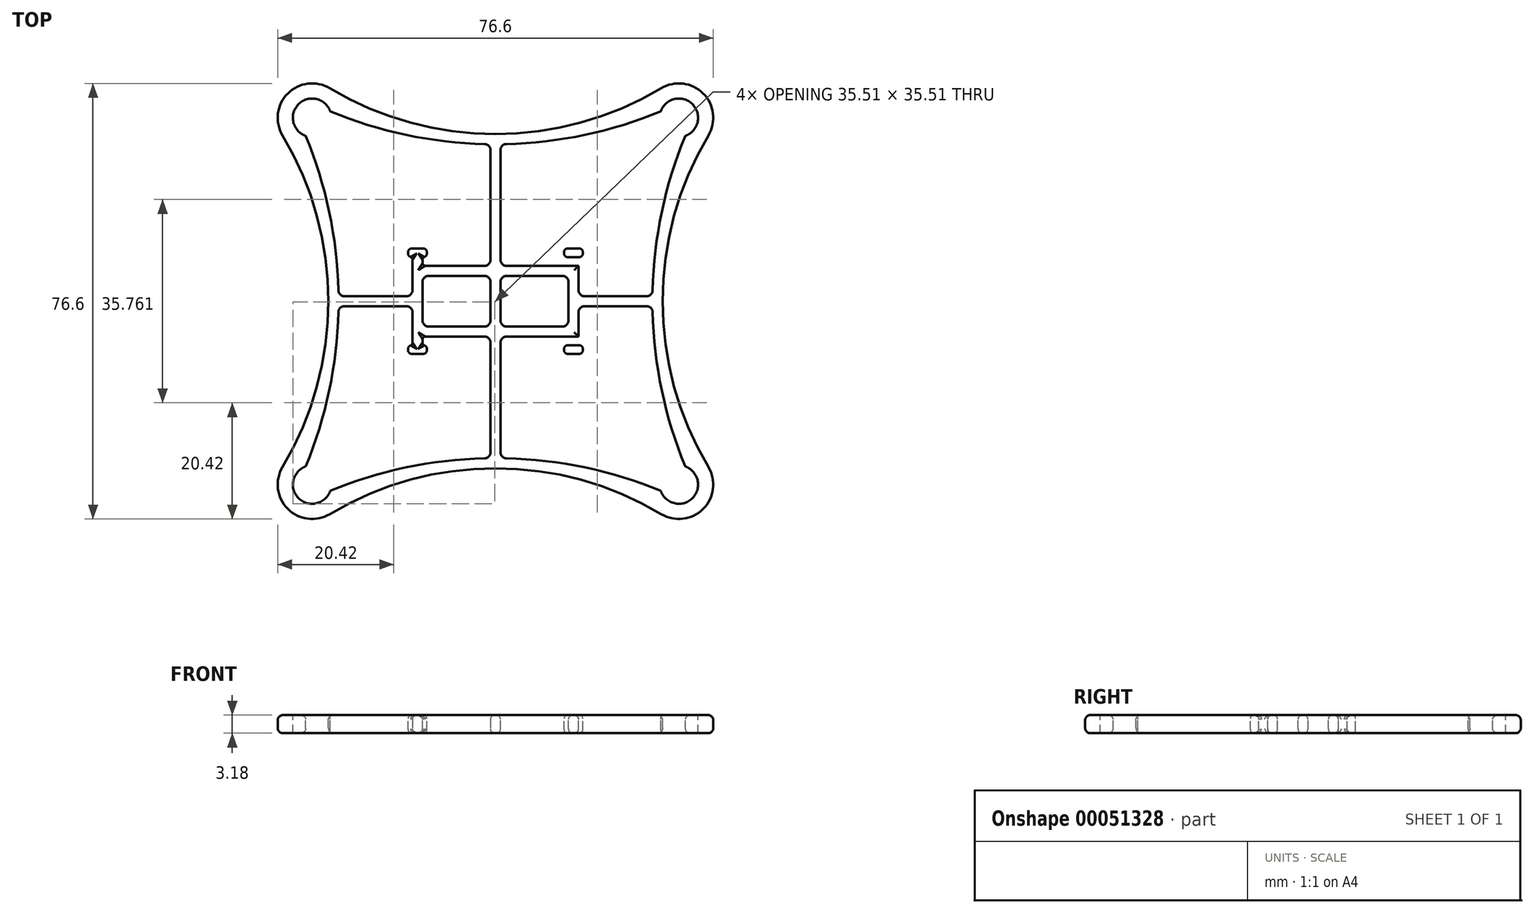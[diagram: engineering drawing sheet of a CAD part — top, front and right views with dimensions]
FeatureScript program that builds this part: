
annotation { "Feature Type Name" : "Feature", "Feature Type Description" : "" }
export const myFeature = defineFeature(function(context is Context, id is Id, definition is map)
    precondition{}
    {
        {
            var Q0;
            Q0=qCreatedBy(makeId("Top.planeOp"),FACE);
            var sketch = newSketch(context, id + "F0", { "sketchPlane" : qUnion([Q0])});
            skCircle(sketch, "E0", {"center": v(-32.26, 32.26) * mm, "radius": 3.38 * mm});
            skCircle(sketch, "E1", {"center": v(32.26, 32.26) * mm, "radius": 3.38 * mm});
            skCircle(sketch, "E2", {"center": v(32.26, -32.26) * mm, "radius": 3.38 * mm});
            skCircle(sketch, "E3", {"center": v(-32.26, -32.26) * mm, "radius": 3.38 * mm});
            skCircle(sketch, "E4", {"center": v(-32.26, 32.26) * mm, "radius": 6.05 * mm});
            skCircle(sketch, "E5", {"center": v(-32.26, -32.26) * mm, "radius": 6.05 * mm});
            skCircle(sketch, "E6", {"center": v(32.26, -32.26) * mm, "radius": 6.05 * mm});
            skCircle(sketch, "E7", {"center": v(32.26, 32.26) * mm, "radius": 6.05 * mm});
            skCircle(sketch, "E8", {"center": v(-103.8, 0) * mm, "radius": 76.2 * mm});
            skCircle(sketch, "E9", {"center": v(-86.16, 0) * mm, "radius": 56.77 * mm});
            skCircle(sketch, "E10", {"center": v(0, 103.8) * mm, "radius": 76.2 * mm});
            skCircle(sketch, "E11", {"center": v(0, 86.16) * mm, "radius": 56.77 * mm});
            skCircle(sketch, "E12", {"center": v(103.8, 0) * mm, "radius": 76.2 * mm});
            skCircle(sketch, "E13", {"center": v(86.16, 0) * mm, "radius": 56.77 * mm});
            skCircle(sketch, "E14", {"center": v(0, -103.8) * mm, "radius": 76.2 * mm});
            skCircle(sketch, "E15", {"center": v(0, -86.16) * mm, "radius": 56.77 * mm});
            skPoint(sketch, "E16.rect.middle", {"position": v(0, 0) * mm});
            skLineSegment(sketch, "E17.rect.bottom", {"start": v(14.6, 6.22) * mm, "end": v(-14.6, 6.22) * mm});
            skLineSegment(sketch, "E17.rect.top", {"start": v(14.6, -6.22) * mm, "end": v(-14.6, -6.22) * mm});
            skLineSegment(sketch, "E17.rect.left", {"start": v(14.6, 6.22) * mm, "end": v(14.6, -6.22) * mm});
            skLineSegment(sketch, "E17.rect.right", {"start": v(-14.6, 6.22) * mm, "end": v(-14.6, -6.22) * mm});
            skLineSegment(sketch, "E18.rect.bottom", {"start": v(12.83, 4.44) * mm, "end": v(-12.83, 4.45) * mm});
            skLineSegment(sketch, "E18.rect.top", {"start": v(12.83, -4.45) * mm, "end": v(-12.83, -4.44) * mm});
            skLineSegment(sketch, "E18.rect.left", {"start": v(12.83, 4.44) * mm, "end": v(12.83, -4.45) * mm});
            skLineSegment(sketch, "E18.rect.right", {"start": v(-12.83, 4.45) * mm, "end": v(-12.83, -4.44) * mm});
            skLineSegment(sketch, "E19.rect.bottom", {"start": v(0.89, 29.4) * mm, "end": v(-0.89, 29.4) * mm});
            skLineSegment(sketch, "E19.rect.top", {"start": v(0.89, -29.4) * mm, "end": v(-0.89, -29.4) * mm});
            skLineSegment(sketch, "E19.rect.left", {"start": v(0.89, 29.4) * mm, "end": v(0.89, -29.4) * mm});
            skLineSegment(sketch, "E19.rect.right", {"start": v(-0.89, 29.4) * mm, "end": v(-0.89, -29.4) * mm});
            skLineSegment(sketch, "E20.rect.bottom", {"start": v(29.4, 0.89) * mm, "end": v(-29.4, 0.89) * mm});
            skLineSegment(sketch, "E20.rect.top", {"start": v(29.4, -0.89) * mm, "end": v(-29.4, -0.89) * mm});
            skLineSegment(sketch, "E20.rect.left", {"start": v(29.4, 0.89) * mm, "end": v(29.4, -0.89) * mm});
            skLineSegment(sketch, "E20.rect.right", {"start": v(-29.4, 0.89) * mm, "end": v(-29.4, -0.89) * mm});
            skLineSegment(sketch, "E21.left", {"start": v(14.6, 6.22) * mm, "end": v(14.6, 6.22) * mm});
            skLineSegment(sketch, "E22.left", {"start": v(14.6, -6.22) * mm, "end": v(14.6, -6.22) * mm});
            skLineSegment(sketch, "E23.bottom", {"start": v(-14.6, 6.22) * mm, "end": v(-12.83, 6.22) * mm});
            skLineSegment(sketch, "E23.top", {"start": v(-14.6, 8.5) * mm, "end": v(-12.83, 8.5) * mm});
            skLineSegment(sketch, "E23.left", {"start": v(-14.6, 6.22) * mm, "end": v(-14.6, 8.5) * mm});
            skLineSegment(sketch, "E23.right", {"start": v(-12.83, 6.22) * mm, "end": v(-12.83, 8.5) * mm});
            skLineSegment(sketch, "E24.bottom", {"start": v(-14.6, -6.22) * mm, "end": v(-12.83, -6.22) * mm});
            skLineSegment(sketch, "E24.top", {"start": v(-14.6, -8.5) * mm, "end": v(-12.83, -8.5) * mm});
            skLineSegment(sketch, "E24.left", {"start": v(-14.6, -6.22) * mm, "end": v(-14.6, -8.5) * mm});
            skLineSegment(sketch, "E24.right", {"start": v(-12.83, -6.22) * mm, "end": v(-12.83, -8.5) * mm});
            skLineSegment(sketch, "E25.bottom", {"start": v(14.6, -6.22) * mm, "end": v(12.83, -6.22) * mm});
            skLineSegment(sketch, "E25.top", {"start": v(14.6, -8.5) * mm, "end": v(12.83, -8.5) * mm});
            skLineSegment(sketch, "E25.left", {"start": v(14.6, -6.22) * mm, "end": v(14.6, -8.5) * mm});
            skLineSegment(sketch, "E25.right", {"start": v(12.83, -6.22) * mm, "end": v(12.83, -8.5) * mm});
            skLineSegment(sketch, "E26.bottom", {"start": v(14.6, 6.22) * mm, "end": v(12.83, 6.22) * mm});
            skLineSegment(sketch, "E26.top", {"start": v(14.6, 8.5) * mm, "end": v(12.83, 8.5) * mm});
            skLineSegment(sketch, "E26.left", {"start": v(14.6, 6.22) * mm, "end": v(14.6, 8.5) * mm});
            skLineSegment(sketch, "E26.right", {"start": v(12.83, 6.22) * mm, "end": v(12.83, 8.5) * mm});
            skLineSegment(sketch, "E27.rect.bottom", {"start": v(-12.06, 9.27) * mm, "end": v(-15.37, 9.27) * mm});
            skLineSegment(sketch, "E27.rect.top", {"start": v(-12.06, 7.75) * mm, "end": v(-15.37, 7.75) * mm});
            skLineSegment(sketch, "E27.rect.left", {"start": v(-12.06, 9.27) * mm, "end": v(-12.06, 7.75) * mm});
            skLineSegment(sketch, "E27.rect.right", {"start": v(-15.37, 9.27) * mm, "end": v(-15.37, 7.75) * mm});
            skPoint(sketch, "E27.rect.middle", {"position": v(-13.72, 8.5) * mm});
            skLineSegment(sketch, "E28.rect.bottom", {"start": v(12.07, 9.27) * mm, "end": v(15.37, 9.27) * mm});
            skLineSegment(sketch, "E28.rect.top", {"start": v(12.07, 7.75) * mm, "end": v(15.37, 7.75) * mm});
            skLineSegment(sketch, "E28.rect.left", {"start": v(12.07, 9.27) * mm, "end": v(12.07, 7.75) * mm});
            skLineSegment(sketch, "E28.rect.right", {"start": v(15.37, 9.27) * mm, "end": v(15.37, 7.75) * mm});
            skPoint(sketch, "E28.rect.middle", {"position": v(13.72, 8.5) * mm});
            skLineSegment(sketch, "E29.rect.bottom", {"start": v(12.07, -7.75) * mm, "end": v(15.37, -7.75) * mm});
            skLineSegment(sketch, "E29.rect.top", {"start": v(12.07, -9.27) * mm, "end": v(15.37, -9.27) * mm});
            skLineSegment(sketch, "E29.rect.left", {"start": v(12.07, -7.75) * mm, "end": v(12.07, -9.27) * mm});
            skLineSegment(sketch, "E29.rect.right", {"start": v(15.37, -7.75) * mm, "end": v(15.37, -9.27) * mm});
            skPoint(sketch, "E29.rect.middle", {"position": v(13.72, -8.5) * mm});
            skLineSegment(sketch, "E30.rect.bottom", {"start": v(-12.06, -9.27) * mm, "end": v(-15.37, -9.27) * mm});
            skLineSegment(sketch, "E30.rect.top", {"start": v(-12.06, -7.75) * mm, "end": v(-15.37, -7.75) * mm});
            skLineSegment(sketch, "E30.rect.left", {"start": v(-12.06, -9.27) * mm, "end": v(-12.06, -7.75) * mm});
            skLineSegment(sketch, "E30.rect.right", {"start": v(-15.37, -9.27) * mm, "end": v(-15.37, -7.75) * mm});
            skPoint(sketch, "E30.rect.middle", {"position": v(-13.72, -8.5) * mm});
            skSolve(sketch);
        }
        {
            var Q0;
            {var subQ3=sQuery(id+"F0.wireOp",EDGE,"E4");var subQ5=sQuery(id+"F0.wireOp",EDGE,"E9");var subQ7=makeQuery(id+"F0.imprint","INTERSECT",VERTEX,{"derivedFrom":[subQ3,subQ5]});Q0=makeQuery(id+"F0.imprint","IMPRINT",FACE,{"disambiguationData":[TD([[makeQuery(id+"F0.imprint","IMPRINT",EDGE,{"disambiguationData":[TD([[subQ7,-1.0]])],"derivedFrom":subQ3}),-1.0]])]});}
            var Q1;
            {var subQ0=sQuery(id+"F0.wireOp",EDGE,"E8");var subQ1=sQuery(id+"F0.wireOp",EDGE,"E0");var subQ2=makeQuery(id+"F0.imprint","INTERSECT",VERTEX,{"disambiguationData":[OD(0.0)],"derivedFrom":[subQ1,subQ0]});Q1=makeQuery(id+"F0.imprint","IMPRINT",FACE,{"disambiguationData":[TD([[makeQuery(id+"F0.imprint","IMPRINT",EDGE,{"disambiguationData":[TD([[subQ2,-1.0]])],"derivedFrom":subQ1}),-1.0]])]});}
            var Q2;
            {var subQ0=sQuery(id+"F0.wireOp",EDGE,"E10");var subQ1=sQuery(id+"F0.wireOp",EDGE,"E0");var subQ2=makeQuery(id+"F0.imprint","INTERSECT",VERTEX,{"disambiguationData":[OD(0.0)],"derivedFrom":[subQ1,subQ0]});Q2=makeQuery(id+"F0.imprint","IMPRINT",FACE,{"disambiguationData":[TD([[makeQuery(id+"F0.imprint","IMPRINT",EDGE,{"disambiguationData":[TD([[subQ2,-1.0]])],"derivedFrom":subQ1}),-1.0]])]});}
            var Q3;
            {var subQ0=sQuery(id+"F0.wireOp",EDGE,"E0");var subQ1=sQuery(id+"F0.wireOp",EDGE,"E10");var subQ3=makeQuery(id+"F0.imprint","INTERSECT",VERTEX,{"disambiguationData":[OD(0.0)],"derivedFrom":[subQ0,subQ1]});Q3=makeQuery(id+"F0.imprint","IMPRINT",FACE,{"disambiguationData":[TD([[makeQuery(id+"F0.imprint","IMPRINT",EDGE,{"disambiguationData":[TD([[subQ3,1.0]])],"derivedFrom":subQ0}),-1.0]])]});}
            var Q4;
            {var subQ0=sQuery(id+"F0.wireOp",EDGE,"E11");var subQ3=sQuery(id+"F0.wireOp",EDGE,"E4");var subQ4=makeQuery(id+"F0.imprint","INTERSECT",VERTEX,{"derivedFrom":[subQ3,subQ0]});Q4=makeQuery(id+"F0.imprint","IMPRINT",FACE,{"disambiguationData":[TD([[makeQuery(id+"F0.imprint","IMPRINT",EDGE,{"disambiguationData":[TD([[subQ4,1.0]])],"derivedFrom":subQ3}),-1.0]])]});}
            var Q5;
            {var subQ0=sQuery(id+"F0.wireOp",EDGE,"E10");var subQ1=sQuery(id+"F0.wireOp",EDGE,"E1");var subQ5=makeQuery(id+"F0.imprint","INTERSECT",VERTEX,{"disambiguationData":[OD(0.0)],"derivedFrom":[subQ1,subQ0]});Q5=makeQuery(id+"F0.imprint","IMPRINT",FACE,{"disambiguationData":[TD([[makeQuery(id+"F0.imprint","IMPRINT",EDGE,{"disambiguationData":[TD([[subQ5,1.0]])],"derivedFrom":subQ1}),-1.0]])]});}
            var Q6;
            {var subQ1=sQuery(id+"F0.wireOp",EDGE,"E1");var subQ5=sQuery(id+"F0.wireOp",EDGE,"E10");var subQ6=makeQuery(id+"F0.imprint","INTERSECT",VERTEX,{"disambiguationData":[OD(1.0)],"derivedFrom":[subQ1,subQ5]});Q6=makeQuery(id+"F0.imprint","IMPRINT",FACE,{"disambiguationData":[TD([[makeQuery(id+"F0.imprint","IMPRINT",EDGE,{"disambiguationData":[TD([[subQ6,1.0]])],"derivedFrom":subQ1}),-1.0]])]});}
            var Q7;
            {var subQ0=sQuery(id+"F0.wireOp",EDGE,"E12");var subQ3=sQuery(id+"F0.wireOp",EDGE,"E1");var subQ4=makeQuery(id+"F0.imprint","INTERSECT",VERTEX,{"disambiguationData":[OD(0.0)],"derivedFrom":[subQ3,subQ0]});Q7=makeQuery(id+"F0.imprint","IMPRINT",FACE,{"disambiguationData":[TD([[makeQuery(id+"F0.imprint","IMPRINT",EDGE,{"disambiguationData":[TD([[subQ4,-1.0]])],"derivedFrom":subQ3}),-1.0]])]});}
            var Q8;
            {var subQ0=sQuery(id+"F0.wireOp",EDGE,"E12");var subQ1=sQuery(id+"F0.wireOp",EDGE,"E2");var subQ5=makeQuery(id+"F0.imprint","INTERSECT",VERTEX,{"disambiguationData":[OD(0.0)],"derivedFrom":[subQ1,subQ0]});Q8=makeQuery(id+"F0.imprint","IMPRINT",FACE,{"disambiguationData":[TD([[makeQuery(id+"F0.imprint","IMPRINT",EDGE,{"disambiguationData":[TD([[subQ5,1.0]])],"derivedFrom":subQ1}),-1.0]])]});}
            var Q9;
            {var subQ0=sQuery(id+"F0.wireOp",EDGE,"E12");var subQ1=sQuery(id+"F0.wireOp",EDGE,"E2");var subQ2=makeQuery(id+"F0.imprint","INTERSECT",VERTEX,{"disambiguationData":[OD(1.0)],"derivedFrom":[subQ1,subQ0]});Q9=makeQuery(id+"F0.imprint","IMPRINT",FACE,{"disambiguationData":[TD([[makeQuery(id+"F0.imprint","IMPRINT",EDGE,{"disambiguationData":[TD([[subQ2,1.0]])],"derivedFrom":subQ1}),-1.0]])]});}
            var Q10;
            {var subQ0=sQuery(id+"F0.wireOp",EDGE,"E14");var subQ3=sQuery(id+"F0.wireOp",EDGE,"E2");var subQ4=makeQuery(id+"F0.imprint","INTERSECT",VERTEX,{"disambiguationData":[OD(0.0)],"derivedFrom":[subQ3,subQ0]});Q10=makeQuery(id+"F0.imprint","IMPRINT",FACE,{"disambiguationData":[TD([[makeQuery(id+"F0.imprint","IMPRINT",EDGE,{"disambiguationData":[TD([[subQ4,-1.0]])],"derivedFrom":subQ3}),-1.0]])]});}
            var Q11;
            {var subQ0=sQuery(id+"F0.wireOp",EDGE,"E3");var subQ1=sQuery(id+"F0.wireOp",EDGE,"E14");var subQ3=makeQuery(id+"F0.imprint","INTERSECT",VERTEX,{"disambiguationData":[OD(0.0)],"derivedFrom":[subQ0,subQ1]});Q11=makeQuery(id+"F0.imprint","IMPRINT",FACE,{"disambiguationData":[TD([[makeQuery(id+"F0.imprint","IMPRINT",EDGE,{"disambiguationData":[TD([[subQ3,-1.0]])],"derivedFrom":subQ0}),-1.0]])]});}
            var Q12;
            {var subQ1=sQuery(id+"F0.wireOp",EDGE,"E3");var subQ5=sQuery(id+"F0.wireOp",EDGE,"E8");var subQ7=makeQuery(id+"F0.imprint","INTERSECT",VERTEX,{"disambiguationData":[OD(0.0)],"derivedFrom":[subQ1,subQ5]});Q12=makeQuery(id+"F0.imprint","IMPRINT",FACE,{"disambiguationData":[TD([[makeQuery(id+"F0.imprint","IMPRINT",EDGE,{"disambiguationData":[TD([[subQ7,-1.0]])],"derivedFrom":subQ1}),-1.0]])]});}
            var Q13;
            {var subQ0=sQuery(id+"F0.wireOp",EDGE,"E8");var subQ3=sQuery(id+"F0.wireOp",EDGE,"E3");var subQ5=makeQuery(id+"F0.imprint","INTERSECT",VERTEX,{"disambiguationData":[OD(0.0)],"derivedFrom":[subQ3,subQ0]});Q13=makeQuery(id+"F0.imprint","IMPRINT",FACE,{"disambiguationData":[TD([[makeQuery(id+"F0.imprint","IMPRINT",EDGE,{"disambiguationData":[TD([[subQ5,1.0]])],"derivedFrom":subQ3}),-1.0]])]});}
            var Q14;
            {var subQ0=sQuery(id+"F0.wireOp",EDGE,"E12");var subQ3=sQuery(id+"F0.wireOp",EDGE,"E1");var subQ6=makeQuery(id+"F0.imprint","INTERSECT",VERTEX,{"disambiguationData":[OD(0.0)],"derivedFrom":[subQ3,subQ0]});Q14=makeQuery(id+"F0.imprint","IMPRINT",FACE,{"disambiguationData":[TD([[makeQuery(id+"F0.imprint","IMPRINT",EDGE,{"disambiguationData":[TD([[subQ6,1.0]])],"derivedFrom":subQ3}),-1.0]])]});}
            var Q15;
            {var subQ3=sQuery(id+"F0.wireOp",EDGE,"E6");var subQ5=sQuery(id+"F0.wireOp",EDGE,"E12");var subQ7=makeQuery(id+"F0.imprint","INTERSECT",VERTEX,{"disambiguationData":[OD(0.0)],"derivedFrom":[subQ3,subQ5]});Q15=makeQuery(id+"F0.imprint","IMPRINT",FACE,{"disambiguationData":[TD([[makeQuery(id+"F0.imprint","IMPRINT",EDGE,{"disambiguationData":[TD([[subQ7,1.0]])],"derivedFrom":subQ3}),-1.0]])]});}
            var Q16;
            {var subQ0=sQuery(id+"F0.wireOp",EDGE,"97792d4c-2e40-4aaa-a942-c1651c489ece.rect.left");var subQ6=sQuery(id+"F0.wireOp",EDGE,"E17.rect.bottom");var subQ7=makeQuery(id+"F0.imprint","INTERSECT",VERTEX,{"derivedFrom":[subQ0,subQ6]});Q16=makeQuery(id+"F0.imprint","IMPRINT",FACE,{"disambiguationData":[TD([[makeQuery(id+"F0.imprint","IMPRINT",EDGE,{"disambiguationData":[TD([[subQ7,-1.0]])],"derivedFrom":subQ6}),-1.0]])]});}
            var Q17;
            {var subQ3=sQuery(id+"F0.wireOp",EDGE,"E16.rect.bottom");var subQ9=sQuery(id+"F0.wireOp",EDGE,"E18.rect.right");var subQ11=makeQuery(id+"F0.imprint","INTERSECT",VERTEX,{"derivedFrom":[subQ3,subQ9]});Q17=makeQuery(id+"F0.imprint","IMPRINT",FACE,{"disambiguationData":[TD([[makeQuery(id+"F0.imprint","IMPRINT",EDGE,{"disambiguationData":[TD([[subQ11,-1.0]])],"derivedFrom":subQ3}),-1.0]])]});}
            var Q18;
            {var subQ0=sQuery(id+"F0.wireOp",EDGE,"E17.rect.bottom");var subQ1=sQuery(id+"F0.wireOp",EDGE,"97792d4c-2e40-4aaa-a942-c1651c489ece.rect.left");var subQ2=makeQuery(id+"F0.imprint","INTERSECT",VERTEX,{"derivedFrom":[subQ1,subQ0]});Q18=makeQuery(id+"F0.imprint","IMPRINT",FACE,{"disambiguationData":[TD([[makeQuery(id+"F0.imprint","IMPRINT",EDGE,{"disambiguationData":[TD([[subQ2,-1.0]])],"derivedFrom":subQ1}),-1.0]])]});}
            var Q19;
            {var subQ0=sQuery(id+"F0.wireOp",EDGE,"E17.rect.left");var subQ3=sQuery(id+"F0.wireOp",EDGE,"E16.rect.bottom");var subQ4=makeQuery(id+"F0.imprint","INTERSECT",VERTEX,{"derivedFrom":[subQ3,subQ0]});Q19=makeQuery(id+"F0.imprint","IMPRINT",FACE,{"disambiguationData":[TD([[makeQuery(id+"F0.imprint","IMPRINT",EDGE,{"disambiguationData":[TD([[subQ4,-1.0]])],"derivedFrom":subQ3}),-1.0]])]});}
            var Q20;
            {var subQ0=sQuery(id+"F0.wireOp",EDGE,"E17.rect.left");var subQ1=sQuery(id+"F0.wireOp",EDGE,"E16.rect.bottom");var subQ2=makeQuery(id+"F0.imprint","INTERSECT",VERTEX,{"derivedFrom":[subQ1,subQ0]});Q20=makeQuery(id+"F0.imprint","IMPRINT",FACE,{"disambiguationData":[TD([[makeQuery(id+"F0.imprint","IMPRINT",EDGE,{"disambiguationData":[TD([[subQ2,-1.0]])],"derivedFrom":subQ1}),1.0]])]});}
            var Q21;
            {var subQ0=sQuery(id+"F0.wireOp",EDGE,"E17.rect.left");var subQ3=sQuery(id+"F0.wireOp",EDGE,"E16.rect.top");var subQ4=makeQuery(id+"F0.imprint","INTERSECT",VERTEX,{"derivedFrom":[subQ3,subQ0]});Q21=makeQuery(id+"F0.imprint","IMPRINT",FACE,{"disambiguationData":[TD([[makeQuery(id+"F0.imprint","IMPRINT",EDGE,{"disambiguationData":[TD([[subQ4,-1.0]])],"derivedFrom":subQ3}),1.0]])]});}
            var Q22;
            {var subQ0=sQuery(id+"F0.wireOp",EDGE,"E18.rect.top");var subQ1=sQuery(id+"F0.wireOp",EDGE,"97792d4c-2e40-4aaa-a942-c1651c489ece.rect.left");var subQ2=makeQuery(id+"F0.imprint","INTERSECT",VERTEX,{"derivedFrom":[subQ1,subQ0]});Q22=makeQuery(id+"F0.imprint","IMPRINT",FACE,{"disambiguationData":[TD([[makeQuery(id+"F0.imprint","IMPRINT",EDGE,{"disambiguationData":[TD([[subQ2,-1.0]])],"derivedFrom":subQ1}),-1.0]])]});}
            var Q23;
            {var subQ5=sQuery(id+"F0.wireOp",EDGE,"E16.rect.top");var subQ9=sQuery(id+"F0.wireOp",EDGE,"E18.rect.right");var subQ11=makeQuery(id+"F0.imprint","INTERSECT",VERTEX,{"derivedFrom":[subQ5,subQ9]});Q23=makeQuery(id+"F0.imprint","IMPRINT",FACE,{"disambiguationData":[TD([[makeQuery(id+"F0.imprint","IMPRINT",EDGE,{"disambiguationData":[TD([[subQ11,-1.0]])],"derivedFrom":subQ5}),1.0]])]});}
            var Q24;
            {var subQ0=sQuery(id+"F0.wireOp",EDGE,"E18.rect.right");var subQ1=sQuery(id+"F0.wireOp",EDGE,"E16.rect.bottom");var subQ2=makeQuery(id+"F0.imprint","INTERSECT",VERTEX,{"derivedFrom":[subQ1,subQ0]});Q24=makeQuery(id+"F0.imprint","IMPRINT",FACE,{"disambiguationData":[TD([[makeQuery(id+"F0.imprint","IMPRINT",EDGE,{"disambiguationData":[TD([[subQ2,-1.0]])],"derivedFrom":subQ1}),1.0]])]});}
            var Q25;
            {var subQ1=sQuery(id+"F0.wireOp",EDGE,"E16.rect.bottom");var subQ6=sQuery(id+"F0.wireOp",EDGE,"E17.rect.right");var subQ7=makeQuery(id+"F0.imprint","INTERSECT",VERTEX,{"derivedFrom":[subQ1,subQ6]});Q25=makeQuery(id+"F0.imprint","IMPRINT",FACE,{"disambiguationData":[TD([[makeQuery(id+"F0.imprint","IMPRINT",EDGE,{"disambiguationData":[TD([[subQ7,-1.0]])],"derivedFrom":subQ6}),-1.0]])]});}
            var Q26;
            {var subQ1=sQuery(id+"F0.wireOp",EDGE,"E16.rect.bottom");var subQ6=sQuery(id+"F0.wireOp",EDGE,"E17.rect.left");var subQ7=makeQuery(id+"F0.imprint","INTERSECT",VERTEX,{"derivedFrom":[subQ1,subQ6]});Q26=makeQuery(id+"F0.imprint","IMPRINT",FACE,{"disambiguationData":[TD([[makeQuery(id+"F0.imprint","IMPRINT",EDGE,{"disambiguationData":[TD([[subQ7,-1.0]])],"derivedFrom":subQ6}),1.0]])]});}
            var Q27;
            {var subQ0=sQuery(id+"F0.wireOp",EDGE,"97792d4c-2e40-4aaa-a942-c1651c489ece.rect.left");var subQ6=sQuery(id+"F0.wireOp",EDGE,"E17.rect.top");var subQ7=makeQuery(id+"F0.imprint","INTERSECT",VERTEX,{"derivedFrom":[subQ0,subQ6]});Q27=makeQuery(id+"F0.imprint","IMPRINT",FACE,{"disambiguationData":[TD([[makeQuery(id+"F0.imprint","IMPRINT",EDGE,{"disambiguationData":[TD([[subQ7,-1.0]])],"derivedFrom":subQ6}),1.0]])]});}
            var Q28;
            Q28=makeQuery(id+"F0.imprint","IMPRINT",FACE,{"disambiguationData":[TD([[makeQuery(id+"F0.imprint","IMPRINT",EDGE,{"derivedFrom":sQuery(id+"F0.wireOp",EDGE,"de616939-67df-4de1-98a8-b123298b16c6.bottom")}),-1.0]])]});
            var Q29;
            Q29=makeQuery(id+"F0.imprint","IMPRINT",FACE,{"disambiguationData":[TD([[makeQuery(id+"F0.imprint","IMPRINT",EDGE,{"derivedFrom":sQuery(id+"F0.wireOp",EDGE,"6e18662c-c205-4df8-b961-8c52012f615d.bottom")}),1.0]])]});
            var Q30;
            Q30=makeQuery(id+"F0.imprint","IMPRINT",FACE,{"disambiguationData":[TD([[makeQuery(id+"F0.imprint","IMPRINT",EDGE,{"derivedFrom":sQuery(id+"F0.wireOp",EDGE,"e5e8593a-10a3-4d83-983c-bc6820abb37f.bottom")}),-1.0]])]});
            var Q31;
            Q31=makeQuery(id+"F0.imprint","IMPRINT",FACE,{"disambiguationData":[TD([[makeQuery(id+"F0.imprint","IMPRINT",EDGE,{"derivedFrom":sQuery(id+"F0.wireOp",EDGE,"fe4e9a62-022c-4ccf-87c7-29a0906fb106.bottom")}),1.0]])]});
            var Q32;
            {var subQ0=sQuery(id+"F0.wireOp",EDGE,"E20.rect.bottom");var subQ1=sQuery(id+"F0.wireOp",EDGE,"E8");var subQ2=makeQuery(id+"F0.imprint","INTERSECT",VERTEX,{"derivedFrom":[subQ1,subQ0]});Q32=makeQuery(id+"F0.imprint","IMPRINT",FACE,{"disambiguationData":[TD([[makeQuery(id+"F0.imprint","IMPRINT",EDGE,{"disambiguationData":[TD([[subQ2,1.0]])],"derivedFrom":subQ1}),1.0]])]});}
            var Q33;
            {var subQ0=sQuery(id+"F0.wireOp",EDGE,"E8");var subQ1=sQuery(id+"F0.wireOp",EDGE,"E5");var subQ2=makeQuery(id+"F0.imprint","INTERSECT",VERTEX,{"disambiguationData":[OD(0.0)],"derivedFrom":[subQ1,subQ0]});Q33=makeQuery(id+"F0.imprint","IMPRINT",FACE,{"disambiguationData":[TD([[makeQuery(id+"F0.imprint","IMPRINT",EDGE,{"disambiguationData":[TD([[subQ2,-1.0]])],"derivedFrom":subQ1}),-1.0]])]});}
            var Q34;
            {var subQ0=sQuery(id+"F0.wireOp",EDGE,"E19.rect.left");var subQ1=sQuery(id+"F0.wireOp",EDGE,"E14");var subQ2=makeQuery(id+"F0.imprint","INTERSECT",VERTEX,{"derivedFrom":[subQ1,subQ0]});Q34=makeQuery(id+"F0.imprint","IMPRINT",FACE,{"disambiguationData":[TD([[makeQuery(id+"F0.imprint","IMPRINT",EDGE,{"disambiguationData":[TD([[subQ2,-1.0]])],"derivedFrom":subQ1}),1.0]])]});}
            var Q35;
            {var subQ0=sQuery(id+"F0.wireOp",EDGE,"E14");var subQ1=sQuery(id+"F0.wireOp",EDGE,"E6");var subQ2=makeQuery(id+"F0.imprint","INTERSECT",VERTEX,{"disambiguationData":[OD(0.0)],"derivedFrom":[subQ1,subQ0]});Q35=makeQuery(id+"F0.imprint","IMPRINT",FACE,{"disambiguationData":[TD([[makeQuery(id+"F0.imprint","IMPRINT",EDGE,{"disambiguationData":[TD([[subQ2,-1.0]])],"derivedFrom":subQ1}),-1.0]])]});}
            var Q36;
            {var subQ0=sQuery(id+"F0.wireOp",EDGE,"E20.rect.bottom");var subQ1=sQuery(id+"F0.wireOp",EDGE,"E12");var subQ2=makeQuery(id+"F0.imprint","INTERSECT",VERTEX,{"derivedFrom":[subQ1,subQ0]});Q36=makeQuery(id+"F0.imprint","IMPRINT",FACE,{"disambiguationData":[TD([[makeQuery(id+"F0.imprint","IMPRINT",EDGE,{"disambiguationData":[TD([[subQ2,-1.0]])],"derivedFrom":subQ1}),1.0]])]});}
            var Q37;
            {var subQ7=sQuery(id+"F0.wireOp",EDGE,"E17.rect.left");var subQ8=sQuery(id+"F0.wireOp",EDGE,"E17.rect.top");var subQ9=makeQuery(id+"F0.imprint","INTERSECT",VERTEX,{"derivedFrom":[subQ8,subQ7]});Q37=makeQuery(id+"F0.imprint","IMPRINT",FACE,{"disambiguationData":[TD([[makeQuery(id+"F0.imprint","IMPRINT",EDGE,{"disambiguationData":[TD([[subQ9,-1.0]])],"derivedFrom":subQ8}),-1.0]])]});}
            var Q38;
            {var subQ0=sQuery(id+"F0.wireOp",EDGE,"E19.rect.left");var subQ1=sQuery(id+"F0.wireOp",EDGE,"E17.rect.top");var subQ2=makeQuery(id+"F0.imprint","INTERSECT",VERTEX,{"derivedFrom":[subQ1,subQ0]});Q38=makeQuery(id+"F0.imprint","IMPRINT",FACE,{"disambiguationData":[TD([[makeQuery(id+"F0.imprint","IMPRINT",EDGE,{"disambiguationData":[TD([[subQ2,-1.0]])],"derivedFrom":subQ1}),-1.0]])]});}
            var Q39;
            {var subQ5=sQuery(id+"F0.wireOp",EDGE,"E17.rect.top");var subQ7=sQuery(id+"F0.wireOp",EDGE,"E17.rect.right");var subQ8=makeQuery(id+"F0.imprint","INTERSECT",VERTEX,{"derivedFrom":[subQ5,subQ7]});Q39=makeQuery(id+"F0.imprint","IMPRINT",FACE,{"disambiguationData":[TD([[makeQuery(id+"F0.imprint","IMPRINT",EDGE,{"disambiguationData":[TD([[subQ8,1.0]])],"derivedFrom":subQ5}),-1.0]])]});}
            var Q40;
            {var subQ0=sQuery(id+"F0.wireOp",EDGE,"E20.rect.bottom");var subQ1=sQuery(id+"F0.wireOp",EDGE,"E17.rect.right");var subQ2=makeQuery(id+"F0.imprint","INTERSECT",VERTEX,{"derivedFrom":[subQ1,subQ0]});Q40=makeQuery(id+"F0.imprint","IMPRINT",FACE,{"disambiguationData":[TD([[makeQuery(id+"F0.imprint","IMPRINT",EDGE,{"disambiguationData":[TD([[subQ2,-1.0]])],"derivedFrom":subQ1}),1.0]])]});}
            var Q41;
            {var subQ7=sQuery(id+"F0.wireOp",EDGE,"E17.rect.right");var subQ8=sQuery(id+"F0.wireOp",EDGE,"E17.rect.bottom");var subQ9=makeQuery(id+"F0.imprint","INTERSECT",VERTEX,{"derivedFrom":[subQ8,subQ7]});Q41=makeQuery(id+"F0.imprint","IMPRINT",FACE,{"disambiguationData":[TD([[makeQuery(id+"F0.imprint","IMPRINT",EDGE,{"disambiguationData":[TD([[subQ9,1.0]])],"derivedFrom":subQ8}),1.0]])]});}
            var Q42;
            {var subQ7=sQuery(id+"F0.wireOp",EDGE,"E17.rect.left");var subQ8=sQuery(id+"F0.wireOp",EDGE,"E17.rect.bottom");var subQ9=makeQuery(id+"F0.imprint","INTERSECT",VERTEX,{"derivedFrom":[subQ8,subQ7]});Q42=makeQuery(id+"F0.imprint","IMPRINT",FACE,{"disambiguationData":[TD([[makeQuery(id+"F0.imprint","IMPRINT",EDGE,{"disambiguationData":[TD([[subQ9,-1.0]])],"derivedFrom":subQ8}),1.0]])]});}
            var Q43;
            {var subQ0=sQuery(id+"F0.wireOp",EDGE,"E20.rect.bottom");var subQ1=sQuery(id+"F0.wireOp",EDGE,"E17.rect.left");var subQ2=makeQuery(id+"F0.imprint","INTERSECT",VERTEX,{"derivedFrom":[subQ1,subQ0]});Q43=makeQuery(id+"F0.imprint","IMPRINT",FACE,{"disambiguationData":[TD([[makeQuery(id+"F0.imprint","IMPRINT",EDGE,{"disambiguationData":[TD([[subQ2,-1.0]])],"derivedFrom":subQ1}),-1.0]])]});}
            var Q44;
            {var subQ0=sQuery(id+"F0.wireOp",EDGE,"E12");var subQ1=sQuery(id+"F0.wireOp",EDGE,"E7");var subQ2=makeQuery(id+"F0.imprint","INTERSECT",VERTEX,{"disambiguationData":[OD(1.0)],"derivedFrom":[subQ1,subQ0]});Q44=makeQuery(id+"F0.imprint","IMPRINT",FACE,{"disambiguationData":[TD([[makeQuery(id+"F0.imprint","IMPRINT",EDGE,{"disambiguationData":[TD([[subQ2,-1.0]])],"derivedFrom":subQ1}),-1.0]])]});}
            var Q45;
            {var subQ0=sQuery(id+"F0.wireOp",EDGE,"E19.rect.left");var subQ1=sQuery(id+"F0.wireOp",EDGE,"E17.rect.bottom");var subQ2=makeQuery(id+"F0.imprint","INTERSECT",VERTEX,{"derivedFrom":[subQ1,subQ0]});Q45=makeQuery(id+"F0.imprint","IMPRINT",FACE,{"disambiguationData":[TD([[makeQuery(id+"F0.imprint","IMPRINT",EDGE,{"disambiguationData":[TD([[subQ2,-1.0]])],"derivedFrom":subQ1}),1.0]])]});}
            var Q46;
            {var subQ0=sQuery(id+"F0.wireOp",EDGE,"E19.rect.right");var subQ1=sQuery(id+"F0.wireOp",EDGE,"E10");var subQ2=makeQuery(id+"F0.imprint","INTERSECT",VERTEX,{"derivedFrom":[subQ1,subQ0]});Q46=makeQuery(id+"F0.imprint","IMPRINT",FACE,{"disambiguationData":[TD([[makeQuery(id+"F0.imprint","IMPRINT",EDGE,{"disambiguationData":[TD([[subQ2,-1.0]])],"derivedFrom":subQ1}),1.0]])]});}
            var Q47;
            {var subQ0=sQuery(id+"F0.wireOp",EDGE,"E11");var subQ1=sQuery(id+"F0.wireOp",EDGE,"E7");var subQ2=makeQuery(id+"F0.imprint","INTERSECT",VERTEX,{"derivedFrom":[subQ1,subQ0]});Q47=makeQuery(id+"F0.imprint","IMPRINT",FACE,{"disambiguationData":[TD([[makeQuery(id+"F0.imprint","IMPRINT",EDGE,{"disambiguationData":[TD([[subQ2,-1.0]])],"derivedFrom":subQ1}),-1.0]])]});}
            var Q48;
            {var subQ7=sQuery(id+"F0.wireOp",EDGE,"f8660cd2-9a3a-46cf-8541-a55b21bbf2a2.left");Q48=makeQuery(id+"F0.imprint","IMPRINT",FACE,{"disambiguationData":[TD([[makeQuery(id+"F0.imprint","IMPRINT",EDGE,{"derivedFrom":subQ7}),1.0]])]});}
            var Q49;
            Q49=makeQuery(id+"F0.imprint","IMPRINT",FACE,{"disambiguationData":[TD([[makeQuery(id+"F0.imprint","IMPRINT",EDGE,{"derivedFrom":sQuery(id+"F0.wireOp",EDGE,"f8660cd2-9a3a-46cf-8541-a55b21bbf2a2.bottom")}),1.0]])]});
            var Q50;
            Q50=makeQuery(id+"F0.imprint","IMPRINT",FACE,{"disambiguationData":[TD([[makeQuery(id+"F0.imprint","IMPRINT",EDGE,{"derivedFrom":sQuery(id+"F0.wireOp",EDGE,"2a5b0057-8150-4ec5-9247-2ce1087ea529.bottom")}),-1.0]])]});
            var Q51;
            {var subQ7=sQuery(id+"F0.wireOp",EDGE,"2a5b0057-8150-4ec5-9247-2ce1087ea529.left");Q51=makeQuery(id+"F0.imprint","IMPRINT",FACE,{"disambiguationData":[TD([[makeQuery(id+"F0.imprint","IMPRINT",EDGE,{"derivedFrom":subQ7}),-1.0]])]});}
            var Q52;
            {var subQ7=sQuery(id+"F0.wireOp",EDGE,"E22.left");Q52=makeQuery(id+"F0.imprint","IMPRINT",FACE,{"disambiguationData":[TD([[makeQuery(id+"F0.imprint","IMPRINT",EDGE,{"derivedFrom":subQ7}),1.0]])]});}
            var Q53;
            Q53=makeQuery(id+"F0.imprint","IMPRINT",FACE,{"disambiguationData":[TD([[makeQuery(id+"F0.imprint","IMPRINT",EDGE,{"derivedFrom":sQuery(id+"F0.wireOp",EDGE,"E22.bottom")}),1.0]])]});
            var Q54;
            {var subQ7=sQuery(id+"F0.wireOp",EDGE,"E21.left");Q54=makeQuery(id+"F0.imprint","IMPRINT",FACE,{"disambiguationData":[TD([[makeQuery(id+"F0.imprint","IMPRINT",EDGE,{"derivedFrom":subQ7}),-1.0]])]});}
            var Q55;
            Q55=makeQuery(id+"F0.imprint","IMPRINT",FACE,{"disambiguationData":[TD([[makeQuery(id+"F0.imprint","IMPRINT",EDGE,{"derivedFrom":sQuery(id+"F0.wireOp",EDGE,"920944db-2e94-47ff-9106-445efe642f17.bottom")}),-1.0]])]});
            var Q56;
            {var subQ7=sQuery(id+"F0.wireOp",EDGE,"E23.bottom");Q56=makeQuery(id+"F0.imprint","IMPRINT",FACE,{"disambiguationData":[TD([[makeQuery(id+"F0.imprint","IMPRINT",EDGE,{"derivedFrom":subQ7}),-1.0]])]});}
            var Q57;
            Q57=makeQuery(id+"F0.imprint","IMPRINT",FACE,{"disambiguationData":[TD([[makeQuery(id+"F0.imprint","IMPRINT",EDGE,{"derivedFrom":sQuery(id+"F0.wireOp",EDGE,"E23.bottom")}),1.0]])]});
            var Q58;
            Q58=makeQuery(id+"F0.imprint","IMPRINT",FACE,{"disambiguationData":[TD([[makeQuery(id+"F0.imprint","IMPRINT",EDGE,{"derivedFrom":sQuery(id+"F0.wireOp",EDGE,"E26.bottom")}),-1.0]])]});
            var Q59;
            {var subQ7=sQuery(id+"F0.wireOp",EDGE,"E26.bottom");Q59=makeQuery(id+"F0.imprint","IMPRINT",FACE,{"disambiguationData":[TD([[makeQuery(id+"F0.imprint","IMPRINT",EDGE,{"derivedFrom":subQ7}),1.0]])]});}
            var Q60;
            {var subQ7=sQuery(id+"F0.wireOp",EDGE,"E25.bottom");Q60=makeQuery(id+"F0.imprint","IMPRINT",FACE,{"disambiguationData":[TD([[makeQuery(id+"F0.imprint","IMPRINT",EDGE,{"derivedFrom":subQ7}),-1.0]])]});}
            var Q61;
            Q61=makeQuery(id+"F0.imprint","IMPRINT",FACE,{"disambiguationData":[TD([[makeQuery(id+"F0.imprint","IMPRINT",EDGE,{"derivedFrom":sQuery(id+"F0.wireOp",EDGE,"E25.bottom")}),1.0]])]});
            var Q62;
            {var subQ7=sQuery(id+"F0.wireOp",EDGE,"E24.bottom");Q62=makeQuery(id+"F0.imprint","IMPRINT",FACE,{"disambiguationData":[TD([[makeQuery(id+"F0.imprint","IMPRINT",EDGE,{"derivedFrom":subQ7}),1.0]])]});}
            var Q63;
            Q63=makeQuery(id+"F0.imprint","IMPRINT",FACE,{"disambiguationData":[TD([[makeQuery(id+"F0.imprint","IMPRINT",EDGE,{"derivedFrom":sQuery(id+"F0.wireOp",EDGE,"E24.bottom")}),-1.0]])]});
            var Q64;
            {var subQ1=sQuery(id+"F0.wireOp",EDGE,"E26.top");Q64=makeQuery(id+"F0.imprint","IMPRINT",FACE,{"disambiguationData":[TD([[makeQuery(id+"F0.imprint","IMPRINT",EDGE,{"derivedFrom":subQ1}),-1.0]])]});}
            var Q65;
            {var subQ0=sQuery(id+"F0.wireOp",EDGE,"E26.top");Q65=makeQuery(id+"F0.imprint","IMPRINT",FACE,{"disambiguationData":[TD([[makeQuery(id+"F0.imprint","IMPRINT",EDGE,{"derivedFrom":subQ0}),1.0]])]});}
            var Q66;
            {var subQ0=sQuery(id+"F0.wireOp",EDGE,"E25.top");Q66=makeQuery(id+"F0.imprint","IMPRINT",FACE,{"disambiguationData":[TD([[makeQuery(id+"F0.imprint","IMPRINT",EDGE,{"derivedFrom":subQ0}),-1.0]])]});}
            var Q67;
            {var subQ4=sQuery(id+"F0.wireOp",EDGE,"E25.top");Q67=makeQuery(id+"F0.imprint","IMPRINT",FACE,{"disambiguationData":[TD([[makeQuery(id+"F0.imprint","IMPRINT",EDGE,{"derivedFrom":subQ4}),1.0]])]});}
            var Q68;
            {var subQ1=sQuery(id+"F0.wireOp",EDGE,"E24.top");Q68=makeQuery(id+"F0.imprint","IMPRINT",FACE,{"disambiguationData":[TD([[makeQuery(id+"F0.imprint","IMPRINT",EDGE,{"derivedFrom":subQ1}),-1.0]])]});}
            var Q69;
            {var subQ0=sQuery(id+"F0.wireOp",EDGE,"E24.top");Q69=makeQuery(id+"F0.imprint","IMPRINT",FACE,{"disambiguationData":[TD([[makeQuery(id+"F0.imprint","IMPRINT",EDGE,{"derivedFrom":subQ0}),1.0]])]});}
            var Q70;
            {var subQ0=sQuery(id+"F0.wireOp",EDGE,"E23.top");Q70=makeQuery(id+"F0.imprint","IMPRINT",FACE,{"disambiguationData":[TD([[makeQuery(id+"F0.imprint","IMPRINT",EDGE,{"derivedFrom":subQ0}),-1.0]])]});}
            var Q71;
            {var subQ1=sQuery(id+"F0.wireOp",EDGE,"E23.top");Q71=makeQuery(id+"F0.imprint","IMPRINT",FACE,{"disambiguationData":[TD([[makeQuery(id+"F0.imprint","IMPRINT",EDGE,{"derivedFrom":subQ1}),1.0]])]});}
            var Q72;
            {var subQ0=sQuery(id+"F0.wireOp",EDGE,"E15");var subQ1=sQuery(id+"F0.wireOp",EDGE,"E5");var subQ2=makeQuery(id+"F0.imprint","INTERSECT",VERTEX,{"derivedFrom":[subQ1,subQ0]});Q72=makeQuery(id+"F0.imprint","IMPRINT",FACE,{"disambiguationData":[TD([[makeQuery(id+"F0.imprint","IMPRINT",EDGE,{"disambiguationData":[TD([[subQ2,-1.0]])],"derivedFrom":subQ1}),-1.0]])]});}
            var Q73;
            {var subQ0=sQuery(id+"F0.wireOp",EDGE,"E19.rect.left");var subQ1=sQuery(id+"F0.wireOp",EDGE,"E18.rect.top");var subQ2=makeQuery(id+"F0.imprint","INTERSECT",VERTEX,{"derivedFrom":[subQ1,subQ0]});Q73=makeQuery(id+"F0.imprint","IMPRINT",FACE,{"disambiguationData":[TD([[makeQuery(id+"F0.imprint","IMPRINT",EDGE,{"disambiguationData":[TD([[subQ2,-1.0]])],"derivedFrom":subQ1}),-1.0]])]});}
            var Q74;
            {var subQ0=sQuery(id+"F0.wireOp",EDGE,"E20.rect.bottom");var subQ1=sQuery(id+"F0.wireOp",EDGE,"E19.rect.left");var subQ2=makeQuery(id+"F0.imprint","INTERSECT",VERTEX,{"derivedFrom":[subQ1,subQ0]});Q74=makeQuery(id+"F0.imprint","IMPRINT",FACE,{"disambiguationData":[TD([[makeQuery(id+"F0.imprint","IMPRINT",EDGE,{"disambiguationData":[TD([[subQ2,-1.0]])],"derivedFrom":subQ1}),-1.0]])]});}
            var Q75;
            {var subQ0=sQuery(id+"F0.wireOp",EDGE,"E19.rect.left");var subQ1=sQuery(id+"F0.wireOp",EDGE,"E18.rect.bottom");var subQ2=makeQuery(id+"F0.imprint","INTERSECT",VERTEX,{"derivedFrom":[subQ1,subQ0]});Q75=makeQuery(id+"F0.imprint","IMPRINT",FACE,{"disambiguationData":[TD([[makeQuery(id+"F0.imprint","IMPRINT",EDGE,{"disambiguationData":[TD([[subQ2,-1.0]])],"derivedFrom":subQ1}),1.0]])]});}
            extrude(context, id + "F1", {"entities" : qUnion([Q0, Q1, Q2, Q3, Q4, Q5, Q6, Q7, Q8, Q9, Q10, Q11, Q12, Q13, Q14, Q15, Q16, Q17, Q18, Q19, Q20, Q21, Q22, Q23, Q24, Q25, Q26, Q27, Q28, Q29, Q30, Q31, Q32, Q33, Q34, Q35, Q36, Q37, Q38, Q39, Q40, Q41, Q42, Q43, Q44, Q45, Q46, Q47, Q48, Q49, Q50, Q51, Q52, Q53, Q54, Q55, Q56, Q57, Q58, Q59, Q60, Q61, Q62, Q63, Q64, Q65, Q66, Q67, Q68, Q69, Q70, Q71, Q72, Q73, Q74, Q75]), "oppositeDirection" : true, "depth" : 3.17 * mm});
        }
        {
            var Q0;
            Q0=makeQuery(id+"F1.opExtrude","CAP_EDGE",EDGE,{"disambiguationData":[OSD([sQuery(id+"F0.wireOp",EDGE,"a5322268-e1dc-436a-8e73-038b822e4c18")])],"isStart":false});
            var Q1;
            Q1=makeQuery(id+"F1.opExtrude","CAP_EDGE",EDGE,{"disambiguationData":[OSD([sQuery(id+"F0.wireOp",EDGE,"E7")])],"isStart":false});
            var Q2;
            Q2=makeQuery(id+"F1.opExtrude","CAP_EDGE",EDGE,{"disambiguationData":[OSD([sQuery(id+"F0.wireOp",EDGE,"1cb2681a-f61c-4038-b64f-4d8f3c1fa337")])],"isStart":true});
            var Q3;
            Q3=makeQuery(id+"F1.opExtrude","CAP_EDGE",EDGE,{"disambiguationData":[OSD([sQuery(id+"F0.wireOp",EDGE,"1cb2681a-f61c-4038-b64f-4d8f3c1fa337")])],"isStart":false});
            var Q4;
            Q4=makeQuery(id+"F1.opExtrude","CAP_EDGE",EDGE,{"disambiguationData":[OSD([sQuery(id+"F0.wireOp",EDGE,"E6")])],"isStart":false});
            var Q5;
            Q5=makeQuery(id+"F1.opExtrude","CAP_EDGE",EDGE,{"disambiguationData":[OSD([sQuery(id+"F0.wireOp",EDGE,"90b38568-d89f-4760-90db-baeff50cd179")])],"isStart":false});
            var Q6;
            Q6=makeQuery(id+"F1.opExtrude","CAP_EDGE",EDGE,{"disambiguationData":[OSD([sQuery(id+"F0.wireOp",EDGE,"E5")])],"isStart":false});
            var Q7;
            Q7=makeQuery(id+"F1.opExtrude","CAP_EDGE",EDGE,{"disambiguationData":[OSD([sQuery(id+"F0.wireOp",EDGE,"a8b6ce6c-9c41-4146-a937-b0af54ecc49b")])],"isStart":false});
            var Q8;
            Q8=makeQuery(id+"F1.opExtrude","CAP_EDGE",EDGE,{"disambiguationData":[OSD([sQuery(id+"F0.wireOp",EDGE,"E4")])],"isStart":false});
            var Q9;
            Q9=makeQuery(id+"F1.opExtrude","CAP_EDGE",EDGE,{"disambiguationData":[OSD([sQuery(id+"F0.wireOp",EDGE,"E6")])],"isStart":true});
            var Q10;
            Q10=makeQuery(id+"F1.opExtrude","CAP_EDGE",EDGE,{"disambiguationData":[OSD([sQuery(id+"F0.wireOp",EDGE,"90b38568-d89f-4760-90db-baeff50cd179")])],"isStart":true});
            var Q11;
            Q11=makeQuery(id+"F1.opExtrude","CAP_EDGE",EDGE,{"disambiguationData":[OSD([sQuery(id+"F0.wireOp",EDGE,"E5")])],"isStart":true});
            var Q12;
            Q12=makeQuery(id+"F1.opExtrude","CAP_EDGE",EDGE,{"disambiguationData":[OSD([sQuery(id+"F0.wireOp",EDGE,"a8b6ce6c-9c41-4146-a937-b0af54ecc49b")])],"isStart":true});
            var Q13;
            Q13=makeQuery(id+"F1.opExtrude","CAP_EDGE",EDGE,{"disambiguationData":[OSD([sQuery(id+"F0.wireOp",EDGE,"a5322268-e1dc-436a-8e73-038b822e4c18")])],"isStart":true});
            var Q14;
            Q14=makeQuery(id+"F1.opExtrude","CAP_EDGE",EDGE,{"disambiguationData":[OSD([sQuery(id+"F0.wireOp",EDGE,"E7")])],"isStart":true});
            var Q15;
            Q15=makeQuery(id+"F1.opExtrude","CAP_EDGE",EDGE,{"disambiguationData":[OSD([sQuery(id+"F0.wireOp",EDGE,"E4")])],"isStart":true});
            fillet(context, id + "F2", {"entities" : qUnion([Q0, Q1, Q2, Q3, Q4, Q5, Q6, Q7, Q8, Q9, Q10, Q11, Q12, Q13, Q14, Q15]), "radius" : 0.89 * mm, "tangentPropagation" : true, "allowEdgeOverflow" : false});
        }
        {
            var Q0;
            Q0=makeQuery(id+"F1.opExtrude","SWEPT_EDGE",EDGE,{"disambiguationData":[OSD([sQuery(id+"F0.wireOp",EDGE,"E10"),sQuery(id+"F0.wireOp",EDGE,"E19.rect.right")])]});
            var Q1;
            Q1=makeQuery(id+"F1.opExtrude","SWEPT_EDGE",EDGE,{"disambiguationData":[OSD([sQuery(id+"F0.wireOp",EDGE,"E12"),sQuery(id+"F0.wireOp",EDGE,"E20.rect.top")])]});
            var Q2;
            Q2=makeQuery(id+"F1.opExtrude","SWEPT_EDGE",EDGE,{"disambiguationData":[OSD([sQuery(id+"F0.wireOp",EDGE,"E17.rect.right"),sQuery(id+"F0.wireOp",EDGE,"E20.rect.top")])]});
            var Q3;
            Q3=makeQuery(id+"F1.opExtrude","SWEPT_EDGE",EDGE,{"disambiguationData":[OSD([sQuery(id+"F0.wireOp",EDGE,"E17.rect.right"),sQuery(id+"F0.wireOp",EDGE,"E20.rect.bottom")])]});
            var Q4;
            Q4=makeQuery(id+"F1.opExtrude","SWEPT_EDGE",EDGE,{"disambiguationData":[OSD([sQuery(id+"F0.wireOp",EDGE,"E17.rect.bottom"),sQuery(id+"F0.wireOp",EDGE,"E19.rect.right")])]});
            var Q5;
            Q5=makeQuery(id+"F1.opExtrude","SWEPT_EDGE",EDGE,{"disambiguationData":[OSD([sQuery(id+"F0.wireOp",EDGE,"E14"),sQuery(id+"F0.wireOp",EDGE,"E19.rect.right")])]});
            var Q6;
            Q6=makeQuery(id+"F1.opExtrude","SWEPT_EDGE",EDGE,{"disambiguationData":[OSD([sQuery(id+"F0.wireOp",EDGE,"E14"),sQuery(id+"F0.wireOp",EDGE,"E19.rect.left")])]});
            var Q7;
            Q7=makeQuery(id+"F1.opExtrude","SWEPT_EDGE",EDGE,{"disambiguationData":[OSD([sQuery(id+"F0.wireOp",EDGE,"E17.rect.bottom"),sQuery(id+"F0.wireOp",EDGE,"E19.rect.left")])]});
            var Q8;
            Q8=makeQuery(id+"F1.opExtrude","SWEPT_EDGE",EDGE,{"disambiguationData":[OSD([sQuery(id+"F0.wireOp",EDGE,"E17.rect.left"),sQuery(id+"F0.wireOp",EDGE,"E20.rect.bottom")])]});
            var Q9;
            Q9=makeQuery(id+"F1.opExtrude","SWEPT_EDGE",EDGE,{"disambiguationData":[OSD([sQuery(id+"F0.wireOp",EDGE,"E17.rect.left"),sQuery(id+"F0.wireOp",EDGE,"E20.rect.top")])]});
            var Q10;
            Q10=makeQuery(id+"F1.opExtrude","SWEPT_EDGE",EDGE,{"disambiguationData":[OSD([sQuery(id+"F0.wireOp",EDGE,"E17.rect.top"),sQuery(id+"F0.wireOp",EDGE,"E19.rect.left")])]});
            var Q11;
            Q11=makeQuery(id+"F1.opExtrude","SWEPT_EDGE",EDGE,{"disambiguationData":[OSD([sQuery(id+"F0.wireOp",EDGE,"E18.rect.top"),sQuery(id+"F0.wireOp",EDGE,"E18.rect.left")])]});
            var Q12;
            Q12=makeQuery(id+"F1.opExtrude","SWEPT_EDGE",EDGE,{"disambiguationData":[OSD([sQuery(id+"F0.wireOp",EDGE,"E18.rect.bottom"),sQuery(id+"F0.wireOp",EDGE,"E18.rect.left")])]});
            var Q13;
            Q13=makeQuery(id+"F1.opExtrude","SWEPT_EDGE",EDGE,{"disambiguationData":[OSD([sQuery(id+"F0.wireOp",EDGE,"E18.rect.bottom"),sQuery(id+"F0.wireOp",EDGE,"E18.rect.right")])]});
            var Q14;
            Q14=makeQuery(id+"F1.opExtrude","SWEPT_EDGE",EDGE,{"disambiguationData":[OSD([sQuery(id+"F0.wireOp",EDGE,"E18.rect.top"),sQuery(id+"F0.wireOp",EDGE,"E18.rect.right")])]});
            var Q15;
            Q15=makeQuery(id+"F1.opExtrude","SWEPT_EDGE",EDGE,{"disambiguationData":[OSD([sQuery(id+"F0.wireOp",EDGE,"E10"),sQuery(id+"F0.wireOp",EDGE,"E19.rect.left")])]});
            var Q16;
            Q16=makeQuery(id+"F1.opExtrude","SWEPT_EDGE",EDGE,{"disambiguationData":[OSD([sQuery(id+"F0.wireOp",EDGE,"E8"),sQuery(id+"F0.wireOp",EDGE,"E20.rect.bottom")])]});
            var Q17;
            Q17=makeQuery(id+"F1.opExtrude","SWEPT_EDGE",EDGE,{"disambiguationData":[OSD([sQuery(id+"F0.wireOp",EDGE,"E12"),sQuery(id+"F0.wireOp",EDGE,"E20.rect.bottom")])]});
            var Q18;
            Q18=makeQuery(id+"F1.opExtrude","SWEPT_EDGE",EDGE,{"disambiguationData":[OSD([sQuery(id+"F0.wireOp",EDGE,"E17.rect.top"),sQuery(id+"F0.wireOp",EDGE,"E19.rect.right")])]});
            var Q19;
            Q19=makeQuery(id+"F1.opExtrude","SWEPT_EDGE",EDGE,{"disambiguationData":[OSD([sQuery(id+"F0.wireOp",EDGE,"E8"),sQuery(id+"F0.wireOp",EDGE,"E20.rect.top")])]});
            var Q20;
            Q20=makeQuery(id+"F1.opExtrude","SWEPT_EDGE",EDGE,{"disambiguationData":[OSD([sQuery(id+"F0.wireOp",EDGE,"E18.rect.bottom"),sQuery(id+"F0.wireOp",EDGE,"E19.rect.left")])]});
            var Q21;
            Q21=makeQuery(id+"F1.opExtrude","SWEPT_EDGE",EDGE,{"disambiguationData":[OSD([sQuery(id+"F0.wireOp",EDGE,"E18.rect.bottom"),sQuery(id+"F0.wireOp",EDGE,"E19.rect.right")])]});
            var Q22;
            Q22=makeQuery(id+"F1.opExtrude","SWEPT_EDGE",EDGE,{"disambiguationData":[OSD([sQuery(id+"F0.wireOp",EDGE,"E18.rect.top"),sQuery(id+"F0.wireOp",EDGE,"E19.rect.right")])]});
            var Q23;
            Q23=makeQuery(id+"F1.opExtrude","SWEPT_EDGE",EDGE,{"disambiguationData":[OSD([sQuery(id+"F0.wireOp",EDGE,"E18.rect.top"),sQuery(id+"F0.wireOp",EDGE,"E19.rect.left")])]});
            fillet(context, id + "F3", {"entities" : qUnion([Q0, Q1, Q2, Q3, Q4, Q5, Q6, Q7, Q8, Q9, Q10, Q11, Q12, Q13, Q14, Q15, Q16, Q17, Q18, Q19, Q20, Q21, Q22, Q23]), "radius" : 1.02 * mm, "tangentPropagation" : true, "allowEdgeOverflow" : false});
        }
        {
            var Q0;
            {var subQ0=sQuery(id+"F0.wireOp",EDGE,"E20.rect.bottom");Q0=makeQuery(id+"F1.opExtrude","CAP_EDGE",EDGE,{"disambiguationData":[OSD([subQ0]),TDD([makeQuery(id+"F0.imprint","IMPRINT",EDGE,{"disambiguationData":[TD([[makeQuery(id+"F0.imprint","INTERSECT",VERTEX,{"derivedFrom":[sQuery(id+"F0.wireOp",EDGE,"E8"),subQ0]}),1.0]])],"derivedFrom":subQ0})])],"isStart":true});}
            var Q1;
            {var subQ0=sQuery(id+"F0.wireOp",EDGE,"E20.rect.bottom");var subQ1=sQuery(id+"F0.wireOp",EDGE,"E8");Q1=makeQuery(id+"F3.opFillet","BLEND_EDGE",EDGE,{"blendedFrom":[makeQuery(id+"F1.opExtrude","SWEPT_EDGE",EDGE,{"disambiguationData":[OSD([subQ1,subQ0])]}),makeQuery(id+"F1.opExtrude","CAP_FACE",FACE,{"disambiguationData":[OSD([sQuery(id+"F0.wireOp",EDGE,"E0"),sQuery(id+"F0.wireOp",EDGE,"E1"),sQuery(id+"F0.wireOp",EDGE,"E2"),sQuery(id+"F0.wireOp",EDGE,"E3"),sQuery(id+"F0.wireOp",EDGE,"E4"),sQuery(id+"F0.wireOp",EDGE,"E5"),sQuery(id+"F0.wireOp",EDGE,"E6"),sQuery(id+"F0.wireOp",EDGE,"E7"),subQ1,sQuery(id+"F0.wireOp",EDGE,"E9"),sQuery(id+"F0.wireOp",EDGE,"E10"),sQuery(id+"F0.wireOp",EDGE,"E11"),sQuery(id+"F0.wireOp",EDGE,"E12"),sQuery(id+"F0.wireOp",EDGE,"E13"),sQuery(id+"F0.wireOp",EDGE,"E14"),sQuery(id+"F0.wireOp",EDGE,"E15"),sQuery(id+"F0.wireOp",EDGE,"E17.rect.bottom"),sQuery(id+"F0.wireOp",EDGE,"E17.rect.top"),sQuery(id+"F0.wireOp",EDGE,"E17.rect.left"),sQuery(id+"F0.wireOp",EDGE,"E17.rect.right"),sQuery(id+"F0.wireOp",EDGE,"E18.rect.bottom"),sQuery(id+"F0.wireOp",EDGE,"E18.rect.top"),sQuery(id+"F0.wireOp",EDGE,"E18.rect.left"),sQuery(id+"F0.wireOp",EDGE,"E18.rect.right"),sQuery(id+"F0.wireOp",EDGE,"E19.rect.left"),sQuery(id+"F0.wireOp",EDGE,"E19.rect.right"),subQ0,sQuery(id+"F0.wireOp",EDGE,"E20.rect.top"),sQuery(id+"F0.wireOp",EDGE,"E23.top"),sQuery(id+"F0.wireOp",EDGE,"E23.left"),sQuery(id+"F0.wireOp",EDGE,"E23.right"),sQuery(id+"F0.wireOp",EDGE,"E24.top"),sQuery(id+"F0.wireOp",EDGE,"E24.left"),sQuery(id+"F0.wireOp",EDGE,"E24.right"),sQuery(id+"F0.wireOp",EDGE,"E25.top"),sQuery(id+"F0.wireOp",EDGE,"E25.left"),sQuery(id+"F0.wireOp",EDGE,"E25.right"),sQuery(id+"F0.wireOp",EDGE,"E26.top"),sQuery(id+"F0.wireOp",EDGE,"E26.left"),sQuery(id+"F0.wireOp",EDGE,"E26.right")])],"isStart":true})],"blendedInto":[makeQuery(id+"F1.opExtrude","CAP_FACE",FACE,{"disambiguationData":[OSD([sQuery(id+"F0.wireOp",EDGE,"E0"),sQuery(id+"F0.wireOp",EDGE,"E1"),sQuery(id+"F0.wireOp",EDGE,"E2"),sQuery(id+"F0.wireOp",EDGE,"E3"),sQuery(id+"F0.wireOp",EDGE,"E4"),sQuery(id+"F0.wireOp",EDGE,"E5"),sQuery(id+"F0.wireOp",EDGE,"E6"),sQuery(id+"F0.wireOp",EDGE,"E7"),subQ1,sQuery(id+"F0.wireOp",EDGE,"E9"),sQuery(id+"F0.wireOp",EDGE,"E10"),sQuery(id+"F0.wireOp",EDGE,"E11"),sQuery(id+"F0.wireOp",EDGE,"E12"),sQuery(id+"F0.wireOp",EDGE,"E13"),sQuery(id+"F0.wireOp",EDGE,"E14"),sQuery(id+"F0.wireOp",EDGE,"E15"),sQuery(id+"F0.wireOp",EDGE,"E17.rect.bottom"),sQuery(id+"F0.wireOp",EDGE,"E17.rect.top"),sQuery(id+"F0.wireOp",EDGE,"E17.rect.left"),sQuery(id+"F0.wireOp",EDGE,"E17.rect.right"),sQuery(id+"F0.wireOp",EDGE,"E18.rect.bottom"),sQuery(id+"F0.wireOp",EDGE,"E18.rect.top"),sQuery(id+"F0.wireOp",EDGE,"E18.rect.left"),sQuery(id+"F0.wireOp",EDGE,"E18.rect.right"),sQuery(id+"F0.wireOp",EDGE,"E19.rect.left"),sQuery(id+"F0.wireOp",EDGE,"E19.rect.right"),subQ0,sQuery(id+"F0.wireOp",EDGE,"E20.rect.top"),sQuery(id+"F0.wireOp",EDGE,"E23.top"),sQuery(id+"F0.wireOp",EDGE,"E23.left"),sQuery(id+"F0.wireOp",EDGE,"E23.right"),sQuery(id+"F0.wireOp",EDGE,"E24.top"),sQuery(id+"F0.wireOp",EDGE,"E24.left"),sQuery(id+"F0.wireOp",EDGE,"E24.right"),sQuery(id+"F0.wireOp",EDGE,"E25.top"),sQuery(id+"F0.wireOp",EDGE,"E25.left"),sQuery(id+"F0.wireOp",EDGE,"E25.right"),sQuery(id+"F0.wireOp",EDGE,"E26.top"),sQuery(id+"F0.wireOp",EDGE,"E26.left"),sQuery(id+"F0.wireOp",EDGE,"E26.right")])],"isStart":true})]});}
            var Q2;
            {var subQ0=sQuery(id+"F0.wireOp",EDGE,"E8");var subQ1=makeQuery(id+"F0.imprint","INTERSECT",VERTEX,{"disambiguationData":[OD(1.0)],"derivedFrom":[sQuery(id+"F0.wireOp",EDGE,"E4"),subQ0]});Q2=makeQuery(id+"F1.opExtrude","CAP_EDGE",EDGE,{"disambiguationData":[OSD([subQ0]),TDD([makeQuery(id+"F0.imprint","IMPRINT",EDGE,{"disambiguationData":[TD([[subQ1,1.0]])],"derivedFrom":subQ0}),makeQuery(id+"F0.imprint","IMPRINT",EDGE,{"disambiguationData":[TD([[makeQuery(id+"F0.imprint","INTERSECT",VERTEX,{"disambiguationData":[OD(1.0)],"derivedFrom":[sQuery(id+"F0.wireOp",EDGE,"E0"),subQ0]}),1.0]])],"derivedFrom":subQ0})])],"isStart":true});}
            var Q3;
            {var subQ0=sQuery(id+"F0.wireOp",EDGE,"E20.rect.bottom");var subQ1=sQuery(id+"F0.wireOp",EDGE,"E17.rect.right");Q3=makeQuery(id+"F3.opFillet","BLEND_EDGE",EDGE,{"blendedFrom":[makeQuery(id+"F1.opExtrude","SWEPT_EDGE",EDGE,{"disambiguationData":[OSD([subQ1,subQ0])]}),makeQuery(id+"F1.opExtrude","CAP_FACE",FACE,{"disambiguationData":[OSD([sQuery(id+"F0.wireOp",EDGE,"E0"),sQuery(id+"F0.wireOp",EDGE,"E1"),sQuery(id+"F0.wireOp",EDGE,"E2"),sQuery(id+"F0.wireOp",EDGE,"E3"),sQuery(id+"F0.wireOp",EDGE,"E4"),sQuery(id+"F0.wireOp",EDGE,"E5"),sQuery(id+"F0.wireOp",EDGE,"E6"),sQuery(id+"F0.wireOp",EDGE,"E7"),sQuery(id+"F0.wireOp",EDGE,"E8"),sQuery(id+"F0.wireOp",EDGE,"E9"),sQuery(id+"F0.wireOp",EDGE,"E10"),sQuery(id+"F0.wireOp",EDGE,"E11"),sQuery(id+"F0.wireOp",EDGE,"E12"),sQuery(id+"F0.wireOp",EDGE,"E13"),sQuery(id+"F0.wireOp",EDGE,"E14"),sQuery(id+"F0.wireOp",EDGE,"E15"),sQuery(id+"F0.wireOp",EDGE,"E17.rect.bottom"),sQuery(id+"F0.wireOp",EDGE,"E17.rect.top"),sQuery(id+"F0.wireOp",EDGE,"E17.rect.left"),subQ1,sQuery(id+"F0.wireOp",EDGE,"E18.rect.bottom"),sQuery(id+"F0.wireOp",EDGE,"E18.rect.top"),sQuery(id+"F0.wireOp",EDGE,"E18.rect.left"),sQuery(id+"F0.wireOp",EDGE,"E18.rect.right"),sQuery(id+"F0.wireOp",EDGE,"E19.rect.left"),sQuery(id+"F0.wireOp",EDGE,"E19.rect.right"),subQ0,sQuery(id+"F0.wireOp",EDGE,"E20.rect.top"),sQuery(id+"F0.wireOp",EDGE,"E23.top"),sQuery(id+"F0.wireOp",EDGE,"E23.left"),sQuery(id+"F0.wireOp",EDGE,"E23.right"),sQuery(id+"F0.wireOp",EDGE,"E24.top"),sQuery(id+"F0.wireOp",EDGE,"E24.left"),sQuery(id+"F0.wireOp",EDGE,"E24.right"),sQuery(id+"F0.wireOp",EDGE,"E25.top"),sQuery(id+"F0.wireOp",EDGE,"E25.left"),sQuery(id+"F0.wireOp",EDGE,"E25.right"),sQuery(id+"F0.wireOp",EDGE,"E26.top"),sQuery(id+"F0.wireOp",EDGE,"E26.left"),sQuery(id+"F0.wireOp",EDGE,"E26.right")])],"isStart":true})],"blendedInto":[makeQuery(id+"F1.opExtrude","CAP_FACE",FACE,{"disambiguationData":[OSD([sQuery(id+"F0.wireOp",EDGE,"E0"),sQuery(id+"F0.wireOp",EDGE,"E1"),sQuery(id+"F0.wireOp",EDGE,"E2"),sQuery(id+"F0.wireOp",EDGE,"E3"),sQuery(id+"F0.wireOp",EDGE,"E4"),sQuery(id+"F0.wireOp",EDGE,"E5"),sQuery(id+"F0.wireOp",EDGE,"E6"),sQuery(id+"F0.wireOp",EDGE,"E7"),sQuery(id+"F0.wireOp",EDGE,"E8"),sQuery(id+"F0.wireOp",EDGE,"E9"),sQuery(id+"F0.wireOp",EDGE,"E10"),sQuery(id+"F0.wireOp",EDGE,"E11"),sQuery(id+"F0.wireOp",EDGE,"E12"),sQuery(id+"F0.wireOp",EDGE,"E13"),sQuery(id+"F0.wireOp",EDGE,"E14"),sQuery(id+"F0.wireOp",EDGE,"E15"),sQuery(id+"F0.wireOp",EDGE,"E17.rect.bottom"),sQuery(id+"F0.wireOp",EDGE,"E17.rect.top"),sQuery(id+"F0.wireOp",EDGE,"E17.rect.left"),subQ1,sQuery(id+"F0.wireOp",EDGE,"E18.rect.bottom"),sQuery(id+"F0.wireOp",EDGE,"E18.rect.top"),sQuery(id+"F0.wireOp",EDGE,"E18.rect.left"),sQuery(id+"F0.wireOp",EDGE,"E18.rect.right"),sQuery(id+"F0.wireOp",EDGE,"E19.rect.left"),sQuery(id+"F0.wireOp",EDGE,"E19.rect.right"),subQ0,sQuery(id+"F0.wireOp",EDGE,"E20.rect.top"),sQuery(id+"F0.wireOp",EDGE,"E23.top"),sQuery(id+"F0.wireOp",EDGE,"E23.left"),sQuery(id+"F0.wireOp",EDGE,"E23.right"),sQuery(id+"F0.wireOp",EDGE,"E24.top"),sQuery(id+"F0.wireOp",EDGE,"E24.left"),sQuery(id+"F0.wireOp",EDGE,"E24.right"),sQuery(id+"F0.wireOp",EDGE,"E25.top"),sQuery(id+"F0.wireOp",EDGE,"E25.left"),sQuery(id+"F0.wireOp",EDGE,"E25.right"),sQuery(id+"F0.wireOp",EDGE,"E26.top"),sQuery(id+"F0.wireOp",EDGE,"E26.left"),sQuery(id+"F0.wireOp",EDGE,"E26.right")])],"isStart":true})]});}
            var Q4;
            {var subQ0=sQuery(id+"F0.wireOp",EDGE,"E20.rect.top");Q4=makeQuery(id+"F1.opExtrude","CAP_EDGE",EDGE,{"disambiguationData":[OSD([subQ0]),TDD([makeQuery(id+"F0.imprint","IMPRINT",EDGE,{"disambiguationData":[TD([[makeQuery(id+"F0.imprint","INTERSECT",VERTEX,{"derivedFrom":[sQuery(id+"F0.wireOp",EDGE,"E8"),subQ0]}),1.0]])],"derivedFrom":subQ0})])],"isStart":true});}
            var Q5;
            {var subQ0=sQuery(id+"F0.wireOp",EDGE,"E20.rect.top");var subQ1=sQuery(id+"F0.wireOp",EDGE,"E8");Q5=makeQuery(id+"F3.opFillet","BLEND_EDGE",EDGE,{"blendedFrom":[makeQuery(id+"F1.opExtrude","SWEPT_EDGE",EDGE,{"disambiguationData":[OSD([subQ1,subQ0])]}),makeQuery(id+"F1.opExtrude","CAP_FACE",FACE,{"disambiguationData":[OSD([sQuery(id+"F0.wireOp",EDGE,"E0"),sQuery(id+"F0.wireOp",EDGE,"E1"),sQuery(id+"F0.wireOp",EDGE,"E2"),sQuery(id+"F0.wireOp",EDGE,"E3"),sQuery(id+"F0.wireOp",EDGE,"E4"),sQuery(id+"F0.wireOp",EDGE,"E5"),sQuery(id+"F0.wireOp",EDGE,"E6"),sQuery(id+"F0.wireOp",EDGE,"E7"),subQ1,sQuery(id+"F0.wireOp",EDGE,"E9"),sQuery(id+"F0.wireOp",EDGE,"E10"),sQuery(id+"F0.wireOp",EDGE,"E11"),sQuery(id+"F0.wireOp",EDGE,"E12"),sQuery(id+"F0.wireOp",EDGE,"E13"),sQuery(id+"F0.wireOp",EDGE,"E14"),sQuery(id+"F0.wireOp",EDGE,"E15"),sQuery(id+"F0.wireOp",EDGE,"E17.rect.bottom"),sQuery(id+"F0.wireOp",EDGE,"E17.rect.top"),sQuery(id+"F0.wireOp",EDGE,"E17.rect.left"),sQuery(id+"F0.wireOp",EDGE,"E17.rect.right"),sQuery(id+"F0.wireOp",EDGE,"E18.rect.bottom"),sQuery(id+"F0.wireOp",EDGE,"E18.rect.top"),sQuery(id+"F0.wireOp",EDGE,"E18.rect.left"),sQuery(id+"F0.wireOp",EDGE,"E18.rect.right"),sQuery(id+"F0.wireOp",EDGE,"E19.rect.left"),sQuery(id+"F0.wireOp",EDGE,"E19.rect.right"),sQuery(id+"F0.wireOp",EDGE,"E20.rect.bottom"),subQ0,sQuery(id+"F0.wireOp",EDGE,"E23.top"),sQuery(id+"F0.wireOp",EDGE,"E23.left"),sQuery(id+"F0.wireOp",EDGE,"E23.right"),sQuery(id+"F0.wireOp",EDGE,"E24.top"),sQuery(id+"F0.wireOp",EDGE,"E24.left"),sQuery(id+"F0.wireOp",EDGE,"E24.right"),sQuery(id+"F0.wireOp",EDGE,"E25.top"),sQuery(id+"F0.wireOp",EDGE,"E25.left"),sQuery(id+"F0.wireOp",EDGE,"E25.right"),sQuery(id+"F0.wireOp",EDGE,"E26.top"),sQuery(id+"F0.wireOp",EDGE,"E26.left"),sQuery(id+"F0.wireOp",EDGE,"E26.right")])],"isStart":true})],"blendedInto":[makeQuery(id+"F1.opExtrude","CAP_FACE",FACE,{"disambiguationData":[OSD([sQuery(id+"F0.wireOp",EDGE,"E0"),sQuery(id+"F0.wireOp",EDGE,"E1"),sQuery(id+"F0.wireOp",EDGE,"E2"),sQuery(id+"F0.wireOp",EDGE,"E3"),sQuery(id+"F0.wireOp",EDGE,"E4"),sQuery(id+"F0.wireOp",EDGE,"E5"),sQuery(id+"F0.wireOp",EDGE,"E6"),sQuery(id+"F0.wireOp",EDGE,"E7"),subQ1,sQuery(id+"F0.wireOp",EDGE,"E9"),sQuery(id+"F0.wireOp",EDGE,"E10"),sQuery(id+"F0.wireOp",EDGE,"E11"),sQuery(id+"F0.wireOp",EDGE,"E12"),sQuery(id+"F0.wireOp",EDGE,"E13"),sQuery(id+"F0.wireOp",EDGE,"E14"),sQuery(id+"F0.wireOp",EDGE,"E15"),sQuery(id+"F0.wireOp",EDGE,"E17.rect.bottom"),sQuery(id+"F0.wireOp",EDGE,"E17.rect.top"),sQuery(id+"F0.wireOp",EDGE,"E17.rect.left"),sQuery(id+"F0.wireOp",EDGE,"E17.rect.right"),sQuery(id+"F0.wireOp",EDGE,"E18.rect.bottom"),sQuery(id+"F0.wireOp",EDGE,"E18.rect.top"),sQuery(id+"F0.wireOp",EDGE,"E18.rect.left"),sQuery(id+"F0.wireOp",EDGE,"E18.rect.right"),sQuery(id+"F0.wireOp",EDGE,"E19.rect.left"),sQuery(id+"F0.wireOp",EDGE,"E19.rect.right"),sQuery(id+"F0.wireOp",EDGE,"E20.rect.bottom"),subQ0,sQuery(id+"F0.wireOp",EDGE,"E23.top"),sQuery(id+"F0.wireOp",EDGE,"E23.left"),sQuery(id+"F0.wireOp",EDGE,"E23.right"),sQuery(id+"F0.wireOp",EDGE,"E24.top"),sQuery(id+"F0.wireOp",EDGE,"E24.left"),sQuery(id+"F0.wireOp",EDGE,"E24.right"),sQuery(id+"F0.wireOp",EDGE,"E25.top"),sQuery(id+"F0.wireOp",EDGE,"E25.left"),sQuery(id+"F0.wireOp",EDGE,"E25.right"),sQuery(id+"F0.wireOp",EDGE,"E26.top"),sQuery(id+"F0.wireOp",EDGE,"E26.left"),sQuery(id+"F0.wireOp",EDGE,"E26.right")])],"isStart":true})]});}
            var Q6;
            {var subQ0=sQuery(id+"F0.wireOp",EDGE,"E8");var subQ1=makeQuery(id+"F0.imprint","INTERSECT",VERTEX,{"disambiguationData":[OD(0.0)],"derivedFrom":[sQuery(id+"F0.wireOp",EDGE,"E5"),subQ0]});Q6=makeQuery(id+"F1.opExtrude","CAP_EDGE",EDGE,{"disambiguationData":[OSD([subQ0]),TDD([makeQuery(id+"F0.imprint","IMPRINT",EDGE,{"disambiguationData":[TD([[makeQuery(id+"F0.imprint","INTERSECT",VERTEX,{"disambiguationData":[OD(1.0)],"derivedFrom":[sQuery(id+"F0.wireOp",EDGE,"E3"),subQ0]}),-1.0]])],"derivedFrom":subQ0}),makeQuery(id+"F0.imprint","IMPRINT",EDGE,{"disambiguationData":[TD([[subQ1,-1.0]])],"derivedFrom":subQ0})])],"isStart":true});}
            var Q7;
            {var subQ0=sQuery(id+"F0.wireOp",EDGE,"E20.rect.top");var subQ1=sQuery(id+"F0.wireOp",EDGE,"E17.rect.right");Q7=makeQuery(id+"F3.opFillet","BLEND_EDGE",EDGE,{"blendedFrom":[makeQuery(id+"F1.opExtrude","SWEPT_EDGE",EDGE,{"disambiguationData":[OSD([subQ1,subQ0])]}),makeQuery(id+"F1.opExtrude","CAP_FACE",FACE,{"disambiguationData":[OSD([sQuery(id+"F0.wireOp",EDGE,"E0"),sQuery(id+"F0.wireOp",EDGE,"E1"),sQuery(id+"F0.wireOp",EDGE,"E2"),sQuery(id+"F0.wireOp",EDGE,"E3"),sQuery(id+"F0.wireOp",EDGE,"E4"),sQuery(id+"F0.wireOp",EDGE,"E5"),sQuery(id+"F0.wireOp",EDGE,"E6"),sQuery(id+"F0.wireOp",EDGE,"E7"),sQuery(id+"F0.wireOp",EDGE,"E8"),sQuery(id+"F0.wireOp",EDGE,"E9"),sQuery(id+"F0.wireOp",EDGE,"E10"),sQuery(id+"F0.wireOp",EDGE,"E11"),sQuery(id+"F0.wireOp",EDGE,"E12"),sQuery(id+"F0.wireOp",EDGE,"E13"),sQuery(id+"F0.wireOp",EDGE,"E14"),sQuery(id+"F0.wireOp",EDGE,"E15"),sQuery(id+"F0.wireOp",EDGE,"E17.rect.bottom"),sQuery(id+"F0.wireOp",EDGE,"E17.rect.top"),sQuery(id+"F0.wireOp",EDGE,"E17.rect.left"),subQ1,sQuery(id+"F0.wireOp",EDGE,"E18.rect.bottom"),sQuery(id+"F0.wireOp",EDGE,"E18.rect.top"),sQuery(id+"F0.wireOp",EDGE,"E18.rect.left"),sQuery(id+"F0.wireOp",EDGE,"E18.rect.right"),sQuery(id+"F0.wireOp",EDGE,"E19.rect.left"),sQuery(id+"F0.wireOp",EDGE,"E19.rect.right"),sQuery(id+"F0.wireOp",EDGE,"E20.rect.bottom"),subQ0,sQuery(id+"F0.wireOp",EDGE,"E23.top"),sQuery(id+"F0.wireOp",EDGE,"E23.left"),sQuery(id+"F0.wireOp",EDGE,"E23.right"),sQuery(id+"F0.wireOp",EDGE,"E24.top"),sQuery(id+"F0.wireOp",EDGE,"E24.left"),sQuery(id+"F0.wireOp",EDGE,"E24.right"),sQuery(id+"F0.wireOp",EDGE,"E25.top"),sQuery(id+"F0.wireOp",EDGE,"E25.left"),sQuery(id+"F0.wireOp",EDGE,"E25.right"),sQuery(id+"F0.wireOp",EDGE,"E26.top"),sQuery(id+"F0.wireOp",EDGE,"E26.left"),sQuery(id+"F0.wireOp",EDGE,"E26.right")])],"isStart":true})],"blendedInto":[makeQuery(id+"F1.opExtrude","CAP_FACE",FACE,{"disambiguationData":[OSD([sQuery(id+"F0.wireOp",EDGE,"E0"),sQuery(id+"F0.wireOp",EDGE,"E1"),sQuery(id+"F0.wireOp",EDGE,"E2"),sQuery(id+"F0.wireOp",EDGE,"E3"),sQuery(id+"F0.wireOp",EDGE,"E4"),sQuery(id+"F0.wireOp",EDGE,"E5"),sQuery(id+"F0.wireOp",EDGE,"E6"),sQuery(id+"F0.wireOp",EDGE,"E7"),sQuery(id+"F0.wireOp",EDGE,"E8"),sQuery(id+"F0.wireOp",EDGE,"E9"),sQuery(id+"F0.wireOp",EDGE,"E10"),sQuery(id+"F0.wireOp",EDGE,"E11"),sQuery(id+"F0.wireOp",EDGE,"E12"),sQuery(id+"F0.wireOp",EDGE,"E13"),sQuery(id+"F0.wireOp",EDGE,"E14"),sQuery(id+"F0.wireOp",EDGE,"E15"),sQuery(id+"F0.wireOp",EDGE,"E17.rect.bottom"),sQuery(id+"F0.wireOp",EDGE,"E17.rect.top"),sQuery(id+"F0.wireOp",EDGE,"E17.rect.left"),subQ1,sQuery(id+"F0.wireOp",EDGE,"E18.rect.bottom"),sQuery(id+"F0.wireOp",EDGE,"E18.rect.top"),sQuery(id+"F0.wireOp",EDGE,"E18.rect.left"),sQuery(id+"F0.wireOp",EDGE,"E18.rect.right"),sQuery(id+"F0.wireOp",EDGE,"E19.rect.left"),sQuery(id+"F0.wireOp",EDGE,"E19.rect.right"),sQuery(id+"F0.wireOp",EDGE,"E20.rect.bottom"),subQ0,sQuery(id+"F0.wireOp",EDGE,"E23.top"),sQuery(id+"F0.wireOp",EDGE,"E23.left"),sQuery(id+"F0.wireOp",EDGE,"E23.right"),sQuery(id+"F0.wireOp",EDGE,"E24.top"),sQuery(id+"F0.wireOp",EDGE,"E24.left"),sQuery(id+"F0.wireOp",EDGE,"E24.right"),sQuery(id+"F0.wireOp",EDGE,"E25.top"),sQuery(id+"F0.wireOp",EDGE,"E25.left"),sQuery(id+"F0.wireOp",EDGE,"E25.right"),sQuery(id+"F0.wireOp",EDGE,"E26.top"),sQuery(id+"F0.wireOp",EDGE,"E26.left"),sQuery(id+"F0.wireOp",EDGE,"E26.right")])],"isStart":true})]});}
            var Q8;
            {var subQ0=sQuery(id+"F0.wireOp",EDGE,"E10");var subQ1=makeQuery(id+"F0.imprint","INTERSECT",VERTEX,{"disambiguationData":[OD(1.0)],"derivedFrom":[sQuery(id+"F0.wireOp",EDGE,"E4"),subQ0]});Q8=makeQuery(id+"F1.opExtrude","CAP_EDGE",EDGE,{"disambiguationData":[OSD([subQ0]),TDD([makeQuery(id+"F0.imprint","IMPRINT",EDGE,{"disambiguationData":[TD([[makeQuery(id+"F0.imprint","INTERSECT",VERTEX,{"disambiguationData":[OD(1.0)],"derivedFrom":[sQuery(id+"F0.wireOp",EDGE,"E0"),subQ0]}),-1.0]])],"derivedFrom":subQ0}),makeQuery(id+"F0.imprint","IMPRINT",EDGE,{"disambiguationData":[TD([[subQ1,-1.0]])],"derivedFrom":subQ0})])],"isStart":true});}
            var Q9;
            {var subQ0=sQuery(id+"F0.wireOp",EDGE,"E19.rect.right");var subQ1=sQuery(id+"F0.wireOp",EDGE,"E10");Q9=makeQuery(id+"F3.opFillet","BLEND_EDGE",EDGE,{"blendedFrom":[makeQuery(id+"F1.opExtrude","SWEPT_EDGE",EDGE,{"disambiguationData":[OSD([subQ1,subQ0])]}),makeQuery(id+"F1.opExtrude","CAP_FACE",FACE,{"disambiguationData":[OSD([sQuery(id+"F0.wireOp",EDGE,"E0"),sQuery(id+"F0.wireOp",EDGE,"E1"),sQuery(id+"F0.wireOp",EDGE,"E2"),sQuery(id+"F0.wireOp",EDGE,"E3"),sQuery(id+"F0.wireOp",EDGE,"E4"),sQuery(id+"F0.wireOp",EDGE,"E5"),sQuery(id+"F0.wireOp",EDGE,"E6"),sQuery(id+"F0.wireOp",EDGE,"E7"),sQuery(id+"F0.wireOp",EDGE,"E8"),sQuery(id+"F0.wireOp",EDGE,"E9"),subQ1,sQuery(id+"F0.wireOp",EDGE,"E11"),sQuery(id+"F0.wireOp",EDGE,"E12"),sQuery(id+"F0.wireOp",EDGE,"E13"),sQuery(id+"F0.wireOp",EDGE,"E14"),sQuery(id+"F0.wireOp",EDGE,"E15"),sQuery(id+"F0.wireOp",EDGE,"E17.rect.bottom"),sQuery(id+"F0.wireOp",EDGE,"E17.rect.top"),sQuery(id+"F0.wireOp",EDGE,"E17.rect.left"),sQuery(id+"F0.wireOp",EDGE,"E17.rect.right"),sQuery(id+"F0.wireOp",EDGE,"E18.rect.bottom"),sQuery(id+"F0.wireOp",EDGE,"E18.rect.top"),sQuery(id+"F0.wireOp",EDGE,"E18.rect.left"),sQuery(id+"F0.wireOp",EDGE,"E18.rect.right"),sQuery(id+"F0.wireOp",EDGE,"E19.rect.left"),subQ0,sQuery(id+"F0.wireOp",EDGE,"E20.rect.bottom"),sQuery(id+"F0.wireOp",EDGE,"E20.rect.top"),sQuery(id+"F0.wireOp",EDGE,"E23.top"),sQuery(id+"F0.wireOp",EDGE,"E23.left"),sQuery(id+"F0.wireOp",EDGE,"E23.right"),sQuery(id+"F0.wireOp",EDGE,"E24.top"),sQuery(id+"F0.wireOp",EDGE,"E24.left"),sQuery(id+"F0.wireOp",EDGE,"E24.right"),sQuery(id+"F0.wireOp",EDGE,"E25.top"),sQuery(id+"F0.wireOp",EDGE,"E25.left"),sQuery(id+"F0.wireOp",EDGE,"E25.right"),sQuery(id+"F0.wireOp",EDGE,"E26.top"),sQuery(id+"F0.wireOp",EDGE,"E26.left"),sQuery(id+"F0.wireOp",EDGE,"E26.right")])],"isStart":true})],"blendedInto":[makeQuery(id+"F1.opExtrude","CAP_FACE",FACE,{"disambiguationData":[OSD([sQuery(id+"F0.wireOp",EDGE,"E0"),sQuery(id+"F0.wireOp",EDGE,"E1"),sQuery(id+"F0.wireOp",EDGE,"E2"),sQuery(id+"F0.wireOp",EDGE,"E3"),sQuery(id+"F0.wireOp",EDGE,"E4"),sQuery(id+"F0.wireOp",EDGE,"E5"),sQuery(id+"F0.wireOp",EDGE,"E6"),sQuery(id+"F0.wireOp",EDGE,"E7"),sQuery(id+"F0.wireOp",EDGE,"E8"),sQuery(id+"F0.wireOp",EDGE,"E9"),subQ1,sQuery(id+"F0.wireOp",EDGE,"E11"),sQuery(id+"F0.wireOp",EDGE,"E12"),sQuery(id+"F0.wireOp",EDGE,"E13"),sQuery(id+"F0.wireOp",EDGE,"E14"),sQuery(id+"F0.wireOp",EDGE,"E15"),sQuery(id+"F0.wireOp",EDGE,"E17.rect.bottom"),sQuery(id+"F0.wireOp",EDGE,"E17.rect.top"),sQuery(id+"F0.wireOp",EDGE,"E17.rect.left"),sQuery(id+"F0.wireOp",EDGE,"E17.rect.right"),sQuery(id+"F0.wireOp",EDGE,"E18.rect.bottom"),sQuery(id+"F0.wireOp",EDGE,"E18.rect.top"),sQuery(id+"F0.wireOp",EDGE,"E18.rect.left"),sQuery(id+"F0.wireOp",EDGE,"E18.rect.right"),sQuery(id+"F0.wireOp",EDGE,"E19.rect.left"),subQ0,sQuery(id+"F0.wireOp",EDGE,"E20.rect.bottom"),sQuery(id+"F0.wireOp",EDGE,"E20.rect.top"),sQuery(id+"F0.wireOp",EDGE,"E23.top"),sQuery(id+"F0.wireOp",EDGE,"E23.left"),sQuery(id+"F0.wireOp",EDGE,"E23.right"),sQuery(id+"F0.wireOp",EDGE,"E24.top"),sQuery(id+"F0.wireOp",EDGE,"E24.left"),sQuery(id+"F0.wireOp",EDGE,"E24.right"),sQuery(id+"F0.wireOp",EDGE,"E25.top"),sQuery(id+"F0.wireOp",EDGE,"E25.left"),sQuery(id+"F0.wireOp",EDGE,"E25.right"),sQuery(id+"F0.wireOp",EDGE,"E26.top"),sQuery(id+"F0.wireOp",EDGE,"E26.left"),sQuery(id+"F0.wireOp",EDGE,"E26.right")])],"isStart":true})]});}
            var Q10;
            {var subQ0=sQuery(id+"F0.wireOp",EDGE,"E19.rect.right");Q10=makeQuery(id+"F1.opExtrude","CAP_EDGE",EDGE,{"disambiguationData":[OSD([subQ0]),TDD([makeQuery(id+"F0.imprint","IMPRINT",EDGE,{"disambiguationData":[TD([[makeQuery(id+"F0.imprint","INTERSECT",VERTEX,{"derivedFrom":[sQuery(id+"F0.wireOp",EDGE,"E10"),subQ0]}),-1.0]])],"derivedFrom":subQ0})])],"isStart":true});}
            var Q11;
            {var subQ0=sQuery(id+"F0.wireOp",EDGE,"E19.rect.right");var subQ1=sQuery(id+"F0.wireOp",EDGE,"E17.rect.bottom");Q11=makeQuery(id+"F3.opFillet","BLEND_EDGE",EDGE,{"blendedFrom":[makeQuery(id+"F1.opExtrude","SWEPT_EDGE",EDGE,{"disambiguationData":[OSD([subQ1,subQ0])]}),makeQuery(id+"F1.opExtrude","CAP_FACE",FACE,{"disambiguationData":[OSD([sQuery(id+"F0.wireOp",EDGE,"E0"),sQuery(id+"F0.wireOp",EDGE,"E1"),sQuery(id+"F0.wireOp",EDGE,"E2"),sQuery(id+"F0.wireOp",EDGE,"E3"),sQuery(id+"F0.wireOp",EDGE,"E4"),sQuery(id+"F0.wireOp",EDGE,"E5"),sQuery(id+"F0.wireOp",EDGE,"E6"),sQuery(id+"F0.wireOp",EDGE,"E7"),sQuery(id+"F0.wireOp",EDGE,"E8"),sQuery(id+"F0.wireOp",EDGE,"E9"),sQuery(id+"F0.wireOp",EDGE,"E10"),sQuery(id+"F0.wireOp",EDGE,"E11"),sQuery(id+"F0.wireOp",EDGE,"E12"),sQuery(id+"F0.wireOp",EDGE,"E13"),sQuery(id+"F0.wireOp",EDGE,"E14"),sQuery(id+"F0.wireOp",EDGE,"E15"),subQ1,sQuery(id+"F0.wireOp",EDGE,"E17.rect.top"),sQuery(id+"F0.wireOp",EDGE,"E17.rect.left"),sQuery(id+"F0.wireOp",EDGE,"E17.rect.right"),sQuery(id+"F0.wireOp",EDGE,"E18.rect.bottom"),sQuery(id+"F0.wireOp",EDGE,"E18.rect.top"),sQuery(id+"F0.wireOp",EDGE,"E18.rect.left"),sQuery(id+"F0.wireOp",EDGE,"E18.rect.right"),sQuery(id+"F0.wireOp",EDGE,"E19.rect.left"),subQ0,sQuery(id+"F0.wireOp",EDGE,"E20.rect.bottom"),sQuery(id+"F0.wireOp",EDGE,"E20.rect.top"),sQuery(id+"F0.wireOp",EDGE,"E23.top"),sQuery(id+"F0.wireOp",EDGE,"E23.left"),sQuery(id+"F0.wireOp",EDGE,"E23.right"),sQuery(id+"F0.wireOp",EDGE,"E24.top"),sQuery(id+"F0.wireOp",EDGE,"E24.left"),sQuery(id+"F0.wireOp",EDGE,"E24.right"),sQuery(id+"F0.wireOp",EDGE,"E25.top"),sQuery(id+"F0.wireOp",EDGE,"E25.left"),sQuery(id+"F0.wireOp",EDGE,"E25.right"),sQuery(id+"F0.wireOp",EDGE,"E26.top"),sQuery(id+"F0.wireOp",EDGE,"E26.left"),sQuery(id+"F0.wireOp",EDGE,"E26.right")])],"isStart":true})],"blendedInto":[makeQuery(id+"F1.opExtrude","CAP_FACE",FACE,{"disambiguationData":[OSD([sQuery(id+"F0.wireOp",EDGE,"E0"),sQuery(id+"F0.wireOp",EDGE,"E1"),sQuery(id+"F0.wireOp",EDGE,"E2"),sQuery(id+"F0.wireOp",EDGE,"E3"),sQuery(id+"F0.wireOp",EDGE,"E4"),sQuery(id+"F0.wireOp",EDGE,"E5"),sQuery(id+"F0.wireOp",EDGE,"E6"),sQuery(id+"F0.wireOp",EDGE,"E7"),sQuery(id+"F0.wireOp",EDGE,"E8"),sQuery(id+"F0.wireOp",EDGE,"E9"),sQuery(id+"F0.wireOp",EDGE,"E10"),sQuery(id+"F0.wireOp",EDGE,"E11"),sQuery(id+"F0.wireOp",EDGE,"E12"),sQuery(id+"F0.wireOp",EDGE,"E13"),sQuery(id+"F0.wireOp",EDGE,"E14"),sQuery(id+"F0.wireOp",EDGE,"E15"),subQ1,sQuery(id+"F0.wireOp",EDGE,"E17.rect.top"),sQuery(id+"F0.wireOp",EDGE,"E17.rect.left"),sQuery(id+"F0.wireOp",EDGE,"E17.rect.right"),sQuery(id+"F0.wireOp",EDGE,"E18.rect.bottom"),sQuery(id+"F0.wireOp",EDGE,"E18.rect.top"),sQuery(id+"F0.wireOp",EDGE,"E18.rect.left"),sQuery(id+"F0.wireOp",EDGE,"E18.rect.right"),sQuery(id+"F0.wireOp",EDGE,"E19.rect.left"),subQ0,sQuery(id+"F0.wireOp",EDGE,"E20.rect.bottom"),sQuery(id+"F0.wireOp",EDGE,"E20.rect.top"),sQuery(id+"F0.wireOp",EDGE,"E23.top"),sQuery(id+"F0.wireOp",EDGE,"E23.left"),sQuery(id+"F0.wireOp",EDGE,"E23.right"),sQuery(id+"F0.wireOp",EDGE,"E24.top"),sQuery(id+"F0.wireOp",EDGE,"E24.left"),sQuery(id+"F0.wireOp",EDGE,"E24.right"),sQuery(id+"F0.wireOp",EDGE,"E25.top"),sQuery(id+"F0.wireOp",EDGE,"E25.left"),sQuery(id+"F0.wireOp",EDGE,"E25.right"),sQuery(id+"F0.wireOp",EDGE,"E26.top"),sQuery(id+"F0.wireOp",EDGE,"E26.left"),sQuery(id+"F0.wireOp",EDGE,"E26.right")])],"isStart":true})]});}
            var Q12;
            {var subQ0=sQuery(id+"F0.wireOp",EDGE,"E17.rect.bottom");Q12=makeQuery(id+"F1.opExtrude","CAP_EDGE",EDGE,{"disambiguationData":[OSD([subQ0]),TDD([makeQuery(id+"F0.imprint","IMPRINT",EDGE,{"disambiguationData":[TD([[makeQuery(id+"F0.imprint","INTERSECT",VERTEX,{"derivedFrom":[subQ0,sQuery(id+"F0.wireOp",EDGE,"E19.rect.right")]}),-1.0]])],"derivedFrom":subQ0})])],"isStart":true});}
            var Q13;
            {var subQ0=sQuery(id+"F0.wireOp",EDGE,"E17.rect.bottom");Q13=makeQuery(id+"F1.opExtrude","CAP_EDGE",EDGE,{"disambiguationData":[OSD([subQ0]),TDD([makeQuery(id+"F0.imprint","IMPRINT",EDGE,{"disambiguationData":[TD([[makeQuery(id+"F0.imprint","INTERSECT",VERTEX,{"derivedFrom":[subQ0,sQuery(id+"F0.wireOp",EDGE,"E19.rect.left")]}),1.0]])],"derivedFrom":subQ0})])],"isStart":true});}
            var Q14;
            {var subQ0=sQuery(id+"F0.wireOp",EDGE,"E19.rect.left");var subQ1=sQuery(id+"F0.wireOp",EDGE,"E17.rect.bottom");Q14=makeQuery(id+"F3.opFillet","BLEND_EDGE",EDGE,{"blendedFrom":[makeQuery(id+"F1.opExtrude","SWEPT_EDGE",EDGE,{"disambiguationData":[OSD([subQ1,subQ0])]}),makeQuery(id+"F1.opExtrude","CAP_FACE",FACE,{"disambiguationData":[OSD([sQuery(id+"F0.wireOp",EDGE,"E0"),sQuery(id+"F0.wireOp",EDGE,"E1"),sQuery(id+"F0.wireOp",EDGE,"E2"),sQuery(id+"F0.wireOp",EDGE,"E3"),sQuery(id+"F0.wireOp",EDGE,"E4"),sQuery(id+"F0.wireOp",EDGE,"E5"),sQuery(id+"F0.wireOp",EDGE,"E6"),sQuery(id+"F0.wireOp",EDGE,"E7"),sQuery(id+"F0.wireOp",EDGE,"E8"),sQuery(id+"F0.wireOp",EDGE,"E9"),sQuery(id+"F0.wireOp",EDGE,"E10"),sQuery(id+"F0.wireOp",EDGE,"E11"),sQuery(id+"F0.wireOp",EDGE,"E12"),sQuery(id+"F0.wireOp",EDGE,"E13"),sQuery(id+"F0.wireOp",EDGE,"E14"),sQuery(id+"F0.wireOp",EDGE,"E15"),subQ1,sQuery(id+"F0.wireOp",EDGE,"E17.rect.top"),sQuery(id+"F0.wireOp",EDGE,"E17.rect.left"),sQuery(id+"F0.wireOp",EDGE,"E17.rect.right"),sQuery(id+"F0.wireOp",EDGE,"E18.rect.bottom"),sQuery(id+"F0.wireOp",EDGE,"E18.rect.top"),sQuery(id+"F0.wireOp",EDGE,"E18.rect.left"),sQuery(id+"F0.wireOp",EDGE,"E18.rect.right"),subQ0,sQuery(id+"F0.wireOp",EDGE,"E19.rect.right"),sQuery(id+"F0.wireOp",EDGE,"E20.rect.bottom"),sQuery(id+"F0.wireOp",EDGE,"E20.rect.top"),sQuery(id+"F0.wireOp",EDGE,"E23.top"),sQuery(id+"F0.wireOp",EDGE,"E23.left"),sQuery(id+"F0.wireOp",EDGE,"E23.right"),sQuery(id+"F0.wireOp",EDGE,"E24.top"),sQuery(id+"F0.wireOp",EDGE,"E24.left"),sQuery(id+"F0.wireOp",EDGE,"E24.right"),sQuery(id+"F0.wireOp",EDGE,"E25.top"),sQuery(id+"F0.wireOp",EDGE,"E25.left"),sQuery(id+"F0.wireOp",EDGE,"E25.right"),sQuery(id+"F0.wireOp",EDGE,"E26.top"),sQuery(id+"F0.wireOp",EDGE,"E26.left"),sQuery(id+"F0.wireOp",EDGE,"E26.right")])],"isStart":true})],"blendedInto":[makeQuery(id+"F1.opExtrude","CAP_FACE",FACE,{"disambiguationData":[OSD([sQuery(id+"F0.wireOp",EDGE,"E0"),sQuery(id+"F0.wireOp",EDGE,"E1"),sQuery(id+"F0.wireOp",EDGE,"E2"),sQuery(id+"F0.wireOp",EDGE,"E3"),sQuery(id+"F0.wireOp",EDGE,"E4"),sQuery(id+"F0.wireOp",EDGE,"E5"),sQuery(id+"F0.wireOp",EDGE,"E6"),sQuery(id+"F0.wireOp",EDGE,"E7"),sQuery(id+"F0.wireOp",EDGE,"E8"),sQuery(id+"F0.wireOp",EDGE,"E9"),sQuery(id+"F0.wireOp",EDGE,"E10"),sQuery(id+"F0.wireOp",EDGE,"E11"),sQuery(id+"F0.wireOp",EDGE,"E12"),sQuery(id+"F0.wireOp",EDGE,"E13"),sQuery(id+"F0.wireOp",EDGE,"E14"),sQuery(id+"F0.wireOp",EDGE,"E15"),subQ1,sQuery(id+"F0.wireOp",EDGE,"E17.rect.top"),sQuery(id+"F0.wireOp",EDGE,"E17.rect.left"),sQuery(id+"F0.wireOp",EDGE,"E17.rect.right"),sQuery(id+"F0.wireOp",EDGE,"E18.rect.bottom"),sQuery(id+"F0.wireOp",EDGE,"E18.rect.top"),sQuery(id+"F0.wireOp",EDGE,"E18.rect.left"),sQuery(id+"F0.wireOp",EDGE,"E18.rect.right"),subQ0,sQuery(id+"F0.wireOp",EDGE,"E19.rect.right"),sQuery(id+"F0.wireOp",EDGE,"E20.rect.bottom"),sQuery(id+"F0.wireOp",EDGE,"E20.rect.top"),sQuery(id+"F0.wireOp",EDGE,"E23.top"),sQuery(id+"F0.wireOp",EDGE,"E23.left"),sQuery(id+"F0.wireOp",EDGE,"E23.right"),sQuery(id+"F0.wireOp",EDGE,"E24.top"),sQuery(id+"F0.wireOp",EDGE,"E24.left"),sQuery(id+"F0.wireOp",EDGE,"E24.right"),sQuery(id+"F0.wireOp",EDGE,"E25.top"),sQuery(id+"F0.wireOp",EDGE,"E25.left"),sQuery(id+"F0.wireOp",EDGE,"E25.right"),sQuery(id+"F0.wireOp",EDGE,"E26.top"),sQuery(id+"F0.wireOp",EDGE,"E26.left"),sQuery(id+"F0.wireOp",EDGE,"E26.right")])],"isStart":true})]});}
            var Q15;
            {var subQ0=sQuery(id+"F0.wireOp",EDGE,"E19.rect.left");Q15=makeQuery(id+"F1.opExtrude","CAP_EDGE",EDGE,{"disambiguationData":[OSD([subQ0]),TDD([makeQuery(id+"F0.imprint","IMPRINT",EDGE,{"disambiguationData":[TD([[makeQuery(id+"F0.imprint","INTERSECT",VERTEX,{"derivedFrom":[sQuery(id+"F0.wireOp",EDGE,"E10"),subQ0]}),-1.0]])],"derivedFrom":subQ0})])],"isStart":true});}
            var Q16;
            {var subQ0=sQuery(id+"F0.wireOp",EDGE,"E19.rect.left");var subQ1=sQuery(id+"F0.wireOp",EDGE,"E10");Q16=makeQuery(id+"F3.opFillet","BLEND_EDGE",EDGE,{"blendedFrom":[makeQuery(id+"F1.opExtrude","SWEPT_EDGE",EDGE,{"disambiguationData":[OSD([subQ1,subQ0])]}),makeQuery(id+"F1.opExtrude","CAP_FACE",FACE,{"disambiguationData":[OSD([sQuery(id+"F0.wireOp",EDGE,"E0"),sQuery(id+"F0.wireOp",EDGE,"E1"),sQuery(id+"F0.wireOp",EDGE,"E2"),sQuery(id+"F0.wireOp",EDGE,"E3"),sQuery(id+"F0.wireOp",EDGE,"E4"),sQuery(id+"F0.wireOp",EDGE,"E5"),sQuery(id+"F0.wireOp",EDGE,"E6"),sQuery(id+"F0.wireOp",EDGE,"E7"),sQuery(id+"F0.wireOp",EDGE,"E8"),sQuery(id+"F0.wireOp",EDGE,"E9"),subQ1,sQuery(id+"F0.wireOp",EDGE,"E11"),sQuery(id+"F0.wireOp",EDGE,"E12"),sQuery(id+"F0.wireOp",EDGE,"E13"),sQuery(id+"F0.wireOp",EDGE,"E14"),sQuery(id+"F0.wireOp",EDGE,"E15"),sQuery(id+"F0.wireOp",EDGE,"E17.rect.bottom"),sQuery(id+"F0.wireOp",EDGE,"E17.rect.top"),sQuery(id+"F0.wireOp",EDGE,"E17.rect.left"),sQuery(id+"F0.wireOp",EDGE,"E17.rect.right"),sQuery(id+"F0.wireOp",EDGE,"E18.rect.bottom"),sQuery(id+"F0.wireOp",EDGE,"E18.rect.top"),sQuery(id+"F0.wireOp",EDGE,"E18.rect.left"),sQuery(id+"F0.wireOp",EDGE,"E18.rect.right"),subQ0,sQuery(id+"F0.wireOp",EDGE,"E19.rect.right"),sQuery(id+"F0.wireOp",EDGE,"E20.rect.bottom"),sQuery(id+"F0.wireOp",EDGE,"E20.rect.top"),sQuery(id+"F0.wireOp",EDGE,"E23.top"),sQuery(id+"F0.wireOp",EDGE,"E23.left"),sQuery(id+"F0.wireOp",EDGE,"E23.right"),sQuery(id+"F0.wireOp",EDGE,"E24.top"),sQuery(id+"F0.wireOp",EDGE,"E24.left"),sQuery(id+"F0.wireOp",EDGE,"E24.right"),sQuery(id+"F0.wireOp",EDGE,"E25.top"),sQuery(id+"F0.wireOp",EDGE,"E25.left"),sQuery(id+"F0.wireOp",EDGE,"E25.right"),sQuery(id+"F0.wireOp",EDGE,"E26.top"),sQuery(id+"F0.wireOp",EDGE,"E26.left"),sQuery(id+"F0.wireOp",EDGE,"E26.right")])],"isStart":true})],"blendedInto":[makeQuery(id+"F1.opExtrude","CAP_FACE",FACE,{"disambiguationData":[OSD([sQuery(id+"F0.wireOp",EDGE,"E0"),sQuery(id+"F0.wireOp",EDGE,"E1"),sQuery(id+"F0.wireOp",EDGE,"E2"),sQuery(id+"F0.wireOp",EDGE,"E3"),sQuery(id+"F0.wireOp",EDGE,"E4"),sQuery(id+"F0.wireOp",EDGE,"E5"),sQuery(id+"F0.wireOp",EDGE,"E6"),sQuery(id+"F0.wireOp",EDGE,"E7"),sQuery(id+"F0.wireOp",EDGE,"E8"),sQuery(id+"F0.wireOp",EDGE,"E9"),subQ1,sQuery(id+"F0.wireOp",EDGE,"E11"),sQuery(id+"F0.wireOp",EDGE,"E12"),sQuery(id+"F0.wireOp",EDGE,"E13"),sQuery(id+"F0.wireOp",EDGE,"E14"),sQuery(id+"F0.wireOp",EDGE,"E15"),sQuery(id+"F0.wireOp",EDGE,"E17.rect.bottom"),sQuery(id+"F0.wireOp",EDGE,"E17.rect.top"),sQuery(id+"F0.wireOp",EDGE,"E17.rect.left"),sQuery(id+"F0.wireOp",EDGE,"E17.rect.right"),sQuery(id+"F0.wireOp",EDGE,"E18.rect.bottom"),sQuery(id+"F0.wireOp",EDGE,"E18.rect.top"),sQuery(id+"F0.wireOp",EDGE,"E18.rect.left"),sQuery(id+"F0.wireOp",EDGE,"E18.rect.right"),subQ0,sQuery(id+"F0.wireOp",EDGE,"E19.rect.right"),sQuery(id+"F0.wireOp",EDGE,"E20.rect.bottom"),sQuery(id+"F0.wireOp",EDGE,"E20.rect.top"),sQuery(id+"F0.wireOp",EDGE,"E23.top"),sQuery(id+"F0.wireOp",EDGE,"E23.left"),sQuery(id+"F0.wireOp",EDGE,"E23.right"),sQuery(id+"F0.wireOp",EDGE,"E24.top"),sQuery(id+"F0.wireOp",EDGE,"E24.left"),sQuery(id+"F0.wireOp",EDGE,"E24.right"),sQuery(id+"F0.wireOp",EDGE,"E25.top"),sQuery(id+"F0.wireOp",EDGE,"E25.left"),sQuery(id+"F0.wireOp",EDGE,"E25.right"),sQuery(id+"F0.wireOp",EDGE,"E26.top"),sQuery(id+"F0.wireOp",EDGE,"E26.left"),sQuery(id+"F0.wireOp",EDGE,"E26.right")])],"isStart":true})]});}
            var Q17;
            {var subQ0=sQuery(id+"F0.wireOp",EDGE,"E10");var subQ1=makeQuery(id+"F0.imprint","INTERSECT",VERTEX,{"disambiguationData":[OD(1.0)],"derivedFrom":[sQuery(id+"F0.wireOp",EDGE,"E7"),subQ0]});Q17=makeQuery(id+"F1.opExtrude","CAP_EDGE",EDGE,{"disambiguationData":[OSD([subQ0]),TDD([makeQuery(id+"F0.imprint","IMPRINT",EDGE,{"disambiguationData":[TD([[subQ1,1.0]])],"derivedFrom":subQ0}),makeQuery(id+"F0.imprint","IMPRINT",EDGE,{"disambiguationData":[TD([[makeQuery(id+"F0.imprint","INTERSECT",VERTEX,{"disambiguationData":[OD(1.0)],"derivedFrom":[sQuery(id+"F0.wireOp",EDGE,"E1"),subQ0]}),1.0]])],"derivedFrom":subQ0})])],"isStart":true});}
            var Q18;
            {var subQ0=sQuery(id+"F0.wireOp",EDGE,"E12");var subQ1=makeQuery(id+"F0.imprint","INTERSECT",VERTEX,{"disambiguationData":[OD(1.0)],"derivedFrom":[sQuery(id+"F0.wireOp",EDGE,"E7"),subQ0]});Q18=makeQuery(id+"F1.opExtrude","CAP_EDGE",EDGE,{"disambiguationData":[OSD([subQ0]),TDD([makeQuery(id+"F0.imprint","IMPRINT",EDGE,{"disambiguationData":[TD([[makeQuery(id+"F0.imprint","INTERSECT",VERTEX,{"disambiguationData":[OD(1.0)],"derivedFrom":[sQuery(id+"F0.wireOp",EDGE,"E1"),subQ0]}),-1.0]])],"derivedFrom":subQ0}),makeQuery(id+"F0.imprint","IMPRINT",EDGE,{"disambiguationData":[TD([[subQ1,-1.0]])],"derivedFrom":subQ0})])],"isStart":true});}
            var Q19;
            {var subQ0=sQuery(id+"F0.wireOp",EDGE,"E20.rect.bottom");var subQ1=sQuery(id+"F0.wireOp",EDGE,"E12");Q19=makeQuery(id+"F3.opFillet","BLEND_EDGE",EDGE,{"blendedFrom":[makeQuery(id+"F1.opExtrude","SWEPT_EDGE",EDGE,{"disambiguationData":[OSD([subQ1,subQ0])]}),makeQuery(id+"F1.opExtrude","CAP_FACE",FACE,{"disambiguationData":[OSD([sQuery(id+"F0.wireOp",EDGE,"E0"),sQuery(id+"F0.wireOp",EDGE,"E1"),sQuery(id+"F0.wireOp",EDGE,"E2"),sQuery(id+"F0.wireOp",EDGE,"E3"),sQuery(id+"F0.wireOp",EDGE,"E4"),sQuery(id+"F0.wireOp",EDGE,"E5"),sQuery(id+"F0.wireOp",EDGE,"E6"),sQuery(id+"F0.wireOp",EDGE,"E7"),sQuery(id+"F0.wireOp",EDGE,"E8"),sQuery(id+"F0.wireOp",EDGE,"E9"),sQuery(id+"F0.wireOp",EDGE,"E10"),sQuery(id+"F0.wireOp",EDGE,"E11"),subQ1,sQuery(id+"F0.wireOp",EDGE,"E13"),sQuery(id+"F0.wireOp",EDGE,"E14"),sQuery(id+"F0.wireOp",EDGE,"E15"),sQuery(id+"F0.wireOp",EDGE,"E17.rect.bottom"),sQuery(id+"F0.wireOp",EDGE,"E17.rect.top"),sQuery(id+"F0.wireOp",EDGE,"E17.rect.left"),sQuery(id+"F0.wireOp",EDGE,"E17.rect.right"),sQuery(id+"F0.wireOp",EDGE,"E18.rect.bottom"),sQuery(id+"F0.wireOp",EDGE,"E18.rect.top"),sQuery(id+"F0.wireOp",EDGE,"E18.rect.left"),sQuery(id+"F0.wireOp",EDGE,"E18.rect.right"),sQuery(id+"F0.wireOp",EDGE,"E19.rect.left"),sQuery(id+"F0.wireOp",EDGE,"E19.rect.right"),subQ0,sQuery(id+"F0.wireOp",EDGE,"E20.rect.top"),sQuery(id+"F0.wireOp",EDGE,"E23.top"),sQuery(id+"F0.wireOp",EDGE,"E23.left"),sQuery(id+"F0.wireOp",EDGE,"E23.right"),sQuery(id+"F0.wireOp",EDGE,"E24.top"),sQuery(id+"F0.wireOp",EDGE,"E24.left"),sQuery(id+"F0.wireOp",EDGE,"E24.right"),sQuery(id+"F0.wireOp",EDGE,"E25.top"),sQuery(id+"F0.wireOp",EDGE,"E25.left"),sQuery(id+"F0.wireOp",EDGE,"E25.right"),sQuery(id+"F0.wireOp",EDGE,"E26.top"),sQuery(id+"F0.wireOp",EDGE,"E26.left"),sQuery(id+"F0.wireOp",EDGE,"E26.right")])],"isStart":true})],"blendedInto":[makeQuery(id+"F1.opExtrude","CAP_FACE",FACE,{"disambiguationData":[OSD([sQuery(id+"F0.wireOp",EDGE,"E0"),sQuery(id+"F0.wireOp",EDGE,"E1"),sQuery(id+"F0.wireOp",EDGE,"E2"),sQuery(id+"F0.wireOp",EDGE,"E3"),sQuery(id+"F0.wireOp",EDGE,"E4"),sQuery(id+"F0.wireOp",EDGE,"E5"),sQuery(id+"F0.wireOp",EDGE,"E6"),sQuery(id+"F0.wireOp",EDGE,"E7"),sQuery(id+"F0.wireOp",EDGE,"E8"),sQuery(id+"F0.wireOp",EDGE,"E9"),sQuery(id+"F0.wireOp",EDGE,"E10"),sQuery(id+"F0.wireOp",EDGE,"E11"),subQ1,sQuery(id+"F0.wireOp",EDGE,"E13"),sQuery(id+"F0.wireOp",EDGE,"E14"),sQuery(id+"F0.wireOp",EDGE,"E15"),sQuery(id+"F0.wireOp",EDGE,"E17.rect.bottom"),sQuery(id+"F0.wireOp",EDGE,"E17.rect.top"),sQuery(id+"F0.wireOp",EDGE,"E17.rect.left"),sQuery(id+"F0.wireOp",EDGE,"E17.rect.right"),sQuery(id+"F0.wireOp",EDGE,"E18.rect.bottom"),sQuery(id+"F0.wireOp",EDGE,"E18.rect.top"),sQuery(id+"F0.wireOp",EDGE,"E18.rect.left"),sQuery(id+"F0.wireOp",EDGE,"E18.rect.right"),sQuery(id+"F0.wireOp",EDGE,"E19.rect.left"),sQuery(id+"F0.wireOp",EDGE,"E19.rect.right"),subQ0,sQuery(id+"F0.wireOp",EDGE,"E20.rect.top"),sQuery(id+"F0.wireOp",EDGE,"E23.top"),sQuery(id+"F0.wireOp",EDGE,"E23.left"),sQuery(id+"F0.wireOp",EDGE,"E23.right"),sQuery(id+"F0.wireOp",EDGE,"E24.top"),sQuery(id+"F0.wireOp",EDGE,"E24.left"),sQuery(id+"F0.wireOp",EDGE,"E24.right"),sQuery(id+"F0.wireOp",EDGE,"E25.top"),sQuery(id+"F0.wireOp",EDGE,"E25.left"),sQuery(id+"F0.wireOp",EDGE,"E25.right"),sQuery(id+"F0.wireOp",EDGE,"E26.top"),sQuery(id+"F0.wireOp",EDGE,"E26.left"),sQuery(id+"F0.wireOp",EDGE,"E26.right")])],"isStart":true})]});}
            var Q20;
            {var subQ0=sQuery(id+"F0.wireOp",EDGE,"E20.rect.bottom");Q20=makeQuery(id+"F1.opExtrude","CAP_EDGE",EDGE,{"disambiguationData":[OSD([subQ0]),TDD([makeQuery(id+"F0.imprint","IMPRINT",EDGE,{"disambiguationData":[TD([[makeQuery(id+"F0.imprint","INTERSECT",VERTEX,{"derivedFrom":[sQuery(id+"F0.wireOp",EDGE,"E12"),subQ0]}),-1.0]])],"derivedFrom":subQ0})])],"isStart":true});}
            var Q21;
            {var subQ0=sQuery(id+"F0.wireOp",EDGE,"E20.rect.bottom");var subQ1=sQuery(id+"F0.wireOp",EDGE,"E17.rect.left");Q21=makeQuery(id+"F3.opFillet","BLEND_EDGE",EDGE,{"blendedFrom":[makeQuery(id+"F1.opExtrude","SWEPT_EDGE",EDGE,{"disambiguationData":[OSD([subQ1,subQ0])]}),makeQuery(id+"F1.opExtrude","CAP_FACE",FACE,{"disambiguationData":[OSD([sQuery(id+"F0.wireOp",EDGE,"E0"),sQuery(id+"F0.wireOp",EDGE,"E1"),sQuery(id+"F0.wireOp",EDGE,"E2"),sQuery(id+"F0.wireOp",EDGE,"E3"),sQuery(id+"F0.wireOp",EDGE,"E4"),sQuery(id+"F0.wireOp",EDGE,"E5"),sQuery(id+"F0.wireOp",EDGE,"E6"),sQuery(id+"F0.wireOp",EDGE,"E7"),sQuery(id+"F0.wireOp",EDGE,"E8"),sQuery(id+"F0.wireOp",EDGE,"E9"),sQuery(id+"F0.wireOp",EDGE,"E10"),sQuery(id+"F0.wireOp",EDGE,"E11"),sQuery(id+"F0.wireOp",EDGE,"E12"),sQuery(id+"F0.wireOp",EDGE,"E13"),sQuery(id+"F0.wireOp",EDGE,"E14"),sQuery(id+"F0.wireOp",EDGE,"E15"),sQuery(id+"F0.wireOp",EDGE,"E17.rect.bottom"),sQuery(id+"F0.wireOp",EDGE,"E17.rect.top"),subQ1,sQuery(id+"F0.wireOp",EDGE,"E17.rect.right"),sQuery(id+"F0.wireOp",EDGE,"E18.rect.bottom"),sQuery(id+"F0.wireOp",EDGE,"E18.rect.top"),sQuery(id+"F0.wireOp",EDGE,"E18.rect.left"),sQuery(id+"F0.wireOp",EDGE,"E18.rect.right"),sQuery(id+"F0.wireOp",EDGE,"E19.rect.left"),sQuery(id+"F0.wireOp",EDGE,"E19.rect.right"),subQ0,sQuery(id+"F0.wireOp",EDGE,"E20.rect.top"),sQuery(id+"F0.wireOp",EDGE,"E23.top"),sQuery(id+"F0.wireOp",EDGE,"E23.left"),sQuery(id+"F0.wireOp",EDGE,"E23.right"),sQuery(id+"F0.wireOp",EDGE,"E24.top"),sQuery(id+"F0.wireOp",EDGE,"E24.left"),sQuery(id+"F0.wireOp",EDGE,"E24.right"),sQuery(id+"F0.wireOp",EDGE,"E25.top"),sQuery(id+"F0.wireOp",EDGE,"E25.left"),sQuery(id+"F0.wireOp",EDGE,"E25.right"),sQuery(id+"F0.wireOp",EDGE,"E26.top"),sQuery(id+"F0.wireOp",EDGE,"E26.left"),sQuery(id+"F0.wireOp",EDGE,"E26.right")])],"isStart":true})],"blendedInto":[makeQuery(id+"F1.opExtrude","CAP_FACE",FACE,{"disambiguationData":[OSD([sQuery(id+"F0.wireOp",EDGE,"E0"),sQuery(id+"F0.wireOp",EDGE,"E1"),sQuery(id+"F0.wireOp",EDGE,"E2"),sQuery(id+"F0.wireOp",EDGE,"E3"),sQuery(id+"F0.wireOp",EDGE,"E4"),sQuery(id+"F0.wireOp",EDGE,"E5"),sQuery(id+"F0.wireOp",EDGE,"E6"),sQuery(id+"F0.wireOp",EDGE,"E7"),sQuery(id+"F0.wireOp",EDGE,"E8"),sQuery(id+"F0.wireOp",EDGE,"E9"),sQuery(id+"F0.wireOp",EDGE,"E10"),sQuery(id+"F0.wireOp",EDGE,"E11"),sQuery(id+"F0.wireOp",EDGE,"E12"),sQuery(id+"F0.wireOp",EDGE,"E13"),sQuery(id+"F0.wireOp",EDGE,"E14"),sQuery(id+"F0.wireOp",EDGE,"E15"),sQuery(id+"F0.wireOp",EDGE,"E17.rect.bottom"),sQuery(id+"F0.wireOp",EDGE,"E17.rect.top"),subQ1,sQuery(id+"F0.wireOp",EDGE,"E17.rect.right"),sQuery(id+"F0.wireOp",EDGE,"E18.rect.bottom"),sQuery(id+"F0.wireOp",EDGE,"E18.rect.top"),sQuery(id+"F0.wireOp",EDGE,"E18.rect.left"),sQuery(id+"F0.wireOp",EDGE,"E18.rect.right"),sQuery(id+"F0.wireOp",EDGE,"E19.rect.left"),sQuery(id+"F0.wireOp",EDGE,"E19.rect.right"),subQ0,sQuery(id+"F0.wireOp",EDGE,"E20.rect.top"),sQuery(id+"F0.wireOp",EDGE,"E23.top"),sQuery(id+"F0.wireOp",EDGE,"E23.left"),sQuery(id+"F0.wireOp",EDGE,"E23.right"),sQuery(id+"F0.wireOp",EDGE,"E24.top"),sQuery(id+"F0.wireOp",EDGE,"E24.left"),sQuery(id+"F0.wireOp",EDGE,"E24.right"),sQuery(id+"F0.wireOp",EDGE,"E25.top"),sQuery(id+"F0.wireOp",EDGE,"E25.left"),sQuery(id+"F0.wireOp",EDGE,"E25.right"),sQuery(id+"F0.wireOp",EDGE,"E26.top"),sQuery(id+"F0.wireOp",EDGE,"E26.left"),sQuery(id+"F0.wireOp",EDGE,"E26.right")])],"isStart":true})]});}
            var Q22;
            {var subQ0=sQuery(id+"F0.wireOp",EDGE,"E20.rect.top");var subQ1=sQuery(id+"F0.wireOp",EDGE,"E17.rect.left");Q22=makeQuery(id+"F3.opFillet","BLEND_EDGE",EDGE,{"blendedFrom":[makeQuery(id+"F1.opExtrude","SWEPT_EDGE",EDGE,{"disambiguationData":[OSD([subQ1,subQ0])]}),makeQuery(id+"F1.opExtrude","CAP_FACE",FACE,{"disambiguationData":[OSD([sQuery(id+"F0.wireOp",EDGE,"E0"),sQuery(id+"F0.wireOp",EDGE,"E1"),sQuery(id+"F0.wireOp",EDGE,"E2"),sQuery(id+"F0.wireOp",EDGE,"E3"),sQuery(id+"F0.wireOp",EDGE,"E4"),sQuery(id+"F0.wireOp",EDGE,"E5"),sQuery(id+"F0.wireOp",EDGE,"E6"),sQuery(id+"F0.wireOp",EDGE,"E7"),sQuery(id+"F0.wireOp",EDGE,"E8"),sQuery(id+"F0.wireOp",EDGE,"E9"),sQuery(id+"F0.wireOp",EDGE,"E10"),sQuery(id+"F0.wireOp",EDGE,"E11"),sQuery(id+"F0.wireOp",EDGE,"E12"),sQuery(id+"F0.wireOp",EDGE,"E13"),sQuery(id+"F0.wireOp",EDGE,"E14"),sQuery(id+"F0.wireOp",EDGE,"E15"),sQuery(id+"F0.wireOp",EDGE,"E17.rect.bottom"),sQuery(id+"F0.wireOp",EDGE,"E17.rect.top"),subQ1,sQuery(id+"F0.wireOp",EDGE,"E17.rect.right"),sQuery(id+"F0.wireOp",EDGE,"E18.rect.bottom"),sQuery(id+"F0.wireOp",EDGE,"E18.rect.top"),sQuery(id+"F0.wireOp",EDGE,"E18.rect.left"),sQuery(id+"F0.wireOp",EDGE,"E18.rect.right"),sQuery(id+"F0.wireOp",EDGE,"E19.rect.left"),sQuery(id+"F0.wireOp",EDGE,"E19.rect.right"),sQuery(id+"F0.wireOp",EDGE,"E20.rect.bottom"),subQ0,sQuery(id+"F0.wireOp",EDGE,"E23.top"),sQuery(id+"F0.wireOp",EDGE,"E23.left"),sQuery(id+"F0.wireOp",EDGE,"E23.right"),sQuery(id+"F0.wireOp",EDGE,"E24.top"),sQuery(id+"F0.wireOp",EDGE,"E24.left"),sQuery(id+"F0.wireOp",EDGE,"E24.right"),sQuery(id+"F0.wireOp",EDGE,"E25.top"),sQuery(id+"F0.wireOp",EDGE,"E25.left"),sQuery(id+"F0.wireOp",EDGE,"E25.right"),sQuery(id+"F0.wireOp",EDGE,"E26.top"),sQuery(id+"F0.wireOp",EDGE,"E26.left"),sQuery(id+"F0.wireOp",EDGE,"E26.right")])],"isStart":true})],"blendedInto":[makeQuery(id+"F1.opExtrude","CAP_FACE",FACE,{"disambiguationData":[OSD([sQuery(id+"F0.wireOp",EDGE,"E0"),sQuery(id+"F0.wireOp",EDGE,"E1"),sQuery(id+"F0.wireOp",EDGE,"E2"),sQuery(id+"F0.wireOp",EDGE,"E3"),sQuery(id+"F0.wireOp",EDGE,"E4"),sQuery(id+"F0.wireOp",EDGE,"E5"),sQuery(id+"F0.wireOp",EDGE,"E6"),sQuery(id+"F0.wireOp",EDGE,"E7"),sQuery(id+"F0.wireOp",EDGE,"E8"),sQuery(id+"F0.wireOp",EDGE,"E9"),sQuery(id+"F0.wireOp",EDGE,"E10"),sQuery(id+"F0.wireOp",EDGE,"E11"),sQuery(id+"F0.wireOp",EDGE,"E12"),sQuery(id+"F0.wireOp",EDGE,"E13"),sQuery(id+"F0.wireOp",EDGE,"E14"),sQuery(id+"F0.wireOp",EDGE,"E15"),sQuery(id+"F0.wireOp",EDGE,"E17.rect.bottom"),sQuery(id+"F0.wireOp",EDGE,"E17.rect.top"),subQ1,sQuery(id+"F0.wireOp",EDGE,"E17.rect.right"),sQuery(id+"F0.wireOp",EDGE,"E18.rect.bottom"),sQuery(id+"F0.wireOp",EDGE,"E18.rect.top"),sQuery(id+"F0.wireOp",EDGE,"E18.rect.left"),sQuery(id+"F0.wireOp",EDGE,"E18.rect.right"),sQuery(id+"F0.wireOp",EDGE,"E19.rect.left"),sQuery(id+"F0.wireOp",EDGE,"E19.rect.right"),sQuery(id+"F0.wireOp",EDGE,"E20.rect.bottom"),subQ0,sQuery(id+"F0.wireOp",EDGE,"E23.top"),sQuery(id+"F0.wireOp",EDGE,"E23.left"),sQuery(id+"F0.wireOp",EDGE,"E23.right"),sQuery(id+"F0.wireOp",EDGE,"E24.top"),sQuery(id+"F0.wireOp",EDGE,"E24.left"),sQuery(id+"F0.wireOp",EDGE,"E24.right"),sQuery(id+"F0.wireOp",EDGE,"E25.top"),sQuery(id+"F0.wireOp",EDGE,"E25.left"),sQuery(id+"F0.wireOp",EDGE,"E25.right"),sQuery(id+"F0.wireOp",EDGE,"E26.top"),sQuery(id+"F0.wireOp",EDGE,"E26.left"),sQuery(id+"F0.wireOp",EDGE,"E26.right")])],"isStart":true})]});}
            var Q23;
            {var subQ0=sQuery(id+"F0.wireOp",EDGE,"E20.rect.top");Q23=makeQuery(id+"F1.opExtrude","CAP_EDGE",EDGE,{"disambiguationData":[OSD([subQ0]),TDD([makeQuery(id+"F0.imprint","IMPRINT",EDGE,{"disambiguationData":[TD([[makeQuery(id+"F0.imprint","INTERSECT",VERTEX,{"derivedFrom":[sQuery(id+"F0.wireOp",EDGE,"E12"),subQ0]}),-1.0]])],"derivedFrom":subQ0})])],"isStart":true});}
            var Q24;
            {var subQ0=sQuery(id+"F0.wireOp",EDGE,"E20.rect.top");var subQ1=sQuery(id+"F0.wireOp",EDGE,"E12");Q24=makeQuery(id+"F3.opFillet","BLEND_EDGE",EDGE,{"blendedFrom":[makeQuery(id+"F1.opExtrude","SWEPT_EDGE",EDGE,{"disambiguationData":[OSD([subQ1,subQ0])]}),makeQuery(id+"F1.opExtrude","CAP_FACE",FACE,{"disambiguationData":[OSD([sQuery(id+"F0.wireOp",EDGE,"E0"),sQuery(id+"F0.wireOp",EDGE,"E1"),sQuery(id+"F0.wireOp",EDGE,"E2"),sQuery(id+"F0.wireOp",EDGE,"E3"),sQuery(id+"F0.wireOp",EDGE,"E4"),sQuery(id+"F0.wireOp",EDGE,"E5"),sQuery(id+"F0.wireOp",EDGE,"E6"),sQuery(id+"F0.wireOp",EDGE,"E7"),sQuery(id+"F0.wireOp",EDGE,"E8"),sQuery(id+"F0.wireOp",EDGE,"E9"),sQuery(id+"F0.wireOp",EDGE,"E10"),sQuery(id+"F0.wireOp",EDGE,"E11"),subQ1,sQuery(id+"F0.wireOp",EDGE,"E13"),sQuery(id+"F0.wireOp",EDGE,"E14"),sQuery(id+"F0.wireOp",EDGE,"E15"),sQuery(id+"F0.wireOp",EDGE,"E17.rect.bottom"),sQuery(id+"F0.wireOp",EDGE,"E17.rect.top"),sQuery(id+"F0.wireOp",EDGE,"E17.rect.left"),sQuery(id+"F0.wireOp",EDGE,"E17.rect.right"),sQuery(id+"F0.wireOp",EDGE,"E18.rect.bottom"),sQuery(id+"F0.wireOp",EDGE,"E18.rect.top"),sQuery(id+"F0.wireOp",EDGE,"E18.rect.left"),sQuery(id+"F0.wireOp",EDGE,"E18.rect.right"),sQuery(id+"F0.wireOp",EDGE,"E19.rect.left"),sQuery(id+"F0.wireOp",EDGE,"E19.rect.right"),sQuery(id+"F0.wireOp",EDGE,"E20.rect.bottom"),subQ0,sQuery(id+"F0.wireOp",EDGE,"E23.top"),sQuery(id+"F0.wireOp",EDGE,"E23.left"),sQuery(id+"F0.wireOp",EDGE,"E23.right"),sQuery(id+"F0.wireOp",EDGE,"E24.top"),sQuery(id+"F0.wireOp",EDGE,"E24.left"),sQuery(id+"F0.wireOp",EDGE,"E24.right"),sQuery(id+"F0.wireOp",EDGE,"E25.top"),sQuery(id+"F0.wireOp",EDGE,"E25.left"),sQuery(id+"F0.wireOp",EDGE,"E25.right"),sQuery(id+"F0.wireOp",EDGE,"E26.top"),sQuery(id+"F0.wireOp",EDGE,"E26.left"),sQuery(id+"F0.wireOp",EDGE,"E26.right")])],"isStart":true})],"blendedInto":[makeQuery(id+"F1.opExtrude","CAP_FACE",FACE,{"disambiguationData":[OSD([sQuery(id+"F0.wireOp",EDGE,"E0"),sQuery(id+"F0.wireOp",EDGE,"E1"),sQuery(id+"F0.wireOp",EDGE,"E2"),sQuery(id+"F0.wireOp",EDGE,"E3"),sQuery(id+"F0.wireOp",EDGE,"E4"),sQuery(id+"F0.wireOp",EDGE,"E5"),sQuery(id+"F0.wireOp",EDGE,"E6"),sQuery(id+"F0.wireOp",EDGE,"E7"),sQuery(id+"F0.wireOp",EDGE,"E8"),sQuery(id+"F0.wireOp",EDGE,"E9"),sQuery(id+"F0.wireOp",EDGE,"E10"),sQuery(id+"F0.wireOp",EDGE,"E11"),subQ1,sQuery(id+"F0.wireOp",EDGE,"E13"),sQuery(id+"F0.wireOp",EDGE,"E14"),sQuery(id+"F0.wireOp",EDGE,"E15"),sQuery(id+"F0.wireOp",EDGE,"E17.rect.bottom"),sQuery(id+"F0.wireOp",EDGE,"E17.rect.top"),sQuery(id+"F0.wireOp",EDGE,"E17.rect.left"),sQuery(id+"F0.wireOp",EDGE,"E17.rect.right"),sQuery(id+"F0.wireOp",EDGE,"E18.rect.bottom"),sQuery(id+"F0.wireOp",EDGE,"E18.rect.top"),sQuery(id+"F0.wireOp",EDGE,"E18.rect.left"),sQuery(id+"F0.wireOp",EDGE,"E18.rect.right"),sQuery(id+"F0.wireOp",EDGE,"E19.rect.left"),sQuery(id+"F0.wireOp",EDGE,"E19.rect.right"),sQuery(id+"F0.wireOp",EDGE,"E20.rect.bottom"),subQ0,sQuery(id+"F0.wireOp",EDGE,"E23.top"),sQuery(id+"F0.wireOp",EDGE,"E23.left"),sQuery(id+"F0.wireOp",EDGE,"E23.right"),sQuery(id+"F0.wireOp",EDGE,"E24.top"),sQuery(id+"F0.wireOp",EDGE,"E24.left"),sQuery(id+"F0.wireOp",EDGE,"E24.right"),sQuery(id+"F0.wireOp",EDGE,"E25.top"),sQuery(id+"F0.wireOp",EDGE,"E25.left"),sQuery(id+"F0.wireOp",EDGE,"E25.right"),sQuery(id+"F0.wireOp",EDGE,"E26.top"),sQuery(id+"F0.wireOp",EDGE,"E26.left"),sQuery(id+"F0.wireOp",EDGE,"E26.right")])],"isStart":true})]});}
            var Q25;
            {var subQ0=sQuery(id+"F0.wireOp",EDGE,"E12");var subQ1=makeQuery(id+"F0.imprint","INTERSECT",VERTEX,{"disambiguationData":[OD(0.0)],"derivedFrom":[sQuery(id+"F0.wireOp",EDGE,"E6"),subQ0]});Q25=makeQuery(id+"F1.opExtrude","CAP_EDGE",EDGE,{"disambiguationData":[OSD([subQ0]),TDD([makeQuery(id+"F0.imprint","IMPRINT",EDGE,{"disambiguationData":[TD([[subQ1,1.0]])],"derivedFrom":subQ0}),makeQuery(id+"F0.imprint","IMPRINT",EDGE,{"disambiguationData":[TD([[makeQuery(id+"F0.imprint","INTERSECT",VERTEX,{"disambiguationData":[OD(0.0)],"derivedFrom":[sQuery(id+"F0.wireOp",EDGE,"E2"),subQ0]}),1.0]])],"derivedFrom":subQ0})])],"isStart":true});}
            var Q26;
            {var subQ0=sQuery(id+"F0.wireOp",EDGE,"E14");var subQ1=makeQuery(id+"F0.imprint","INTERSECT",VERTEX,{"disambiguationData":[OD(0.0)],"derivedFrom":[sQuery(id+"F0.wireOp",EDGE,"E6"),subQ0]});Q26=makeQuery(id+"F1.opExtrude","CAP_EDGE",EDGE,{"disambiguationData":[OSD([subQ0]),TDD([makeQuery(id+"F0.imprint","IMPRINT",EDGE,{"disambiguationData":[TD([[makeQuery(id+"F0.imprint","INTERSECT",VERTEX,{"disambiguationData":[OD(0.0)],"derivedFrom":[sQuery(id+"F0.wireOp",EDGE,"E2"),subQ0]}),-1.0]])],"derivedFrom":subQ0}),makeQuery(id+"F0.imprint","IMPRINT",EDGE,{"disambiguationData":[TD([[subQ1,-1.0]])],"derivedFrom":subQ0})])],"isStart":true});}
            var Q27;
            {var subQ0=sQuery(id+"F0.wireOp",EDGE,"E19.rect.left");var subQ1=sQuery(id+"F0.wireOp",EDGE,"E14");Q27=makeQuery(id+"F3.opFillet","BLEND_EDGE",EDGE,{"blendedFrom":[makeQuery(id+"F1.opExtrude","SWEPT_EDGE",EDGE,{"disambiguationData":[OSD([subQ1,subQ0])]}),makeQuery(id+"F1.opExtrude","CAP_FACE",FACE,{"disambiguationData":[OSD([sQuery(id+"F0.wireOp",EDGE,"E0"),sQuery(id+"F0.wireOp",EDGE,"E1"),sQuery(id+"F0.wireOp",EDGE,"E2"),sQuery(id+"F0.wireOp",EDGE,"E3"),sQuery(id+"F0.wireOp",EDGE,"E4"),sQuery(id+"F0.wireOp",EDGE,"E5"),sQuery(id+"F0.wireOp",EDGE,"E6"),sQuery(id+"F0.wireOp",EDGE,"E7"),sQuery(id+"F0.wireOp",EDGE,"E8"),sQuery(id+"F0.wireOp",EDGE,"E9"),sQuery(id+"F0.wireOp",EDGE,"E10"),sQuery(id+"F0.wireOp",EDGE,"E11"),sQuery(id+"F0.wireOp",EDGE,"E12"),sQuery(id+"F0.wireOp",EDGE,"E13"),subQ1,sQuery(id+"F0.wireOp",EDGE,"E15"),sQuery(id+"F0.wireOp",EDGE,"E17.rect.bottom"),sQuery(id+"F0.wireOp",EDGE,"E17.rect.top"),sQuery(id+"F0.wireOp",EDGE,"E17.rect.left"),sQuery(id+"F0.wireOp",EDGE,"E17.rect.right"),sQuery(id+"F0.wireOp",EDGE,"E18.rect.bottom"),sQuery(id+"F0.wireOp",EDGE,"E18.rect.top"),sQuery(id+"F0.wireOp",EDGE,"E18.rect.left"),sQuery(id+"F0.wireOp",EDGE,"E18.rect.right"),subQ0,sQuery(id+"F0.wireOp",EDGE,"E19.rect.right"),sQuery(id+"F0.wireOp",EDGE,"E20.rect.bottom"),sQuery(id+"F0.wireOp",EDGE,"E20.rect.top"),sQuery(id+"F0.wireOp",EDGE,"E23.top"),sQuery(id+"F0.wireOp",EDGE,"E23.left"),sQuery(id+"F0.wireOp",EDGE,"E23.right"),sQuery(id+"F0.wireOp",EDGE,"E24.top"),sQuery(id+"F0.wireOp",EDGE,"E24.left"),sQuery(id+"F0.wireOp",EDGE,"E24.right"),sQuery(id+"F0.wireOp",EDGE,"E25.top"),sQuery(id+"F0.wireOp",EDGE,"E25.left"),sQuery(id+"F0.wireOp",EDGE,"E25.right"),sQuery(id+"F0.wireOp",EDGE,"E26.top"),sQuery(id+"F0.wireOp",EDGE,"E26.left"),sQuery(id+"F0.wireOp",EDGE,"E26.right")])],"isStart":true})],"blendedInto":[makeQuery(id+"F1.opExtrude","CAP_FACE",FACE,{"disambiguationData":[OSD([sQuery(id+"F0.wireOp",EDGE,"E0"),sQuery(id+"F0.wireOp",EDGE,"E1"),sQuery(id+"F0.wireOp",EDGE,"E2"),sQuery(id+"F0.wireOp",EDGE,"E3"),sQuery(id+"F0.wireOp",EDGE,"E4"),sQuery(id+"F0.wireOp",EDGE,"E5"),sQuery(id+"F0.wireOp",EDGE,"E6"),sQuery(id+"F0.wireOp",EDGE,"E7"),sQuery(id+"F0.wireOp",EDGE,"E8"),sQuery(id+"F0.wireOp",EDGE,"E9"),sQuery(id+"F0.wireOp",EDGE,"E10"),sQuery(id+"F0.wireOp",EDGE,"E11"),sQuery(id+"F0.wireOp",EDGE,"E12"),sQuery(id+"F0.wireOp",EDGE,"E13"),subQ1,sQuery(id+"F0.wireOp",EDGE,"E15"),sQuery(id+"F0.wireOp",EDGE,"E17.rect.bottom"),sQuery(id+"F0.wireOp",EDGE,"E17.rect.top"),sQuery(id+"F0.wireOp",EDGE,"E17.rect.left"),sQuery(id+"F0.wireOp",EDGE,"E17.rect.right"),sQuery(id+"F0.wireOp",EDGE,"E18.rect.bottom"),sQuery(id+"F0.wireOp",EDGE,"E18.rect.top"),sQuery(id+"F0.wireOp",EDGE,"E18.rect.left"),sQuery(id+"F0.wireOp",EDGE,"E18.rect.right"),subQ0,sQuery(id+"F0.wireOp",EDGE,"E19.rect.right"),sQuery(id+"F0.wireOp",EDGE,"E20.rect.bottom"),sQuery(id+"F0.wireOp",EDGE,"E20.rect.top"),sQuery(id+"F0.wireOp",EDGE,"E23.top"),sQuery(id+"F0.wireOp",EDGE,"E23.left"),sQuery(id+"F0.wireOp",EDGE,"E23.right"),sQuery(id+"F0.wireOp",EDGE,"E24.top"),sQuery(id+"F0.wireOp",EDGE,"E24.left"),sQuery(id+"F0.wireOp",EDGE,"E24.right"),sQuery(id+"F0.wireOp",EDGE,"E25.top"),sQuery(id+"F0.wireOp",EDGE,"E25.left"),sQuery(id+"F0.wireOp",EDGE,"E25.right"),sQuery(id+"F0.wireOp",EDGE,"E26.top"),sQuery(id+"F0.wireOp",EDGE,"E26.left"),sQuery(id+"F0.wireOp",EDGE,"E26.right")])],"isStart":true})]});}
            var Q28;
            {var subQ0=sQuery(id+"F0.wireOp",EDGE,"E19.rect.left");Q28=makeQuery(id+"F1.opExtrude","CAP_EDGE",EDGE,{"disambiguationData":[OSD([subQ0]),TDD([makeQuery(id+"F0.imprint","IMPRINT",EDGE,{"disambiguationData":[TD([[makeQuery(id+"F0.imprint","INTERSECT",VERTEX,{"derivedFrom":[sQuery(id+"F0.wireOp",EDGE,"E14"),subQ0]}),1.0]])],"derivedFrom":subQ0})])],"isStart":true});}
            var Q29;
            {var subQ0=sQuery(id+"F0.wireOp",EDGE,"E19.rect.left");var subQ1=sQuery(id+"F0.wireOp",EDGE,"E17.rect.top");Q29=makeQuery(id+"F3.opFillet","BLEND_EDGE",EDGE,{"blendedFrom":[makeQuery(id+"F1.opExtrude","SWEPT_EDGE",EDGE,{"disambiguationData":[OSD([subQ1,subQ0])]}),makeQuery(id+"F1.opExtrude","CAP_FACE",FACE,{"disambiguationData":[OSD([sQuery(id+"F0.wireOp",EDGE,"E0"),sQuery(id+"F0.wireOp",EDGE,"E1"),sQuery(id+"F0.wireOp",EDGE,"E2"),sQuery(id+"F0.wireOp",EDGE,"E3"),sQuery(id+"F0.wireOp",EDGE,"E4"),sQuery(id+"F0.wireOp",EDGE,"E5"),sQuery(id+"F0.wireOp",EDGE,"E6"),sQuery(id+"F0.wireOp",EDGE,"E7"),sQuery(id+"F0.wireOp",EDGE,"E8"),sQuery(id+"F0.wireOp",EDGE,"E9"),sQuery(id+"F0.wireOp",EDGE,"E10"),sQuery(id+"F0.wireOp",EDGE,"E11"),sQuery(id+"F0.wireOp",EDGE,"E12"),sQuery(id+"F0.wireOp",EDGE,"E13"),sQuery(id+"F0.wireOp",EDGE,"E14"),sQuery(id+"F0.wireOp",EDGE,"E15"),sQuery(id+"F0.wireOp",EDGE,"E17.rect.bottom"),subQ1,sQuery(id+"F0.wireOp",EDGE,"E17.rect.left"),sQuery(id+"F0.wireOp",EDGE,"E17.rect.right"),sQuery(id+"F0.wireOp",EDGE,"E18.rect.bottom"),sQuery(id+"F0.wireOp",EDGE,"E18.rect.top"),sQuery(id+"F0.wireOp",EDGE,"E18.rect.left"),sQuery(id+"F0.wireOp",EDGE,"E18.rect.right"),subQ0,sQuery(id+"F0.wireOp",EDGE,"E19.rect.right"),sQuery(id+"F0.wireOp",EDGE,"E20.rect.bottom"),sQuery(id+"F0.wireOp",EDGE,"E20.rect.top"),sQuery(id+"F0.wireOp",EDGE,"E23.top"),sQuery(id+"F0.wireOp",EDGE,"E23.left"),sQuery(id+"F0.wireOp",EDGE,"E23.right"),sQuery(id+"F0.wireOp",EDGE,"E24.top"),sQuery(id+"F0.wireOp",EDGE,"E24.left"),sQuery(id+"F0.wireOp",EDGE,"E24.right"),sQuery(id+"F0.wireOp",EDGE,"E25.top"),sQuery(id+"F0.wireOp",EDGE,"E25.left"),sQuery(id+"F0.wireOp",EDGE,"E25.right"),sQuery(id+"F0.wireOp",EDGE,"E26.top"),sQuery(id+"F0.wireOp",EDGE,"E26.left"),sQuery(id+"F0.wireOp",EDGE,"E26.right")])],"isStart":true})],"blendedInto":[makeQuery(id+"F1.opExtrude","CAP_FACE",FACE,{"disambiguationData":[OSD([sQuery(id+"F0.wireOp",EDGE,"E0"),sQuery(id+"F0.wireOp",EDGE,"E1"),sQuery(id+"F0.wireOp",EDGE,"E2"),sQuery(id+"F0.wireOp",EDGE,"E3"),sQuery(id+"F0.wireOp",EDGE,"E4"),sQuery(id+"F0.wireOp",EDGE,"E5"),sQuery(id+"F0.wireOp",EDGE,"E6"),sQuery(id+"F0.wireOp",EDGE,"E7"),sQuery(id+"F0.wireOp",EDGE,"E8"),sQuery(id+"F0.wireOp",EDGE,"E9"),sQuery(id+"F0.wireOp",EDGE,"E10"),sQuery(id+"F0.wireOp",EDGE,"E11"),sQuery(id+"F0.wireOp",EDGE,"E12"),sQuery(id+"F0.wireOp",EDGE,"E13"),sQuery(id+"F0.wireOp",EDGE,"E14"),sQuery(id+"F0.wireOp",EDGE,"E15"),sQuery(id+"F0.wireOp",EDGE,"E17.rect.bottom"),subQ1,sQuery(id+"F0.wireOp",EDGE,"E17.rect.left"),sQuery(id+"F0.wireOp",EDGE,"E17.rect.right"),sQuery(id+"F0.wireOp",EDGE,"E18.rect.bottom"),sQuery(id+"F0.wireOp",EDGE,"E18.rect.top"),sQuery(id+"F0.wireOp",EDGE,"E18.rect.left"),sQuery(id+"F0.wireOp",EDGE,"E18.rect.right"),subQ0,sQuery(id+"F0.wireOp",EDGE,"E19.rect.right"),sQuery(id+"F0.wireOp",EDGE,"E20.rect.bottom"),sQuery(id+"F0.wireOp",EDGE,"E20.rect.top"),sQuery(id+"F0.wireOp",EDGE,"E23.top"),sQuery(id+"F0.wireOp",EDGE,"E23.left"),sQuery(id+"F0.wireOp",EDGE,"E23.right"),sQuery(id+"F0.wireOp",EDGE,"E24.top"),sQuery(id+"F0.wireOp",EDGE,"E24.left"),sQuery(id+"F0.wireOp",EDGE,"E24.right"),sQuery(id+"F0.wireOp",EDGE,"E25.top"),sQuery(id+"F0.wireOp",EDGE,"E25.left"),sQuery(id+"F0.wireOp",EDGE,"E25.right"),sQuery(id+"F0.wireOp",EDGE,"E26.top"),sQuery(id+"F0.wireOp",EDGE,"E26.left"),sQuery(id+"F0.wireOp",EDGE,"E26.right")])],"isStart":true})]});}
            var Q30;
            {var subQ0=sQuery(id+"F0.wireOp",EDGE,"E17.rect.top");Q30=makeQuery(id+"F1.opExtrude","CAP_EDGE",EDGE,{"disambiguationData":[OSD([subQ0]),TDD([makeQuery(id+"F0.imprint","IMPRINT",EDGE,{"disambiguationData":[TD([[makeQuery(id+"F0.imprint","INTERSECT",VERTEX,{"derivedFrom":[subQ0,sQuery(id+"F0.wireOp",EDGE,"E19.rect.left")]}),1.0]])],"derivedFrom":subQ0})])],"isStart":true});}
            var Q31;
            {var subQ0=sQuery(id+"F0.wireOp",EDGE,"E17.rect.top");Q31=makeQuery(id+"F1.opExtrude","CAP_EDGE",EDGE,{"disambiguationData":[OSD([subQ0]),TDD([makeQuery(id+"F0.imprint","IMPRINT",EDGE,{"disambiguationData":[TD([[makeQuery(id+"F0.imprint","INTERSECT",VERTEX,{"derivedFrom":[subQ0,sQuery(id+"F0.wireOp",EDGE,"E19.rect.right")]}),-1.0]])],"derivedFrom":subQ0})])],"isStart":true});}
            var Q32;
            {var subQ0=sQuery(id+"F0.wireOp",EDGE,"E19.rect.right");var subQ1=sQuery(id+"F0.wireOp",EDGE,"E17.rect.top");Q32=makeQuery(id+"F3.opFillet","BLEND_EDGE",EDGE,{"blendedFrom":[makeQuery(id+"F1.opExtrude","SWEPT_EDGE",EDGE,{"disambiguationData":[OSD([subQ1,subQ0])]}),makeQuery(id+"F1.opExtrude","CAP_FACE",FACE,{"disambiguationData":[OSD([sQuery(id+"F0.wireOp",EDGE,"E0"),sQuery(id+"F0.wireOp",EDGE,"E1"),sQuery(id+"F0.wireOp",EDGE,"E2"),sQuery(id+"F0.wireOp",EDGE,"E3"),sQuery(id+"F0.wireOp",EDGE,"E4"),sQuery(id+"F0.wireOp",EDGE,"E5"),sQuery(id+"F0.wireOp",EDGE,"E6"),sQuery(id+"F0.wireOp",EDGE,"E7"),sQuery(id+"F0.wireOp",EDGE,"E8"),sQuery(id+"F0.wireOp",EDGE,"E9"),sQuery(id+"F0.wireOp",EDGE,"E10"),sQuery(id+"F0.wireOp",EDGE,"E11"),sQuery(id+"F0.wireOp",EDGE,"E12"),sQuery(id+"F0.wireOp",EDGE,"E13"),sQuery(id+"F0.wireOp",EDGE,"E14"),sQuery(id+"F0.wireOp",EDGE,"E15"),sQuery(id+"F0.wireOp",EDGE,"E17.rect.bottom"),subQ1,sQuery(id+"F0.wireOp",EDGE,"E17.rect.left"),sQuery(id+"F0.wireOp",EDGE,"E17.rect.right"),sQuery(id+"F0.wireOp",EDGE,"E18.rect.bottom"),sQuery(id+"F0.wireOp",EDGE,"E18.rect.top"),sQuery(id+"F0.wireOp",EDGE,"E18.rect.left"),sQuery(id+"F0.wireOp",EDGE,"E18.rect.right"),sQuery(id+"F0.wireOp",EDGE,"E19.rect.left"),subQ0,sQuery(id+"F0.wireOp",EDGE,"E20.rect.bottom"),sQuery(id+"F0.wireOp",EDGE,"E20.rect.top"),sQuery(id+"F0.wireOp",EDGE,"E23.top"),sQuery(id+"F0.wireOp",EDGE,"E23.left"),sQuery(id+"F0.wireOp",EDGE,"E23.right"),sQuery(id+"F0.wireOp",EDGE,"E24.top"),sQuery(id+"F0.wireOp",EDGE,"E24.left"),sQuery(id+"F0.wireOp",EDGE,"E24.right"),sQuery(id+"F0.wireOp",EDGE,"E25.top"),sQuery(id+"F0.wireOp",EDGE,"E25.left"),sQuery(id+"F0.wireOp",EDGE,"E25.right"),sQuery(id+"F0.wireOp",EDGE,"E26.top"),sQuery(id+"F0.wireOp",EDGE,"E26.left"),sQuery(id+"F0.wireOp",EDGE,"E26.right")])],"isStart":true})],"blendedInto":[makeQuery(id+"F1.opExtrude","CAP_FACE",FACE,{"disambiguationData":[OSD([sQuery(id+"F0.wireOp",EDGE,"E0"),sQuery(id+"F0.wireOp",EDGE,"E1"),sQuery(id+"F0.wireOp",EDGE,"E2"),sQuery(id+"F0.wireOp",EDGE,"E3"),sQuery(id+"F0.wireOp",EDGE,"E4"),sQuery(id+"F0.wireOp",EDGE,"E5"),sQuery(id+"F0.wireOp",EDGE,"E6"),sQuery(id+"F0.wireOp",EDGE,"E7"),sQuery(id+"F0.wireOp",EDGE,"E8"),sQuery(id+"F0.wireOp",EDGE,"E9"),sQuery(id+"F0.wireOp",EDGE,"E10"),sQuery(id+"F0.wireOp",EDGE,"E11"),sQuery(id+"F0.wireOp",EDGE,"E12"),sQuery(id+"F0.wireOp",EDGE,"E13"),sQuery(id+"F0.wireOp",EDGE,"E14"),sQuery(id+"F0.wireOp",EDGE,"E15"),sQuery(id+"F0.wireOp",EDGE,"E17.rect.bottom"),subQ1,sQuery(id+"F0.wireOp",EDGE,"E17.rect.left"),sQuery(id+"F0.wireOp",EDGE,"E17.rect.right"),sQuery(id+"F0.wireOp",EDGE,"E18.rect.bottom"),sQuery(id+"F0.wireOp",EDGE,"E18.rect.top"),sQuery(id+"F0.wireOp",EDGE,"E18.rect.left"),sQuery(id+"F0.wireOp",EDGE,"E18.rect.right"),sQuery(id+"F0.wireOp",EDGE,"E19.rect.left"),subQ0,sQuery(id+"F0.wireOp",EDGE,"E20.rect.bottom"),sQuery(id+"F0.wireOp",EDGE,"E20.rect.top"),sQuery(id+"F0.wireOp",EDGE,"E23.top"),sQuery(id+"F0.wireOp",EDGE,"E23.left"),sQuery(id+"F0.wireOp",EDGE,"E23.right"),sQuery(id+"F0.wireOp",EDGE,"E24.top"),sQuery(id+"F0.wireOp",EDGE,"E24.left"),sQuery(id+"F0.wireOp",EDGE,"E24.right"),sQuery(id+"F0.wireOp",EDGE,"E25.top"),sQuery(id+"F0.wireOp",EDGE,"E25.left"),sQuery(id+"F0.wireOp",EDGE,"E25.right"),sQuery(id+"F0.wireOp",EDGE,"E26.top"),sQuery(id+"F0.wireOp",EDGE,"E26.left"),sQuery(id+"F0.wireOp",EDGE,"E26.right")])],"isStart":true})]});}
            var Q33;
            {var subQ0=sQuery(id+"F0.wireOp",EDGE,"E19.rect.right");Q33=makeQuery(id+"F1.opExtrude","CAP_EDGE",EDGE,{"disambiguationData":[OSD([subQ0]),TDD([makeQuery(id+"F0.imprint","IMPRINT",EDGE,{"disambiguationData":[TD([[makeQuery(id+"F0.imprint","INTERSECT",VERTEX,{"derivedFrom":[sQuery(id+"F0.wireOp",EDGE,"E14"),subQ0]}),1.0]])],"derivedFrom":subQ0})])],"isStart":true});}
            var Q34;
            {var subQ0=sQuery(id+"F0.wireOp",EDGE,"E19.rect.right");var subQ1=sQuery(id+"F0.wireOp",EDGE,"E14");Q34=makeQuery(id+"F3.opFillet","BLEND_EDGE",EDGE,{"blendedFrom":[makeQuery(id+"F1.opExtrude","SWEPT_EDGE",EDGE,{"disambiguationData":[OSD([subQ1,subQ0])]}),makeQuery(id+"F1.opExtrude","CAP_FACE",FACE,{"disambiguationData":[OSD([sQuery(id+"F0.wireOp",EDGE,"E0"),sQuery(id+"F0.wireOp",EDGE,"E1"),sQuery(id+"F0.wireOp",EDGE,"E2"),sQuery(id+"F0.wireOp",EDGE,"E3"),sQuery(id+"F0.wireOp",EDGE,"E4"),sQuery(id+"F0.wireOp",EDGE,"E5"),sQuery(id+"F0.wireOp",EDGE,"E6"),sQuery(id+"F0.wireOp",EDGE,"E7"),sQuery(id+"F0.wireOp",EDGE,"E8"),sQuery(id+"F0.wireOp",EDGE,"E9"),sQuery(id+"F0.wireOp",EDGE,"E10"),sQuery(id+"F0.wireOp",EDGE,"E11"),sQuery(id+"F0.wireOp",EDGE,"E12"),sQuery(id+"F0.wireOp",EDGE,"E13"),subQ1,sQuery(id+"F0.wireOp",EDGE,"E15"),sQuery(id+"F0.wireOp",EDGE,"E17.rect.bottom"),sQuery(id+"F0.wireOp",EDGE,"E17.rect.top"),sQuery(id+"F0.wireOp",EDGE,"E17.rect.left"),sQuery(id+"F0.wireOp",EDGE,"E17.rect.right"),sQuery(id+"F0.wireOp",EDGE,"E18.rect.bottom"),sQuery(id+"F0.wireOp",EDGE,"E18.rect.top"),sQuery(id+"F0.wireOp",EDGE,"E18.rect.left"),sQuery(id+"F0.wireOp",EDGE,"E18.rect.right"),sQuery(id+"F0.wireOp",EDGE,"E19.rect.left"),subQ0,sQuery(id+"F0.wireOp",EDGE,"E20.rect.bottom"),sQuery(id+"F0.wireOp",EDGE,"E20.rect.top"),sQuery(id+"F0.wireOp",EDGE,"E23.top"),sQuery(id+"F0.wireOp",EDGE,"E23.left"),sQuery(id+"F0.wireOp",EDGE,"E23.right"),sQuery(id+"F0.wireOp",EDGE,"E24.top"),sQuery(id+"F0.wireOp",EDGE,"E24.left"),sQuery(id+"F0.wireOp",EDGE,"E24.right"),sQuery(id+"F0.wireOp",EDGE,"E25.top"),sQuery(id+"F0.wireOp",EDGE,"E25.left"),sQuery(id+"F0.wireOp",EDGE,"E25.right"),sQuery(id+"F0.wireOp",EDGE,"E26.top"),sQuery(id+"F0.wireOp",EDGE,"E26.left"),sQuery(id+"F0.wireOp",EDGE,"E26.right")])],"isStart":true})],"blendedInto":[makeQuery(id+"F1.opExtrude","CAP_FACE",FACE,{"disambiguationData":[OSD([sQuery(id+"F0.wireOp",EDGE,"E0"),sQuery(id+"F0.wireOp",EDGE,"E1"),sQuery(id+"F0.wireOp",EDGE,"E2"),sQuery(id+"F0.wireOp",EDGE,"E3"),sQuery(id+"F0.wireOp",EDGE,"E4"),sQuery(id+"F0.wireOp",EDGE,"E5"),sQuery(id+"F0.wireOp",EDGE,"E6"),sQuery(id+"F0.wireOp",EDGE,"E7"),sQuery(id+"F0.wireOp",EDGE,"E8"),sQuery(id+"F0.wireOp",EDGE,"E9"),sQuery(id+"F0.wireOp",EDGE,"E10"),sQuery(id+"F0.wireOp",EDGE,"E11"),sQuery(id+"F0.wireOp",EDGE,"E12"),sQuery(id+"F0.wireOp",EDGE,"E13"),subQ1,sQuery(id+"F0.wireOp",EDGE,"E15"),sQuery(id+"F0.wireOp",EDGE,"E17.rect.bottom"),sQuery(id+"F0.wireOp",EDGE,"E17.rect.top"),sQuery(id+"F0.wireOp",EDGE,"E17.rect.left"),sQuery(id+"F0.wireOp",EDGE,"E17.rect.right"),sQuery(id+"F0.wireOp",EDGE,"E18.rect.bottom"),sQuery(id+"F0.wireOp",EDGE,"E18.rect.top"),sQuery(id+"F0.wireOp",EDGE,"E18.rect.left"),sQuery(id+"F0.wireOp",EDGE,"E18.rect.right"),sQuery(id+"F0.wireOp",EDGE,"E19.rect.left"),subQ0,sQuery(id+"F0.wireOp",EDGE,"E20.rect.bottom"),sQuery(id+"F0.wireOp",EDGE,"E20.rect.top"),sQuery(id+"F0.wireOp",EDGE,"E23.top"),sQuery(id+"F0.wireOp",EDGE,"E23.left"),sQuery(id+"F0.wireOp",EDGE,"E23.right"),sQuery(id+"F0.wireOp",EDGE,"E24.top"),sQuery(id+"F0.wireOp",EDGE,"E24.left"),sQuery(id+"F0.wireOp",EDGE,"E24.right"),sQuery(id+"F0.wireOp",EDGE,"E25.top"),sQuery(id+"F0.wireOp",EDGE,"E25.left"),sQuery(id+"F0.wireOp",EDGE,"E25.right"),sQuery(id+"F0.wireOp",EDGE,"E26.top"),sQuery(id+"F0.wireOp",EDGE,"E26.left"),sQuery(id+"F0.wireOp",EDGE,"E26.right")])],"isStart":true})]});}
            var Q35;
            Q35=makeQuery(id+"F1.opExtrude","CAP_EDGE",EDGE,{"disambiguationData":[OSD([sQuery(id+"F0.wireOp",EDGE,"E18.rect.top")])],"isStart":true});
            var Q36;
            {var subQ0=sQuery(id+"F0.wireOp",EDGE,"E18.rect.left");var subQ1=sQuery(id+"F0.wireOp",EDGE,"E18.rect.top");Q36=makeQuery(id+"F3.opFillet","BLEND_EDGE",EDGE,{"blendedFrom":[makeQuery(id+"F1.opExtrude","SWEPT_EDGE",EDGE,{"disambiguationData":[OSD([subQ1,subQ0])]}),makeQuery(id+"F1.opExtrude","CAP_FACE",FACE,{"disambiguationData":[OSD([sQuery(id+"F0.wireOp",EDGE,"E0"),sQuery(id+"F0.wireOp",EDGE,"E1"),sQuery(id+"F0.wireOp",EDGE,"E2"),sQuery(id+"F0.wireOp",EDGE,"E3"),sQuery(id+"F0.wireOp",EDGE,"E4"),sQuery(id+"F0.wireOp",EDGE,"E5"),sQuery(id+"F0.wireOp",EDGE,"E6"),sQuery(id+"F0.wireOp",EDGE,"E7"),sQuery(id+"F0.wireOp",EDGE,"E8"),sQuery(id+"F0.wireOp",EDGE,"E9"),sQuery(id+"F0.wireOp",EDGE,"E10"),sQuery(id+"F0.wireOp",EDGE,"E11"),sQuery(id+"F0.wireOp",EDGE,"E12"),sQuery(id+"F0.wireOp",EDGE,"E13"),sQuery(id+"F0.wireOp",EDGE,"E14"),sQuery(id+"F0.wireOp",EDGE,"E15"),sQuery(id+"F0.wireOp",EDGE,"E17.rect.bottom"),sQuery(id+"F0.wireOp",EDGE,"E17.rect.top"),sQuery(id+"F0.wireOp",EDGE,"E17.rect.left"),sQuery(id+"F0.wireOp",EDGE,"E17.rect.right"),sQuery(id+"F0.wireOp",EDGE,"E18.rect.bottom"),subQ1,subQ0,sQuery(id+"F0.wireOp",EDGE,"E18.rect.right"),sQuery(id+"F0.wireOp",EDGE,"E19.rect.left"),sQuery(id+"F0.wireOp",EDGE,"E19.rect.right"),sQuery(id+"F0.wireOp",EDGE,"E20.rect.bottom"),sQuery(id+"F0.wireOp",EDGE,"E20.rect.top"),sQuery(id+"F0.wireOp",EDGE,"E23.top"),sQuery(id+"F0.wireOp",EDGE,"E23.left"),sQuery(id+"F0.wireOp",EDGE,"E23.right"),sQuery(id+"F0.wireOp",EDGE,"E24.top"),sQuery(id+"F0.wireOp",EDGE,"E24.left"),sQuery(id+"F0.wireOp",EDGE,"E24.right"),sQuery(id+"F0.wireOp",EDGE,"E25.top"),sQuery(id+"F0.wireOp",EDGE,"E25.left"),sQuery(id+"F0.wireOp",EDGE,"E25.right"),sQuery(id+"F0.wireOp",EDGE,"E26.top"),sQuery(id+"F0.wireOp",EDGE,"E26.left"),sQuery(id+"F0.wireOp",EDGE,"E26.right")])],"isStart":true})],"blendedInto":[makeQuery(id+"F1.opExtrude","CAP_FACE",FACE,{"disambiguationData":[OSD([sQuery(id+"F0.wireOp",EDGE,"E0"),sQuery(id+"F0.wireOp",EDGE,"E1"),sQuery(id+"F0.wireOp",EDGE,"E2"),sQuery(id+"F0.wireOp",EDGE,"E3"),sQuery(id+"F0.wireOp",EDGE,"E4"),sQuery(id+"F0.wireOp",EDGE,"E5"),sQuery(id+"F0.wireOp",EDGE,"E6"),sQuery(id+"F0.wireOp",EDGE,"E7"),sQuery(id+"F0.wireOp",EDGE,"E8"),sQuery(id+"F0.wireOp",EDGE,"E9"),sQuery(id+"F0.wireOp",EDGE,"E10"),sQuery(id+"F0.wireOp",EDGE,"E11"),sQuery(id+"F0.wireOp",EDGE,"E12"),sQuery(id+"F0.wireOp",EDGE,"E13"),sQuery(id+"F0.wireOp",EDGE,"E14"),sQuery(id+"F0.wireOp",EDGE,"E15"),sQuery(id+"F0.wireOp",EDGE,"E17.rect.bottom"),sQuery(id+"F0.wireOp",EDGE,"E17.rect.top"),sQuery(id+"F0.wireOp",EDGE,"E17.rect.left"),sQuery(id+"F0.wireOp",EDGE,"E17.rect.right"),sQuery(id+"F0.wireOp",EDGE,"E18.rect.bottom"),subQ1,subQ0,sQuery(id+"F0.wireOp",EDGE,"E18.rect.right"),sQuery(id+"F0.wireOp",EDGE,"E19.rect.left"),sQuery(id+"F0.wireOp",EDGE,"E19.rect.right"),sQuery(id+"F0.wireOp",EDGE,"E20.rect.bottom"),sQuery(id+"F0.wireOp",EDGE,"E20.rect.top"),sQuery(id+"F0.wireOp",EDGE,"E23.top"),sQuery(id+"F0.wireOp",EDGE,"E23.left"),sQuery(id+"F0.wireOp",EDGE,"E23.right"),sQuery(id+"F0.wireOp",EDGE,"E24.top"),sQuery(id+"F0.wireOp",EDGE,"E24.left"),sQuery(id+"F0.wireOp",EDGE,"E24.right"),sQuery(id+"F0.wireOp",EDGE,"E25.top"),sQuery(id+"F0.wireOp",EDGE,"E25.left"),sQuery(id+"F0.wireOp",EDGE,"E25.right"),sQuery(id+"F0.wireOp",EDGE,"E26.top"),sQuery(id+"F0.wireOp",EDGE,"E26.left"),sQuery(id+"F0.wireOp",EDGE,"E26.right")])],"isStart":true})]});}
            var Q37;
            Q37=makeQuery(id+"F1.opExtrude","CAP_EDGE",EDGE,{"disambiguationData":[OSD([sQuery(id+"F0.wireOp",EDGE,"E18.rect.left")])],"isStart":true});
            var Q38;
            {var subQ0=sQuery(id+"F0.wireOp",EDGE,"E18.rect.left");var subQ1=sQuery(id+"F0.wireOp",EDGE,"E18.rect.bottom");Q38=makeQuery(id+"F3.opFillet","BLEND_EDGE",EDGE,{"blendedFrom":[makeQuery(id+"F1.opExtrude","SWEPT_EDGE",EDGE,{"disambiguationData":[OSD([subQ1,subQ0])]}),makeQuery(id+"F1.opExtrude","CAP_FACE",FACE,{"disambiguationData":[OSD([sQuery(id+"F0.wireOp",EDGE,"E0"),sQuery(id+"F0.wireOp",EDGE,"E1"),sQuery(id+"F0.wireOp",EDGE,"E2"),sQuery(id+"F0.wireOp",EDGE,"E3"),sQuery(id+"F0.wireOp",EDGE,"E4"),sQuery(id+"F0.wireOp",EDGE,"E5"),sQuery(id+"F0.wireOp",EDGE,"E6"),sQuery(id+"F0.wireOp",EDGE,"E7"),sQuery(id+"F0.wireOp",EDGE,"E8"),sQuery(id+"F0.wireOp",EDGE,"E9"),sQuery(id+"F0.wireOp",EDGE,"E10"),sQuery(id+"F0.wireOp",EDGE,"E11"),sQuery(id+"F0.wireOp",EDGE,"E12"),sQuery(id+"F0.wireOp",EDGE,"E13"),sQuery(id+"F0.wireOp",EDGE,"E14"),sQuery(id+"F0.wireOp",EDGE,"E15"),sQuery(id+"F0.wireOp",EDGE,"E17.rect.bottom"),sQuery(id+"F0.wireOp",EDGE,"E17.rect.top"),sQuery(id+"F0.wireOp",EDGE,"E17.rect.left"),sQuery(id+"F0.wireOp",EDGE,"E17.rect.right"),subQ1,sQuery(id+"F0.wireOp",EDGE,"E18.rect.top"),subQ0,sQuery(id+"F0.wireOp",EDGE,"E18.rect.right"),sQuery(id+"F0.wireOp",EDGE,"E19.rect.left"),sQuery(id+"F0.wireOp",EDGE,"E19.rect.right"),sQuery(id+"F0.wireOp",EDGE,"E20.rect.bottom"),sQuery(id+"F0.wireOp",EDGE,"E20.rect.top"),sQuery(id+"F0.wireOp",EDGE,"E23.top"),sQuery(id+"F0.wireOp",EDGE,"E23.left"),sQuery(id+"F0.wireOp",EDGE,"E23.right"),sQuery(id+"F0.wireOp",EDGE,"E24.top"),sQuery(id+"F0.wireOp",EDGE,"E24.left"),sQuery(id+"F0.wireOp",EDGE,"E24.right"),sQuery(id+"F0.wireOp",EDGE,"E25.top"),sQuery(id+"F0.wireOp",EDGE,"E25.left"),sQuery(id+"F0.wireOp",EDGE,"E25.right"),sQuery(id+"F0.wireOp",EDGE,"E26.top"),sQuery(id+"F0.wireOp",EDGE,"E26.left"),sQuery(id+"F0.wireOp",EDGE,"E26.right")])],"isStart":true})],"blendedInto":[makeQuery(id+"F1.opExtrude","CAP_FACE",FACE,{"disambiguationData":[OSD([sQuery(id+"F0.wireOp",EDGE,"E0"),sQuery(id+"F0.wireOp",EDGE,"E1"),sQuery(id+"F0.wireOp",EDGE,"E2"),sQuery(id+"F0.wireOp",EDGE,"E3"),sQuery(id+"F0.wireOp",EDGE,"E4"),sQuery(id+"F0.wireOp",EDGE,"E5"),sQuery(id+"F0.wireOp",EDGE,"E6"),sQuery(id+"F0.wireOp",EDGE,"E7"),sQuery(id+"F0.wireOp",EDGE,"E8"),sQuery(id+"F0.wireOp",EDGE,"E9"),sQuery(id+"F0.wireOp",EDGE,"E10"),sQuery(id+"F0.wireOp",EDGE,"E11"),sQuery(id+"F0.wireOp",EDGE,"E12"),sQuery(id+"F0.wireOp",EDGE,"E13"),sQuery(id+"F0.wireOp",EDGE,"E14"),sQuery(id+"F0.wireOp",EDGE,"E15"),sQuery(id+"F0.wireOp",EDGE,"E17.rect.bottom"),sQuery(id+"F0.wireOp",EDGE,"E17.rect.top"),sQuery(id+"F0.wireOp",EDGE,"E17.rect.left"),sQuery(id+"F0.wireOp",EDGE,"E17.rect.right"),subQ1,sQuery(id+"F0.wireOp",EDGE,"E18.rect.top"),subQ0,sQuery(id+"F0.wireOp",EDGE,"E18.rect.right"),sQuery(id+"F0.wireOp",EDGE,"E19.rect.left"),sQuery(id+"F0.wireOp",EDGE,"E19.rect.right"),sQuery(id+"F0.wireOp",EDGE,"E20.rect.bottom"),sQuery(id+"F0.wireOp",EDGE,"E20.rect.top"),sQuery(id+"F0.wireOp",EDGE,"E23.top"),sQuery(id+"F0.wireOp",EDGE,"E23.left"),sQuery(id+"F0.wireOp",EDGE,"E23.right"),sQuery(id+"F0.wireOp",EDGE,"E24.top"),sQuery(id+"F0.wireOp",EDGE,"E24.left"),sQuery(id+"F0.wireOp",EDGE,"E24.right"),sQuery(id+"F0.wireOp",EDGE,"E25.top"),sQuery(id+"F0.wireOp",EDGE,"E25.left"),sQuery(id+"F0.wireOp",EDGE,"E25.right"),sQuery(id+"F0.wireOp",EDGE,"E26.top"),sQuery(id+"F0.wireOp",EDGE,"E26.left"),sQuery(id+"F0.wireOp",EDGE,"E26.right")])],"isStart":true})]});}
            var Q39;
            Q39=makeQuery(id+"F1.opExtrude","CAP_EDGE",EDGE,{"disambiguationData":[OSD([sQuery(id+"F0.wireOp",EDGE,"E18.rect.bottom")])],"isStart":true});
            var Q40;
            {var subQ0=sQuery(id+"F0.wireOp",EDGE,"E18.rect.right");var subQ1=sQuery(id+"F0.wireOp",EDGE,"E18.rect.bottom");Q40=makeQuery(id+"F3.opFillet","BLEND_EDGE",EDGE,{"blendedFrom":[makeQuery(id+"F1.opExtrude","SWEPT_EDGE",EDGE,{"disambiguationData":[OSD([subQ1,subQ0])]}),makeQuery(id+"F1.opExtrude","CAP_FACE",FACE,{"disambiguationData":[OSD([sQuery(id+"F0.wireOp",EDGE,"E0"),sQuery(id+"F0.wireOp",EDGE,"E1"),sQuery(id+"F0.wireOp",EDGE,"E2"),sQuery(id+"F0.wireOp",EDGE,"E3"),sQuery(id+"F0.wireOp",EDGE,"E4"),sQuery(id+"F0.wireOp",EDGE,"E5"),sQuery(id+"F0.wireOp",EDGE,"E6"),sQuery(id+"F0.wireOp",EDGE,"E7"),sQuery(id+"F0.wireOp",EDGE,"E8"),sQuery(id+"F0.wireOp",EDGE,"E9"),sQuery(id+"F0.wireOp",EDGE,"E10"),sQuery(id+"F0.wireOp",EDGE,"E11"),sQuery(id+"F0.wireOp",EDGE,"E12"),sQuery(id+"F0.wireOp",EDGE,"E13"),sQuery(id+"F0.wireOp",EDGE,"E14"),sQuery(id+"F0.wireOp",EDGE,"E15"),sQuery(id+"F0.wireOp",EDGE,"E17.rect.bottom"),sQuery(id+"F0.wireOp",EDGE,"E17.rect.top"),sQuery(id+"F0.wireOp",EDGE,"E17.rect.left"),sQuery(id+"F0.wireOp",EDGE,"E17.rect.right"),subQ1,sQuery(id+"F0.wireOp",EDGE,"E18.rect.top"),sQuery(id+"F0.wireOp",EDGE,"E18.rect.left"),subQ0,sQuery(id+"F0.wireOp",EDGE,"E19.rect.left"),sQuery(id+"F0.wireOp",EDGE,"E19.rect.right"),sQuery(id+"F0.wireOp",EDGE,"E20.rect.bottom"),sQuery(id+"F0.wireOp",EDGE,"E20.rect.top"),sQuery(id+"F0.wireOp",EDGE,"E23.top"),sQuery(id+"F0.wireOp",EDGE,"E23.left"),sQuery(id+"F0.wireOp",EDGE,"E23.right"),sQuery(id+"F0.wireOp",EDGE,"E24.top"),sQuery(id+"F0.wireOp",EDGE,"E24.left"),sQuery(id+"F0.wireOp",EDGE,"E24.right"),sQuery(id+"F0.wireOp",EDGE,"E25.top"),sQuery(id+"F0.wireOp",EDGE,"E25.left"),sQuery(id+"F0.wireOp",EDGE,"E25.right"),sQuery(id+"F0.wireOp",EDGE,"E26.top"),sQuery(id+"F0.wireOp",EDGE,"E26.left"),sQuery(id+"F0.wireOp",EDGE,"E26.right")])],"isStart":true})],"blendedInto":[makeQuery(id+"F1.opExtrude","CAP_FACE",FACE,{"disambiguationData":[OSD([sQuery(id+"F0.wireOp",EDGE,"E0"),sQuery(id+"F0.wireOp",EDGE,"E1"),sQuery(id+"F0.wireOp",EDGE,"E2"),sQuery(id+"F0.wireOp",EDGE,"E3"),sQuery(id+"F0.wireOp",EDGE,"E4"),sQuery(id+"F0.wireOp",EDGE,"E5"),sQuery(id+"F0.wireOp",EDGE,"E6"),sQuery(id+"F0.wireOp",EDGE,"E7"),sQuery(id+"F0.wireOp",EDGE,"E8"),sQuery(id+"F0.wireOp",EDGE,"E9"),sQuery(id+"F0.wireOp",EDGE,"E10"),sQuery(id+"F0.wireOp",EDGE,"E11"),sQuery(id+"F0.wireOp",EDGE,"E12"),sQuery(id+"F0.wireOp",EDGE,"E13"),sQuery(id+"F0.wireOp",EDGE,"E14"),sQuery(id+"F0.wireOp",EDGE,"E15"),sQuery(id+"F0.wireOp",EDGE,"E17.rect.bottom"),sQuery(id+"F0.wireOp",EDGE,"E17.rect.top"),sQuery(id+"F0.wireOp",EDGE,"E17.rect.left"),sQuery(id+"F0.wireOp",EDGE,"E17.rect.right"),subQ1,sQuery(id+"F0.wireOp",EDGE,"E18.rect.top"),sQuery(id+"F0.wireOp",EDGE,"E18.rect.left"),subQ0,sQuery(id+"F0.wireOp",EDGE,"E19.rect.left"),sQuery(id+"F0.wireOp",EDGE,"E19.rect.right"),sQuery(id+"F0.wireOp",EDGE,"E20.rect.bottom"),sQuery(id+"F0.wireOp",EDGE,"E20.rect.top"),sQuery(id+"F0.wireOp",EDGE,"E23.top"),sQuery(id+"F0.wireOp",EDGE,"E23.left"),sQuery(id+"F0.wireOp",EDGE,"E23.right"),sQuery(id+"F0.wireOp",EDGE,"E24.top"),sQuery(id+"F0.wireOp",EDGE,"E24.left"),sQuery(id+"F0.wireOp",EDGE,"E24.right"),sQuery(id+"F0.wireOp",EDGE,"E25.top"),sQuery(id+"F0.wireOp",EDGE,"E25.left"),sQuery(id+"F0.wireOp",EDGE,"E25.right"),sQuery(id+"F0.wireOp",EDGE,"E26.top"),sQuery(id+"F0.wireOp",EDGE,"E26.left"),sQuery(id+"F0.wireOp",EDGE,"E26.right")])],"isStart":true})]});}
            var Q41;
            Q41=makeQuery(id+"F1.opExtrude","CAP_EDGE",EDGE,{"disambiguationData":[OSD([sQuery(id+"F0.wireOp",EDGE,"E18.rect.right")])],"isStart":true});
            var Q42;
            {var subQ0=sQuery(id+"F0.wireOp",EDGE,"E18.rect.right");var subQ1=sQuery(id+"F0.wireOp",EDGE,"E18.rect.top");Q42=makeQuery(id+"F3.opFillet","BLEND_EDGE",EDGE,{"blendedFrom":[makeQuery(id+"F1.opExtrude","SWEPT_EDGE",EDGE,{"disambiguationData":[OSD([subQ1,subQ0])]}),makeQuery(id+"F1.opExtrude","CAP_FACE",FACE,{"disambiguationData":[OSD([sQuery(id+"F0.wireOp",EDGE,"E0"),sQuery(id+"F0.wireOp",EDGE,"E1"),sQuery(id+"F0.wireOp",EDGE,"E2"),sQuery(id+"F0.wireOp",EDGE,"E3"),sQuery(id+"F0.wireOp",EDGE,"E4"),sQuery(id+"F0.wireOp",EDGE,"E5"),sQuery(id+"F0.wireOp",EDGE,"E6"),sQuery(id+"F0.wireOp",EDGE,"E7"),sQuery(id+"F0.wireOp",EDGE,"E8"),sQuery(id+"F0.wireOp",EDGE,"E9"),sQuery(id+"F0.wireOp",EDGE,"E10"),sQuery(id+"F0.wireOp",EDGE,"E11"),sQuery(id+"F0.wireOp",EDGE,"E12"),sQuery(id+"F0.wireOp",EDGE,"E13"),sQuery(id+"F0.wireOp",EDGE,"E14"),sQuery(id+"F0.wireOp",EDGE,"E15"),sQuery(id+"F0.wireOp",EDGE,"E17.rect.bottom"),sQuery(id+"F0.wireOp",EDGE,"E17.rect.top"),sQuery(id+"F0.wireOp",EDGE,"E17.rect.left"),sQuery(id+"F0.wireOp",EDGE,"E17.rect.right"),sQuery(id+"F0.wireOp",EDGE,"E18.rect.bottom"),subQ1,sQuery(id+"F0.wireOp",EDGE,"E18.rect.left"),subQ0,sQuery(id+"F0.wireOp",EDGE,"E19.rect.left"),sQuery(id+"F0.wireOp",EDGE,"E19.rect.right"),sQuery(id+"F0.wireOp",EDGE,"E20.rect.bottom"),sQuery(id+"F0.wireOp",EDGE,"E20.rect.top"),sQuery(id+"F0.wireOp",EDGE,"E23.top"),sQuery(id+"F0.wireOp",EDGE,"E23.left"),sQuery(id+"F0.wireOp",EDGE,"E23.right"),sQuery(id+"F0.wireOp",EDGE,"E24.top"),sQuery(id+"F0.wireOp",EDGE,"E24.left"),sQuery(id+"F0.wireOp",EDGE,"E24.right"),sQuery(id+"F0.wireOp",EDGE,"E25.top"),sQuery(id+"F0.wireOp",EDGE,"E25.left"),sQuery(id+"F0.wireOp",EDGE,"E25.right"),sQuery(id+"F0.wireOp",EDGE,"E26.top"),sQuery(id+"F0.wireOp",EDGE,"E26.left"),sQuery(id+"F0.wireOp",EDGE,"E26.right")])],"isStart":true})],"blendedInto":[makeQuery(id+"F1.opExtrude","CAP_FACE",FACE,{"disambiguationData":[OSD([sQuery(id+"F0.wireOp",EDGE,"E0"),sQuery(id+"F0.wireOp",EDGE,"E1"),sQuery(id+"F0.wireOp",EDGE,"E2"),sQuery(id+"F0.wireOp",EDGE,"E3"),sQuery(id+"F0.wireOp",EDGE,"E4"),sQuery(id+"F0.wireOp",EDGE,"E5"),sQuery(id+"F0.wireOp",EDGE,"E6"),sQuery(id+"F0.wireOp",EDGE,"E7"),sQuery(id+"F0.wireOp",EDGE,"E8"),sQuery(id+"F0.wireOp",EDGE,"E9"),sQuery(id+"F0.wireOp",EDGE,"E10"),sQuery(id+"F0.wireOp",EDGE,"E11"),sQuery(id+"F0.wireOp",EDGE,"E12"),sQuery(id+"F0.wireOp",EDGE,"E13"),sQuery(id+"F0.wireOp",EDGE,"E14"),sQuery(id+"F0.wireOp",EDGE,"E15"),sQuery(id+"F0.wireOp",EDGE,"E17.rect.bottom"),sQuery(id+"F0.wireOp",EDGE,"E17.rect.top"),sQuery(id+"F0.wireOp",EDGE,"E17.rect.left"),sQuery(id+"F0.wireOp",EDGE,"E17.rect.right"),sQuery(id+"F0.wireOp",EDGE,"E18.rect.bottom"),subQ1,sQuery(id+"F0.wireOp",EDGE,"E18.rect.left"),subQ0,sQuery(id+"F0.wireOp",EDGE,"E19.rect.left"),sQuery(id+"F0.wireOp",EDGE,"E19.rect.right"),sQuery(id+"F0.wireOp",EDGE,"E20.rect.bottom"),sQuery(id+"F0.wireOp",EDGE,"E20.rect.top"),sQuery(id+"F0.wireOp",EDGE,"E23.top"),sQuery(id+"F0.wireOp",EDGE,"E23.left"),sQuery(id+"F0.wireOp",EDGE,"E23.right"),sQuery(id+"F0.wireOp",EDGE,"E24.top"),sQuery(id+"F0.wireOp",EDGE,"E24.left"),sQuery(id+"F0.wireOp",EDGE,"E24.right"),sQuery(id+"F0.wireOp",EDGE,"E25.top"),sQuery(id+"F0.wireOp",EDGE,"E25.left"),sQuery(id+"F0.wireOp",EDGE,"E25.right"),sQuery(id+"F0.wireOp",EDGE,"E26.top"),sQuery(id+"F0.wireOp",EDGE,"E26.left"),sQuery(id+"F0.wireOp",EDGE,"E26.right")])],"isStart":true})]});}
            var Q43;
            Q43=makeQuery(id+"F1.opExtrude","CAP_EDGE",EDGE,{"disambiguationData":[OSD([sQuery(id+"F0.wireOp",EDGE,"E17.rect.right"),sQuery(id+"F0.wireOp",EDGE,"E23.left")])],"isStart":true});
            var Q44;
            Q44=makeQuery(id+"F1.opExtrude","CAP_EDGE",EDGE,{"disambiguationData":[OSD([sQuery(id+"F0.wireOp",EDGE,"E17.rect.right"),sQuery(id+"F0.wireOp",EDGE,"E24.left")])],"isStart":true});
            var Q45;
            Q45=makeQuery(id+"F1.opExtrude","CAP_EDGE",EDGE,{"disambiguationData":[OSD([sQuery(id+"F0.wireOp",EDGE,"E24.right")])],"isStart":true});
            var Q46;
            Q46=makeQuery(id+"F1.opExtrude","CAP_EDGE",EDGE,{"disambiguationData":[OSD([sQuery(id+"F0.wireOp",EDGE,"E23.right")])],"isStart":true});
            var Q47;
            Q47=makeQuery(id+"F1.opExtrude","CAP_EDGE",EDGE,{"disambiguationData":[OSD([sQuery(id+"F0.wireOp",EDGE,"E26.right")])],"isStart":true});
            var Q48;
            Q48=makeQuery(id+"F1.opExtrude","CAP_EDGE",EDGE,{"disambiguationData":[OSD([sQuery(id+"F0.wireOp",EDGE,"E25.right")])],"isStart":true});
            var Q49;
            Q49=makeQuery(id+"F1.opExtrude","CAP_EDGE",EDGE,{"disambiguationData":[OSD([sQuery(id+"F0.wireOp",EDGE,"E17.rect.left"),sQuery(id+"F0.wireOp",EDGE,"E26.left")])],"isStart":true});
            var Q50;
            Q50=makeQuery(id+"F1.opExtrude","CAP_EDGE",EDGE,{"disambiguationData":[OSD([sQuery(id+"F0.wireOp",EDGE,"E17.rect.left"),sQuery(id+"F0.wireOp",EDGE,"E25.left")])],"isStart":true});
            var Q51;
            {var subQ0=sQuery(id+"F0.wireOp",EDGE,"E14");var subQ1=makeQuery(id+"F0.imprint","INTERSECT",VERTEX,{"disambiguationData":[OD(0.0)],"derivedFrom":[sQuery(id+"F0.wireOp",EDGE,"E5"),subQ0]});Q51=makeQuery(id+"F1.opExtrude","CAP_EDGE",EDGE,{"disambiguationData":[OSD([subQ0]),TDD([makeQuery(id+"F0.imprint","IMPRINT",EDGE,{"disambiguationData":[TD([[subQ1,1.0]])],"derivedFrom":subQ0}),makeQuery(id+"F0.imprint","IMPRINT",EDGE,{"disambiguationData":[TD([[makeQuery(id+"F0.imprint","INTERSECT",VERTEX,{"disambiguationData":[OD(1.0)],"derivedFrom":[sQuery(id+"F0.wireOp",EDGE,"E3"),subQ0]}),1.0]])],"derivedFrom":subQ0})])],"isStart":true});}
            var Q52;
            {var subQ0=sQuery(id+"F0.wireOp",EDGE,"E14");var subQ1=makeQuery(id+"F0.imprint","INTERSECT",VERTEX,{"disambiguationData":[OD(0.0)],"derivedFrom":[sQuery(id+"F0.wireOp",EDGE,"E6"),subQ0]});Q52=makeQuery(id+"F1.opExtrude","CAP_EDGE",EDGE,{"disambiguationData":[OSD([subQ0]),TDD([makeQuery(id+"F0.imprint","IMPRINT",EDGE,{"disambiguationData":[TD([[makeQuery(id+"F0.imprint","INTERSECT",VERTEX,{"disambiguationData":[OD(0.0)],"derivedFrom":[sQuery(id+"F0.wireOp",EDGE,"E2"),subQ0]}),-1.0]])],"derivedFrom":subQ0}),makeQuery(id+"F0.imprint","IMPRINT",EDGE,{"disambiguationData":[TD([[subQ1,-1.0]])],"derivedFrom":subQ0})])],"isStart":false});}
            var Q53;
            {var subQ0=sQuery(id+"F0.wireOp",EDGE,"E19.rect.left");var subQ1=sQuery(id+"F0.wireOp",EDGE,"E14");Q53=makeQuery(id+"F3.opFillet","BLEND_EDGE",EDGE,{"blendedFrom":[makeQuery(id+"F1.opExtrude","SWEPT_EDGE",EDGE,{"disambiguationData":[OSD([subQ1,subQ0])]}),makeQuery(id+"F1.opExtrude","CAP_FACE",FACE,{"disambiguationData":[OSD([sQuery(id+"F0.wireOp",EDGE,"E0"),sQuery(id+"F0.wireOp",EDGE,"E1"),sQuery(id+"F0.wireOp",EDGE,"E2"),sQuery(id+"F0.wireOp",EDGE,"E3"),sQuery(id+"F0.wireOp",EDGE,"E4"),sQuery(id+"F0.wireOp",EDGE,"E5"),sQuery(id+"F0.wireOp",EDGE,"E6"),sQuery(id+"F0.wireOp",EDGE,"E7"),sQuery(id+"F0.wireOp",EDGE,"E8"),sQuery(id+"F0.wireOp",EDGE,"E9"),sQuery(id+"F0.wireOp",EDGE,"E10"),sQuery(id+"F0.wireOp",EDGE,"E11"),sQuery(id+"F0.wireOp",EDGE,"E12"),sQuery(id+"F0.wireOp",EDGE,"E13"),subQ1,sQuery(id+"F0.wireOp",EDGE,"E15"),sQuery(id+"F0.wireOp",EDGE,"E17.rect.bottom"),sQuery(id+"F0.wireOp",EDGE,"E17.rect.top"),sQuery(id+"F0.wireOp",EDGE,"E17.rect.left"),sQuery(id+"F0.wireOp",EDGE,"E17.rect.right"),sQuery(id+"F0.wireOp",EDGE,"E18.rect.bottom"),sQuery(id+"F0.wireOp",EDGE,"E18.rect.top"),sQuery(id+"F0.wireOp",EDGE,"E18.rect.left"),sQuery(id+"F0.wireOp",EDGE,"E18.rect.right"),subQ0,sQuery(id+"F0.wireOp",EDGE,"E19.rect.right"),sQuery(id+"F0.wireOp",EDGE,"E20.rect.bottom"),sQuery(id+"F0.wireOp",EDGE,"E20.rect.top"),sQuery(id+"F0.wireOp",EDGE,"E23.top"),sQuery(id+"F0.wireOp",EDGE,"E23.left"),sQuery(id+"F0.wireOp",EDGE,"E23.right"),sQuery(id+"F0.wireOp",EDGE,"E24.top"),sQuery(id+"F0.wireOp",EDGE,"E24.left"),sQuery(id+"F0.wireOp",EDGE,"E24.right"),sQuery(id+"F0.wireOp",EDGE,"E25.top"),sQuery(id+"F0.wireOp",EDGE,"E25.left"),sQuery(id+"F0.wireOp",EDGE,"E25.right"),sQuery(id+"F0.wireOp",EDGE,"E26.top"),sQuery(id+"F0.wireOp",EDGE,"E26.left"),sQuery(id+"F0.wireOp",EDGE,"E26.right")])],"isStart":false})],"blendedInto":[makeQuery(id+"F1.opExtrude","CAP_FACE",FACE,{"disambiguationData":[OSD([sQuery(id+"F0.wireOp",EDGE,"E0"),sQuery(id+"F0.wireOp",EDGE,"E1"),sQuery(id+"F0.wireOp",EDGE,"E2"),sQuery(id+"F0.wireOp",EDGE,"E3"),sQuery(id+"F0.wireOp",EDGE,"E4"),sQuery(id+"F0.wireOp",EDGE,"E5"),sQuery(id+"F0.wireOp",EDGE,"E6"),sQuery(id+"F0.wireOp",EDGE,"E7"),sQuery(id+"F0.wireOp",EDGE,"E8"),sQuery(id+"F0.wireOp",EDGE,"E9"),sQuery(id+"F0.wireOp",EDGE,"E10"),sQuery(id+"F0.wireOp",EDGE,"E11"),sQuery(id+"F0.wireOp",EDGE,"E12"),sQuery(id+"F0.wireOp",EDGE,"E13"),subQ1,sQuery(id+"F0.wireOp",EDGE,"E15"),sQuery(id+"F0.wireOp",EDGE,"E17.rect.bottom"),sQuery(id+"F0.wireOp",EDGE,"E17.rect.top"),sQuery(id+"F0.wireOp",EDGE,"E17.rect.left"),sQuery(id+"F0.wireOp",EDGE,"E17.rect.right"),sQuery(id+"F0.wireOp",EDGE,"E18.rect.bottom"),sQuery(id+"F0.wireOp",EDGE,"E18.rect.top"),sQuery(id+"F0.wireOp",EDGE,"E18.rect.left"),sQuery(id+"F0.wireOp",EDGE,"E18.rect.right"),subQ0,sQuery(id+"F0.wireOp",EDGE,"E19.rect.right"),sQuery(id+"F0.wireOp",EDGE,"E20.rect.bottom"),sQuery(id+"F0.wireOp",EDGE,"E20.rect.top"),sQuery(id+"F0.wireOp",EDGE,"E23.top"),sQuery(id+"F0.wireOp",EDGE,"E23.left"),sQuery(id+"F0.wireOp",EDGE,"E23.right"),sQuery(id+"F0.wireOp",EDGE,"E24.top"),sQuery(id+"F0.wireOp",EDGE,"E24.left"),sQuery(id+"F0.wireOp",EDGE,"E24.right"),sQuery(id+"F0.wireOp",EDGE,"E25.top"),sQuery(id+"F0.wireOp",EDGE,"E25.left"),sQuery(id+"F0.wireOp",EDGE,"E25.right"),sQuery(id+"F0.wireOp",EDGE,"E26.top"),sQuery(id+"F0.wireOp",EDGE,"E26.left"),sQuery(id+"F0.wireOp",EDGE,"E26.right")])],"isStart":false})]});}
            var Q54;
            {var subQ0=sQuery(id+"F0.wireOp",EDGE,"E19.rect.left");Q54=makeQuery(id+"F1.opExtrude","CAP_EDGE",EDGE,{"disambiguationData":[OSD([subQ0]),TDD([makeQuery(id+"F0.imprint","IMPRINT",EDGE,{"disambiguationData":[TD([[makeQuery(id+"F0.imprint","INTERSECT",VERTEX,{"derivedFrom":[sQuery(id+"F0.wireOp",EDGE,"E14"),subQ0]}),1.0]])],"derivedFrom":subQ0})])],"isStart":false});}
            var Q55;
            {var subQ0=sQuery(id+"F0.wireOp",EDGE,"E19.rect.left");var subQ1=sQuery(id+"F0.wireOp",EDGE,"E17.rect.top");Q55=makeQuery(id+"F3.opFillet","BLEND_EDGE",EDGE,{"blendedFrom":[makeQuery(id+"F1.opExtrude","SWEPT_EDGE",EDGE,{"disambiguationData":[OSD([subQ1,subQ0])]}),makeQuery(id+"F1.opExtrude","CAP_FACE",FACE,{"disambiguationData":[OSD([sQuery(id+"F0.wireOp",EDGE,"E0"),sQuery(id+"F0.wireOp",EDGE,"E1"),sQuery(id+"F0.wireOp",EDGE,"E2"),sQuery(id+"F0.wireOp",EDGE,"E3"),sQuery(id+"F0.wireOp",EDGE,"E4"),sQuery(id+"F0.wireOp",EDGE,"E5"),sQuery(id+"F0.wireOp",EDGE,"E6"),sQuery(id+"F0.wireOp",EDGE,"E7"),sQuery(id+"F0.wireOp",EDGE,"E8"),sQuery(id+"F0.wireOp",EDGE,"E9"),sQuery(id+"F0.wireOp",EDGE,"E10"),sQuery(id+"F0.wireOp",EDGE,"E11"),sQuery(id+"F0.wireOp",EDGE,"E12"),sQuery(id+"F0.wireOp",EDGE,"E13"),sQuery(id+"F0.wireOp",EDGE,"E14"),sQuery(id+"F0.wireOp",EDGE,"E15"),sQuery(id+"F0.wireOp",EDGE,"E17.rect.bottom"),subQ1,sQuery(id+"F0.wireOp",EDGE,"E17.rect.left"),sQuery(id+"F0.wireOp",EDGE,"E17.rect.right"),sQuery(id+"F0.wireOp",EDGE,"E18.rect.bottom"),sQuery(id+"F0.wireOp",EDGE,"E18.rect.top"),sQuery(id+"F0.wireOp",EDGE,"E18.rect.left"),sQuery(id+"F0.wireOp",EDGE,"E18.rect.right"),subQ0,sQuery(id+"F0.wireOp",EDGE,"E19.rect.right"),sQuery(id+"F0.wireOp",EDGE,"E20.rect.bottom"),sQuery(id+"F0.wireOp",EDGE,"E20.rect.top"),sQuery(id+"F0.wireOp",EDGE,"E23.top"),sQuery(id+"F0.wireOp",EDGE,"E23.left"),sQuery(id+"F0.wireOp",EDGE,"E23.right"),sQuery(id+"F0.wireOp",EDGE,"E24.top"),sQuery(id+"F0.wireOp",EDGE,"E24.left"),sQuery(id+"F0.wireOp",EDGE,"E24.right"),sQuery(id+"F0.wireOp",EDGE,"E25.top"),sQuery(id+"F0.wireOp",EDGE,"E25.left"),sQuery(id+"F0.wireOp",EDGE,"E25.right"),sQuery(id+"F0.wireOp",EDGE,"E26.top"),sQuery(id+"F0.wireOp",EDGE,"E26.left"),sQuery(id+"F0.wireOp",EDGE,"E26.right")])],"isStart":false})],"blendedInto":[makeQuery(id+"F1.opExtrude","CAP_FACE",FACE,{"disambiguationData":[OSD([sQuery(id+"F0.wireOp",EDGE,"E0"),sQuery(id+"F0.wireOp",EDGE,"E1"),sQuery(id+"F0.wireOp",EDGE,"E2"),sQuery(id+"F0.wireOp",EDGE,"E3"),sQuery(id+"F0.wireOp",EDGE,"E4"),sQuery(id+"F0.wireOp",EDGE,"E5"),sQuery(id+"F0.wireOp",EDGE,"E6"),sQuery(id+"F0.wireOp",EDGE,"E7"),sQuery(id+"F0.wireOp",EDGE,"E8"),sQuery(id+"F0.wireOp",EDGE,"E9"),sQuery(id+"F0.wireOp",EDGE,"E10"),sQuery(id+"F0.wireOp",EDGE,"E11"),sQuery(id+"F0.wireOp",EDGE,"E12"),sQuery(id+"F0.wireOp",EDGE,"E13"),sQuery(id+"F0.wireOp",EDGE,"E14"),sQuery(id+"F0.wireOp",EDGE,"E15"),sQuery(id+"F0.wireOp",EDGE,"E17.rect.bottom"),subQ1,sQuery(id+"F0.wireOp",EDGE,"E17.rect.left"),sQuery(id+"F0.wireOp",EDGE,"E17.rect.right"),sQuery(id+"F0.wireOp",EDGE,"E18.rect.bottom"),sQuery(id+"F0.wireOp",EDGE,"E18.rect.top"),sQuery(id+"F0.wireOp",EDGE,"E18.rect.left"),sQuery(id+"F0.wireOp",EDGE,"E18.rect.right"),subQ0,sQuery(id+"F0.wireOp",EDGE,"E19.rect.right"),sQuery(id+"F0.wireOp",EDGE,"E20.rect.bottom"),sQuery(id+"F0.wireOp",EDGE,"E20.rect.top"),sQuery(id+"F0.wireOp",EDGE,"E23.top"),sQuery(id+"F0.wireOp",EDGE,"E23.left"),sQuery(id+"F0.wireOp",EDGE,"E23.right"),sQuery(id+"F0.wireOp",EDGE,"E24.top"),sQuery(id+"F0.wireOp",EDGE,"E24.left"),sQuery(id+"F0.wireOp",EDGE,"E24.right"),sQuery(id+"F0.wireOp",EDGE,"E25.top"),sQuery(id+"F0.wireOp",EDGE,"E25.left"),sQuery(id+"F0.wireOp",EDGE,"E25.right"),sQuery(id+"F0.wireOp",EDGE,"E26.top"),sQuery(id+"F0.wireOp",EDGE,"E26.left"),sQuery(id+"F0.wireOp",EDGE,"E26.right")])],"isStart":false})]});}
            var Q56;
            {var subQ0=sQuery(id+"F0.wireOp",EDGE,"E17.rect.top");Q56=makeQuery(id+"F1.opExtrude","CAP_EDGE",EDGE,{"disambiguationData":[OSD([subQ0]),TDD([makeQuery(id+"F0.imprint","IMPRINT",EDGE,{"disambiguationData":[TD([[makeQuery(id+"F0.imprint","INTERSECT",VERTEX,{"derivedFrom":[subQ0,sQuery(id+"F0.wireOp",EDGE,"E19.rect.left")]}),1.0]])],"derivedFrom":subQ0})])],"isStart":false});}
            var Q57;
            Q57=makeQuery(id+"F1.opExtrude","CAP_EDGE",EDGE,{"disambiguationData":[OSD([sQuery(id+"F0.wireOp",EDGE,"E25.right")])],"isStart":false});
            var Q58;
            Q58=makeQuery(id+"F1.opExtrude","CAP_EDGE",EDGE,{"disambiguationData":[OSD([sQuery(id+"F0.wireOp",EDGE,"E17.rect.left"),sQuery(id+"F0.wireOp",EDGE,"E25.left")])],"isStart":false});
            var Q59;
            {var subQ0=sQuery(id+"F0.wireOp",EDGE,"E20.rect.top");var subQ1=sQuery(id+"F0.wireOp",EDGE,"E17.rect.left");Q59=makeQuery(id+"F3.opFillet","BLEND_EDGE",EDGE,{"blendedFrom":[makeQuery(id+"F1.opExtrude","SWEPT_EDGE",EDGE,{"disambiguationData":[OSD([subQ1,subQ0])]}),makeQuery(id+"F1.opExtrude","CAP_FACE",FACE,{"disambiguationData":[OSD([sQuery(id+"F0.wireOp",EDGE,"E0"),sQuery(id+"F0.wireOp",EDGE,"E1"),sQuery(id+"F0.wireOp",EDGE,"E2"),sQuery(id+"F0.wireOp",EDGE,"E3"),sQuery(id+"F0.wireOp",EDGE,"E4"),sQuery(id+"F0.wireOp",EDGE,"E5"),sQuery(id+"F0.wireOp",EDGE,"E6"),sQuery(id+"F0.wireOp",EDGE,"E7"),sQuery(id+"F0.wireOp",EDGE,"E8"),sQuery(id+"F0.wireOp",EDGE,"E9"),sQuery(id+"F0.wireOp",EDGE,"E10"),sQuery(id+"F0.wireOp",EDGE,"E11"),sQuery(id+"F0.wireOp",EDGE,"E12"),sQuery(id+"F0.wireOp",EDGE,"E13"),sQuery(id+"F0.wireOp",EDGE,"E14"),sQuery(id+"F0.wireOp",EDGE,"E15"),sQuery(id+"F0.wireOp",EDGE,"E17.rect.bottom"),sQuery(id+"F0.wireOp",EDGE,"E17.rect.top"),subQ1,sQuery(id+"F0.wireOp",EDGE,"E17.rect.right"),sQuery(id+"F0.wireOp",EDGE,"E18.rect.bottom"),sQuery(id+"F0.wireOp",EDGE,"E18.rect.top"),sQuery(id+"F0.wireOp",EDGE,"E18.rect.left"),sQuery(id+"F0.wireOp",EDGE,"E18.rect.right"),sQuery(id+"F0.wireOp",EDGE,"E19.rect.left"),sQuery(id+"F0.wireOp",EDGE,"E19.rect.right"),sQuery(id+"F0.wireOp",EDGE,"E20.rect.bottom"),subQ0,sQuery(id+"F0.wireOp",EDGE,"E23.top"),sQuery(id+"F0.wireOp",EDGE,"E23.left"),sQuery(id+"F0.wireOp",EDGE,"E23.right"),sQuery(id+"F0.wireOp",EDGE,"E24.top"),sQuery(id+"F0.wireOp",EDGE,"E24.left"),sQuery(id+"F0.wireOp",EDGE,"E24.right"),sQuery(id+"F0.wireOp",EDGE,"E25.top"),sQuery(id+"F0.wireOp",EDGE,"E25.left"),sQuery(id+"F0.wireOp",EDGE,"E25.right"),sQuery(id+"F0.wireOp",EDGE,"E26.top"),sQuery(id+"F0.wireOp",EDGE,"E26.left"),sQuery(id+"F0.wireOp",EDGE,"E26.right")])],"isStart":false})],"blendedInto":[makeQuery(id+"F1.opExtrude","CAP_FACE",FACE,{"disambiguationData":[OSD([sQuery(id+"F0.wireOp",EDGE,"E0"),sQuery(id+"F0.wireOp",EDGE,"E1"),sQuery(id+"F0.wireOp",EDGE,"E2"),sQuery(id+"F0.wireOp",EDGE,"E3"),sQuery(id+"F0.wireOp",EDGE,"E4"),sQuery(id+"F0.wireOp",EDGE,"E5"),sQuery(id+"F0.wireOp",EDGE,"E6"),sQuery(id+"F0.wireOp",EDGE,"E7"),sQuery(id+"F0.wireOp",EDGE,"E8"),sQuery(id+"F0.wireOp",EDGE,"E9"),sQuery(id+"F0.wireOp",EDGE,"E10"),sQuery(id+"F0.wireOp",EDGE,"E11"),sQuery(id+"F0.wireOp",EDGE,"E12"),sQuery(id+"F0.wireOp",EDGE,"E13"),sQuery(id+"F0.wireOp",EDGE,"E14"),sQuery(id+"F0.wireOp",EDGE,"E15"),sQuery(id+"F0.wireOp",EDGE,"E17.rect.bottom"),sQuery(id+"F0.wireOp",EDGE,"E17.rect.top"),subQ1,sQuery(id+"F0.wireOp",EDGE,"E17.rect.right"),sQuery(id+"F0.wireOp",EDGE,"E18.rect.bottom"),sQuery(id+"F0.wireOp",EDGE,"E18.rect.top"),sQuery(id+"F0.wireOp",EDGE,"E18.rect.left"),sQuery(id+"F0.wireOp",EDGE,"E18.rect.right"),sQuery(id+"F0.wireOp",EDGE,"E19.rect.left"),sQuery(id+"F0.wireOp",EDGE,"E19.rect.right"),sQuery(id+"F0.wireOp",EDGE,"E20.rect.bottom"),subQ0,sQuery(id+"F0.wireOp",EDGE,"E23.top"),sQuery(id+"F0.wireOp",EDGE,"E23.left"),sQuery(id+"F0.wireOp",EDGE,"E23.right"),sQuery(id+"F0.wireOp",EDGE,"E24.top"),sQuery(id+"F0.wireOp",EDGE,"E24.left"),sQuery(id+"F0.wireOp",EDGE,"E24.right"),sQuery(id+"F0.wireOp",EDGE,"E25.top"),sQuery(id+"F0.wireOp",EDGE,"E25.left"),sQuery(id+"F0.wireOp",EDGE,"E25.right"),sQuery(id+"F0.wireOp",EDGE,"E26.top"),sQuery(id+"F0.wireOp",EDGE,"E26.left"),sQuery(id+"F0.wireOp",EDGE,"E26.right")])],"isStart":false})]});}
            var Q60;
            {var subQ0=sQuery(id+"F0.wireOp",EDGE,"E20.rect.top");Q60=makeQuery(id+"F1.opExtrude","CAP_EDGE",EDGE,{"disambiguationData":[OSD([subQ0]),TDD([makeQuery(id+"F0.imprint","IMPRINT",EDGE,{"disambiguationData":[TD([[makeQuery(id+"F0.imprint","INTERSECT",VERTEX,{"derivedFrom":[sQuery(id+"F0.wireOp",EDGE,"E12"),subQ0]}),-1.0]])],"derivedFrom":subQ0})])],"isStart":false});}
            var Q61;
            {var subQ0=sQuery(id+"F0.wireOp",EDGE,"E20.rect.top");var subQ1=sQuery(id+"F0.wireOp",EDGE,"E12");Q61=makeQuery(id+"F3.opFillet","BLEND_EDGE",EDGE,{"blendedFrom":[makeQuery(id+"F1.opExtrude","SWEPT_EDGE",EDGE,{"disambiguationData":[OSD([subQ1,subQ0])]}),makeQuery(id+"F1.opExtrude","CAP_FACE",FACE,{"disambiguationData":[OSD([sQuery(id+"F0.wireOp",EDGE,"E0"),sQuery(id+"F0.wireOp",EDGE,"E1"),sQuery(id+"F0.wireOp",EDGE,"E2"),sQuery(id+"F0.wireOp",EDGE,"E3"),sQuery(id+"F0.wireOp",EDGE,"E4"),sQuery(id+"F0.wireOp",EDGE,"E5"),sQuery(id+"F0.wireOp",EDGE,"E6"),sQuery(id+"F0.wireOp",EDGE,"E7"),sQuery(id+"F0.wireOp",EDGE,"E8"),sQuery(id+"F0.wireOp",EDGE,"E9"),sQuery(id+"F0.wireOp",EDGE,"E10"),sQuery(id+"F0.wireOp",EDGE,"E11"),subQ1,sQuery(id+"F0.wireOp",EDGE,"E13"),sQuery(id+"F0.wireOp",EDGE,"E14"),sQuery(id+"F0.wireOp",EDGE,"E15"),sQuery(id+"F0.wireOp",EDGE,"E17.rect.bottom"),sQuery(id+"F0.wireOp",EDGE,"E17.rect.top"),sQuery(id+"F0.wireOp",EDGE,"E17.rect.left"),sQuery(id+"F0.wireOp",EDGE,"E17.rect.right"),sQuery(id+"F0.wireOp",EDGE,"E18.rect.bottom"),sQuery(id+"F0.wireOp",EDGE,"E18.rect.top"),sQuery(id+"F0.wireOp",EDGE,"E18.rect.left"),sQuery(id+"F0.wireOp",EDGE,"E18.rect.right"),sQuery(id+"F0.wireOp",EDGE,"E19.rect.left"),sQuery(id+"F0.wireOp",EDGE,"E19.rect.right"),sQuery(id+"F0.wireOp",EDGE,"E20.rect.bottom"),subQ0,sQuery(id+"F0.wireOp",EDGE,"E23.top"),sQuery(id+"F0.wireOp",EDGE,"E23.left"),sQuery(id+"F0.wireOp",EDGE,"E23.right"),sQuery(id+"F0.wireOp",EDGE,"E24.top"),sQuery(id+"F0.wireOp",EDGE,"E24.left"),sQuery(id+"F0.wireOp",EDGE,"E24.right"),sQuery(id+"F0.wireOp",EDGE,"E25.top"),sQuery(id+"F0.wireOp",EDGE,"E25.left"),sQuery(id+"F0.wireOp",EDGE,"E25.right"),sQuery(id+"F0.wireOp",EDGE,"E26.top"),sQuery(id+"F0.wireOp",EDGE,"E26.left"),sQuery(id+"F0.wireOp",EDGE,"E26.right")])],"isStart":false})],"blendedInto":[makeQuery(id+"F1.opExtrude","CAP_FACE",FACE,{"disambiguationData":[OSD([sQuery(id+"F0.wireOp",EDGE,"E0"),sQuery(id+"F0.wireOp",EDGE,"E1"),sQuery(id+"F0.wireOp",EDGE,"E2"),sQuery(id+"F0.wireOp",EDGE,"E3"),sQuery(id+"F0.wireOp",EDGE,"E4"),sQuery(id+"F0.wireOp",EDGE,"E5"),sQuery(id+"F0.wireOp",EDGE,"E6"),sQuery(id+"F0.wireOp",EDGE,"E7"),sQuery(id+"F0.wireOp",EDGE,"E8"),sQuery(id+"F0.wireOp",EDGE,"E9"),sQuery(id+"F0.wireOp",EDGE,"E10"),sQuery(id+"F0.wireOp",EDGE,"E11"),subQ1,sQuery(id+"F0.wireOp",EDGE,"E13"),sQuery(id+"F0.wireOp",EDGE,"E14"),sQuery(id+"F0.wireOp",EDGE,"E15"),sQuery(id+"F0.wireOp",EDGE,"E17.rect.bottom"),sQuery(id+"F0.wireOp",EDGE,"E17.rect.top"),sQuery(id+"F0.wireOp",EDGE,"E17.rect.left"),sQuery(id+"F0.wireOp",EDGE,"E17.rect.right"),sQuery(id+"F0.wireOp",EDGE,"E18.rect.bottom"),sQuery(id+"F0.wireOp",EDGE,"E18.rect.top"),sQuery(id+"F0.wireOp",EDGE,"E18.rect.left"),sQuery(id+"F0.wireOp",EDGE,"E18.rect.right"),sQuery(id+"F0.wireOp",EDGE,"E19.rect.left"),sQuery(id+"F0.wireOp",EDGE,"E19.rect.right"),sQuery(id+"F0.wireOp",EDGE,"E20.rect.bottom"),subQ0,sQuery(id+"F0.wireOp",EDGE,"E23.top"),sQuery(id+"F0.wireOp",EDGE,"E23.left"),sQuery(id+"F0.wireOp",EDGE,"E23.right"),sQuery(id+"F0.wireOp",EDGE,"E24.top"),sQuery(id+"F0.wireOp",EDGE,"E24.left"),sQuery(id+"F0.wireOp",EDGE,"E24.right"),sQuery(id+"F0.wireOp",EDGE,"E25.top"),sQuery(id+"F0.wireOp",EDGE,"E25.left"),sQuery(id+"F0.wireOp",EDGE,"E25.right"),sQuery(id+"F0.wireOp",EDGE,"E26.top"),sQuery(id+"F0.wireOp",EDGE,"E26.left"),sQuery(id+"F0.wireOp",EDGE,"E26.right")])],"isStart":false})]});}
            var Q62;
            {var subQ0=sQuery(id+"F0.wireOp",EDGE,"E12");var subQ1=makeQuery(id+"F0.imprint","INTERSECT",VERTEX,{"disambiguationData":[OD(0.0)],"derivedFrom":[sQuery(id+"F0.wireOp",EDGE,"E6"),subQ0]});Q62=makeQuery(id+"F1.opExtrude","CAP_EDGE",EDGE,{"disambiguationData":[OSD([subQ0]),TDD([makeQuery(id+"F0.imprint","IMPRINT",EDGE,{"disambiguationData":[TD([[subQ1,1.0]])],"derivedFrom":subQ0}),makeQuery(id+"F0.imprint","IMPRINT",EDGE,{"disambiguationData":[TD([[makeQuery(id+"F0.imprint","INTERSECT",VERTEX,{"disambiguationData":[OD(0.0)],"derivedFrom":[sQuery(id+"F0.wireOp",EDGE,"E2"),subQ0]}),1.0]])],"derivedFrom":subQ0})])],"isStart":false});}
            var Q63;
            {var subQ0=sQuery(id+"F0.wireOp",EDGE,"E18.rect.left");var subQ1=sQuery(id+"F0.wireOp",EDGE,"E18.rect.top");Q63=makeQuery(id+"F3.opFillet","BLEND_EDGE",EDGE,{"blendedFrom":[makeQuery(id+"F1.opExtrude","SWEPT_EDGE",EDGE,{"disambiguationData":[OSD([subQ1,subQ0])]}),makeQuery(id+"F1.opExtrude","CAP_FACE",FACE,{"disambiguationData":[OSD([sQuery(id+"F0.wireOp",EDGE,"E0"),sQuery(id+"F0.wireOp",EDGE,"E1"),sQuery(id+"F0.wireOp",EDGE,"E2"),sQuery(id+"F0.wireOp",EDGE,"E3"),sQuery(id+"F0.wireOp",EDGE,"E4"),sQuery(id+"F0.wireOp",EDGE,"E5"),sQuery(id+"F0.wireOp",EDGE,"E6"),sQuery(id+"F0.wireOp",EDGE,"E7"),sQuery(id+"F0.wireOp",EDGE,"E8"),sQuery(id+"F0.wireOp",EDGE,"E9"),sQuery(id+"F0.wireOp",EDGE,"E10"),sQuery(id+"F0.wireOp",EDGE,"E11"),sQuery(id+"F0.wireOp",EDGE,"E12"),sQuery(id+"F0.wireOp",EDGE,"E13"),sQuery(id+"F0.wireOp",EDGE,"E14"),sQuery(id+"F0.wireOp",EDGE,"E15"),sQuery(id+"F0.wireOp",EDGE,"E17.rect.bottom"),sQuery(id+"F0.wireOp",EDGE,"E17.rect.top"),sQuery(id+"F0.wireOp",EDGE,"E17.rect.left"),sQuery(id+"F0.wireOp",EDGE,"E17.rect.right"),sQuery(id+"F0.wireOp",EDGE,"E18.rect.bottom"),subQ1,subQ0,sQuery(id+"F0.wireOp",EDGE,"E18.rect.right"),sQuery(id+"F0.wireOp",EDGE,"E19.rect.left"),sQuery(id+"F0.wireOp",EDGE,"E19.rect.right"),sQuery(id+"F0.wireOp",EDGE,"E20.rect.bottom"),sQuery(id+"F0.wireOp",EDGE,"E20.rect.top"),sQuery(id+"F0.wireOp",EDGE,"E23.top"),sQuery(id+"F0.wireOp",EDGE,"E23.left"),sQuery(id+"F0.wireOp",EDGE,"E23.right"),sQuery(id+"F0.wireOp",EDGE,"E24.top"),sQuery(id+"F0.wireOp",EDGE,"E24.left"),sQuery(id+"F0.wireOp",EDGE,"E24.right"),sQuery(id+"F0.wireOp",EDGE,"E25.top"),sQuery(id+"F0.wireOp",EDGE,"E25.left"),sQuery(id+"F0.wireOp",EDGE,"E25.right"),sQuery(id+"F0.wireOp",EDGE,"E26.top"),sQuery(id+"F0.wireOp",EDGE,"E26.left"),sQuery(id+"F0.wireOp",EDGE,"E26.right")])],"isStart":false})],"blendedInto":[makeQuery(id+"F1.opExtrude","CAP_FACE",FACE,{"disambiguationData":[OSD([sQuery(id+"F0.wireOp",EDGE,"E0"),sQuery(id+"F0.wireOp",EDGE,"E1"),sQuery(id+"F0.wireOp",EDGE,"E2"),sQuery(id+"F0.wireOp",EDGE,"E3"),sQuery(id+"F0.wireOp",EDGE,"E4"),sQuery(id+"F0.wireOp",EDGE,"E5"),sQuery(id+"F0.wireOp",EDGE,"E6"),sQuery(id+"F0.wireOp",EDGE,"E7"),sQuery(id+"F0.wireOp",EDGE,"E8"),sQuery(id+"F0.wireOp",EDGE,"E9"),sQuery(id+"F0.wireOp",EDGE,"E10"),sQuery(id+"F0.wireOp",EDGE,"E11"),sQuery(id+"F0.wireOp",EDGE,"E12"),sQuery(id+"F0.wireOp",EDGE,"E13"),sQuery(id+"F0.wireOp",EDGE,"E14"),sQuery(id+"F0.wireOp",EDGE,"E15"),sQuery(id+"F0.wireOp",EDGE,"E17.rect.bottom"),sQuery(id+"F0.wireOp",EDGE,"E17.rect.top"),sQuery(id+"F0.wireOp",EDGE,"E17.rect.left"),sQuery(id+"F0.wireOp",EDGE,"E17.rect.right"),sQuery(id+"F0.wireOp",EDGE,"E18.rect.bottom"),subQ1,subQ0,sQuery(id+"F0.wireOp",EDGE,"E18.rect.right"),sQuery(id+"F0.wireOp",EDGE,"E19.rect.left"),sQuery(id+"F0.wireOp",EDGE,"E19.rect.right"),sQuery(id+"F0.wireOp",EDGE,"E20.rect.bottom"),sQuery(id+"F0.wireOp",EDGE,"E20.rect.top"),sQuery(id+"F0.wireOp",EDGE,"E23.top"),sQuery(id+"F0.wireOp",EDGE,"E23.left"),sQuery(id+"F0.wireOp",EDGE,"E23.right"),sQuery(id+"F0.wireOp",EDGE,"E24.top"),sQuery(id+"F0.wireOp",EDGE,"E24.left"),sQuery(id+"F0.wireOp",EDGE,"E24.right"),sQuery(id+"F0.wireOp",EDGE,"E25.top"),sQuery(id+"F0.wireOp",EDGE,"E25.left"),sQuery(id+"F0.wireOp",EDGE,"E25.right"),sQuery(id+"F0.wireOp",EDGE,"E26.top"),sQuery(id+"F0.wireOp",EDGE,"E26.left"),sQuery(id+"F0.wireOp",EDGE,"E26.right")])],"isStart":false})]});}
            var Q64;
            Q64=makeQuery(id+"F1.opExtrude","CAP_EDGE",EDGE,{"disambiguationData":[OSD([sQuery(id+"F0.wireOp",EDGE,"E18.rect.top")])],"isStart":false});
            var Q65;
            Q65=makeQuery(id+"F1.opExtrude","CAP_EDGE",EDGE,{"disambiguationData":[OSD([sQuery(id+"F0.wireOp",EDGE,"E18.rect.left")])],"isStart":false});
            var Q66;
            {var subQ0=sQuery(id+"F0.wireOp",EDGE,"E18.rect.left");var subQ1=sQuery(id+"F0.wireOp",EDGE,"E18.rect.bottom");Q66=makeQuery(id+"F3.opFillet","BLEND_EDGE",EDGE,{"blendedFrom":[makeQuery(id+"F1.opExtrude","SWEPT_EDGE",EDGE,{"disambiguationData":[OSD([subQ1,subQ0])]}),makeQuery(id+"F1.opExtrude","CAP_FACE",FACE,{"disambiguationData":[OSD([sQuery(id+"F0.wireOp",EDGE,"E0"),sQuery(id+"F0.wireOp",EDGE,"E1"),sQuery(id+"F0.wireOp",EDGE,"E2"),sQuery(id+"F0.wireOp",EDGE,"E3"),sQuery(id+"F0.wireOp",EDGE,"E4"),sQuery(id+"F0.wireOp",EDGE,"E5"),sQuery(id+"F0.wireOp",EDGE,"E6"),sQuery(id+"F0.wireOp",EDGE,"E7"),sQuery(id+"F0.wireOp",EDGE,"E8"),sQuery(id+"F0.wireOp",EDGE,"E9"),sQuery(id+"F0.wireOp",EDGE,"E10"),sQuery(id+"F0.wireOp",EDGE,"E11"),sQuery(id+"F0.wireOp",EDGE,"E12"),sQuery(id+"F0.wireOp",EDGE,"E13"),sQuery(id+"F0.wireOp",EDGE,"E14"),sQuery(id+"F0.wireOp",EDGE,"E15"),sQuery(id+"F0.wireOp",EDGE,"E17.rect.bottom"),sQuery(id+"F0.wireOp",EDGE,"E17.rect.top"),sQuery(id+"F0.wireOp",EDGE,"E17.rect.left"),sQuery(id+"F0.wireOp",EDGE,"E17.rect.right"),subQ1,sQuery(id+"F0.wireOp",EDGE,"E18.rect.top"),subQ0,sQuery(id+"F0.wireOp",EDGE,"E18.rect.right"),sQuery(id+"F0.wireOp",EDGE,"E19.rect.left"),sQuery(id+"F0.wireOp",EDGE,"E19.rect.right"),sQuery(id+"F0.wireOp",EDGE,"E20.rect.bottom"),sQuery(id+"F0.wireOp",EDGE,"E20.rect.top"),sQuery(id+"F0.wireOp",EDGE,"E23.top"),sQuery(id+"F0.wireOp",EDGE,"E23.left"),sQuery(id+"F0.wireOp",EDGE,"E23.right"),sQuery(id+"F0.wireOp",EDGE,"E24.top"),sQuery(id+"F0.wireOp",EDGE,"E24.left"),sQuery(id+"F0.wireOp",EDGE,"E24.right"),sQuery(id+"F0.wireOp",EDGE,"E25.top"),sQuery(id+"F0.wireOp",EDGE,"E25.left"),sQuery(id+"F0.wireOp",EDGE,"E25.right"),sQuery(id+"F0.wireOp",EDGE,"E26.top"),sQuery(id+"F0.wireOp",EDGE,"E26.left"),sQuery(id+"F0.wireOp",EDGE,"E26.right")])],"isStart":false})],"blendedInto":[makeQuery(id+"F1.opExtrude","CAP_FACE",FACE,{"disambiguationData":[OSD([sQuery(id+"F0.wireOp",EDGE,"E0"),sQuery(id+"F0.wireOp",EDGE,"E1"),sQuery(id+"F0.wireOp",EDGE,"E2"),sQuery(id+"F0.wireOp",EDGE,"E3"),sQuery(id+"F0.wireOp",EDGE,"E4"),sQuery(id+"F0.wireOp",EDGE,"E5"),sQuery(id+"F0.wireOp",EDGE,"E6"),sQuery(id+"F0.wireOp",EDGE,"E7"),sQuery(id+"F0.wireOp",EDGE,"E8"),sQuery(id+"F0.wireOp",EDGE,"E9"),sQuery(id+"F0.wireOp",EDGE,"E10"),sQuery(id+"F0.wireOp",EDGE,"E11"),sQuery(id+"F0.wireOp",EDGE,"E12"),sQuery(id+"F0.wireOp",EDGE,"E13"),sQuery(id+"F0.wireOp",EDGE,"E14"),sQuery(id+"F0.wireOp",EDGE,"E15"),sQuery(id+"F0.wireOp",EDGE,"E17.rect.bottom"),sQuery(id+"F0.wireOp",EDGE,"E17.rect.top"),sQuery(id+"F0.wireOp",EDGE,"E17.rect.left"),sQuery(id+"F0.wireOp",EDGE,"E17.rect.right"),subQ1,sQuery(id+"F0.wireOp",EDGE,"E18.rect.top"),subQ0,sQuery(id+"F0.wireOp",EDGE,"E18.rect.right"),sQuery(id+"F0.wireOp",EDGE,"E19.rect.left"),sQuery(id+"F0.wireOp",EDGE,"E19.rect.right"),sQuery(id+"F0.wireOp",EDGE,"E20.rect.bottom"),sQuery(id+"F0.wireOp",EDGE,"E20.rect.top"),sQuery(id+"F0.wireOp",EDGE,"E23.top"),sQuery(id+"F0.wireOp",EDGE,"E23.left"),sQuery(id+"F0.wireOp",EDGE,"E23.right"),sQuery(id+"F0.wireOp",EDGE,"E24.top"),sQuery(id+"F0.wireOp",EDGE,"E24.left"),sQuery(id+"F0.wireOp",EDGE,"E24.right"),sQuery(id+"F0.wireOp",EDGE,"E25.top"),sQuery(id+"F0.wireOp",EDGE,"E25.left"),sQuery(id+"F0.wireOp",EDGE,"E25.right"),sQuery(id+"F0.wireOp",EDGE,"E26.top"),sQuery(id+"F0.wireOp",EDGE,"E26.left"),sQuery(id+"F0.wireOp",EDGE,"E26.right")])],"isStart":false})]});}
            var Q67;
            Q67=makeQuery(id+"F1.opExtrude","CAP_EDGE",EDGE,{"disambiguationData":[OSD([sQuery(id+"F0.wireOp",EDGE,"E18.rect.bottom")])],"isStart":false});
            var Q68;
            {var subQ0=sQuery(id+"F0.wireOp",EDGE,"E18.rect.right");var subQ1=sQuery(id+"F0.wireOp",EDGE,"E18.rect.bottom");Q68=makeQuery(id+"F3.opFillet","BLEND_EDGE",EDGE,{"blendedFrom":[makeQuery(id+"F1.opExtrude","SWEPT_EDGE",EDGE,{"disambiguationData":[OSD([subQ1,subQ0])]}),makeQuery(id+"F1.opExtrude","CAP_FACE",FACE,{"disambiguationData":[OSD([sQuery(id+"F0.wireOp",EDGE,"E0"),sQuery(id+"F0.wireOp",EDGE,"E1"),sQuery(id+"F0.wireOp",EDGE,"E2"),sQuery(id+"F0.wireOp",EDGE,"E3"),sQuery(id+"F0.wireOp",EDGE,"E4"),sQuery(id+"F0.wireOp",EDGE,"E5"),sQuery(id+"F0.wireOp",EDGE,"E6"),sQuery(id+"F0.wireOp",EDGE,"E7"),sQuery(id+"F0.wireOp",EDGE,"E8"),sQuery(id+"F0.wireOp",EDGE,"E9"),sQuery(id+"F0.wireOp",EDGE,"E10"),sQuery(id+"F0.wireOp",EDGE,"E11"),sQuery(id+"F0.wireOp",EDGE,"E12"),sQuery(id+"F0.wireOp",EDGE,"E13"),sQuery(id+"F0.wireOp",EDGE,"E14"),sQuery(id+"F0.wireOp",EDGE,"E15"),sQuery(id+"F0.wireOp",EDGE,"E17.rect.bottom"),sQuery(id+"F0.wireOp",EDGE,"E17.rect.top"),sQuery(id+"F0.wireOp",EDGE,"E17.rect.left"),sQuery(id+"F0.wireOp",EDGE,"E17.rect.right"),subQ1,sQuery(id+"F0.wireOp",EDGE,"E18.rect.top"),sQuery(id+"F0.wireOp",EDGE,"E18.rect.left"),subQ0,sQuery(id+"F0.wireOp",EDGE,"E19.rect.left"),sQuery(id+"F0.wireOp",EDGE,"E19.rect.right"),sQuery(id+"F0.wireOp",EDGE,"E20.rect.bottom"),sQuery(id+"F0.wireOp",EDGE,"E20.rect.top"),sQuery(id+"F0.wireOp",EDGE,"E23.top"),sQuery(id+"F0.wireOp",EDGE,"E23.left"),sQuery(id+"F0.wireOp",EDGE,"E23.right"),sQuery(id+"F0.wireOp",EDGE,"E24.top"),sQuery(id+"F0.wireOp",EDGE,"E24.left"),sQuery(id+"F0.wireOp",EDGE,"E24.right"),sQuery(id+"F0.wireOp",EDGE,"E25.top"),sQuery(id+"F0.wireOp",EDGE,"E25.left"),sQuery(id+"F0.wireOp",EDGE,"E25.right"),sQuery(id+"F0.wireOp",EDGE,"E26.top"),sQuery(id+"F0.wireOp",EDGE,"E26.left"),sQuery(id+"F0.wireOp",EDGE,"E26.right")])],"isStart":false})],"blendedInto":[makeQuery(id+"F1.opExtrude","CAP_FACE",FACE,{"disambiguationData":[OSD([sQuery(id+"F0.wireOp",EDGE,"E0"),sQuery(id+"F0.wireOp",EDGE,"E1"),sQuery(id+"F0.wireOp",EDGE,"E2"),sQuery(id+"F0.wireOp",EDGE,"E3"),sQuery(id+"F0.wireOp",EDGE,"E4"),sQuery(id+"F0.wireOp",EDGE,"E5"),sQuery(id+"F0.wireOp",EDGE,"E6"),sQuery(id+"F0.wireOp",EDGE,"E7"),sQuery(id+"F0.wireOp",EDGE,"E8"),sQuery(id+"F0.wireOp",EDGE,"E9"),sQuery(id+"F0.wireOp",EDGE,"E10"),sQuery(id+"F0.wireOp",EDGE,"E11"),sQuery(id+"F0.wireOp",EDGE,"E12"),sQuery(id+"F0.wireOp",EDGE,"E13"),sQuery(id+"F0.wireOp",EDGE,"E14"),sQuery(id+"F0.wireOp",EDGE,"E15"),sQuery(id+"F0.wireOp",EDGE,"E17.rect.bottom"),sQuery(id+"F0.wireOp",EDGE,"E17.rect.top"),sQuery(id+"F0.wireOp",EDGE,"E17.rect.left"),sQuery(id+"F0.wireOp",EDGE,"E17.rect.right"),subQ1,sQuery(id+"F0.wireOp",EDGE,"E18.rect.top"),sQuery(id+"F0.wireOp",EDGE,"E18.rect.left"),subQ0,sQuery(id+"F0.wireOp",EDGE,"E19.rect.left"),sQuery(id+"F0.wireOp",EDGE,"E19.rect.right"),sQuery(id+"F0.wireOp",EDGE,"E20.rect.bottom"),sQuery(id+"F0.wireOp",EDGE,"E20.rect.top"),sQuery(id+"F0.wireOp",EDGE,"E23.top"),sQuery(id+"F0.wireOp",EDGE,"E23.left"),sQuery(id+"F0.wireOp",EDGE,"E23.right"),sQuery(id+"F0.wireOp",EDGE,"E24.top"),sQuery(id+"F0.wireOp",EDGE,"E24.left"),sQuery(id+"F0.wireOp",EDGE,"E24.right"),sQuery(id+"F0.wireOp",EDGE,"E25.top"),sQuery(id+"F0.wireOp",EDGE,"E25.left"),sQuery(id+"F0.wireOp",EDGE,"E25.right"),sQuery(id+"F0.wireOp",EDGE,"E26.top"),sQuery(id+"F0.wireOp",EDGE,"E26.left"),sQuery(id+"F0.wireOp",EDGE,"E26.right")])],"isStart":false})]});}
            var Q69;
            Q69=makeQuery(id+"F1.opExtrude","CAP_EDGE",EDGE,{"disambiguationData":[OSD([sQuery(id+"F0.wireOp",EDGE,"E18.rect.right")])],"isStart":false});
            var Q70;
            {var subQ0=sQuery(id+"F0.wireOp",EDGE,"E18.rect.right");var subQ1=sQuery(id+"F0.wireOp",EDGE,"E18.rect.top");Q70=makeQuery(id+"F3.opFillet","BLEND_EDGE",EDGE,{"blendedFrom":[makeQuery(id+"F1.opExtrude","SWEPT_EDGE",EDGE,{"disambiguationData":[OSD([subQ1,subQ0])]}),makeQuery(id+"F1.opExtrude","CAP_FACE",FACE,{"disambiguationData":[OSD([sQuery(id+"F0.wireOp",EDGE,"E0"),sQuery(id+"F0.wireOp",EDGE,"E1"),sQuery(id+"F0.wireOp",EDGE,"E2"),sQuery(id+"F0.wireOp",EDGE,"E3"),sQuery(id+"F0.wireOp",EDGE,"E4"),sQuery(id+"F0.wireOp",EDGE,"E5"),sQuery(id+"F0.wireOp",EDGE,"E6"),sQuery(id+"F0.wireOp",EDGE,"E7"),sQuery(id+"F0.wireOp",EDGE,"E8"),sQuery(id+"F0.wireOp",EDGE,"E9"),sQuery(id+"F0.wireOp",EDGE,"E10"),sQuery(id+"F0.wireOp",EDGE,"E11"),sQuery(id+"F0.wireOp",EDGE,"E12"),sQuery(id+"F0.wireOp",EDGE,"E13"),sQuery(id+"F0.wireOp",EDGE,"E14"),sQuery(id+"F0.wireOp",EDGE,"E15"),sQuery(id+"F0.wireOp",EDGE,"E17.rect.bottom"),sQuery(id+"F0.wireOp",EDGE,"E17.rect.top"),sQuery(id+"F0.wireOp",EDGE,"E17.rect.left"),sQuery(id+"F0.wireOp",EDGE,"E17.rect.right"),sQuery(id+"F0.wireOp",EDGE,"E18.rect.bottom"),subQ1,sQuery(id+"F0.wireOp",EDGE,"E18.rect.left"),subQ0,sQuery(id+"F0.wireOp",EDGE,"E19.rect.left"),sQuery(id+"F0.wireOp",EDGE,"E19.rect.right"),sQuery(id+"F0.wireOp",EDGE,"E20.rect.bottom"),sQuery(id+"F0.wireOp",EDGE,"E20.rect.top"),sQuery(id+"F0.wireOp",EDGE,"E23.top"),sQuery(id+"F0.wireOp",EDGE,"E23.left"),sQuery(id+"F0.wireOp",EDGE,"E23.right"),sQuery(id+"F0.wireOp",EDGE,"E24.top"),sQuery(id+"F0.wireOp",EDGE,"E24.left"),sQuery(id+"F0.wireOp",EDGE,"E24.right"),sQuery(id+"F0.wireOp",EDGE,"E25.top"),sQuery(id+"F0.wireOp",EDGE,"E25.left"),sQuery(id+"F0.wireOp",EDGE,"E25.right"),sQuery(id+"F0.wireOp",EDGE,"E26.top"),sQuery(id+"F0.wireOp",EDGE,"E26.left"),sQuery(id+"F0.wireOp",EDGE,"E26.right")])],"isStart":false})],"blendedInto":[makeQuery(id+"F1.opExtrude","CAP_FACE",FACE,{"disambiguationData":[OSD([sQuery(id+"F0.wireOp",EDGE,"E0"),sQuery(id+"F0.wireOp",EDGE,"E1"),sQuery(id+"F0.wireOp",EDGE,"E2"),sQuery(id+"F0.wireOp",EDGE,"E3"),sQuery(id+"F0.wireOp",EDGE,"E4"),sQuery(id+"F0.wireOp",EDGE,"E5"),sQuery(id+"F0.wireOp",EDGE,"E6"),sQuery(id+"F0.wireOp",EDGE,"E7"),sQuery(id+"F0.wireOp",EDGE,"E8"),sQuery(id+"F0.wireOp",EDGE,"E9"),sQuery(id+"F0.wireOp",EDGE,"E10"),sQuery(id+"F0.wireOp",EDGE,"E11"),sQuery(id+"F0.wireOp",EDGE,"E12"),sQuery(id+"F0.wireOp",EDGE,"E13"),sQuery(id+"F0.wireOp",EDGE,"E14"),sQuery(id+"F0.wireOp",EDGE,"E15"),sQuery(id+"F0.wireOp",EDGE,"E17.rect.bottom"),sQuery(id+"F0.wireOp",EDGE,"E17.rect.top"),sQuery(id+"F0.wireOp",EDGE,"E17.rect.left"),sQuery(id+"F0.wireOp",EDGE,"E17.rect.right"),sQuery(id+"F0.wireOp",EDGE,"E18.rect.bottom"),subQ1,sQuery(id+"F0.wireOp",EDGE,"E18.rect.left"),subQ0,sQuery(id+"F0.wireOp",EDGE,"E19.rect.left"),sQuery(id+"F0.wireOp",EDGE,"E19.rect.right"),sQuery(id+"F0.wireOp",EDGE,"E20.rect.bottom"),sQuery(id+"F0.wireOp",EDGE,"E20.rect.top"),sQuery(id+"F0.wireOp",EDGE,"E23.top"),sQuery(id+"F0.wireOp",EDGE,"E23.left"),sQuery(id+"F0.wireOp",EDGE,"E23.right"),sQuery(id+"F0.wireOp",EDGE,"E24.top"),sQuery(id+"F0.wireOp",EDGE,"E24.left"),sQuery(id+"F0.wireOp",EDGE,"E24.right"),sQuery(id+"F0.wireOp",EDGE,"E25.top"),sQuery(id+"F0.wireOp",EDGE,"E25.left"),sQuery(id+"F0.wireOp",EDGE,"E25.right"),sQuery(id+"F0.wireOp",EDGE,"E26.top"),sQuery(id+"F0.wireOp",EDGE,"E26.left"),sQuery(id+"F0.wireOp",EDGE,"E26.right")])],"isStart":false})]});}
            var Q71;
            {var subQ0=sQuery(id+"F0.wireOp",EDGE,"E17.rect.top");Q71=makeQuery(id+"F1.opExtrude","CAP_EDGE",EDGE,{"disambiguationData":[OSD([subQ0]),TDD([makeQuery(id+"F0.imprint","IMPRINT",EDGE,{"disambiguationData":[TD([[makeQuery(id+"F0.imprint","INTERSECT",VERTEX,{"derivedFrom":[subQ0,sQuery(id+"F0.wireOp",EDGE,"E19.rect.right")]}),-1.0]])],"derivedFrom":subQ0})])],"isStart":false});}
            var Q72;
            Q72=makeQuery(id+"F1.opExtrude","CAP_EDGE",EDGE,{"disambiguationData":[OSD([sQuery(id+"F0.wireOp",EDGE,"E24.right")])],"isStart":false});
            var Q73;
            {var subQ0=sQuery(id+"F0.wireOp",EDGE,"E19.rect.right");var subQ1=sQuery(id+"F0.wireOp",EDGE,"E17.rect.top");Q73=makeQuery(id+"F3.opFillet","BLEND_EDGE",EDGE,{"blendedFrom":[makeQuery(id+"F1.opExtrude","SWEPT_EDGE",EDGE,{"disambiguationData":[OSD([subQ1,subQ0])]}),makeQuery(id+"F1.opExtrude","CAP_FACE",FACE,{"disambiguationData":[OSD([sQuery(id+"F0.wireOp",EDGE,"E0"),sQuery(id+"F0.wireOp",EDGE,"E1"),sQuery(id+"F0.wireOp",EDGE,"E2"),sQuery(id+"F0.wireOp",EDGE,"E3"),sQuery(id+"F0.wireOp",EDGE,"E4"),sQuery(id+"F0.wireOp",EDGE,"E5"),sQuery(id+"F0.wireOp",EDGE,"E6"),sQuery(id+"F0.wireOp",EDGE,"E7"),sQuery(id+"F0.wireOp",EDGE,"E8"),sQuery(id+"F0.wireOp",EDGE,"E9"),sQuery(id+"F0.wireOp",EDGE,"E10"),sQuery(id+"F0.wireOp",EDGE,"E11"),sQuery(id+"F0.wireOp",EDGE,"E12"),sQuery(id+"F0.wireOp",EDGE,"E13"),sQuery(id+"F0.wireOp",EDGE,"E14"),sQuery(id+"F0.wireOp",EDGE,"E15"),sQuery(id+"F0.wireOp",EDGE,"E17.rect.bottom"),subQ1,sQuery(id+"F0.wireOp",EDGE,"E17.rect.left"),sQuery(id+"F0.wireOp",EDGE,"E17.rect.right"),sQuery(id+"F0.wireOp",EDGE,"E18.rect.bottom"),sQuery(id+"F0.wireOp",EDGE,"E18.rect.top"),sQuery(id+"F0.wireOp",EDGE,"E18.rect.left"),sQuery(id+"F0.wireOp",EDGE,"E18.rect.right"),sQuery(id+"F0.wireOp",EDGE,"E19.rect.left"),subQ0,sQuery(id+"F0.wireOp",EDGE,"E20.rect.bottom"),sQuery(id+"F0.wireOp",EDGE,"E20.rect.top"),sQuery(id+"F0.wireOp",EDGE,"E23.top"),sQuery(id+"F0.wireOp",EDGE,"E23.left"),sQuery(id+"F0.wireOp",EDGE,"E23.right"),sQuery(id+"F0.wireOp",EDGE,"E24.top"),sQuery(id+"F0.wireOp",EDGE,"E24.left"),sQuery(id+"F0.wireOp",EDGE,"E24.right"),sQuery(id+"F0.wireOp",EDGE,"E25.top"),sQuery(id+"F0.wireOp",EDGE,"E25.left"),sQuery(id+"F0.wireOp",EDGE,"E25.right"),sQuery(id+"F0.wireOp",EDGE,"E26.top"),sQuery(id+"F0.wireOp",EDGE,"E26.left"),sQuery(id+"F0.wireOp",EDGE,"E26.right")])],"isStart":false})],"blendedInto":[makeQuery(id+"F1.opExtrude","CAP_FACE",FACE,{"disambiguationData":[OSD([sQuery(id+"F0.wireOp",EDGE,"E0"),sQuery(id+"F0.wireOp",EDGE,"E1"),sQuery(id+"F0.wireOp",EDGE,"E2"),sQuery(id+"F0.wireOp",EDGE,"E3"),sQuery(id+"F0.wireOp",EDGE,"E4"),sQuery(id+"F0.wireOp",EDGE,"E5"),sQuery(id+"F0.wireOp",EDGE,"E6"),sQuery(id+"F0.wireOp",EDGE,"E7"),sQuery(id+"F0.wireOp",EDGE,"E8"),sQuery(id+"F0.wireOp",EDGE,"E9"),sQuery(id+"F0.wireOp",EDGE,"E10"),sQuery(id+"F0.wireOp",EDGE,"E11"),sQuery(id+"F0.wireOp",EDGE,"E12"),sQuery(id+"F0.wireOp",EDGE,"E13"),sQuery(id+"F0.wireOp",EDGE,"E14"),sQuery(id+"F0.wireOp",EDGE,"E15"),sQuery(id+"F0.wireOp",EDGE,"E17.rect.bottom"),subQ1,sQuery(id+"F0.wireOp",EDGE,"E17.rect.left"),sQuery(id+"F0.wireOp",EDGE,"E17.rect.right"),sQuery(id+"F0.wireOp",EDGE,"E18.rect.bottom"),sQuery(id+"F0.wireOp",EDGE,"E18.rect.top"),sQuery(id+"F0.wireOp",EDGE,"E18.rect.left"),sQuery(id+"F0.wireOp",EDGE,"E18.rect.right"),sQuery(id+"F0.wireOp",EDGE,"E19.rect.left"),subQ0,sQuery(id+"F0.wireOp",EDGE,"E20.rect.bottom"),sQuery(id+"F0.wireOp",EDGE,"E20.rect.top"),sQuery(id+"F0.wireOp",EDGE,"E23.top"),sQuery(id+"F0.wireOp",EDGE,"E23.left"),sQuery(id+"F0.wireOp",EDGE,"E23.right"),sQuery(id+"F0.wireOp",EDGE,"E24.top"),sQuery(id+"F0.wireOp",EDGE,"E24.left"),sQuery(id+"F0.wireOp",EDGE,"E24.right"),sQuery(id+"F0.wireOp",EDGE,"E25.top"),sQuery(id+"F0.wireOp",EDGE,"E25.left"),sQuery(id+"F0.wireOp",EDGE,"E25.right"),sQuery(id+"F0.wireOp",EDGE,"E26.top"),sQuery(id+"F0.wireOp",EDGE,"E26.left"),sQuery(id+"F0.wireOp",EDGE,"E26.right")])],"isStart":false})]});}
            var Q74;
            {var subQ0=sQuery(id+"F0.wireOp",EDGE,"E19.rect.right");Q74=makeQuery(id+"F1.opExtrude","CAP_EDGE",EDGE,{"disambiguationData":[OSD([subQ0]),TDD([makeQuery(id+"F0.imprint","IMPRINT",EDGE,{"disambiguationData":[TD([[makeQuery(id+"F0.imprint","INTERSECT",VERTEX,{"derivedFrom":[sQuery(id+"F0.wireOp",EDGE,"E14"),subQ0]}),1.0]])],"derivedFrom":subQ0})])],"isStart":false});}
            var Q75;
            {var subQ0=sQuery(id+"F0.wireOp",EDGE,"E19.rect.right");var subQ1=sQuery(id+"F0.wireOp",EDGE,"E14");Q75=makeQuery(id+"F3.opFillet","BLEND_EDGE",EDGE,{"blendedFrom":[makeQuery(id+"F1.opExtrude","SWEPT_EDGE",EDGE,{"disambiguationData":[OSD([subQ1,subQ0])]}),makeQuery(id+"F1.opExtrude","CAP_FACE",FACE,{"disambiguationData":[OSD([sQuery(id+"F0.wireOp",EDGE,"E0"),sQuery(id+"F0.wireOp",EDGE,"E1"),sQuery(id+"F0.wireOp",EDGE,"E2"),sQuery(id+"F0.wireOp",EDGE,"E3"),sQuery(id+"F0.wireOp",EDGE,"E4"),sQuery(id+"F0.wireOp",EDGE,"E5"),sQuery(id+"F0.wireOp",EDGE,"E6"),sQuery(id+"F0.wireOp",EDGE,"E7"),sQuery(id+"F0.wireOp",EDGE,"E8"),sQuery(id+"F0.wireOp",EDGE,"E9"),sQuery(id+"F0.wireOp",EDGE,"E10"),sQuery(id+"F0.wireOp",EDGE,"E11"),sQuery(id+"F0.wireOp",EDGE,"E12"),sQuery(id+"F0.wireOp",EDGE,"E13"),subQ1,sQuery(id+"F0.wireOp",EDGE,"E15"),sQuery(id+"F0.wireOp",EDGE,"E17.rect.bottom"),sQuery(id+"F0.wireOp",EDGE,"E17.rect.top"),sQuery(id+"F0.wireOp",EDGE,"E17.rect.left"),sQuery(id+"F0.wireOp",EDGE,"E17.rect.right"),sQuery(id+"F0.wireOp",EDGE,"E18.rect.bottom"),sQuery(id+"F0.wireOp",EDGE,"E18.rect.top"),sQuery(id+"F0.wireOp",EDGE,"E18.rect.left"),sQuery(id+"F0.wireOp",EDGE,"E18.rect.right"),sQuery(id+"F0.wireOp",EDGE,"E19.rect.left"),subQ0,sQuery(id+"F0.wireOp",EDGE,"E20.rect.bottom"),sQuery(id+"F0.wireOp",EDGE,"E20.rect.top"),sQuery(id+"F0.wireOp",EDGE,"E23.top"),sQuery(id+"F0.wireOp",EDGE,"E23.left"),sQuery(id+"F0.wireOp",EDGE,"E23.right"),sQuery(id+"F0.wireOp",EDGE,"E24.top"),sQuery(id+"F0.wireOp",EDGE,"E24.left"),sQuery(id+"F0.wireOp",EDGE,"E24.right"),sQuery(id+"F0.wireOp",EDGE,"E25.top"),sQuery(id+"F0.wireOp",EDGE,"E25.left"),sQuery(id+"F0.wireOp",EDGE,"E25.right"),sQuery(id+"F0.wireOp",EDGE,"E26.top"),sQuery(id+"F0.wireOp",EDGE,"E26.left"),sQuery(id+"F0.wireOp",EDGE,"E26.right")])],"isStart":false})],"blendedInto":[makeQuery(id+"F1.opExtrude","CAP_FACE",FACE,{"disambiguationData":[OSD([sQuery(id+"F0.wireOp",EDGE,"E0"),sQuery(id+"F0.wireOp",EDGE,"E1"),sQuery(id+"F0.wireOp",EDGE,"E2"),sQuery(id+"F0.wireOp",EDGE,"E3"),sQuery(id+"F0.wireOp",EDGE,"E4"),sQuery(id+"F0.wireOp",EDGE,"E5"),sQuery(id+"F0.wireOp",EDGE,"E6"),sQuery(id+"F0.wireOp",EDGE,"E7"),sQuery(id+"F0.wireOp",EDGE,"E8"),sQuery(id+"F0.wireOp",EDGE,"E9"),sQuery(id+"F0.wireOp",EDGE,"E10"),sQuery(id+"F0.wireOp",EDGE,"E11"),sQuery(id+"F0.wireOp",EDGE,"E12"),sQuery(id+"F0.wireOp",EDGE,"E13"),subQ1,sQuery(id+"F0.wireOp",EDGE,"E15"),sQuery(id+"F0.wireOp",EDGE,"E17.rect.bottom"),sQuery(id+"F0.wireOp",EDGE,"E17.rect.top"),sQuery(id+"F0.wireOp",EDGE,"E17.rect.left"),sQuery(id+"F0.wireOp",EDGE,"E17.rect.right"),sQuery(id+"F0.wireOp",EDGE,"E18.rect.bottom"),sQuery(id+"F0.wireOp",EDGE,"E18.rect.top"),sQuery(id+"F0.wireOp",EDGE,"E18.rect.left"),sQuery(id+"F0.wireOp",EDGE,"E18.rect.right"),sQuery(id+"F0.wireOp",EDGE,"E19.rect.left"),subQ0,sQuery(id+"F0.wireOp",EDGE,"E20.rect.bottom"),sQuery(id+"F0.wireOp",EDGE,"E20.rect.top"),sQuery(id+"F0.wireOp",EDGE,"E23.top"),sQuery(id+"F0.wireOp",EDGE,"E23.left"),sQuery(id+"F0.wireOp",EDGE,"E23.right"),sQuery(id+"F0.wireOp",EDGE,"E24.top"),sQuery(id+"F0.wireOp",EDGE,"E24.left"),sQuery(id+"F0.wireOp",EDGE,"E24.right"),sQuery(id+"F0.wireOp",EDGE,"E25.top"),sQuery(id+"F0.wireOp",EDGE,"E25.left"),sQuery(id+"F0.wireOp",EDGE,"E25.right"),sQuery(id+"F0.wireOp",EDGE,"E26.top"),sQuery(id+"F0.wireOp",EDGE,"E26.left"),sQuery(id+"F0.wireOp",EDGE,"E26.right")])],"isStart":false})]});}
            var Q76;
            {var subQ0=sQuery(id+"F0.wireOp",EDGE,"E14");var subQ1=makeQuery(id+"F0.imprint","INTERSECT",VERTEX,{"disambiguationData":[OD(0.0)],"derivedFrom":[sQuery(id+"F0.wireOp",EDGE,"E5"),subQ0]});Q76=makeQuery(id+"F1.opExtrude","CAP_EDGE",EDGE,{"disambiguationData":[OSD([subQ0]),TDD([makeQuery(id+"F0.imprint","IMPRINT",EDGE,{"disambiguationData":[TD([[subQ1,1.0]])],"derivedFrom":subQ0}),makeQuery(id+"F0.imprint","IMPRINT",EDGE,{"disambiguationData":[TD([[makeQuery(id+"F0.imprint","INTERSECT",VERTEX,{"disambiguationData":[OD(1.0)],"derivedFrom":[sQuery(id+"F0.wireOp",EDGE,"E3"),subQ0]}),1.0]])],"derivedFrom":subQ0})])],"isStart":false});}
            var Q77;
            {var subQ0=sQuery(id+"F0.wireOp",EDGE,"E8");var subQ1=makeQuery(id+"F0.imprint","INTERSECT",VERTEX,{"disambiguationData":[OD(0.0)],"derivedFrom":[sQuery(id+"F0.wireOp",EDGE,"E5"),subQ0]});Q77=makeQuery(id+"F1.opExtrude","CAP_EDGE",EDGE,{"disambiguationData":[OSD([subQ0]),TDD([makeQuery(id+"F0.imprint","IMPRINT",EDGE,{"disambiguationData":[TD([[makeQuery(id+"F0.imprint","INTERSECT",VERTEX,{"disambiguationData":[OD(1.0)],"derivedFrom":[sQuery(id+"F0.wireOp",EDGE,"E3"),subQ0]}),-1.0]])],"derivedFrom":subQ0}),makeQuery(id+"F0.imprint","IMPRINT",EDGE,{"disambiguationData":[TD([[subQ1,-1.0]])],"derivedFrom":subQ0})])],"isStart":false});}
            var Q78;
            {var subQ0=sQuery(id+"F0.wireOp",EDGE,"E20.rect.top");var subQ1=sQuery(id+"F0.wireOp",EDGE,"E8");Q78=makeQuery(id+"F3.opFillet","BLEND_EDGE",EDGE,{"blendedFrom":[makeQuery(id+"F1.opExtrude","SWEPT_EDGE",EDGE,{"disambiguationData":[OSD([subQ1,subQ0])]}),makeQuery(id+"F1.opExtrude","CAP_FACE",FACE,{"disambiguationData":[OSD([sQuery(id+"F0.wireOp",EDGE,"E0"),sQuery(id+"F0.wireOp",EDGE,"E1"),sQuery(id+"F0.wireOp",EDGE,"E2"),sQuery(id+"F0.wireOp",EDGE,"E3"),sQuery(id+"F0.wireOp",EDGE,"E4"),sQuery(id+"F0.wireOp",EDGE,"E5"),sQuery(id+"F0.wireOp",EDGE,"E6"),sQuery(id+"F0.wireOp",EDGE,"E7"),subQ1,sQuery(id+"F0.wireOp",EDGE,"E9"),sQuery(id+"F0.wireOp",EDGE,"E10"),sQuery(id+"F0.wireOp",EDGE,"E11"),sQuery(id+"F0.wireOp",EDGE,"E12"),sQuery(id+"F0.wireOp",EDGE,"E13"),sQuery(id+"F0.wireOp",EDGE,"E14"),sQuery(id+"F0.wireOp",EDGE,"E15"),sQuery(id+"F0.wireOp",EDGE,"E17.rect.bottom"),sQuery(id+"F0.wireOp",EDGE,"E17.rect.top"),sQuery(id+"F0.wireOp",EDGE,"E17.rect.left"),sQuery(id+"F0.wireOp",EDGE,"E17.rect.right"),sQuery(id+"F0.wireOp",EDGE,"E18.rect.bottom"),sQuery(id+"F0.wireOp",EDGE,"E18.rect.top"),sQuery(id+"F0.wireOp",EDGE,"E18.rect.left"),sQuery(id+"F0.wireOp",EDGE,"E18.rect.right"),sQuery(id+"F0.wireOp",EDGE,"E19.rect.left"),sQuery(id+"F0.wireOp",EDGE,"E19.rect.right"),sQuery(id+"F0.wireOp",EDGE,"E20.rect.bottom"),subQ0,sQuery(id+"F0.wireOp",EDGE,"E23.top"),sQuery(id+"F0.wireOp",EDGE,"E23.left"),sQuery(id+"F0.wireOp",EDGE,"E23.right"),sQuery(id+"F0.wireOp",EDGE,"E24.top"),sQuery(id+"F0.wireOp",EDGE,"E24.left"),sQuery(id+"F0.wireOp",EDGE,"E24.right"),sQuery(id+"F0.wireOp",EDGE,"E25.top"),sQuery(id+"F0.wireOp",EDGE,"E25.left"),sQuery(id+"F0.wireOp",EDGE,"E25.right"),sQuery(id+"F0.wireOp",EDGE,"E26.top"),sQuery(id+"F0.wireOp",EDGE,"E26.left"),sQuery(id+"F0.wireOp",EDGE,"E26.right")])],"isStart":false})],"blendedInto":[makeQuery(id+"F1.opExtrude","CAP_FACE",FACE,{"disambiguationData":[OSD([sQuery(id+"F0.wireOp",EDGE,"E0"),sQuery(id+"F0.wireOp",EDGE,"E1"),sQuery(id+"F0.wireOp",EDGE,"E2"),sQuery(id+"F0.wireOp",EDGE,"E3"),sQuery(id+"F0.wireOp",EDGE,"E4"),sQuery(id+"F0.wireOp",EDGE,"E5"),sQuery(id+"F0.wireOp",EDGE,"E6"),sQuery(id+"F0.wireOp",EDGE,"E7"),subQ1,sQuery(id+"F0.wireOp",EDGE,"E9"),sQuery(id+"F0.wireOp",EDGE,"E10"),sQuery(id+"F0.wireOp",EDGE,"E11"),sQuery(id+"F0.wireOp",EDGE,"E12"),sQuery(id+"F0.wireOp",EDGE,"E13"),sQuery(id+"F0.wireOp",EDGE,"E14"),sQuery(id+"F0.wireOp",EDGE,"E15"),sQuery(id+"F0.wireOp",EDGE,"E17.rect.bottom"),sQuery(id+"F0.wireOp",EDGE,"E17.rect.top"),sQuery(id+"F0.wireOp",EDGE,"E17.rect.left"),sQuery(id+"F0.wireOp",EDGE,"E17.rect.right"),sQuery(id+"F0.wireOp",EDGE,"E18.rect.bottom"),sQuery(id+"F0.wireOp",EDGE,"E18.rect.top"),sQuery(id+"F0.wireOp",EDGE,"E18.rect.left"),sQuery(id+"F0.wireOp",EDGE,"E18.rect.right"),sQuery(id+"F0.wireOp",EDGE,"E19.rect.left"),sQuery(id+"F0.wireOp",EDGE,"E19.rect.right"),sQuery(id+"F0.wireOp",EDGE,"E20.rect.bottom"),subQ0,sQuery(id+"F0.wireOp",EDGE,"E23.top"),sQuery(id+"F0.wireOp",EDGE,"E23.left"),sQuery(id+"F0.wireOp",EDGE,"E23.right"),sQuery(id+"F0.wireOp",EDGE,"E24.top"),sQuery(id+"F0.wireOp",EDGE,"E24.left"),sQuery(id+"F0.wireOp",EDGE,"E24.right"),sQuery(id+"F0.wireOp",EDGE,"E25.top"),sQuery(id+"F0.wireOp",EDGE,"E25.left"),sQuery(id+"F0.wireOp",EDGE,"E25.right"),sQuery(id+"F0.wireOp",EDGE,"E26.top"),sQuery(id+"F0.wireOp",EDGE,"E26.left"),sQuery(id+"F0.wireOp",EDGE,"E26.right")])],"isStart":false})]});}
            var Q79;
            {var subQ0=sQuery(id+"F0.wireOp",EDGE,"E20.rect.top");Q79=makeQuery(id+"F1.opExtrude","CAP_EDGE",EDGE,{"disambiguationData":[OSD([subQ0]),TDD([makeQuery(id+"F0.imprint","IMPRINT",EDGE,{"disambiguationData":[TD([[makeQuery(id+"F0.imprint","INTERSECT",VERTEX,{"derivedFrom":[sQuery(id+"F0.wireOp",EDGE,"E8"),subQ0]}),1.0]])],"derivedFrom":subQ0})])],"isStart":false});}
            var Q80;
            {var subQ0=sQuery(id+"F0.wireOp",EDGE,"E20.rect.top");var subQ1=sQuery(id+"F0.wireOp",EDGE,"E17.rect.right");Q80=makeQuery(id+"F3.opFillet","BLEND_EDGE",EDGE,{"blendedFrom":[makeQuery(id+"F1.opExtrude","SWEPT_EDGE",EDGE,{"disambiguationData":[OSD([subQ1,subQ0])]}),makeQuery(id+"F1.opExtrude","CAP_FACE",FACE,{"disambiguationData":[OSD([sQuery(id+"F0.wireOp",EDGE,"E0"),sQuery(id+"F0.wireOp",EDGE,"E1"),sQuery(id+"F0.wireOp",EDGE,"E2"),sQuery(id+"F0.wireOp",EDGE,"E3"),sQuery(id+"F0.wireOp",EDGE,"E4"),sQuery(id+"F0.wireOp",EDGE,"E5"),sQuery(id+"F0.wireOp",EDGE,"E6"),sQuery(id+"F0.wireOp",EDGE,"E7"),sQuery(id+"F0.wireOp",EDGE,"E8"),sQuery(id+"F0.wireOp",EDGE,"E9"),sQuery(id+"F0.wireOp",EDGE,"E10"),sQuery(id+"F0.wireOp",EDGE,"E11"),sQuery(id+"F0.wireOp",EDGE,"E12"),sQuery(id+"F0.wireOp",EDGE,"E13"),sQuery(id+"F0.wireOp",EDGE,"E14"),sQuery(id+"F0.wireOp",EDGE,"E15"),sQuery(id+"F0.wireOp",EDGE,"E17.rect.bottom"),sQuery(id+"F0.wireOp",EDGE,"E17.rect.top"),sQuery(id+"F0.wireOp",EDGE,"E17.rect.left"),subQ1,sQuery(id+"F0.wireOp",EDGE,"E18.rect.bottom"),sQuery(id+"F0.wireOp",EDGE,"E18.rect.top"),sQuery(id+"F0.wireOp",EDGE,"E18.rect.left"),sQuery(id+"F0.wireOp",EDGE,"E18.rect.right"),sQuery(id+"F0.wireOp",EDGE,"E19.rect.left"),sQuery(id+"F0.wireOp",EDGE,"E19.rect.right"),sQuery(id+"F0.wireOp",EDGE,"E20.rect.bottom"),subQ0,sQuery(id+"F0.wireOp",EDGE,"E23.top"),sQuery(id+"F0.wireOp",EDGE,"E23.left"),sQuery(id+"F0.wireOp",EDGE,"E23.right"),sQuery(id+"F0.wireOp",EDGE,"E24.top"),sQuery(id+"F0.wireOp",EDGE,"E24.left"),sQuery(id+"F0.wireOp",EDGE,"E24.right"),sQuery(id+"F0.wireOp",EDGE,"E25.top"),sQuery(id+"F0.wireOp",EDGE,"E25.left"),sQuery(id+"F0.wireOp",EDGE,"E25.right"),sQuery(id+"F0.wireOp",EDGE,"E26.top"),sQuery(id+"F0.wireOp",EDGE,"E26.left"),sQuery(id+"F0.wireOp",EDGE,"E26.right")])],"isStart":false})],"blendedInto":[makeQuery(id+"F1.opExtrude","CAP_FACE",FACE,{"disambiguationData":[OSD([sQuery(id+"F0.wireOp",EDGE,"E0"),sQuery(id+"F0.wireOp",EDGE,"E1"),sQuery(id+"F0.wireOp",EDGE,"E2"),sQuery(id+"F0.wireOp",EDGE,"E3"),sQuery(id+"F0.wireOp",EDGE,"E4"),sQuery(id+"F0.wireOp",EDGE,"E5"),sQuery(id+"F0.wireOp",EDGE,"E6"),sQuery(id+"F0.wireOp",EDGE,"E7"),sQuery(id+"F0.wireOp",EDGE,"E8"),sQuery(id+"F0.wireOp",EDGE,"E9"),sQuery(id+"F0.wireOp",EDGE,"E10"),sQuery(id+"F0.wireOp",EDGE,"E11"),sQuery(id+"F0.wireOp",EDGE,"E12"),sQuery(id+"F0.wireOp",EDGE,"E13"),sQuery(id+"F0.wireOp",EDGE,"E14"),sQuery(id+"F0.wireOp",EDGE,"E15"),sQuery(id+"F0.wireOp",EDGE,"E17.rect.bottom"),sQuery(id+"F0.wireOp",EDGE,"E17.rect.top"),sQuery(id+"F0.wireOp",EDGE,"E17.rect.left"),subQ1,sQuery(id+"F0.wireOp",EDGE,"E18.rect.bottom"),sQuery(id+"F0.wireOp",EDGE,"E18.rect.top"),sQuery(id+"F0.wireOp",EDGE,"E18.rect.left"),sQuery(id+"F0.wireOp",EDGE,"E18.rect.right"),sQuery(id+"F0.wireOp",EDGE,"E19.rect.left"),sQuery(id+"F0.wireOp",EDGE,"E19.rect.right"),sQuery(id+"F0.wireOp",EDGE,"E20.rect.bottom"),subQ0,sQuery(id+"F0.wireOp",EDGE,"E23.top"),sQuery(id+"F0.wireOp",EDGE,"E23.left"),sQuery(id+"F0.wireOp",EDGE,"E23.right"),sQuery(id+"F0.wireOp",EDGE,"E24.top"),sQuery(id+"F0.wireOp",EDGE,"E24.left"),sQuery(id+"F0.wireOp",EDGE,"E24.right"),sQuery(id+"F0.wireOp",EDGE,"E25.top"),sQuery(id+"F0.wireOp",EDGE,"E25.left"),sQuery(id+"F0.wireOp",EDGE,"E25.right"),sQuery(id+"F0.wireOp",EDGE,"E26.top"),sQuery(id+"F0.wireOp",EDGE,"E26.left"),sQuery(id+"F0.wireOp",EDGE,"E26.right")])],"isStart":false})]});}
            var Q81;
            Q81=makeQuery(id+"F1.opExtrude","CAP_EDGE",EDGE,{"disambiguationData":[OSD([sQuery(id+"F0.wireOp",EDGE,"E17.rect.right"),sQuery(id+"F0.wireOp",EDGE,"E24.left")])],"isStart":false});
            var Q82;
            Q82=makeQuery(id+"F1.opExtrude","CAP_EDGE",EDGE,{"disambiguationData":[OSD([sQuery(id+"F0.wireOp",EDGE,"E17.rect.left"),sQuery(id+"F0.wireOp",EDGE,"E26.left")])],"isStart":false});
            var Q83;
            {var subQ0=sQuery(id+"F0.wireOp",EDGE,"E20.rect.bottom");var subQ1=sQuery(id+"F0.wireOp",EDGE,"E17.rect.left");Q83=makeQuery(id+"F3.opFillet","BLEND_EDGE",EDGE,{"blendedFrom":[makeQuery(id+"F1.opExtrude","SWEPT_EDGE",EDGE,{"disambiguationData":[OSD([subQ1,subQ0])]}),makeQuery(id+"F1.opExtrude","CAP_FACE",FACE,{"disambiguationData":[OSD([sQuery(id+"F0.wireOp",EDGE,"E0"),sQuery(id+"F0.wireOp",EDGE,"E1"),sQuery(id+"F0.wireOp",EDGE,"E2"),sQuery(id+"F0.wireOp",EDGE,"E3"),sQuery(id+"F0.wireOp",EDGE,"E4"),sQuery(id+"F0.wireOp",EDGE,"E5"),sQuery(id+"F0.wireOp",EDGE,"E6"),sQuery(id+"F0.wireOp",EDGE,"E7"),sQuery(id+"F0.wireOp",EDGE,"E8"),sQuery(id+"F0.wireOp",EDGE,"E9"),sQuery(id+"F0.wireOp",EDGE,"E10"),sQuery(id+"F0.wireOp",EDGE,"E11"),sQuery(id+"F0.wireOp",EDGE,"E12"),sQuery(id+"F0.wireOp",EDGE,"E13"),sQuery(id+"F0.wireOp",EDGE,"E14"),sQuery(id+"F0.wireOp",EDGE,"E15"),sQuery(id+"F0.wireOp",EDGE,"E17.rect.bottom"),sQuery(id+"F0.wireOp",EDGE,"E17.rect.top"),subQ1,sQuery(id+"F0.wireOp",EDGE,"E17.rect.right"),sQuery(id+"F0.wireOp",EDGE,"E18.rect.bottom"),sQuery(id+"F0.wireOp",EDGE,"E18.rect.top"),sQuery(id+"F0.wireOp",EDGE,"E18.rect.left"),sQuery(id+"F0.wireOp",EDGE,"E18.rect.right"),sQuery(id+"F0.wireOp",EDGE,"E19.rect.left"),sQuery(id+"F0.wireOp",EDGE,"E19.rect.right"),subQ0,sQuery(id+"F0.wireOp",EDGE,"E20.rect.top"),sQuery(id+"F0.wireOp",EDGE,"E23.top"),sQuery(id+"F0.wireOp",EDGE,"E23.left"),sQuery(id+"F0.wireOp",EDGE,"E23.right"),sQuery(id+"F0.wireOp",EDGE,"E24.top"),sQuery(id+"F0.wireOp",EDGE,"E24.left"),sQuery(id+"F0.wireOp",EDGE,"E24.right"),sQuery(id+"F0.wireOp",EDGE,"E25.top"),sQuery(id+"F0.wireOp",EDGE,"E25.left"),sQuery(id+"F0.wireOp",EDGE,"E25.right"),sQuery(id+"F0.wireOp",EDGE,"E26.top"),sQuery(id+"F0.wireOp",EDGE,"E26.left"),sQuery(id+"F0.wireOp",EDGE,"E26.right")])],"isStart":false})],"blendedInto":[makeQuery(id+"F1.opExtrude","CAP_FACE",FACE,{"disambiguationData":[OSD([sQuery(id+"F0.wireOp",EDGE,"E0"),sQuery(id+"F0.wireOp",EDGE,"E1"),sQuery(id+"F0.wireOp",EDGE,"E2"),sQuery(id+"F0.wireOp",EDGE,"E3"),sQuery(id+"F0.wireOp",EDGE,"E4"),sQuery(id+"F0.wireOp",EDGE,"E5"),sQuery(id+"F0.wireOp",EDGE,"E6"),sQuery(id+"F0.wireOp",EDGE,"E7"),sQuery(id+"F0.wireOp",EDGE,"E8"),sQuery(id+"F0.wireOp",EDGE,"E9"),sQuery(id+"F0.wireOp",EDGE,"E10"),sQuery(id+"F0.wireOp",EDGE,"E11"),sQuery(id+"F0.wireOp",EDGE,"E12"),sQuery(id+"F0.wireOp",EDGE,"E13"),sQuery(id+"F0.wireOp",EDGE,"E14"),sQuery(id+"F0.wireOp",EDGE,"E15"),sQuery(id+"F0.wireOp",EDGE,"E17.rect.bottom"),sQuery(id+"F0.wireOp",EDGE,"E17.rect.top"),subQ1,sQuery(id+"F0.wireOp",EDGE,"E17.rect.right"),sQuery(id+"F0.wireOp",EDGE,"E18.rect.bottom"),sQuery(id+"F0.wireOp",EDGE,"E18.rect.top"),sQuery(id+"F0.wireOp",EDGE,"E18.rect.left"),sQuery(id+"F0.wireOp",EDGE,"E18.rect.right"),sQuery(id+"F0.wireOp",EDGE,"E19.rect.left"),sQuery(id+"F0.wireOp",EDGE,"E19.rect.right"),subQ0,sQuery(id+"F0.wireOp",EDGE,"E20.rect.top"),sQuery(id+"F0.wireOp",EDGE,"E23.top"),sQuery(id+"F0.wireOp",EDGE,"E23.left"),sQuery(id+"F0.wireOp",EDGE,"E23.right"),sQuery(id+"F0.wireOp",EDGE,"E24.top"),sQuery(id+"F0.wireOp",EDGE,"E24.left"),sQuery(id+"F0.wireOp",EDGE,"E24.right"),sQuery(id+"F0.wireOp",EDGE,"E25.top"),sQuery(id+"F0.wireOp",EDGE,"E25.left"),sQuery(id+"F0.wireOp",EDGE,"E25.right"),sQuery(id+"F0.wireOp",EDGE,"E26.top"),sQuery(id+"F0.wireOp",EDGE,"E26.left"),sQuery(id+"F0.wireOp",EDGE,"E26.right")])],"isStart":false})]});}
            var Q84;
            {var subQ0=sQuery(id+"F0.wireOp",EDGE,"E20.rect.bottom");Q84=makeQuery(id+"F1.opExtrude","CAP_EDGE",EDGE,{"disambiguationData":[OSD([subQ0]),TDD([makeQuery(id+"F0.imprint","IMPRINT",EDGE,{"disambiguationData":[TD([[makeQuery(id+"F0.imprint","INTERSECT",VERTEX,{"derivedFrom":[sQuery(id+"F0.wireOp",EDGE,"E12"),subQ0]}),-1.0]])],"derivedFrom":subQ0})])],"isStart":false});}
            var Q85;
            {var subQ0=sQuery(id+"F0.wireOp",EDGE,"E20.rect.bottom");var subQ1=sQuery(id+"F0.wireOp",EDGE,"E12");Q85=makeQuery(id+"F3.opFillet","BLEND_EDGE",EDGE,{"blendedFrom":[makeQuery(id+"F1.opExtrude","SWEPT_EDGE",EDGE,{"disambiguationData":[OSD([subQ1,subQ0])]}),makeQuery(id+"F1.opExtrude","CAP_FACE",FACE,{"disambiguationData":[OSD([sQuery(id+"F0.wireOp",EDGE,"E0"),sQuery(id+"F0.wireOp",EDGE,"E1"),sQuery(id+"F0.wireOp",EDGE,"E2"),sQuery(id+"F0.wireOp",EDGE,"E3"),sQuery(id+"F0.wireOp",EDGE,"E4"),sQuery(id+"F0.wireOp",EDGE,"E5"),sQuery(id+"F0.wireOp",EDGE,"E6"),sQuery(id+"F0.wireOp",EDGE,"E7"),sQuery(id+"F0.wireOp",EDGE,"E8"),sQuery(id+"F0.wireOp",EDGE,"E9"),sQuery(id+"F0.wireOp",EDGE,"E10"),sQuery(id+"F0.wireOp",EDGE,"E11"),subQ1,sQuery(id+"F0.wireOp",EDGE,"E13"),sQuery(id+"F0.wireOp",EDGE,"E14"),sQuery(id+"F0.wireOp",EDGE,"E15"),sQuery(id+"F0.wireOp",EDGE,"E17.rect.bottom"),sQuery(id+"F0.wireOp",EDGE,"E17.rect.top"),sQuery(id+"F0.wireOp",EDGE,"E17.rect.left"),sQuery(id+"F0.wireOp",EDGE,"E17.rect.right"),sQuery(id+"F0.wireOp",EDGE,"E18.rect.bottom"),sQuery(id+"F0.wireOp",EDGE,"E18.rect.top"),sQuery(id+"F0.wireOp",EDGE,"E18.rect.left"),sQuery(id+"F0.wireOp",EDGE,"E18.rect.right"),sQuery(id+"F0.wireOp",EDGE,"E19.rect.left"),sQuery(id+"F0.wireOp",EDGE,"E19.rect.right"),subQ0,sQuery(id+"F0.wireOp",EDGE,"E20.rect.top"),sQuery(id+"F0.wireOp",EDGE,"E23.top"),sQuery(id+"F0.wireOp",EDGE,"E23.left"),sQuery(id+"F0.wireOp",EDGE,"E23.right"),sQuery(id+"F0.wireOp",EDGE,"E24.top"),sQuery(id+"F0.wireOp",EDGE,"E24.left"),sQuery(id+"F0.wireOp",EDGE,"E24.right"),sQuery(id+"F0.wireOp",EDGE,"E25.top"),sQuery(id+"F0.wireOp",EDGE,"E25.left"),sQuery(id+"F0.wireOp",EDGE,"E25.right"),sQuery(id+"F0.wireOp",EDGE,"E26.top"),sQuery(id+"F0.wireOp",EDGE,"E26.left"),sQuery(id+"F0.wireOp",EDGE,"E26.right")])],"isStart":false})],"blendedInto":[makeQuery(id+"F1.opExtrude","CAP_FACE",FACE,{"disambiguationData":[OSD([sQuery(id+"F0.wireOp",EDGE,"E0"),sQuery(id+"F0.wireOp",EDGE,"E1"),sQuery(id+"F0.wireOp",EDGE,"E2"),sQuery(id+"F0.wireOp",EDGE,"E3"),sQuery(id+"F0.wireOp",EDGE,"E4"),sQuery(id+"F0.wireOp",EDGE,"E5"),sQuery(id+"F0.wireOp",EDGE,"E6"),sQuery(id+"F0.wireOp",EDGE,"E7"),sQuery(id+"F0.wireOp",EDGE,"E8"),sQuery(id+"F0.wireOp",EDGE,"E9"),sQuery(id+"F0.wireOp",EDGE,"E10"),sQuery(id+"F0.wireOp",EDGE,"E11"),subQ1,sQuery(id+"F0.wireOp",EDGE,"E13"),sQuery(id+"F0.wireOp",EDGE,"E14"),sQuery(id+"F0.wireOp",EDGE,"E15"),sQuery(id+"F0.wireOp",EDGE,"E17.rect.bottom"),sQuery(id+"F0.wireOp",EDGE,"E17.rect.top"),sQuery(id+"F0.wireOp",EDGE,"E17.rect.left"),sQuery(id+"F0.wireOp",EDGE,"E17.rect.right"),sQuery(id+"F0.wireOp",EDGE,"E18.rect.bottom"),sQuery(id+"F0.wireOp",EDGE,"E18.rect.top"),sQuery(id+"F0.wireOp",EDGE,"E18.rect.left"),sQuery(id+"F0.wireOp",EDGE,"E18.rect.right"),sQuery(id+"F0.wireOp",EDGE,"E19.rect.left"),sQuery(id+"F0.wireOp",EDGE,"E19.rect.right"),subQ0,sQuery(id+"F0.wireOp",EDGE,"E20.rect.top"),sQuery(id+"F0.wireOp",EDGE,"E23.top"),sQuery(id+"F0.wireOp",EDGE,"E23.left"),sQuery(id+"F0.wireOp",EDGE,"E23.right"),sQuery(id+"F0.wireOp",EDGE,"E24.top"),sQuery(id+"F0.wireOp",EDGE,"E24.left"),sQuery(id+"F0.wireOp",EDGE,"E24.right"),sQuery(id+"F0.wireOp",EDGE,"E25.top"),sQuery(id+"F0.wireOp",EDGE,"E25.left"),sQuery(id+"F0.wireOp",EDGE,"E25.right"),sQuery(id+"F0.wireOp",EDGE,"E26.top"),sQuery(id+"F0.wireOp",EDGE,"E26.left"),sQuery(id+"F0.wireOp",EDGE,"E26.right")])],"isStart":false})]});}
            var Q86;
            {var subQ0=sQuery(id+"F0.wireOp",EDGE,"E12");var subQ1=makeQuery(id+"F0.imprint","INTERSECT",VERTEX,{"disambiguationData":[OD(1.0)],"derivedFrom":[sQuery(id+"F0.wireOp",EDGE,"E7"),subQ0]});Q86=makeQuery(id+"F1.opExtrude","CAP_EDGE",EDGE,{"disambiguationData":[OSD([subQ0]),TDD([makeQuery(id+"F0.imprint","IMPRINT",EDGE,{"disambiguationData":[TD([[makeQuery(id+"F0.imprint","INTERSECT",VERTEX,{"disambiguationData":[OD(1.0)],"derivedFrom":[sQuery(id+"F0.wireOp",EDGE,"E1"),subQ0]}),-1.0]])],"derivedFrom":subQ0}),makeQuery(id+"F0.imprint","IMPRINT",EDGE,{"disambiguationData":[TD([[subQ1,-1.0]])],"derivedFrom":subQ0})])],"isStart":false});}
            var Q87;
            {var subQ0=sQuery(id+"F0.wireOp",EDGE,"E10");var subQ1=makeQuery(id+"F0.imprint","INTERSECT",VERTEX,{"disambiguationData":[OD(1.0)],"derivedFrom":[sQuery(id+"F0.wireOp",EDGE,"E7"),subQ0]});Q87=makeQuery(id+"F1.opExtrude","CAP_EDGE",EDGE,{"disambiguationData":[OSD([subQ0]),TDD([makeQuery(id+"F0.imprint","IMPRINT",EDGE,{"disambiguationData":[TD([[subQ1,1.0]])],"derivedFrom":subQ0}),makeQuery(id+"F0.imprint","IMPRINT",EDGE,{"disambiguationData":[TD([[makeQuery(id+"F0.imprint","INTERSECT",VERTEX,{"disambiguationData":[OD(1.0)],"derivedFrom":[sQuery(id+"F0.wireOp",EDGE,"E1"),subQ0]}),1.0]])],"derivedFrom":subQ0})])],"isStart":false});}
            var Q88;
            {var subQ0=sQuery(id+"F0.wireOp",EDGE,"E19.rect.left");var subQ1=sQuery(id+"F0.wireOp",EDGE,"E10");Q88=makeQuery(id+"F3.opFillet","BLEND_EDGE",EDGE,{"blendedFrom":[makeQuery(id+"F1.opExtrude","SWEPT_EDGE",EDGE,{"disambiguationData":[OSD([subQ1,subQ0])]}),makeQuery(id+"F1.opExtrude","CAP_FACE",FACE,{"disambiguationData":[OSD([sQuery(id+"F0.wireOp",EDGE,"E0"),sQuery(id+"F0.wireOp",EDGE,"E1"),sQuery(id+"F0.wireOp",EDGE,"E2"),sQuery(id+"F0.wireOp",EDGE,"E3"),sQuery(id+"F0.wireOp",EDGE,"E4"),sQuery(id+"F0.wireOp",EDGE,"E5"),sQuery(id+"F0.wireOp",EDGE,"E6"),sQuery(id+"F0.wireOp",EDGE,"E7"),sQuery(id+"F0.wireOp",EDGE,"E8"),sQuery(id+"F0.wireOp",EDGE,"E9"),subQ1,sQuery(id+"F0.wireOp",EDGE,"E11"),sQuery(id+"F0.wireOp",EDGE,"E12"),sQuery(id+"F0.wireOp",EDGE,"E13"),sQuery(id+"F0.wireOp",EDGE,"E14"),sQuery(id+"F0.wireOp",EDGE,"E15"),sQuery(id+"F0.wireOp",EDGE,"E17.rect.bottom"),sQuery(id+"F0.wireOp",EDGE,"E17.rect.top"),sQuery(id+"F0.wireOp",EDGE,"E17.rect.left"),sQuery(id+"F0.wireOp",EDGE,"E17.rect.right"),sQuery(id+"F0.wireOp",EDGE,"E18.rect.bottom"),sQuery(id+"F0.wireOp",EDGE,"E18.rect.top"),sQuery(id+"F0.wireOp",EDGE,"E18.rect.left"),sQuery(id+"F0.wireOp",EDGE,"E18.rect.right"),subQ0,sQuery(id+"F0.wireOp",EDGE,"E19.rect.right"),sQuery(id+"F0.wireOp",EDGE,"E20.rect.bottom"),sQuery(id+"F0.wireOp",EDGE,"E20.rect.top"),sQuery(id+"F0.wireOp",EDGE,"E23.top"),sQuery(id+"F0.wireOp",EDGE,"E23.left"),sQuery(id+"F0.wireOp",EDGE,"E23.right"),sQuery(id+"F0.wireOp",EDGE,"E24.top"),sQuery(id+"F0.wireOp",EDGE,"E24.left"),sQuery(id+"F0.wireOp",EDGE,"E24.right"),sQuery(id+"F0.wireOp",EDGE,"E25.top"),sQuery(id+"F0.wireOp",EDGE,"E25.left"),sQuery(id+"F0.wireOp",EDGE,"E25.right"),sQuery(id+"F0.wireOp",EDGE,"E26.top"),sQuery(id+"F0.wireOp",EDGE,"E26.left"),sQuery(id+"F0.wireOp",EDGE,"E26.right")])],"isStart":false})],"blendedInto":[makeQuery(id+"F1.opExtrude","CAP_FACE",FACE,{"disambiguationData":[OSD([sQuery(id+"F0.wireOp",EDGE,"E0"),sQuery(id+"F0.wireOp",EDGE,"E1"),sQuery(id+"F0.wireOp",EDGE,"E2"),sQuery(id+"F0.wireOp",EDGE,"E3"),sQuery(id+"F0.wireOp",EDGE,"E4"),sQuery(id+"F0.wireOp",EDGE,"E5"),sQuery(id+"F0.wireOp",EDGE,"E6"),sQuery(id+"F0.wireOp",EDGE,"E7"),sQuery(id+"F0.wireOp",EDGE,"E8"),sQuery(id+"F0.wireOp",EDGE,"E9"),subQ1,sQuery(id+"F0.wireOp",EDGE,"E11"),sQuery(id+"F0.wireOp",EDGE,"E12"),sQuery(id+"F0.wireOp",EDGE,"E13"),sQuery(id+"F0.wireOp",EDGE,"E14"),sQuery(id+"F0.wireOp",EDGE,"E15"),sQuery(id+"F0.wireOp",EDGE,"E17.rect.bottom"),sQuery(id+"F0.wireOp",EDGE,"E17.rect.top"),sQuery(id+"F0.wireOp",EDGE,"E17.rect.left"),sQuery(id+"F0.wireOp",EDGE,"E17.rect.right"),sQuery(id+"F0.wireOp",EDGE,"E18.rect.bottom"),sQuery(id+"F0.wireOp",EDGE,"E18.rect.top"),sQuery(id+"F0.wireOp",EDGE,"E18.rect.left"),sQuery(id+"F0.wireOp",EDGE,"E18.rect.right"),subQ0,sQuery(id+"F0.wireOp",EDGE,"E19.rect.right"),sQuery(id+"F0.wireOp",EDGE,"E20.rect.bottom"),sQuery(id+"F0.wireOp",EDGE,"E20.rect.top"),sQuery(id+"F0.wireOp",EDGE,"E23.top"),sQuery(id+"F0.wireOp",EDGE,"E23.left"),sQuery(id+"F0.wireOp",EDGE,"E23.right"),sQuery(id+"F0.wireOp",EDGE,"E24.top"),sQuery(id+"F0.wireOp",EDGE,"E24.left"),sQuery(id+"F0.wireOp",EDGE,"E24.right"),sQuery(id+"F0.wireOp",EDGE,"E25.top"),sQuery(id+"F0.wireOp",EDGE,"E25.left"),sQuery(id+"F0.wireOp",EDGE,"E25.right"),sQuery(id+"F0.wireOp",EDGE,"E26.top"),sQuery(id+"F0.wireOp",EDGE,"E26.left"),sQuery(id+"F0.wireOp",EDGE,"E26.right")])],"isStart":false})]});}
            var Q89;
            {var subQ0=sQuery(id+"F0.wireOp",EDGE,"E19.rect.left");Q89=makeQuery(id+"F1.opExtrude","CAP_EDGE",EDGE,{"disambiguationData":[OSD([subQ0]),TDD([makeQuery(id+"F0.imprint","IMPRINT",EDGE,{"disambiguationData":[TD([[makeQuery(id+"F0.imprint","INTERSECT",VERTEX,{"derivedFrom":[sQuery(id+"F0.wireOp",EDGE,"E10"),subQ0]}),-1.0]])],"derivedFrom":subQ0})])],"isStart":false});}
            var Q90;
            {var subQ0=sQuery(id+"F0.wireOp",EDGE,"E19.rect.left");var subQ1=sQuery(id+"F0.wireOp",EDGE,"E17.rect.bottom");Q90=makeQuery(id+"F3.opFillet","BLEND_EDGE",EDGE,{"blendedFrom":[makeQuery(id+"F1.opExtrude","SWEPT_EDGE",EDGE,{"disambiguationData":[OSD([subQ1,subQ0])]}),makeQuery(id+"F1.opExtrude","CAP_FACE",FACE,{"disambiguationData":[OSD([sQuery(id+"F0.wireOp",EDGE,"E0"),sQuery(id+"F0.wireOp",EDGE,"E1"),sQuery(id+"F0.wireOp",EDGE,"E2"),sQuery(id+"F0.wireOp",EDGE,"E3"),sQuery(id+"F0.wireOp",EDGE,"E4"),sQuery(id+"F0.wireOp",EDGE,"E5"),sQuery(id+"F0.wireOp",EDGE,"E6"),sQuery(id+"F0.wireOp",EDGE,"E7"),sQuery(id+"F0.wireOp",EDGE,"E8"),sQuery(id+"F0.wireOp",EDGE,"E9"),sQuery(id+"F0.wireOp",EDGE,"E10"),sQuery(id+"F0.wireOp",EDGE,"E11"),sQuery(id+"F0.wireOp",EDGE,"E12"),sQuery(id+"F0.wireOp",EDGE,"E13"),sQuery(id+"F0.wireOp",EDGE,"E14"),sQuery(id+"F0.wireOp",EDGE,"E15"),subQ1,sQuery(id+"F0.wireOp",EDGE,"E17.rect.top"),sQuery(id+"F0.wireOp",EDGE,"E17.rect.left"),sQuery(id+"F0.wireOp",EDGE,"E17.rect.right"),sQuery(id+"F0.wireOp",EDGE,"E18.rect.bottom"),sQuery(id+"F0.wireOp",EDGE,"E18.rect.top"),sQuery(id+"F0.wireOp",EDGE,"E18.rect.left"),sQuery(id+"F0.wireOp",EDGE,"E18.rect.right"),subQ0,sQuery(id+"F0.wireOp",EDGE,"E19.rect.right"),sQuery(id+"F0.wireOp",EDGE,"E20.rect.bottom"),sQuery(id+"F0.wireOp",EDGE,"E20.rect.top"),sQuery(id+"F0.wireOp",EDGE,"E23.top"),sQuery(id+"F0.wireOp",EDGE,"E23.left"),sQuery(id+"F0.wireOp",EDGE,"E23.right"),sQuery(id+"F0.wireOp",EDGE,"E24.top"),sQuery(id+"F0.wireOp",EDGE,"E24.left"),sQuery(id+"F0.wireOp",EDGE,"E24.right"),sQuery(id+"F0.wireOp",EDGE,"E25.top"),sQuery(id+"F0.wireOp",EDGE,"E25.left"),sQuery(id+"F0.wireOp",EDGE,"E25.right"),sQuery(id+"F0.wireOp",EDGE,"E26.top"),sQuery(id+"F0.wireOp",EDGE,"E26.left"),sQuery(id+"F0.wireOp",EDGE,"E26.right")])],"isStart":false})],"blendedInto":[makeQuery(id+"F1.opExtrude","CAP_FACE",FACE,{"disambiguationData":[OSD([sQuery(id+"F0.wireOp",EDGE,"E0"),sQuery(id+"F0.wireOp",EDGE,"E1"),sQuery(id+"F0.wireOp",EDGE,"E2"),sQuery(id+"F0.wireOp",EDGE,"E3"),sQuery(id+"F0.wireOp",EDGE,"E4"),sQuery(id+"F0.wireOp",EDGE,"E5"),sQuery(id+"F0.wireOp",EDGE,"E6"),sQuery(id+"F0.wireOp",EDGE,"E7"),sQuery(id+"F0.wireOp",EDGE,"E8"),sQuery(id+"F0.wireOp",EDGE,"E9"),sQuery(id+"F0.wireOp",EDGE,"E10"),sQuery(id+"F0.wireOp",EDGE,"E11"),sQuery(id+"F0.wireOp",EDGE,"E12"),sQuery(id+"F0.wireOp",EDGE,"E13"),sQuery(id+"F0.wireOp",EDGE,"E14"),sQuery(id+"F0.wireOp",EDGE,"E15"),subQ1,sQuery(id+"F0.wireOp",EDGE,"E17.rect.top"),sQuery(id+"F0.wireOp",EDGE,"E17.rect.left"),sQuery(id+"F0.wireOp",EDGE,"E17.rect.right"),sQuery(id+"F0.wireOp",EDGE,"E18.rect.bottom"),sQuery(id+"F0.wireOp",EDGE,"E18.rect.top"),sQuery(id+"F0.wireOp",EDGE,"E18.rect.left"),sQuery(id+"F0.wireOp",EDGE,"E18.rect.right"),subQ0,sQuery(id+"F0.wireOp",EDGE,"E19.rect.right"),sQuery(id+"F0.wireOp",EDGE,"E20.rect.bottom"),sQuery(id+"F0.wireOp",EDGE,"E20.rect.top"),sQuery(id+"F0.wireOp",EDGE,"E23.top"),sQuery(id+"F0.wireOp",EDGE,"E23.left"),sQuery(id+"F0.wireOp",EDGE,"E23.right"),sQuery(id+"F0.wireOp",EDGE,"E24.top"),sQuery(id+"F0.wireOp",EDGE,"E24.left"),sQuery(id+"F0.wireOp",EDGE,"E24.right"),sQuery(id+"F0.wireOp",EDGE,"E25.top"),sQuery(id+"F0.wireOp",EDGE,"E25.left"),sQuery(id+"F0.wireOp",EDGE,"E25.right"),sQuery(id+"F0.wireOp",EDGE,"E26.top"),sQuery(id+"F0.wireOp",EDGE,"E26.left"),sQuery(id+"F0.wireOp",EDGE,"E26.right")])],"isStart":false})]});}
            var Q91;
            {var subQ0=sQuery(id+"F0.wireOp",EDGE,"E17.rect.bottom");Q91=makeQuery(id+"F1.opExtrude","CAP_EDGE",EDGE,{"disambiguationData":[OSD([subQ0]),TDD([makeQuery(id+"F0.imprint","IMPRINT",EDGE,{"disambiguationData":[TD([[makeQuery(id+"F0.imprint","INTERSECT",VERTEX,{"derivedFrom":[subQ0,sQuery(id+"F0.wireOp",EDGE,"E19.rect.left")]}),1.0]])],"derivedFrom":subQ0})])],"isStart":false});}
            var Q92;
            Q92=makeQuery(id+"F1.opExtrude","CAP_EDGE",EDGE,{"disambiguationData":[OSD([sQuery(id+"F0.wireOp",EDGE,"E26.right")])],"isStart":false});
            var Q93;
            Q93=makeQuery(id+"F1.opExtrude","CAP_EDGE",EDGE,{"disambiguationData":[OSD([sQuery(id+"F0.wireOp",EDGE,"E23.right")])],"isStart":false});
            var Q94;
            {var subQ0=sQuery(id+"F0.wireOp",EDGE,"E17.rect.bottom");Q94=makeQuery(id+"F1.opExtrude","CAP_EDGE",EDGE,{"disambiguationData":[OSD([subQ0]),TDD([makeQuery(id+"F0.imprint","IMPRINT",EDGE,{"disambiguationData":[TD([[makeQuery(id+"F0.imprint","INTERSECT",VERTEX,{"derivedFrom":[subQ0,sQuery(id+"F0.wireOp",EDGE,"E19.rect.right")]}),-1.0]])],"derivedFrom":subQ0})])],"isStart":false});}
            var Q95;
            {var subQ0=sQuery(id+"F0.wireOp",EDGE,"E19.rect.right");var subQ1=sQuery(id+"F0.wireOp",EDGE,"E17.rect.bottom");Q95=makeQuery(id+"F3.opFillet","BLEND_EDGE",EDGE,{"blendedFrom":[makeQuery(id+"F1.opExtrude","SWEPT_EDGE",EDGE,{"disambiguationData":[OSD([subQ1,subQ0])]}),makeQuery(id+"F1.opExtrude","CAP_FACE",FACE,{"disambiguationData":[OSD([sQuery(id+"F0.wireOp",EDGE,"E0"),sQuery(id+"F0.wireOp",EDGE,"E1"),sQuery(id+"F0.wireOp",EDGE,"E2"),sQuery(id+"F0.wireOp",EDGE,"E3"),sQuery(id+"F0.wireOp",EDGE,"E4"),sQuery(id+"F0.wireOp",EDGE,"E5"),sQuery(id+"F0.wireOp",EDGE,"E6"),sQuery(id+"F0.wireOp",EDGE,"E7"),sQuery(id+"F0.wireOp",EDGE,"E8"),sQuery(id+"F0.wireOp",EDGE,"E9"),sQuery(id+"F0.wireOp",EDGE,"E10"),sQuery(id+"F0.wireOp",EDGE,"E11"),sQuery(id+"F0.wireOp",EDGE,"E12"),sQuery(id+"F0.wireOp",EDGE,"E13"),sQuery(id+"F0.wireOp",EDGE,"E14"),sQuery(id+"F0.wireOp",EDGE,"E15"),subQ1,sQuery(id+"F0.wireOp",EDGE,"E17.rect.top"),sQuery(id+"F0.wireOp",EDGE,"E17.rect.left"),sQuery(id+"F0.wireOp",EDGE,"E17.rect.right"),sQuery(id+"F0.wireOp",EDGE,"E18.rect.bottom"),sQuery(id+"F0.wireOp",EDGE,"E18.rect.top"),sQuery(id+"F0.wireOp",EDGE,"E18.rect.left"),sQuery(id+"F0.wireOp",EDGE,"E18.rect.right"),sQuery(id+"F0.wireOp",EDGE,"E19.rect.left"),subQ0,sQuery(id+"F0.wireOp",EDGE,"E20.rect.bottom"),sQuery(id+"F0.wireOp",EDGE,"E20.rect.top"),sQuery(id+"F0.wireOp",EDGE,"E23.top"),sQuery(id+"F0.wireOp",EDGE,"E23.left"),sQuery(id+"F0.wireOp",EDGE,"E23.right"),sQuery(id+"F0.wireOp",EDGE,"E24.top"),sQuery(id+"F0.wireOp",EDGE,"E24.left"),sQuery(id+"F0.wireOp",EDGE,"E24.right"),sQuery(id+"F0.wireOp",EDGE,"E25.top"),sQuery(id+"F0.wireOp",EDGE,"E25.left"),sQuery(id+"F0.wireOp",EDGE,"E25.right"),sQuery(id+"F0.wireOp",EDGE,"E26.top"),sQuery(id+"F0.wireOp",EDGE,"E26.left"),sQuery(id+"F0.wireOp",EDGE,"E26.right")])],"isStart":false})],"blendedInto":[makeQuery(id+"F1.opExtrude","CAP_FACE",FACE,{"disambiguationData":[OSD([sQuery(id+"F0.wireOp",EDGE,"E0"),sQuery(id+"F0.wireOp",EDGE,"E1"),sQuery(id+"F0.wireOp",EDGE,"E2"),sQuery(id+"F0.wireOp",EDGE,"E3"),sQuery(id+"F0.wireOp",EDGE,"E4"),sQuery(id+"F0.wireOp",EDGE,"E5"),sQuery(id+"F0.wireOp",EDGE,"E6"),sQuery(id+"F0.wireOp",EDGE,"E7"),sQuery(id+"F0.wireOp",EDGE,"E8"),sQuery(id+"F0.wireOp",EDGE,"E9"),sQuery(id+"F0.wireOp",EDGE,"E10"),sQuery(id+"F0.wireOp",EDGE,"E11"),sQuery(id+"F0.wireOp",EDGE,"E12"),sQuery(id+"F0.wireOp",EDGE,"E13"),sQuery(id+"F0.wireOp",EDGE,"E14"),sQuery(id+"F0.wireOp",EDGE,"E15"),subQ1,sQuery(id+"F0.wireOp",EDGE,"E17.rect.top"),sQuery(id+"F0.wireOp",EDGE,"E17.rect.left"),sQuery(id+"F0.wireOp",EDGE,"E17.rect.right"),sQuery(id+"F0.wireOp",EDGE,"E18.rect.bottom"),sQuery(id+"F0.wireOp",EDGE,"E18.rect.top"),sQuery(id+"F0.wireOp",EDGE,"E18.rect.left"),sQuery(id+"F0.wireOp",EDGE,"E18.rect.right"),sQuery(id+"F0.wireOp",EDGE,"E19.rect.left"),subQ0,sQuery(id+"F0.wireOp",EDGE,"E20.rect.bottom"),sQuery(id+"F0.wireOp",EDGE,"E20.rect.top"),sQuery(id+"F0.wireOp",EDGE,"E23.top"),sQuery(id+"F0.wireOp",EDGE,"E23.left"),sQuery(id+"F0.wireOp",EDGE,"E23.right"),sQuery(id+"F0.wireOp",EDGE,"E24.top"),sQuery(id+"F0.wireOp",EDGE,"E24.left"),sQuery(id+"F0.wireOp",EDGE,"E24.right"),sQuery(id+"F0.wireOp",EDGE,"E25.top"),sQuery(id+"F0.wireOp",EDGE,"E25.left"),sQuery(id+"F0.wireOp",EDGE,"E25.right"),sQuery(id+"F0.wireOp",EDGE,"E26.top"),sQuery(id+"F0.wireOp",EDGE,"E26.left"),sQuery(id+"F0.wireOp",EDGE,"E26.right")])],"isStart":false})]});}
            var Q96;
            {var subQ0=sQuery(id+"F0.wireOp",EDGE,"E19.rect.right");Q96=makeQuery(id+"F1.opExtrude","CAP_EDGE",EDGE,{"disambiguationData":[OSD([subQ0]),TDD([makeQuery(id+"F0.imprint","IMPRINT",EDGE,{"disambiguationData":[TD([[makeQuery(id+"F0.imprint","INTERSECT",VERTEX,{"derivedFrom":[sQuery(id+"F0.wireOp",EDGE,"E10"),subQ0]}),-1.0]])],"derivedFrom":subQ0})])],"isStart":false});}
            var Q97;
            {var subQ0=sQuery(id+"F0.wireOp",EDGE,"E19.rect.right");var subQ1=sQuery(id+"F0.wireOp",EDGE,"E10");Q97=makeQuery(id+"F3.opFillet","BLEND_EDGE",EDGE,{"blendedFrom":[makeQuery(id+"F1.opExtrude","SWEPT_EDGE",EDGE,{"disambiguationData":[OSD([subQ1,subQ0])]}),makeQuery(id+"F1.opExtrude","CAP_FACE",FACE,{"disambiguationData":[OSD([sQuery(id+"F0.wireOp",EDGE,"E0"),sQuery(id+"F0.wireOp",EDGE,"E1"),sQuery(id+"F0.wireOp",EDGE,"E2"),sQuery(id+"F0.wireOp",EDGE,"E3"),sQuery(id+"F0.wireOp",EDGE,"E4"),sQuery(id+"F0.wireOp",EDGE,"E5"),sQuery(id+"F0.wireOp",EDGE,"E6"),sQuery(id+"F0.wireOp",EDGE,"E7"),sQuery(id+"F0.wireOp",EDGE,"E8"),sQuery(id+"F0.wireOp",EDGE,"E9"),subQ1,sQuery(id+"F0.wireOp",EDGE,"E11"),sQuery(id+"F0.wireOp",EDGE,"E12"),sQuery(id+"F0.wireOp",EDGE,"E13"),sQuery(id+"F0.wireOp",EDGE,"E14"),sQuery(id+"F0.wireOp",EDGE,"E15"),sQuery(id+"F0.wireOp",EDGE,"E17.rect.bottom"),sQuery(id+"F0.wireOp",EDGE,"E17.rect.top"),sQuery(id+"F0.wireOp",EDGE,"E17.rect.left"),sQuery(id+"F0.wireOp",EDGE,"E17.rect.right"),sQuery(id+"F0.wireOp",EDGE,"E18.rect.bottom"),sQuery(id+"F0.wireOp",EDGE,"E18.rect.top"),sQuery(id+"F0.wireOp",EDGE,"E18.rect.left"),sQuery(id+"F0.wireOp",EDGE,"E18.rect.right"),sQuery(id+"F0.wireOp",EDGE,"E19.rect.left"),subQ0,sQuery(id+"F0.wireOp",EDGE,"E20.rect.bottom"),sQuery(id+"F0.wireOp",EDGE,"E20.rect.top"),sQuery(id+"F0.wireOp",EDGE,"E23.top"),sQuery(id+"F0.wireOp",EDGE,"E23.left"),sQuery(id+"F0.wireOp",EDGE,"E23.right"),sQuery(id+"F0.wireOp",EDGE,"E24.top"),sQuery(id+"F0.wireOp",EDGE,"E24.left"),sQuery(id+"F0.wireOp",EDGE,"E24.right"),sQuery(id+"F0.wireOp",EDGE,"E25.top"),sQuery(id+"F0.wireOp",EDGE,"E25.left"),sQuery(id+"F0.wireOp",EDGE,"E25.right"),sQuery(id+"F0.wireOp",EDGE,"E26.top"),sQuery(id+"F0.wireOp",EDGE,"E26.left"),sQuery(id+"F0.wireOp",EDGE,"E26.right")])],"isStart":false})],"blendedInto":[makeQuery(id+"F1.opExtrude","CAP_FACE",FACE,{"disambiguationData":[OSD([sQuery(id+"F0.wireOp",EDGE,"E0"),sQuery(id+"F0.wireOp",EDGE,"E1"),sQuery(id+"F0.wireOp",EDGE,"E2"),sQuery(id+"F0.wireOp",EDGE,"E3"),sQuery(id+"F0.wireOp",EDGE,"E4"),sQuery(id+"F0.wireOp",EDGE,"E5"),sQuery(id+"F0.wireOp",EDGE,"E6"),sQuery(id+"F0.wireOp",EDGE,"E7"),sQuery(id+"F0.wireOp",EDGE,"E8"),sQuery(id+"F0.wireOp",EDGE,"E9"),subQ1,sQuery(id+"F0.wireOp",EDGE,"E11"),sQuery(id+"F0.wireOp",EDGE,"E12"),sQuery(id+"F0.wireOp",EDGE,"E13"),sQuery(id+"F0.wireOp",EDGE,"E14"),sQuery(id+"F0.wireOp",EDGE,"E15"),sQuery(id+"F0.wireOp",EDGE,"E17.rect.bottom"),sQuery(id+"F0.wireOp",EDGE,"E17.rect.top"),sQuery(id+"F0.wireOp",EDGE,"E17.rect.left"),sQuery(id+"F0.wireOp",EDGE,"E17.rect.right"),sQuery(id+"F0.wireOp",EDGE,"E18.rect.bottom"),sQuery(id+"F0.wireOp",EDGE,"E18.rect.top"),sQuery(id+"F0.wireOp",EDGE,"E18.rect.left"),sQuery(id+"F0.wireOp",EDGE,"E18.rect.right"),sQuery(id+"F0.wireOp",EDGE,"E19.rect.left"),subQ0,sQuery(id+"F0.wireOp",EDGE,"E20.rect.bottom"),sQuery(id+"F0.wireOp",EDGE,"E20.rect.top"),sQuery(id+"F0.wireOp",EDGE,"E23.top"),sQuery(id+"F0.wireOp",EDGE,"E23.left"),sQuery(id+"F0.wireOp",EDGE,"E23.right"),sQuery(id+"F0.wireOp",EDGE,"E24.top"),sQuery(id+"F0.wireOp",EDGE,"E24.left"),sQuery(id+"F0.wireOp",EDGE,"E24.right"),sQuery(id+"F0.wireOp",EDGE,"E25.top"),sQuery(id+"F0.wireOp",EDGE,"E25.left"),sQuery(id+"F0.wireOp",EDGE,"E25.right"),sQuery(id+"F0.wireOp",EDGE,"E26.top"),sQuery(id+"F0.wireOp",EDGE,"E26.left"),sQuery(id+"F0.wireOp",EDGE,"E26.right")])],"isStart":false})]});}
            var Q98;
            {var subQ0=sQuery(id+"F0.wireOp",EDGE,"E10");var subQ1=makeQuery(id+"F0.imprint","INTERSECT",VERTEX,{"disambiguationData":[OD(1.0)],"derivedFrom":[sQuery(id+"F0.wireOp",EDGE,"E4"),subQ0]});Q98=makeQuery(id+"F1.opExtrude","CAP_EDGE",EDGE,{"disambiguationData":[OSD([subQ0]),TDD([makeQuery(id+"F0.imprint","IMPRINT",EDGE,{"disambiguationData":[TD([[makeQuery(id+"F0.imprint","INTERSECT",VERTEX,{"disambiguationData":[OD(1.0)],"derivedFrom":[sQuery(id+"F0.wireOp",EDGE,"E0"),subQ0]}),-1.0]])],"derivedFrom":subQ0}),makeQuery(id+"F0.imprint","IMPRINT",EDGE,{"disambiguationData":[TD([[subQ1,-1.0]])],"derivedFrom":subQ0})])],"isStart":false});}
            var Q99;
            {var subQ0=sQuery(id+"F0.wireOp",EDGE,"E8");var subQ1=makeQuery(id+"F0.imprint","INTERSECT",VERTEX,{"disambiguationData":[OD(1.0)],"derivedFrom":[sQuery(id+"F0.wireOp",EDGE,"E4"),subQ0]});Q99=makeQuery(id+"F1.opExtrude","CAP_EDGE",EDGE,{"disambiguationData":[OSD([subQ0]),TDD([makeQuery(id+"F0.imprint","IMPRINT",EDGE,{"disambiguationData":[TD([[subQ1,1.0]])],"derivedFrom":subQ0}),makeQuery(id+"F0.imprint","IMPRINT",EDGE,{"disambiguationData":[TD([[makeQuery(id+"F0.imprint","INTERSECT",VERTEX,{"disambiguationData":[OD(1.0)],"derivedFrom":[sQuery(id+"F0.wireOp",EDGE,"E0"),subQ0]}),1.0]])],"derivedFrom":subQ0})])],"isStart":false});}
            var Q100;
            {var subQ0=sQuery(id+"F0.wireOp",EDGE,"E20.rect.bottom");var subQ1=sQuery(id+"F0.wireOp",EDGE,"E8");Q100=makeQuery(id+"F3.opFillet","BLEND_EDGE",EDGE,{"blendedFrom":[makeQuery(id+"F1.opExtrude","SWEPT_EDGE",EDGE,{"disambiguationData":[OSD([subQ1,subQ0])]}),makeQuery(id+"F1.opExtrude","CAP_FACE",FACE,{"disambiguationData":[OSD([sQuery(id+"F0.wireOp",EDGE,"E0"),sQuery(id+"F0.wireOp",EDGE,"E1"),sQuery(id+"F0.wireOp",EDGE,"E2"),sQuery(id+"F0.wireOp",EDGE,"E3"),sQuery(id+"F0.wireOp",EDGE,"E4"),sQuery(id+"F0.wireOp",EDGE,"E5"),sQuery(id+"F0.wireOp",EDGE,"E6"),sQuery(id+"F0.wireOp",EDGE,"E7"),subQ1,sQuery(id+"F0.wireOp",EDGE,"E9"),sQuery(id+"F0.wireOp",EDGE,"E10"),sQuery(id+"F0.wireOp",EDGE,"E11"),sQuery(id+"F0.wireOp",EDGE,"E12"),sQuery(id+"F0.wireOp",EDGE,"E13"),sQuery(id+"F0.wireOp",EDGE,"E14"),sQuery(id+"F0.wireOp",EDGE,"E15"),sQuery(id+"F0.wireOp",EDGE,"E17.rect.bottom"),sQuery(id+"F0.wireOp",EDGE,"E17.rect.top"),sQuery(id+"F0.wireOp",EDGE,"E17.rect.left"),sQuery(id+"F0.wireOp",EDGE,"E17.rect.right"),sQuery(id+"F0.wireOp",EDGE,"E18.rect.bottom"),sQuery(id+"F0.wireOp",EDGE,"E18.rect.top"),sQuery(id+"F0.wireOp",EDGE,"E18.rect.left"),sQuery(id+"F0.wireOp",EDGE,"E18.rect.right"),sQuery(id+"F0.wireOp",EDGE,"E19.rect.left"),sQuery(id+"F0.wireOp",EDGE,"E19.rect.right"),subQ0,sQuery(id+"F0.wireOp",EDGE,"E20.rect.top"),sQuery(id+"F0.wireOp",EDGE,"E23.top"),sQuery(id+"F0.wireOp",EDGE,"E23.left"),sQuery(id+"F0.wireOp",EDGE,"E23.right"),sQuery(id+"F0.wireOp",EDGE,"E24.top"),sQuery(id+"F0.wireOp",EDGE,"E24.left"),sQuery(id+"F0.wireOp",EDGE,"E24.right"),sQuery(id+"F0.wireOp",EDGE,"E25.top"),sQuery(id+"F0.wireOp",EDGE,"E25.left"),sQuery(id+"F0.wireOp",EDGE,"E25.right"),sQuery(id+"F0.wireOp",EDGE,"E26.top"),sQuery(id+"F0.wireOp",EDGE,"E26.left"),sQuery(id+"F0.wireOp",EDGE,"E26.right")])],"isStart":false})],"blendedInto":[makeQuery(id+"F1.opExtrude","CAP_FACE",FACE,{"disambiguationData":[OSD([sQuery(id+"F0.wireOp",EDGE,"E0"),sQuery(id+"F0.wireOp",EDGE,"E1"),sQuery(id+"F0.wireOp",EDGE,"E2"),sQuery(id+"F0.wireOp",EDGE,"E3"),sQuery(id+"F0.wireOp",EDGE,"E4"),sQuery(id+"F0.wireOp",EDGE,"E5"),sQuery(id+"F0.wireOp",EDGE,"E6"),sQuery(id+"F0.wireOp",EDGE,"E7"),subQ1,sQuery(id+"F0.wireOp",EDGE,"E9"),sQuery(id+"F0.wireOp",EDGE,"E10"),sQuery(id+"F0.wireOp",EDGE,"E11"),sQuery(id+"F0.wireOp",EDGE,"E12"),sQuery(id+"F0.wireOp",EDGE,"E13"),sQuery(id+"F0.wireOp",EDGE,"E14"),sQuery(id+"F0.wireOp",EDGE,"E15"),sQuery(id+"F0.wireOp",EDGE,"E17.rect.bottom"),sQuery(id+"F0.wireOp",EDGE,"E17.rect.top"),sQuery(id+"F0.wireOp",EDGE,"E17.rect.left"),sQuery(id+"F0.wireOp",EDGE,"E17.rect.right"),sQuery(id+"F0.wireOp",EDGE,"E18.rect.bottom"),sQuery(id+"F0.wireOp",EDGE,"E18.rect.top"),sQuery(id+"F0.wireOp",EDGE,"E18.rect.left"),sQuery(id+"F0.wireOp",EDGE,"E18.rect.right"),sQuery(id+"F0.wireOp",EDGE,"E19.rect.left"),sQuery(id+"F0.wireOp",EDGE,"E19.rect.right"),subQ0,sQuery(id+"F0.wireOp",EDGE,"E20.rect.top"),sQuery(id+"F0.wireOp",EDGE,"E23.top"),sQuery(id+"F0.wireOp",EDGE,"E23.left"),sQuery(id+"F0.wireOp",EDGE,"E23.right"),sQuery(id+"F0.wireOp",EDGE,"E24.top"),sQuery(id+"F0.wireOp",EDGE,"E24.left"),sQuery(id+"F0.wireOp",EDGE,"E24.right"),sQuery(id+"F0.wireOp",EDGE,"E25.top"),sQuery(id+"F0.wireOp",EDGE,"E25.left"),sQuery(id+"F0.wireOp",EDGE,"E25.right"),sQuery(id+"F0.wireOp",EDGE,"E26.top"),sQuery(id+"F0.wireOp",EDGE,"E26.left"),sQuery(id+"F0.wireOp",EDGE,"E26.right")])],"isStart":false})]});}
            var Q101;
            {var subQ0=sQuery(id+"F0.wireOp",EDGE,"E20.rect.bottom");Q101=makeQuery(id+"F1.opExtrude","CAP_EDGE",EDGE,{"disambiguationData":[OSD([subQ0]),TDD([makeQuery(id+"F0.imprint","IMPRINT",EDGE,{"disambiguationData":[TD([[makeQuery(id+"F0.imprint","INTERSECT",VERTEX,{"derivedFrom":[sQuery(id+"F0.wireOp",EDGE,"E8"),subQ0]}),1.0]])],"derivedFrom":subQ0})])],"isStart":false});}
            var Q102;
            {var subQ0=sQuery(id+"F0.wireOp",EDGE,"E20.rect.bottom");var subQ1=sQuery(id+"F0.wireOp",EDGE,"E17.rect.right");Q102=makeQuery(id+"F3.opFillet","BLEND_EDGE",EDGE,{"blendedFrom":[makeQuery(id+"F1.opExtrude","SWEPT_EDGE",EDGE,{"disambiguationData":[OSD([subQ1,subQ0])]}),makeQuery(id+"F1.opExtrude","CAP_FACE",FACE,{"disambiguationData":[OSD([sQuery(id+"F0.wireOp",EDGE,"E0"),sQuery(id+"F0.wireOp",EDGE,"E1"),sQuery(id+"F0.wireOp",EDGE,"E2"),sQuery(id+"F0.wireOp",EDGE,"E3"),sQuery(id+"F0.wireOp",EDGE,"E4"),sQuery(id+"F0.wireOp",EDGE,"E5"),sQuery(id+"F0.wireOp",EDGE,"E6"),sQuery(id+"F0.wireOp",EDGE,"E7"),sQuery(id+"F0.wireOp",EDGE,"E8"),sQuery(id+"F0.wireOp",EDGE,"E9"),sQuery(id+"F0.wireOp",EDGE,"E10"),sQuery(id+"F0.wireOp",EDGE,"E11"),sQuery(id+"F0.wireOp",EDGE,"E12"),sQuery(id+"F0.wireOp",EDGE,"E13"),sQuery(id+"F0.wireOp",EDGE,"E14"),sQuery(id+"F0.wireOp",EDGE,"E15"),sQuery(id+"F0.wireOp",EDGE,"E17.rect.bottom"),sQuery(id+"F0.wireOp",EDGE,"E17.rect.top"),sQuery(id+"F0.wireOp",EDGE,"E17.rect.left"),subQ1,sQuery(id+"F0.wireOp",EDGE,"E18.rect.bottom"),sQuery(id+"F0.wireOp",EDGE,"E18.rect.top"),sQuery(id+"F0.wireOp",EDGE,"E18.rect.left"),sQuery(id+"F0.wireOp",EDGE,"E18.rect.right"),sQuery(id+"F0.wireOp",EDGE,"E19.rect.left"),sQuery(id+"F0.wireOp",EDGE,"E19.rect.right"),subQ0,sQuery(id+"F0.wireOp",EDGE,"E20.rect.top"),sQuery(id+"F0.wireOp",EDGE,"E23.top"),sQuery(id+"F0.wireOp",EDGE,"E23.left"),sQuery(id+"F0.wireOp",EDGE,"E23.right"),sQuery(id+"F0.wireOp",EDGE,"E24.top"),sQuery(id+"F0.wireOp",EDGE,"E24.left"),sQuery(id+"F0.wireOp",EDGE,"E24.right"),sQuery(id+"F0.wireOp",EDGE,"E25.top"),sQuery(id+"F0.wireOp",EDGE,"E25.left"),sQuery(id+"F0.wireOp",EDGE,"E25.right"),sQuery(id+"F0.wireOp",EDGE,"E26.top"),sQuery(id+"F0.wireOp",EDGE,"E26.left"),sQuery(id+"F0.wireOp",EDGE,"E26.right")])],"isStart":false})],"blendedInto":[makeQuery(id+"F1.opExtrude","CAP_FACE",FACE,{"disambiguationData":[OSD([sQuery(id+"F0.wireOp",EDGE,"E0"),sQuery(id+"F0.wireOp",EDGE,"E1"),sQuery(id+"F0.wireOp",EDGE,"E2"),sQuery(id+"F0.wireOp",EDGE,"E3"),sQuery(id+"F0.wireOp",EDGE,"E4"),sQuery(id+"F0.wireOp",EDGE,"E5"),sQuery(id+"F0.wireOp",EDGE,"E6"),sQuery(id+"F0.wireOp",EDGE,"E7"),sQuery(id+"F0.wireOp",EDGE,"E8"),sQuery(id+"F0.wireOp",EDGE,"E9"),sQuery(id+"F0.wireOp",EDGE,"E10"),sQuery(id+"F0.wireOp",EDGE,"E11"),sQuery(id+"F0.wireOp",EDGE,"E12"),sQuery(id+"F0.wireOp",EDGE,"E13"),sQuery(id+"F0.wireOp",EDGE,"E14"),sQuery(id+"F0.wireOp",EDGE,"E15"),sQuery(id+"F0.wireOp",EDGE,"E17.rect.bottom"),sQuery(id+"F0.wireOp",EDGE,"E17.rect.top"),sQuery(id+"F0.wireOp",EDGE,"E17.rect.left"),subQ1,sQuery(id+"F0.wireOp",EDGE,"E18.rect.bottom"),sQuery(id+"F0.wireOp",EDGE,"E18.rect.top"),sQuery(id+"F0.wireOp",EDGE,"E18.rect.left"),sQuery(id+"F0.wireOp",EDGE,"E18.rect.right"),sQuery(id+"F0.wireOp",EDGE,"E19.rect.left"),sQuery(id+"F0.wireOp",EDGE,"E19.rect.right"),subQ0,sQuery(id+"F0.wireOp",EDGE,"E20.rect.top"),sQuery(id+"F0.wireOp",EDGE,"E23.top"),sQuery(id+"F0.wireOp",EDGE,"E23.left"),sQuery(id+"F0.wireOp",EDGE,"E23.right"),sQuery(id+"F0.wireOp",EDGE,"E24.top"),sQuery(id+"F0.wireOp",EDGE,"E24.left"),sQuery(id+"F0.wireOp",EDGE,"E24.right"),sQuery(id+"F0.wireOp",EDGE,"E25.top"),sQuery(id+"F0.wireOp",EDGE,"E25.left"),sQuery(id+"F0.wireOp",EDGE,"E25.right"),sQuery(id+"F0.wireOp",EDGE,"E26.top"),sQuery(id+"F0.wireOp",EDGE,"E26.left"),sQuery(id+"F0.wireOp",EDGE,"E26.right")])],"isStart":false})]});}
            var Q103;
            Q103=makeQuery(id+"F1.opExtrude","CAP_EDGE",EDGE,{"disambiguationData":[OSD([sQuery(id+"F0.wireOp",EDGE,"E17.rect.right"),sQuery(id+"F0.wireOp",EDGE,"E23.left")])],"isStart":false});
            var Q104;
            {var subQ0=sQuery(id+"F0.wireOp",EDGE,"E19.rect.right");var subQ2=makeQuery(id+"F0.imprint","INTERSECT",VERTEX,{"derivedFrom":[subQ0,sQuery(id+"F0.wireOp",EDGE,"E20.rect.bottom")]});Q104=makeQuery(id+"F1.opExtrude","CAP_EDGE",EDGE,{"disambiguationData":[OSD([subQ0]),TDD([makeQuery(id+"F0.imprint","IMPRINT",EDGE,{"disambiguationData":[TD([[makeQuery(id+"F0.imprint","INTERSECT",VERTEX,{"derivedFrom":[sQuery(id+"F0.wireOp",EDGE,"E18.rect.bottom"),subQ0]}),-1.0]])],"derivedFrom":subQ0}),makeQuery(id+"F0.imprint","IMPRINT",EDGE,{"disambiguationData":[TD([[subQ2,-1.0]])],"derivedFrom":subQ0}),makeQuery(id+"F0.imprint","IMPRINT",EDGE,{"disambiguationData":[TD([[makeQuery(id+"F0.imprint","INTERSECT",VERTEX,{"derivedFrom":[sQuery(id+"F0.wireOp",EDGE,"E18.rect.top"),subQ0]}),1.0]])],"derivedFrom":subQ0})])],"isStart":true});}
            var Q105;
            {var subQ0=sQuery(id+"F0.wireOp",EDGE,"E19.rect.left");var subQ2=makeQuery(id+"F0.imprint","INTERSECT",VERTEX,{"derivedFrom":[subQ0,sQuery(id+"F0.wireOp",EDGE,"E20.rect.bottom")]});Q105=makeQuery(id+"F1.opExtrude","CAP_EDGE",EDGE,{"disambiguationData":[OSD([subQ0]),TDD([makeQuery(id+"F0.imprint","IMPRINT",EDGE,{"disambiguationData":[TD([[makeQuery(id+"F0.imprint","INTERSECT",VERTEX,{"derivedFrom":[sQuery(id+"F0.wireOp",EDGE,"E18.rect.bottom"),subQ0]}),-1.0]])],"derivedFrom":subQ0}),makeQuery(id+"F0.imprint","IMPRINT",EDGE,{"disambiguationData":[TD([[subQ2,-1.0]])],"derivedFrom":subQ0}),makeQuery(id+"F0.imprint","IMPRINT",EDGE,{"disambiguationData":[TD([[makeQuery(id+"F0.imprint","INTERSECT",VERTEX,{"derivedFrom":[sQuery(id+"F0.wireOp",EDGE,"E18.rect.top"),subQ0]}),1.0]])],"derivedFrom":subQ0})])],"isStart":true});}
            var Q106;
            {var subQ0=sQuery(id+"F0.wireOp",EDGE,"E19.rect.left");var subQ1=sQuery(id+"F0.wireOp",EDGE,"E18.rect.top");Q106=makeQuery(id+"F3.opFillet","BLEND_EDGE",EDGE,{"blendedFrom":[makeQuery(id+"F1.opExtrude","SWEPT_EDGE",EDGE,{"disambiguationData":[OSD([subQ1,subQ0])]}),makeQuery(id+"F1.opExtrude","CAP_FACE",FACE,{"disambiguationData":[OSD([sQuery(id+"F0.wireOp",EDGE,"E0"),sQuery(id+"F0.wireOp",EDGE,"E1"),sQuery(id+"F0.wireOp",EDGE,"E2"),sQuery(id+"F0.wireOp",EDGE,"E3"),sQuery(id+"F0.wireOp",EDGE,"E4"),sQuery(id+"F0.wireOp",EDGE,"E5"),sQuery(id+"F0.wireOp",EDGE,"E6"),sQuery(id+"F0.wireOp",EDGE,"E7"),sQuery(id+"F0.wireOp",EDGE,"E8"),sQuery(id+"F0.wireOp",EDGE,"E9"),sQuery(id+"F0.wireOp",EDGE,"E10"),sQuery(id+"F0.wireOp",EDGE,"E11"),sQuery(id+"F0.wireOp",EDGE,"E12"),sQuery(id+"F0.wireOp",EDGE,"E13"),sQuery(id+"F0.wireOp",EDGE,"E14"),sQuery(id+"F0.wireOp",EDGE,"E15"),sQuery(id+"F0.wireOp",EDGE,"E17.rect.bottom"),sQuery(id+"F0.wireOp",EDGE,"E17.rect.top"),sQuery(id+"F0.wireOp",EDGE,"E17.rect.left"),sQuery(id+"F0.wireOp",EDGE,"E17.rect.right"),sQuery(id+"F0.wireOp",EDGE,"E18.rect.bottom"),subQ1,sQuery(id+"F0.wireOp",EDGE,"E18.rect.left"),sQuery(id+"F0.wireOp",EDGE,"E18.rect.right"),subQ0,sQuery(id+"F0.wireOp",EDGE,"E19.rect.right"),sQuery(id+"F0.wireOp",EDGE,"E20.rect.bottom"),sQuery(id+"F0.wireOp",EDGE,"E20.rect.top"),sQuery(id+"F0.wireOp",EDGE,"E23.left"),sQuery(id+"F0.wireOp",EDGE,"E23.right"),sQuery(id+"F0.wireOp",EDGE,"E24.left"),sQuery(id+"F0.wireOp",EDGE,"E24.right"),sQuery(id+"F0.wireOp",EDGE,"E25.left"),sQuery(id+"F0.wireOp",EDGE,"E25.right"),sQuery(id+"F0.wireOp",EDGE,"E26.left"),sQuery(id+"F0.wireOp",EDGE,"E26.right"),sQuery(id+"F0.wireOp",EDGE,"E27.rect.bottom"),sQuery(id+"F0.wireOp",EDGE,"E27.rect.top"),sQuery(id+"F0.wireOp",EDGE,"E27.rect.left"),sQuery(id+"F0.wireOp",EDGE,"E27.rect.right"),sQuery(id+"F0.wireOp",EDGE,"E28.rect.bottom"),sQuery(id+"F0.wireOp",EDGE,"E28.rect.top"),sQuery(id+"F0.wireOp",EDGE,"E28.rect.left"),sQuery(id+"F0.wireOp",EDGE,"E28.rect.right"),sQuery(id+"F0.wireOp",EDGE,"E29.rect.bottom"),sQuery(id+"F0.wireOp",EDGE,"E29.rect.top"),sQuery(id+"F0.wireOp",EDGE,"E29.rect.left"),sQuery(id+"F0.wireOp",EDGE,"E29.rect.right"),sQuery(id+"F0.wireOp",EDGE,"E30.rect.bottom"),sQuery(id+"F0.wireOp",EDGE,"E30.rect.top"),sQuery(id+"F0.wireOp",EDGE,"E30.rect.left"),sQuery(id+"F0.wireOp",EDGE,"E30.rect.right")])],"isStart":true})],"blendedInto":[makeQuery(id+"F1.opExtrude","CAP_FACE",FACE,{"disambiguationData":[OSD([sQuery(id+"F0.wireOp",EDGE,"E0"),sQuery(id+"F0.wireOp",EDGE,"E1"),sQuery(id+"F0.wireOp",EDGE,"E2"),sQuery(id+"F0.wireOp",EDGE,"E3"),sQuery(id+"F0.wireOp",EDGE,"E4"),sQuery(id+"F0.wireOp",EDGE,"E5"),sQuery(id+"F0.wireOp",EDGE,"E6"),sQuery(id+"F0.wireOp",EDGE,"E7"),sQuery(id+"F0.wireOp",EDGE,"E8"),sQuery(id+"F0.wireOp",EDGE,"E9"),sQuery(id+"F0.wireOp",EDGE,"E10"),sQuery(id+"F0.wireOp",EDGE,"E11"),sQuery(id+"F0.wireOp",EDGE,"E12"),sQuery(id+"F0.wireOp",EDGE,"E13"),sQuery(id+"F0.wireOp",EDGE,"E14"),sQuery(id+"F0.wireOp",EDGE,"E15"),sQuery(id+"F0.wireOp",EDGE,"E17.rect.bottom"),sQuery(id+"F0.wireOp",EDGE,"E17.rect.top"),sQuery(id+"F0.wireOp",EDGE,"E17.rect.left"),sQuery(id+"F0.wireOp",EDGE,"E17.rect.right"),sQuery(id+"F0.wireOp",EDGE,"E18.rect.bottom"),subQ1,sQuery(id+"F0.wireOp",EDGE,"E18.rect.left"),sQuery(id+"F0.wireOp",EDGE,"E18.rect.right"),subQ0,sQuery(id+"F0.wireOp",EDGE,"E19.rect.right"),sQuery(id+"F0.wireOp",EDGE,"E20.rect.bottom"),sQuery(id+"F0.wireOp",EDGE,"E20.rect.top"),sQuery(id+"F0.wireOp",EDGE,"E23.left"),sQuery(id+"F0.wireOp",EDGE,"E23.right"),sQuery(id+"F0.wireOp",EDGE,"E24.left"),sQuery(id+"F0.wireOp",EDGE,"E24.right"),sQuery(id+"F0.wireOp",EDGE,"E25.left"),sQuery(id+"F0.wireOp",EDGE,"E25.right"),sQuery(id+"F0.wireOp",EDGE,"E26.left"),sQuery(id+"F0.wireOp",EDGE,"E26.right"),sQuery(id+"F0.wireOp",EDGE,"E27.rect.bottom"),sQuery(id+"F0.wireOp",EDGE,"E27.rect.top"),sQuery(id+"F0.wireOp",EDGE,"E27.rect.left"),sQuery(id+"F0.wireOp",EDGE,"E27.rect.right"),sQuery(id+"F0.wireOp",EDGE,"E28.rect.bottom"),sQuery(id+"F0.wireOp",EDGE,"E28.rect.top"),sQuery(id+"F0.wireOp",EDGE,"E28.rect.left"),sQuery(id+"F0.wireOp",EDGE,"E28.rect.right"),sQuery(id+"F0.wireOp",EDGE,"E29.rect.bottom"),sQuery(id+"F0.wireOp",EDGE,"E29.rect.top"),sQuery(id+"F0.wireOp",EDGE,"E29.rect.left"),sQuery(id+"F0.wireOp",EDGE,"E29.rect.right"),sQuery(id+"F0.wireOp",EDGE,"E30.rect.bottom"),sQuery(id+"F0.wireOp",EDGE,"E30.rect.top"),sQuery(id+"F0.wireOp",EDGE,"E30.rect.left"),sQuery(id+"F0.wireOp",EDGE,"E30.rect.right")])],"isStart":true})]});}
            var Q107;
            {var subQ0=sQuery(id+"F0.wireOp",EDGE,"E19.rect.left");var subQ1=sQuery(id+"F0.wireOp",EDGE,"E18.rect.bottom");Q107=makeQuery(id+"F3.opFillet","BLEND_EDGE",EDGE,{"blendedFrom":[makeQuery(id+"F1.opExtrude","SWEPT_EDGE",EDGE,{"disambiguationData":[OSD([subQ1,subQ0])]}),makeQuery(id+"F1.opExtrude","CAP_FACE",FACE,{"disambiguationData":[OSD([sQuery(id+"F0.wireOp",EDGE,"E0"),sQuery(id+"F0.wireOp",EDGE,"E1"),sQuery(id+"F0.wireOp",EDGE,"E2"),sQuery(id+"F0.wireOp",EDGE,"E3"),sQuery(id+"F0.wireOp",EDGE,"E4"),sQuery(id+"F0.wireOp",EDGE,"E5"),sQuery(id+"F0.wireOp",EDGE,"E6"),sQuery(id+"F0.wireOp",EDGE,"E7"),sQuery(id+"F0.wireOp",EDGE,"E8"),sQuery(id+"F0.wireOp",EDGE,"E9"),sQuery(id+"F0.wireOp",EDGE,"E10"),sQuery(id+"F0.wireOp",EDGE,"E11"),sQuery(id+"F0.wireOp",EDGE,"E12"),sQuery(id+"F0.wireOp",EDGE,"E13"),sQuery(id+"F0.wireOp",EDGE,"E14"),sQuery(id+"F0.wireOp",EDGE,"E15"),sQuery(id+"F0.wireOp",EDGE,"E17.rect.bottom"),sQuery(id+"F0.wireOp",EDGE,"E17.rect.top"),sQuery(id+"F0.wireOp",EDGE,"E17.rect.left"),sQuery(id+"F0.wireOp",EDGE,"E17.rect.right"),subQ1,sQuery(id+"F0.wireOp",EDGE,"E18.rect.top"),sQuery(id+"F0.wireOp",EDGE,"E18.rect.left"),sQuery(id+"F0.wireOp",EDGE,"E18.rect.right"),subQ0,sQuery(id+"F0.wireOp",EDGE,"E19.rect.right"),sQuery(id+"F0.wireOp",EDGE,"E20.rect.bottom"),sQuery(id+"F0.wireOp",EDGE,"E20.rect.top"),sQuery(id+"F0.wireOp",EDGE,"E23.left"),sQuery(id+"F0.wireOp",EDGE,"E23.right"),sQuery(id+"F0.wireOp",EDGE,"E24.left"),sQuery(id+"F0.wireOp",EDGE,"E24.right"),sQuery(id+"F0.wireOp",EDGE,"E25.left"),sQuery(id+"F0.wireOp",EDGE,"E25.right"),sQuery(id+"F0.wireOp",EDGE,"E26.left"),sQuery(id+"F0.wireOp",EDGE,"E26.right"),sQuery(id+"F0.wireOp",EDGE,"E27.rect.bottom"),sQuery(id+"F0.wireOp",EDGE,"E27.rect.top"),sQuery(id+"F0.wireOp",EDGE,"E27.rect.left"),sQuery(id+"F0.wireOp",EDGE,"E27.rect.right"),sQuery(id+"F0.wireOp",EDGE,"E28.rect.bottom"),sQuery(id+"F0.wireOp",EDGE,"E28.rect.top"),sQuery(id+"F0.wireOp",EDGE,"E28.rect.left"),sQuery(id+"F0.wireOp",EDGE,"E28.rect.right"),sQuery(id+"F0.wireOp",EDGE,"E29.rect.bottom"),sQuery(id+"F0.wireOp",EDGE,"E29.rect.top"),sQuery(id+"F0.wireOp",EDGE,"E29.rect.left"),sQuery(id+"F0.wireOp",EDGE,"E29.rect.right"),sQuery(id+"F0.wireOp",EDGE,"E30.rect.bottom"),sQuery(id+"F0.wireOp",EDGE,"E30.rect.top"),sQuery(id+"F0.wireOp",EDGE,"E30.rect.left"),sQuery(id+"F0.wireOp",EDGE,"E30.rect.right")])],"isStart":true})],"blendedInto":[makeQuery(id+"F1.opExtrude","CAP_FACE",FACE,{"disambiguationData":[OSD([sQuery(id+"F0.wireOp",EDGE,"E0"),sQuery(id+"F0.wireOp",EDGE,"E1"),sQuery(id+"F0.wireOp",EDGE,"E2"),sQuery(id+"F0.wireOp",EDGE,"E3"),sQuery(id+"F0.wireOp",EDGE,"E4"),sQuery(id+"F0.wireOp",EDGE,"E5"),sQuery(id+"F0.wireOp",EDGE,"E6"),sQuery(id+"F0.wireOp",EDGE,"E7"),sQuery(id+"F0.wireOp",EDGE,"E8"),sQuery(id+"F0.wireOp",EDGE,"E9"),sQuery(id+"F0.wireOp",EDGE,"E10"),sQuery(id+"F0.wireOp",EDGE,"E11"),sQuery(id+"F0.wireOp",EDGE,"E12"),sQuery(id+"F0.wireOp",EDGE,"E13"),sQuery(id+"F0.wireOp",EDGE,"E14"),sQuery(id+"F0.wireOp",EDGE,"E15"),sQuery(id+"F0.wireOp",EDGE,"E17.rect.bottom"),sQuery(id+"F0.wireOp",EDGE,"E17.rect.top"),sQuery(id+"F0.wireOp",EDGE,"E17.rect.left"),sQuery(id+"F0.wireOp",EDGE,"E17.rect.right"),subQ1,sQuery(id+"F0.wireOp",EDGE,"E18.rect.top"),sQuery(id+"F0.wireOp",EDGE,"E18.rect.left"),sQuery(id+"F0.wireOp",EDGE,"E18.rect.right"),subQ0,sQuery(id+"F0.wireOp",EDGE,"E19.rect.right"),sQuery(id+"F0.wireOp",EDGE,"E20.rect.bottom"),sQuery(id+"F0.wireOp",EDGE,"E20.rect.top"),sQuery(id+"F0.wireOp",EDGE,"E23.left"),sQuery(id+"F0.wireOp",EDGE,"E23.right"),sQuery(id+"F0.wireOp",EDGE,"E24.left"),sQuery(id+"F0.wireOp",EDGE,"E24.right"),sQuery(id+"F0.wireOp",EDGE,"E25.left"),sQuery(id+"F0.wireOp",EDGE,"E25.right"),sQuery(id+"F0.wireOp",EDGE,"E26.left"),sQuery(id+"F0.wireOp",EDGE,"E26.right"),sQuery(id+"F0.wireOp",EDGE,"E27.rect.bottom"),sQuery(id+"F0.wireOp",EDGE,"E27.rect.top"),sQuery(id+"F0.wireOp",EDGE,"E27.rect.left"),sQuery(id+"F0.wireOp",EDGE,"E27.rect.right"),sQuery(id+"F0.wireOp",EDGE,"E28.rect.bottom"),sQuery(id+"F0.wireOp",EDGE,"E28.rect.top"),sQuery(id+"F0.wireOp",EDGE,"E28.rect.left"),sQuery(id+"F0.wireOp",EDGE,"E28.rect.right"),sQuery(id+"F0.wireOp",EDGE,"E29.rect.bottom"),sQuery(id+"F0.wireOp",EDGE,"E29.rect.top"),sQuery(id+"F0.wireOp",EDGE,"E29.rect.left"),sQuery(id+"F0.wireOp",EDGE,"E29.rect.right"),sQuery(id+"F0.wireOp",EDGE,"E30.rect.bottom"),sQuery(id+"F0.wireOp",EDGE,"E30.rect.top"),sQuery(id+"F0.wireOp",EDGE,"E30.rect.left"),sQuery(id+"F0.wireOp",EDGE,"E30.rect.right")])],"isStart":true})]});}
            var Q108;
            {var subQ0=sQuery(id+"F0.wireOp",EDGE,"E19.rect.right");var subQ1=sQuery(id+"F0.wireOp",EDGE,"E18.rect.bottom");Q108=makeQuery(id+"F3.opFillet","BLEND_EDGE",EDGE,{"blendedFrom":[makeQuery(id+"F1.opExtrude","SWEPT_EDGE",EDGE,{"disambiguationData":[OSD([subQ1,subQ0])]}),makeQuery(id+"F1.opExtrude","CAP_FACE",FACE,{"disambiguationData":[OSD([sQuery(id+"F0.wireOp",EDGE,"E0"),sQuery(id+"F0.wireOp",EDGE,"E1"),sQuery(id+"F0.wireOp",EDGE,"E2"),sQuery(id+"F0.wireOp",EDGE,"E3"),sQuery(id+"F0.wireOp",EDGE,"E4"),sQuery(id+"F0.wireOp",EDGE,"E5"),sQuery(id+"F0.wireOp",EDGE,"E6"),sQuery(id+"F0.wireOp",EDGE,"E7"),sQuery(id+"F0.wireOp",EDGE,"E8"),sQuery(id+"F0.wireOp",EDGE,"E9"),sQuery(id+"F0.wireOp",EDGE,"E10"),sQuery(id+"F0.wireOp",EDGE,"E11"),sQuery(id+"F0.wireOp",EDGE,"E12"),sQuery(id+"F0.wireOp",EDGE,"E13"),sQuery(id+"F0.wireOp",EDGE,"E14"),sQuery(id+"F0.wireOp",EDGE,"E15"),sQuery(id+"F0.wireOp",EDGE,"E17.rect.bottom"),sQuery(id+"F0.wireOp",EDGE,"E17.rect.top"),sQuery(id+"F0.wireOp",EDGE,"E17.rect.left"),sQuery(id+"F0.wireOp",EDGE,"E17.rect.right"),subQ1,sQuery(id+"F0.wireOp",EDGE,"E18.rect.top"),sQuery(id+"F0.wireOp",EDGE,"E18.rect.left"),sQuery(id+"F0.wireOp",EDGE,"E18.rect.right"),sQuery(id+"F0.wireOp",EDGE,"E19.rect.left"),subQ0,sQuery(id+"F0.wireOp",EDGE,"E20.rect.bottom"),sQuery(id+"F0.wireOp",EDGE,"E20.rect.top"),sQuery(id+"F0.wireOp",EDGE,"E23.left"),sQuery(id+"F0.wireOp",EDGE,"E23.right"),sQuery(id+"F0.wireOp",EDGE,"E24.left"),sQuery(id+"F0.wireOp",EDGE,"E24.right"),sQuery(id+"F0.wireOp",EDGE,"E25.left"),sQuery(id+"F0.wireOp",EDGE,"E25.right"),sQuery(id+"F0.wireOp",EDGE,"E26.left"),sQuery(id+"F0.wireOp",EDGE,"E26.right"),sQuery(id+"F0.wireOp",EDGE,"E27.rect.bottom"),sQuery(id+"F0.wireOp",EDGE,"E27.rect.top"),sQuery(id+"F0.wireOp",EDGE,"E27.rect.left"),sQuery(id+"F0.wireOp",EDGE,"E27.rect.right"),sQuery(id+"F0.wireOp",EDGE,"E28.rect.bottom"),sQuery(id+"F0.wireOp",EDGE,"E28.rect.top"),sQuery(id+"F0.wireOp",EDGE,"E28.rect.left"),sQuery(id+"F0.wireOp",EDGE,"E28.rect.right"),sQuery(id+"F0.wireOp",EDGE,"E29.rect.bottom"),sQuery(id+"F0.wireOp",EDGE,"E29.rect.top"),sQuery(id+"F0.wireOp",EDGE,"E29.rect.left"),sQuery(id+"F0.wireOp",EDGE,"E29.rect.right"),sQuery(id+"F0.wireOp",EDGE,"E30.rect.bottom"),sQuery(id+"F0.wireOp",EDGE,"E30.rect.top"),sQuery(id+"F0.wireOp",EDGE,"E30.rect.left"),sQuery(id+"F0.wireOp",EDGE,"E30.rect.right")])],"isStart":true})],"blendedInto":[makeQuery(id+"F1.opExtrude","CAP_FACE",FACE,{"disambiguationData":[OSD([sQuery(id+"F0.wireOp",EDGE,"E0"),sQuery(id+"F0.wireOp",EDGE,"E1"),sQuery(id+"F0.wireOp",EDGE,"E2"),sQuery(id+"F0.wireOp",EDGE,"E3"),sQuery(id+"F0.wireOp",EDGE,"E4"),sQuery(id+"F0.wireOp",EDGE,"E5"),sQuery(id+"F0.wireOp",EDGE,"E6"),sQuery(id+"F0.wireOp",EDGE,"E7"),sQuery(id+"F0.wireOp",EDGE,"E8"),sQuery(id+"F0.wireOp",EDGE,"E9"),sQuery(id+"F0.wireOp",EDGE,"E10"),sQuery(id+"F0.wireOp",EDGE,"E11"),sQuery(id+"F0.wireOp",EDGE,"E12"),sQuery(id+"F0.wireOp",EDGE,"E13"),sQuery(id+"F0.wireOp",EDGE,"E14"),sQuery(id+"F0.wireOp",EDGE,"E15"),sQuery(id+"F0.wireOp",EDGE,"E17.rect.bottom"),sQuery(id+"F0.wireOp",EDGE,"E17.rect.top"),sQuery(id+"F0.wireOp",EDGE,"E17.rect.left"),sQuery(id+"F0.wireOp",EDGE,"E17.rect.right"),subQ1,sQuery(id+"F0.wireOp",EDGE,"E18.rect.top"),sQuery(id+"F0.wireOp",EDGE,"E18.rect.left"),sQuery(id+"F0.wireOp",EDGE,"E18.rect.right"),sQuery(id+"F0.wireOp",EDGE,"E19.rect.left"),subQ0,sQuery(id+"F0.wireOp",EDGE,"E20.rect.bottom"),sQuery(id+"F0.wireOp",EDGE,"E20.rect.top"),sQuery(id+"F0.wireOp",EDGE,"E23.left"),sQuery(id+"F0.wireOp",EDGE,"E23.right"),sQuery(id+"F0.wireOp",EDGE,"E24.left"),sQuery(id+"F0.wireOp",EDGE,"E24.right"),sQuery(id+"F0.wireOp",EDGE,"E25.left"),sQuery(id+"F0.wireOp",EDGE,"E25.right"),sQuery(id+"F0.wireOp",EDGE,"E26.left"),sQuery(id+"F0.wireOp",EDGE,"E26.right"),sQuery(id+"F0.wireOp",EDGE,"E27.rect.bottom"),sQuery(id+"F0.wireOp",EDGE,"E27.rect.top"),sQuery(id+"F0.wireOp",EDGE,"E27.rect.left"),sQuery(id+"F0.wireOp",EDGE,"E27.rect.right"),sQuery(id+"F0.wireOp",EDGE,"E28.rect.bottom"),sQuery(id+"F0.wireOp",EDGE,"E28.rect.top"),sQuery(id+"F0.wireOp",EDGE,"E28.rect.left"),sQuery(id+"F0.wireOp",EDGE,"E28.rect.right"),sQuery(id+"F0.wireOp",EDGE,"E29.rect.bottom"),sQuery(id+"F0.wireOp",EDGE,"E29.rect.top"),sQuery(id+"F0.wireOp",EDGE,"E29.rect.left"),sQuery(id+"F0.wireOp",EDGE,"E29.rect.right"),sQuery(id+"F0.wireOp",EDGE,"E30.rect.bottom"),sQuery(id+"F0.wireOp",EDGE,"E30.rect.top"),sQuery(id+"F0.wireOp",EDGE,"E30.rect.left"),sQuery(id+"F0.wireOp",EDGE,"E30.rect.right")])],"isStart":true})]});}
            var Q109;
            {var subQ0=sQuery(id+"F0.wireOp",EDGE,"E19.rect.right");var subQ1=sQuery(id+"F0.wireOp",EDGE,"E18.rect.top");Q109=makeQuery(id+"F3.opFillet","BLEND_EDGE",EDGE,{"blendedFrom":[makeQuery(id+"F1.opExtrude","SWEPT_EDGE",EDGE,{"disambiguationData":[OSD([subQ1,subQ0])]}),makeQuery(id+"F1.opExtrude","CAP_FACE",FACE,{"disambiguationData":[OSD([sQuery(id+"F0.wireOp",EDGE,"E0"),sQuery(id+"F0.wireOp",EDGE,"E1"),sQuery(id+"F0.wireOp",EDGE,"E2"),sQuery(id+"F0.wireOp",EDGE,"E3"),sQuery(id+"F0.wireOp",EDGE,"E4"),sQuery(id+"F0.wireOp",EDGE,"E5"),sQuery(id+"F0.wireOp",EDGE,"E6"),sQuery(id+"F0.wireOp",EDGE,"E7"),sQuery(id+"F0.wireOp",EDGE,"E8"),sQuery(id+"F0.wireOp",EDGE,"E9"),sQuery(id+"F0.wireOp",EDGE,"E10"),sQuery(id+"F0.wireOp",EDGE,"E11"),sQuery(id+"F0.wireOp",EDGE,"E12"),sQuery(id+"F0.wireOp",EDGE,"E13"),sQuery(id+"F0.wireOp",EDGE,"E14"),sQuery(id+"F0.wireOp",EDGE,"E15"),sQuery(id+"F0.wireOp",EDGE,"E17.rect.bottom"),sQuery(id+"F0.wireOp",EDGE,"E17.rect.top"),sQuery(id+"F0.wireOp",EDGE,"E17.rect.left"),sQuery(id+"F0.wireOp",EDGE,"E17.rect.right"),sQuery(id+"F0.wireOp",EDGE,"E18.rect.bottom"),subQ1,sQuery(id+"F0.wireOp",EDGE,"E18.rect.left"),sQuery(id+"F0.wireOp",EDGE,"E18.rect.right"),sQuery(id+"F0.wireOp",EDGE,"E19.rect.left"),subQ0,sQuery(id+"F0.wireOp",EDGE,"E20.rect.bottom"),sQuery(id+"F0.wireOp",EDGE,"E20.rect.top"),sQuery(id+"F0.wireOp",EDGE,"E23.left"),sQuery(id+"F0.wireOp",EDGE,"E23.right"),sQuery(id+"F0.wireOp",EDGE,"E24.left"),sQuery(id+"F0.wireOp",EDGE,"E24.right"),sQuery(id+"F0.wireOp",EDGE,"E25.left"),sQuery(id+"F0.wireOp",EDGE,"E25.right"),sQuery(id+"F0.wireOp",EDGE,"E26.left"),sQuery(id+"F0.wireOp",EDGE,"E26.right"),sQuery(id+"F0.wireOp",EDGE,"E27.rect.bottom"),sQuery(id+"F0.wireOp",EDGE,"E27.rect.top"),sQuery(id+"F0.wireOp",EDGE,"E27.rect.left"),sQuery(id+"F0.wireOp",EDGE,"E27.rect.right"),sQuery(id+"F0.wireOp",EDGE,"E28.rect.bottom"),sQuery(id+"F0.wireOp",EDGE,"E28.rect.top"),sQuery(id+"F0.wireOp",EDGE,"E28.rect.left"),sQuery(id+"F0.wireOp",EDGE,"E28.rect.right"),sQuery(id+"F0.wireOp",EDGE,"E29.rect.bottom"),sQuery(id+"F0.wireOp",EDGE,"E29.rect.top"),sQuery(id+"F0.wireOp",EDGE,"E29.rect.left"),sQuery(id+"F0.wireOp",EDGE,"E29.rect.right"),sQuery(id+"F0.wireOp",EDGE,"E30.rect.bottom"),sQuery(id+"F0.wireOp",EDGE,"E30.rect.top"),sQuery(id+"F0.wireOp",EDGE,"E30.rect.left"),sQuery(id+"F0.wireOp",EDGE,"E30.rect.right")])],"isStart":true})],"blendedInto":[makeQuery(id+"F1.opExtrude","CAP_FACE",FACE,{"disambiguationData":[OSD([sQuery(id+"F0.wireOp",EDGE,"E0"),sQuery(id+"F0.wireOp",EDGE,"E1"),sQuery(id+"F0.wireOp",EDGE,"E2"),sQuery(id+"F0.wireOp",EDGE,"E3"),sQuery(id+"F0.wireOp",EDGE,"E4"),sQuery(id+"F0.wireOp",EDGE,"E5"),sQuery(id+"F0.wireOp",EDGE,"E6"),sQuery(id+"F0.wireOp",EDGE,"E7"),sQuery(id+"F0.wireOp",EDGE,"E8"),sQuery(id+"F0.wireOp",EDGE,"E9"),sQuery(id+"F0.wireOp",EDGE,"E10"),sQuery(id+"F0.wireOp",EDGE,"E11"),sQuery(id+"F0.wireOp",EDGE,"E12"),sQuery(id+"F0.wireOp",EDGE,"E13"),sQuery(id+"F0.wireOp",EDGE,"E14"),sQuery(id+"F0.wireOp",EDGE,"E15"),sQuery(id+"F0.wireOp",EDGE,"E17.rect.bottom"),sQuery(id+"F0.wireOp",EDGE,"E17.rect.top"),sQuery(id+"F0.wireOp",EDGE,"E17.rect.left"),sQuery(id+"F0.wireOp",EDGE,"E17.rect.right"),sQuery(id+"F0.wireOp",EDGE,"E18.rect.bottom"),subQ1,sQuery(id+"F0.wireOp",EDGE,"E18.rect.left"),sQuery(id+"F0.wireOp",EDGE,"E18.rect.right"),sQuery(id+"F0.wireOp",EDGE,"E19.rect.left"),subQ0,sQuery(id+"F0.wireOp",EDGE,"E20.rect.bottom"),sQuery(id+"F0.wireOp",EDGE,"E20.rect.top"),sQuery(id+"F0.wireOp",EDGE,"E23.left"),sQuery(id+"F0.wireOp",EDGE,"E23.right"),sQuery(id+"F0.wireOp",EDGE,"E24.left"),sQuery(id+"F0.wireOp",EDGE,"E24.right"),sQuery(id+"F0.wireOp",EDGE,"E25.left"),sQuery(id+"F0.wireOp",EDGE,"E25.right"),sQuery(id+"F0.wireOp",EDGE,"E26.left"),sQuery(id+"F0.wireOp",EDGE,"E26.right"),sQuery(id+"F0.wireOp",EDGE,"E27.rect.bottom"),sQuery(id+"F0.wireOp",EDGE,"E27.rect.top"),sQuery(id+"F0.wireOp",EDGE,"E27.rect.left"),sQuery(id+"F0.wireOp",EDGE,"E27.rect.right"),sQuery(id+"F0.wireOp",EDGE,"E28.rect.bottom"),sQuery(id+"F0.wireOp",EDGE,"E28.rect.top"),sQuery(id+"F0.wireOp",EDGE,"E28.rect.left"),sQuery(id+"F0.wireOp",EDGE,"E28.rect.right"),sQuery(id+"F0.wireOp",EDGE,"E29.rect.bottom"),sQuery(id+"F0.wireOp",EDGE,"E29.rect.top"),sQuery(id+"F0.wireOp",EDGE,"E29.rect.left"),sQuery(id+"F0.wireOp",EDGE,"E29.rect.right"),sQuery(id+"F0.wireOp",EDGE,"E30.rect.bottom"),sQuery(id+"F0.wireOp",EDGE,"E30.rect.top"),sQuery(id+"F0.wireOp",EDGE,"E30.rect.left"),sQuery(id+"F0.wireOp",EDGE,"E30.rect.right")])],"isStart":true})]});}
            var Q110;
            {var subQ0=sQuery(id+"F0.wireOp",EDGE,"E19.rect.right");var subQ1=sQuery(id+"F0.wireOp",EDGE,"E18.rect.top");Q110=makeQuery(id+"F3.opFillet","BLEND_EDGE",EDGE,{"blendedFrom":[makeQuery(id+"F1.opExtrude","SWEPT_EDGE",EDGE,{"disambiguationData":[OSD([subQ1,subQ0])]}),makeQuery(id+"F1.opExtrude","CAP_FACE",FACE,{"disambiguationData":[OSD([sQuery(id+"F0.wireOp",EDGE,"E0"),sQuery(id+"F0.wireOp",EDGE,"E1"),sQuery(id+"F0.wireOp",EDGE,"E2"),sQuery(id+"F0.wireOp",EDGE,"E3"),sQuery(id+"F0.wireOp",EDGE,"E4"),sQuery(id+"F0.wireOp",EDGE,"E5"),sQuery(id+"F0.wireOp",EDGE,"E6"),sQuery(id+"F0.wireOp",EDGE,"E7"),sQuery(id+"F0.wireOp",EDGE,"E8"),sQuery(id+"F0.wireOp",EDGE,"E9"),sQuery(id+"F0.wireOp",EDGE,"E10"),sQuery(id+"F0.wireOp",EDGE,"E11"),sQuery(id+"F0.wireOp",EDGE,"E12"),sQuery(id+"F0.wireOp",EDGE,"E13"),sQuery(id+"F0.wireOp",EDGE,"E14"),sQuery(id+"F0.wireOp",EDGE,"E15"),sQuery(id+"F0.wireOp",EDGE,"E17.rect.bottom"),sQuery(id+"F0.wireOp",EDGE,"E17.rect.top"),sQuery(id+"F0.wireOp",EDGE,"E17.rect.left"),sQuery(id+"F0.wireOp",EDGE,"E17.rect.right"),sQuery(id+"F0.wireOp",EDGE,"E18.rect.bottom"),subQ1,sQuery(id+"F0.wireOp",EDGE,"E18.rect.left"),sQuery(id+"F0.wireOp",EDGE,"E18.rect.right"),sQuery(id+"F0.wireOp",EDGE,"E19.rect.left"),subQ0,sQuery(id+"F0.wireOp",EDGE,"E20.rect.bottom"),sQuery(id+"F0.wireOp",EDGE,"E20.rect.top"),sQuery(id+"F0.wireOp",EDGE,"E23.left"),sQuery(id+"F0.wireOp",EDGE,"E23.right"),sQuery(id+"F0.wireOp",EDGE,"E24.left"),sQuery(id+"F0.wireOp",EDGE,"E24.right"),sQuery(id+"F0.wireOp",EDGE,"E25.left"),sQuery(id+"F0.wireOp",EDGE,"E25.right"),sQuery(id+"F0.wireOp",EDGE,"E26.left"),sQuery(id+"F0.wireOp",EDGE,"E26.right"),sQuery(id+"F0.wireOp",EDGE,"E27.rect.bottom"),sQuery(id+"F0.wireOp",EDGE,"E27.rect.top"),sQuery(id+"F0.wireOp",EDGE,"E27.rect.left"),sQuery(id+"F0.wireOp",EDGE,"E27.rect.right"),sQuery(id+"F0.wireOp",EDGE,"E28.rect.bottom"),sQuery(id+"F0.wireOp",EDGE,"E28.rect.top"),sQuery(id+"F0.wireOp",EDGE,"E28.rect.left"),sQuery(id+"F0.wireOp",EDGE,"E28.rect.right"),sQuery(id+"F0.wireOp",EDGE,"E29.rect.bottom"),sQuery(id+"F0.wireOp",EDGE,"E29.rect.top"),sQuery(id+"F0.wireOp",EDGE,"E29.rect.left"),sQuery(id+"F0.wireOp",EDGE,"E29.rect.right"),sQuery(id+"F0.wireOp",EDGE,"E30.rect.bottom"),sQuery(id+"F0.wireOp",EDGE,"E30.rect.top"),sQuery(id+"F0.wireOp",EDGE,"E30.rect.left"),sQuery(id+"F0.wireOp",EDGE,"E30.rect.right")])],"isStart":false})],"blendedInto":[makeQuery(id+"F1.opExtrude","CAP_FACE",FACE,{"disambiguationData":[OSD([sQuery(id+"F0.wireOp",EDGE,"E0"),sQuery(id+"F0.wireOp",EDGE,"E1"),sQuery(id+"F0.wireOp",EDGE,"E2"),sQuery(id+"F0.wireOp",EDGE,"E3"),sQuery(id+"F0.wireOp",EDGE,"E4"),sQuery(id+"F0.wireOp",EDGE,"E5"),sQuery(id+"F0.wireOp",EDGE,"E6"),sQuery(id+"F0.wireOp",EDGE,"E7"),sQuery(id+"F0.wireOp",EDGE,"E8"),sQuery(id+"F0.wireOp",EDGE,"E9"),sQuery(id+"F0.wireOp",EDGE,"E10"),sQuery(id+"F0.wireOp",EDGE,"E11"),sQuery(id+"F0.wireOp",EDGE,"E12"),sQuery(id+"F0.wireOp",EDGE,"E13"),sQuery(id+"F0.wireOp",EDGE,"E14"),sQuery(id+"F0.wireOp",EDGE,"E15"),sQuery(id+"F0.wireOp",EDGE,"E17.rect.bottom"),sQuery(id+"F0.wireOp",EDGE,"E17.rect.top"),sQuery(id+"F0.wireOp",EDGE,"E17.rect.left"),sQuery(id+"F0.wireOp",EDGE,"E17.rect.right"),sQuery(id+"F0.wireOp",EDGE,"E18.rect.bottom"),subQ1,sQuery(id+"F0.wireOp",EDGE,"E18.rect.left"),sQuery(id+"F0.wireOp",EDGE,"E18.rect.right"),sQuery(id+"F0.wireOp",EDGE,"E19.rect.left"),subQ0,sQuery(id+"F0.wireOp",EDGE,"E20.rect.bottom"),sQuery(id+"F0.wireOp",EDGE,"E20.rect.top"),sQuery(id+"F0.wireOp",EDGE,"E23.left"),sQuery(id+"F0.wireOp",EDGE,"E23.right"),sQuery(id+"F0.wireOp",EDGE,"E24.left"),sQuery(id+"F0.wireOp",EDGE,"E24.right"),sQuery(id+"F0.wireOp",EDGE,"E25.left"),sQuery(id+"F0.wireOp",EDGE,"E25.right"),sQuery(id+"F0.wireOp",EDGE,"E26.left"),sQuery(id+"F0.wireOp",EDGE,"E26.right"),sQuery(id+"F0.wireOp",EDGE,"E27.rect.bottom"),sQuery(id+"F0.wireOp",EDGE,"E27.rect.top"),sQuery(id+"F0.wireOp",EDGE,"E27.rect.left"),sQuery(id+"F0.wireOp",EDGE,"E27.rect.right"),sQuery(id+"F0.wireOp",EDGE,"E28.rect.bottom"),sQuery(id+"F0.wireOp",EDGE,"E28.rect.top"),sQuery(id+"F0.wireOp",EDGE,"E28.rect.left"),sQuery(id+"F0.wireOp",EDGE,"E28.rect.right"),sQuery(id+"F0.wireOp",EDGE,"E29.rect.bottom"),sQuery(id+"F0.wireOp",EDGE,"E29.rect.top"),sQuery(id+"F0.wireOp",EDGE,"E29.rect.left"),sQuery(id+"F0.wireOp",EDGE,"E29.rect.right"),sQuery(id+"F0.wireOp",EDGE,"E30.rect.bottom"),sQuery(id+"F0.wireOp",EDGE,"E30.rect.top"),sQuery(id+"F0.wireOp",EDGE,"E30.rect.left"),sQuery(id+"F0.wireOp",EDGE,"E30.rect.right")])],"isStart":false})]});}
            var Q111;
            {var subQ0=sQuery(id+"F0.wireOp",EDGE,"E19.rect.right");var subQ2=makeQuery(id+"F0.imprint","INTERSECT",VERTEX,{"derivedFrom":[subQ0,sQuery(id+"F0.wireOp",EDGE,"E20.rect.bottom")]});Q111=makeQuery(id+"F1.opExtrude","CAP_EDGE",EDGE,{"disambiguationData":[OSD([subQ0]),TDD([makeQuery(id+"F0.imprint","IMPRINT",EDGE,{"disambiguationData":[TD([[makeQuery(id+"F0.imprint","INTERSECT",VERTEX,{"derivedFrom":[sQuery(id+"F0.wireOp",EDGE,"E18.rect.bottom"),subQ0]}),-1.0]])],"derivedFrom":subQ0}),makeQuery(id+"F0.imprint","IMPRINT",EDGE,{"disambiguationData":[TD([[subQ2,-1.0]])],"derivedFrom":subQ0}),makeQuery(id+"F0.imprint","IMPRINT",EDGE,{"disambiguationData":[TD([[makeQuery(id+"F0.imprint","INTERSECT",VERTEX,{"derivedFrom":[sQuery(id+"F0.wireOp",EDGE,"E18.rect.top"),subQ0]}),1.0]])],"derivedFrom":subQ0})])],"isStart":false});}
            var Q112;
            {var subQ0=sQuery(id+"F0.wireOp",EDGE,"E19.rect.right");var subQ1=sQuery(id+"F0.wireOp",EDGE,"E18.rect.bottom");Q112=makeQuery(id+"F3.opFillet","BLEND_EDGE",EDGE,{"blendedFrom":[makeQuery(id+"F1.opExtrude","SWEPT_EDGE",EDGE,{"disambiguationData":[OSD([subQ1,subQ0])]}),makeQuery(id+"F1.opExtrude","CAP_FACE",FACE,{"disambiguationData":[OSD([sQuery(id+"F0.wireOp",EDGE,"E0"),sQuery(id+"F0.wireOp",EDGE,"E1"),sQuery(id+"F0.wireOp",EDGE,"E2"),sQuery(id+"F0.wireOp",EDGE,"E3"),sQuery(id+"F0.wireOp",EDGE,"E4"),sQuery(id+"F0.wireOp",EDGE,"E5"),sQuery(id+"F0.wireOp",EDGE,"E6"),sQuery(id+"F0.wireOp",EDGE,"E7"),sQuery(id+"F0.wireOp",EDGE,"E8"),sQuery(id+"F0.wireOp",EDGE,"E9"),sQuery(id+"F0.wireOp",EDGE,"E10"),sQuery(id+"F0.wireOp",EDGE,"E11"),sQuery(id+"F0.wireOp",EDGE,"E12"),sQuery(id+"F0.wireOp",EDGE,"E13"),sQuery(id+"F0.wireOp",EDGE,"E14"),sQuery(id+"F0.wireOp",EDGE,"E15"),sQuery(id+"F0.wireOp",EDGE,"E17.rect.bottom"),sQuery(id+"F0.wireOp",EDGE,"E17.rect.top"),sQuery(id+"F0.wireOp",EDGE,"E17.rect.left"),sQuery(id+"F0.wireOp",EDGE,"E17.rect.right"),subQ1,sQuery(id+"F0.wireOp",EDGE,"E18.rect.top"),sQuery(id+"F0.wireOp",EDGE,"E18.rect.left"),sQuery(id+"F0.wireOp",EDGE,"E18.rect.right"),sQuery(id+"F0.wireOp",EDGE,"E19.rect.left"),subQ0,sQuery(id+"F0.wireOp",EDGE,"E20.rect.bottom"),sQuery(id+"F0.wireOp",EDGE,"E20.rect.top"),sQuery(id+"F0.wireOp",EDGE,"E23.left"),sQuery(id+"F0.wireOp",EDGE,"E23.right"),sQuery(id+"F0.wireOp",EDGE,"E24.left"),sQuery(id+"F0.wireOp",EDGE,"E24.right"),sQuery(id+"F0.wireOp",EDGE,"E25.left"),sQuery(id+"F0.wireOp",EDGE,"E25.right"),sQuery(id+"F0.wireOp",EDGE,"E26.left"),sQuery(id+"F0.wireOp",EDGE,"E26.right"),sQuery(id+"F0.wireOp",EDGE,"E27.rect.bottom"),sQuery(id+"F0.wireOp",EDGE,"E27.rect.top"),sQuery(id+"F0.wireOp",EDGE,"E27.rect.left"),sQuery(id+"F0.wireOp",EDGE,"E27.rect.right"),sQuery(id+"F0.wireOp",EDGE,"E28.rect.bottom"),sQuery(id+"F0.wireOp",EDGE,"E28.rect.top"),sQuery(id+"F0.wireOp",EDGE,"E28.rect.left"),sQuery(id+"F0.wireOp",EDGE,"E28.rect.right"),sQuery(id+"F0.wireOp",EDGE,"E29.rect.bottom"),sQuery(id+"F0.wireOp",EDGE,"E29.rect.top"),sQuery(id+"F0.wireOp",EDGE,"E29.rect.left"),sQuery(id+"F0.wireOp",EDGE,"E29.rect.right"),sQuery(id+"F0.wireOp",EDGE,"E30.rect.bottom"),sQuery(id+"F0.wireOp",EDGE,"E30.rect.top"),sQuery(id+"F0.wireOp",EDGE,"E30.rect.left"),sQuery(id+"F0.wireOp",EDGE,"E30.rect.right")])],"isStart":false})],"blendedInto":[makeQuery(id+"F1.opExtrude","CAP_FACE",FACE,{"disambiguationData":[OSD([sQuery(id+"F0.wireOp",EDGE,"E0"),sQuery(id+"F0.wireOp",EDGE,"E1"),sQuery(id+"F0.wireOp",EDGE,"E2"),sQuery(id+"F0.wireOp",EDGE,"E3"),sQuery(id+"F0.wireOp",EDGE,"E4"),sQuery(id+"F0.wireOp",EDGE,"E5"),sQuery(id+"F0.wireOp",EDGE,"E6"),sQuery(id+"F0.wireOp",EDGE,"E7"),sQuery(id+"F0.wireOp",EDGE,"E8"),sQuery(id+"F0.wireOp",EDGE,"E9"),sQuery(id+"F0.wireOp",EDGE,"E10"),sQuery(id+"F0.wireOp",EDGE,"E11"),sQuery(id+"F0.wireOp",EDGE,"E12"),sQuery(id+"F0.wireOp",EDGE,"E13"),sQuery(id+"F0.wireOp",EDGE,"E14"),sQuery(id+"F0.wireOp",EDGE,"E15"),sQuery(id+"F0.wireOp",EDGE,"E17.rect.bottom"),sQuery(id+"F0.wireOp",EDGE,"E17.rect.top"),sQuery(id+"F0.wireOp",EDGE,"E17.rect.left"),sQuery(id+"F0.wireOp",EDGE,"E17.rect.right"),subQ1,sQuery(id+"F0.wireOp",EDGE,"E18.rect.top"),sQuery(id+"F0.wireOp",EDGE,"E18.rect.left"),sQuery(id+"F0.wireOp",EDGE,"E18.rect.right"),sQuery(id+"F0.wireOp",EDGE,"E19.rect.left"),subQ0,sQuery(id+"F0.wireOp",EDGE,"E20.rect.bottom"),sQuery(id+"F0.wireOp",EDGE,"E20.rect.top"),sQuery(id+"F0.wireOp",EDGE,"E23.left"),sQuery(id+"F0.wireOp",EDGE,"E23.right"),sQuery(id+"F0.wireOp",EDGE,"E24.left"),sQuery(id+"F0.wireOp",EDGE,"E24.right"),sQuery(id+"F0.wireOp",EDGE,"E25.left"),sQuery(id+"F0.wireOp",EDGE,"E25.right"),sQuery(id+"F0.wireOp",EDGE,"E26.left"),sQuery(id+"F0.wireOp",EDGE,"E26.right"),sQuery(id+"F0.wireOp",EDGE,"E27.rect.bottom"),sQuery(id+"F0.wireOp",EDGE,"E27.rect.top"),sQuery(id+"F0.wireOp",EDGE,"E27.rect.left"),sQuery(id+"F0.wireOp",EDGE,"E27.rect.right"),sQuery(id+"F0.wireOp",EDGE,"E28.rect.bottom"),sQuery(id+"F0.wireOp",EDGE,"E28.rect.top"),sQuery(id+"F0.wireOp",EDGE,"E28.rect.left"),sQuery(id+"F0.wireOp",EDGE,"E28.rect.right"),sQuery(id+"F0.wireOp",EDGE,"E29.rect.bottom"),sQuery(id+"F0.wireOp",EDGE,"E29.rect.top"),sQuery(id+"F0.wireOp",EDGE,"E29.rect.left"),sQuery(id+"F0.wireOp",EDGE,"E29.rect.right"),sQuery(id+"F0.wireOp",EDGE,"E30.rect.bottom"),sQuery(id+"F0.wireOp",EDGE,"E30.rect.top"),sQuery(id+"F0.wireOp",EDGE,"E30.rect.left"),sQuery(id+"F0.wireOp",EDGE,"E30.rect.right")])],"isStart":false})]});}
            var Q113;
            {var subQ0=sQuery(id+"F0.wireOp",EDGE,"E19.rect.left");var subQ2=makeQuery(id+"F0.imprint","INTERSECT",VERTEX,{"derivedFrom":[subQ0,sQuery(id+"F0.wireOp",EDGE,"E20.rect.bottom")]});Q113=makeQuery(id+"F1.opExtrude","CAP_EDGE",EDGE,{"disambiguationData":[OSD([subQ0]),TDD([makeQuery(id+"F0.imprint","IMPRINT",EDGE,{"disambiguationData":[TD([[makeQuery(id+"F0.imprint","INTERSECT",VERTEX,{"derivedFrom":[sQuery(id+"F0.wireOp",EDGE,"E18.rect.bottom"),subQ0]}),-1.0]])],"derivedFrom":subQ0}),makeQuery(id+"F0.imprint","IMPRINT",EDGE,{"disambiguationData":[TD([[subQ2,-1.0]])],"derivedFrom":subQ0}),makeQuery(id+"F0.imprint","IMPRINT",EDGE,{"disambiguationData":[TD([[makeQuery(id+"F0.imprint","INTERSECT",VERTEX,{"derivedFrom":[sQuery(id+"F0.wireOp",EDGE,"E18.rect.top"),subQ0]}),1.0]])],"derivedFrom":subQ0})])],"isStart":false});}
            var Q114;
            {var subQ0=sQuery(id+"F0.wireOp",EDGE,"E19.rect.left");var subQ1=sQuery(id+"F0.wireOp",EDGE,"E18.rect.bottom");Q114=makeQuery(id+"F3.opFillet","BLEND_EDGE",EDGE,{"blendedFrom":[makeQuery(id+"F1.opExtrude","SWEPT_EDGE",EDGE,{"disambiguationData":[OSD([subQ1,subQ0])]}),makeQuery(id+"F1.opExtrude","CAP_FACE",FACE,{"disambiguationData":[OSD([sQuery(id+"F0.wireOp",EDGE,"E0"),sQuery(id+"F0.wireOp",EDGE,"E1"),sQuery(id+"F0.wireOp",EDGE,"E2"),sQuery(id+"F0.wireOp",EDGE,"E3"),sQuery(id+"F0.wireOp",EDGE,"E4"),sQuery(id+"F0.wireOp",EDGE,"E5"),sQuery(id+"F0.wireOp",EDGE,"E6"),sQuery(id+"F0.wireOp",EDGE,"E7"),sQuery(id+"F0.wireOp",EDGE,"E8"),sQuery(id+"F0.wireOp",EDGE,"E9"),sQuery(id+"F0.wireOp",EDGE,"E10"),sQuery(id+"F0.wireOp",EDGE,"E11"),sQuery(id+"F0.wireOp",EDGE,"E12"),sQuery(id+"F0.wireOp",EDGE,"E13"),sQuery(id+"F0.wireOp",EDGE,"E14"),sQuery(id+"F0.wireOp",EDGE,"E15"),sQuery(id+"F0.wireOp",EDGE,"E17.rect.bottom"),sQuery(id+"F0.wireOp",EDGE,"E17.rect.top"),sQuery(id+"F0.wireOp",EDGE,"E17.rect.left"),sQuery(id+"F0.wireOp",EDGE,"E17.rect.right"),subQ1,sQuery(id+"F0.wireOp",EDGE,"E18.rect.top"),sQuery(id+"F0.wireOp",EDGE,"E18.rect.left"),sQuery(id+"F0.wireOp",EDGE,"E18.rect.right"),subQ0,sQuery(id+"F0.wireOp",EDGE,"E19.rect.right"),sQuery(id+"F0.wireOp",EDGE,"E20.rect.bottom"),sQuery(id+"F0.wireOp",EDGE,"E20.rect.top"),sQuery(id+"F0.wireOp",EDGE,"E23.left"),sQuery(id+"F0.wireOp",EDGE,"E23.right"),sQuery(id+"F0.wireOp",EDGE,"E24.left"),sQuery(id+"F0.wireOp",EDGE,"E24.right"),sQuery(id+"F0.wireOp",EDGE,"E25.left"),sQuery(id+"F0.wireOp",EDGE,"E25.right"),sQuery(id+"F0.wireOp",EDGE,"E26.left"),sQuery(id+"F0.wireOp",EDGE,"E26.right"),sQuery(id+"F0.wireOp",EDGE,"E27.rect.bottom"),sQuery(id+"F0.wireOp",EDGE,"E27.rect.top"),sQuery(id+"F0.wireOp",EDGE,"E27.rect.left"),sQuery(id+"F0.wireOp",EDGE,"E27.rect.right"),sQuery(id+"F0.wireOp",EDGE,"E28.rect.bottom"),sQuery(id+"F0.wireOp",EDGE,"E28.rect.top"),sQuery(id+"F0.wireOp",EDGE,"E28.rect.left"),sQuery(id+"F0.wireOp",EDGE,"E28.rect.right"),sQuery(id+"F0.wireOp",EDGE,"E29.rect.bottom"),sQuery(id+"F0.wireOp",EDGE,"E29.rect.top"),sQuery(id+"F0.wireOp",EDGE,"E29.rect.left"),sQuery(id+"F0.wireOp",EDGE,"E29.rect.right"),sQuery(id+"F0.wireOp",EDGE,"E30.rect.bottom"),sQuery(id+"F0.wireOp",EDGE,"E30.rect.top"),sQuery(id+"F0.wireOp",EDGE,"E30.rect.left"),sQuery(id+"F0.wireOp",EDGE,"E30.rect.right")])],"isStart":false})],"blendedInto":[makeQuery(id+"F1.opExtrude","CAP_FACE",FACE,{"disambiguationData":[OSD([sQuery(id+"F0.wireOp",EDGE,"E0"),sQuery(id+"F0.wireOp",EDGE,"E1"),sQuery(id+"F0.wireOp",EDGE,"E2"),sQuery(id+"F0.wireOp",EDGE,"E3"),sQuery(id+"F0.wireOp",EDGE,"E4"),sQuery(id+"F0.wireOp",EDGE,"E5"),sQuery(id+"F0.wireOp",EDGE,"E6"),sQuery(id+"F0.wireOp",EDGE,"E7"),sQuery(id+"F0.wireOp",EDGE,"E8"),sQuery(id+"F0.wireOp",EDGE,"E9"),sQuery(id+"F0.wireOp",EDGE,"E10"),sQuery(id+"F0.wireOp",EDGE,"E11"),sQuery(id+"F0.wireOp",EDGE,"E12"),sQuery(id+"F0.wireOp",EDGE,"E13"),sQuery(id+"F0.wireOp",EDGE,"E14"),sQuery(id+"F0.wireOp",EDGE,"E15"),sQuery(id+"F0.wireOp",EDGE,"E17.rect.bottom"),sQuery(id+"F0.wireOp",EDGE,"E17.rect.top"),sQuery(id+"F0.wireOp",EDGE,"E17.rect.left"),sQuery(id+"F0.wireOp",EDGE,"E17.rect.right"),subQ1,sQuery(id+"F0.wireOp",EDGE,"E18.rect.top"),sQuery(id+"F0.wireOp",EDGE,"E18.rect.left"),sQuery(id+"F0.wireOp",EDGE,"E18.rect.right"),subQ0,sQuery(id+"F0.wireOp",EDGE,"E19.rect.right"),sQuery(id+"F0.wireOp",EDGE,"E20.rect.bottom"),sQuery(id+"F0.wireOp",EDGE,"E20.rect.top"),sQuery(id+"F0.wireOp",EDGE,"E23.left"),sQuery(id+"F0.wireOp",EDGE,"E23.right"),sQuery(id+"F0.wireOp",EDGE,"E24.left"),sQuery(id+"F0.wireOp",EDGE,"E24.right"),sQuery(id+"F0.wireOp",EDGE,"E25.left"),sQuery(id+"F0.wireOp",EDGE,"E25.right"),sQuery(id+"F0.wireOp",EDGE,"E26.left"),sQuery(id+"F0.wireOp",EDGE,"E26.right"),sQuery(id+"F0.wireOp",EDGE,"E27.rect.bottom"),sQuery(id+"F0.wireOp",EDGE,"E27.rect.top"),sQuery(id+"F0.wireOp",EDGE,"E27.rect.left"),sQuery(id+"F0.wireOp",EDGE,"E27.rect.right"),sQuery(id+"F0.wireOp",EDGE,"E28.rect.bottom"),sQuery(id+"F0.wireOp",EDGE,"E28.rect.top"),sQuery(id+"F0.wireOp",EDGE,"E28.rect.left"),sQuery(id+"F0.wireOp",EDGE,"E28.rect.right"),sQuery(id+"F0.wireOp",EDGE,"E29.rect.bottom"),sQuery(id+"F0.wireOp",EDGE,"E29.rect.top"),sQuery(id+"F0.wireOp",EDGE,"E29.rect.left"),sQuery(id+"F0.wireOp",EDGE,"E29.rect.right"),sQuery(id+"F0.wireOp",EDGE,"E30.rect.bottom"),sQuery(id+"F0.wireOp",EDGE,"E30.rect.top"),sQuery(id+"F0.wireOp",EDGE,"E30.rect.left"),sQuery(id+"F0.wireOp",EDGE,"E30.rect.right")])],"isStart":false})]});}
            var Q115;
            {var subQ0=sQuery(id+"F0.wireOp",EDGE,"E19.rect.left");var subQ1=sQuery(id+"F0.wireOp",EDGE,"E18.rect.top");Q115=makeQuery(id+"F3.opFillet","BLEND_EDGE",EDGE,{"blendedFrom":[makeQuery(id+"F1.opExtrude","SWEPT_EDGE",EDGE,{"disambiguationData":[OSD([subQ1,subQ0])]}),makeQuery(id+"F1.opExtrude","CAP_FACE",FACE,{"disambiguationData":[OSD([sQuery(id+"F0.wireOp",EDGE,"E0"),sQuery(id+"F0.wireOp",EDGE,"E1"),sQuery(id+"F0.wireOp",EDGE,"E2"),sQuery(id+"F0.wireOp",EDGE,"E3"),sQuery(id+"F0.wireOp",EDGE,"E4"),sQuery(id+"F0.wireOp",EDGE,"E5"),sQuery(id+"F0.wireOp",EDGE,"E6"),sQuery(id+"F0.wireOp",EDGE,"E7"),sQuery(id+"F0.wireOp",EDGE,"E8"),sQuery(id+"F0.wireOp",EDGE,"E9"),sQuery(id+"F0.wireOp",EDGE,"E10"),sQuery(id+"F0.wireOp",EDGE,"E11"),sQuery(id+"F0.wireOp",EDGE,"E12"),sQuery(id+"F0.wireOp",EDGE,"E13"),sQuery(id+"F0.wireOp",EDGE,"E14"),sQuery(id+"F0.wireOp",EDGE,"E15"),sQuery(id+"F0.wireOp",EDGE,"E17.rect.bottom"),sQuery(id+"F0.wireOp",EDGE,"E17.rect.top"),sQuery(id+"F0.wireOp",EDGE,"E17.rect.left"),sQuery(id+"F0.wireOp",EDGE,"E17.rect.right"),sQuery(id+"F0.wireOp",EDGE,"E18.rect.bottom"),subQ1,sQuery(id+"F0.wireOp",EDGE,"E18.rect.left"),sQuery(id+"F0.wireOp",EDGE,"E18.rect.right"),subQ0,sQuery(id+"F0.wireOp",EDGE,"E19.rect.right"),sQuery(id+"F0.wireOp",EDGE,"E20.rect.bottom"),sQuery(id+"F0.wireOp",EDGE,"E20.rect.top"),sQuery(id+"F0.wireOp",EDGE,"E23.left"),sQuery(id+"F0.wireOp",EDGE,"E23.right"),sQuery(id+"F0.wireOp",EDGE,"E24.left"),sQuery(id+"F0.wireOp",EDGE,"E24.right"),sQuery(id+"F0.wireOp",EDGE,"E25.left"),sQuery(id+"F0.wireOp",EDGE,"E25.right"),sQuery(id+"F0.wireOp",EDGE,"E26.left"),sQuery(id+"F0.wireOp",EDGE,"E26.right"),sQuery(id+"F0.wireOp",EDGE,"E27.rect.bottom"),sQuery(id+"F0.wireOp",EDGE,"E27.rect.top"),sQuery(id+"F0.wireOp",EDGE,"E27.rect.left"),sQuery(id+"F0.wireOp",EDGE,"E27.rect.right"),sQuery(id+"F0.wireOp",EDGE,"E28.rect.bottom"),sQuery(id+"F0.wireOp",EDGE,"E28.rect.top"),sQuery(id+"F0.wireOp",EDGE,"E28.rect.left"),sQuery(id+"F0.wireOp",EDGE,"E28.rect.right"),sQuery(id+"F0.wireOp",EDGE,"E29.rect.bottom"),sQuery(id+"F0.wireOp",EDGE,"E29.rect.top"),sQuery(id+"F0.wireOp",EDGE,"E29.rect.left"),sQuery(id+"F0.wireOp",EDGE,"E29.rect.right"),sQuery(id+"F0.wireOp",EDGE,"E30.rect.bottom"),sQuery(id+"F0.wireOp",EDGE,"E30.rect.top"),sQuery(id+"F0.wireOp",EDGE,"E30.rect.left"),sQuery(id+"F0.wireOp",EDGE,"E30.rect.right")])],"isStart":false})],"blendedInto":[makeQuery(id+"F1.opExtrude","CAP_FACE",FACE,{"disambiguationData":[OSD([sQuery(id+"F0.wireOp",EDGE,"E0"),sQuery(id+"F0.wireOp",EDGE,"E1"),sQuery(id+"F0.wireOp",EDGE,"E2"),sQuery(id+"F0.wireOp",EDGE,"E3"),sQuery(id+"F0.wireOp",EDGE,"E4"),sQuery(id+"F0.wireOp",EDGE,"E5"),sQuery(id+"F0.wireOp",EDGE,"E6"),sQuery(id+"F0.wireOp",EDGE,"E7"),sQuery(id+"F0.wireOp",EDGE,"E8"),sQuery(id+"F0.wireOp",EDGE,"E9"),sQuery(id+"F0.wireOp",EDGE,"E10"),sQuery(id+"F0.wireOp",EDGE,"E11"),sQuery(id+"F0.wireOp",EDGE,"E12"),sQuery(id+"F0.wireOp",EDGE,"E13"),sQuery(id+"F0.wireOp",EDGE,"E14"),sQuery(id+"F0.wireOp",EDGE,"E15"),sQuery(id+"F0.wireOp",EDGE,"E17.rect.bottom"),sQuery(id+"F0.wireOp",EDGE,"E17.rect.top"),sQuery(id+"F0.wireOp",EDGE,"E17.rect.left"),sQuery(id+"F0.wireOp",EDGE,"E17.rect.right"),sQuery(id+"F0.wireOp",EDGE,"E18.rect.bottom"),subQ1,sQuery(id+"F0.wireOp",EDGE,"E18.rect.left"),sQuery(id+"F0.wireOp",EDGE,"E18.rect.right"),subQ0,sQuery(id+"F0.wireOp",EDGE,"E19.rect.right"),sQuery(id+"F0.wireOp",EDGE,"E20.rect.bottom"),sQuery(id+"F0.wireOp",EDGE,"E20.rect.top"),sQuery(id+"F0.wireOp",EDGE,"E23.left"),sQuery(id+"F0.wireOp",EDGE,"E23.right"),sQuery(id+"F0.wireOp",EDGE,"E24.left"),sQuery(id+"F0.wireOp",EDGE,"E24.right"),sQuery(id+"F0.wireOp",EDGE,"E25.left"),sQuery(id+"F0.wireOp",EDGE,"E25.right"),sQuery(id+"F0.wireOp",EDGE,"E26.left"),sQuery(id+"F0.wireOp",EDGE,"E26.right"),sQuery(id+"F0.wireOp",EDGE,"E27.rect.bottom"),sQuery(id+"F0.wireOp",EDGE,"E27.rect.top"),sQuery(id+"F0.wireOp",EDGE,"E27.rect.left"),sQuery(id+"F0.wireOp",EDGE,"E27.rect.right"),sQuery(id+"F0.wireOp",EDGE,"E28.rect.bottom"),sQuery(id+"F0.wireOp",EDGE,"E28.rect.top"),sQuery(id+"F0.wireOp",EDGE,"E28.rect.left"),sQuery(id+"F0.wireOp",EDGE,"E28.rect.right"),sQuery(id+"F0.wireOp",EDGE,"E29.rect.bottom"),sQuery(id+"F0.wireOp",EDGE,"E29.rect.top"),sQuery(id+"F0.wireOp",EDGE,"E29.rect.left"),sQuery(id+"F0.wireOp",EDGE,"E29.rect.right"),sQuery(id+"F0.wireOp",EDGE,"E30.rect.bottom"),sQuery(id+"F0.wireOp",EDGE,"E30.rect.top"),sQuery(id+"F0.wireOp",EDGE,"E30.rect.left"),sQuery(id+"F0.wireOp",EDGE,"E30.rect.right")])],"isStart":false})]});}
            fillet(context, id + "F4", {"entities" : qUnion([Q0, Q1, Q2, Q3, Q4, Q5, Q6, Q7, Q8, Q9, Q10, Q11, Q12, Q13, Q14, Q15, Q16, Q17, Q18, Q19, Q20, Q21, Q22, Q23, Q24, Q25, Q26, Q27, Q28, Q29, Q30, Q31, Q32, Q33, Q34, Q35, Q36, Q37, Q38, Q39, Q40, Q41, Q42, Q43, Q44, Q45, Q46, Q47, Q48, Q49, Q50, Q51, Q52, Q53, Q54, Q55, Q56, Q57, Q58, Q59, Q60, Q61, Q62, Q63, Q64, Q65, Q66, Q67, Q68, Q69, Q70, Q71, Q72, Q73, Q74, Q75, Q76, Q77, Q78, Q79, Q80, Q81, Q82, Q83, Q84, Q85, Q86, Q87, Q88, Q89, Q90, Q91, Q92, Q93, Q94, Q95, Q96, Q97, Q98, Q99, Q100, Q101, Q102, Q103, Q104, Q105, Q106, Q107, Q108, Q109, Q110, Q111, Q112, Q113, Q114, Q115]), "radius" : 0.76 * mm, "allowEdgeOverflow" : false});
        }
        {
            var Q0;
            Q0=makeQuery(id+"F1.opExtrude","CAP_EDGE",EDGE,{"disambiguationData":[OSD([sQuery(id+"F0.wireOp",EDGE,"E27.rect.right")])],"isStart":true});
            var Q1;
            Q1=makeQuery(id+"F1.opExtrude","CAP_EDGE",EDGE,{"disambiguationData":[OSD([sQuery(id+"F0.wireOp",EDGE,"E27.rect.bottom")])],"isStart":true});
            var Q2;
            Q2=makeQuery(id+"F1.opExtrude","CAP_EDGE",EDGE,{"disambiguationData":[OSD([sQuery(id+"F0.wireOp",EDGE,"E27.rect.left")])],"isStart":true});
            var Q3;
            {var subQ0=sQuery(id+"F0.wireOp",EDGE,"E27.rect.top");Q3=makeQuery(id+"F1.opExtrude","CAP_EDGE",EDGE,{"disambiguationData":[OSD([subQ0]),TDD([makeQuery(id+"F0.imprint","IMPRINT",EDGE,{"disambiguationData":[TD([[makeQuery(id+"F0.imprint","INTERSECT",VERTEX,{"derivedFrom":[subQ0,sQuery(id+"F0.wireOp",EDGE,"E27.rect.left")]}),-1.0]])],"derivedFrom":subQ0})])],"isStart":true});}
            var Q4;
            {var subQ0=sQuery(id+"F0.wireOp",EDGE,"E27.rect.top");Q4=makeQuery(id+"F1.opExtrude","CAP_EDGE",EDGE,{"disambiguationData":[OSD([subQ0]),TDD([makeQuery(id+"F0.imprint","IMPRINT",EDGE,{"disambiguationData":[TD([[makeQuery(id+"F0.imprint","INTERSECT",VERTEX,{"derivedFrom":[subQ0,sQuery(id+"F0.wireOp",EDGE,"E27.rect.right")]}),1.0]])],"derivedFrom":subQ0})])],"isStart":true});}
            var Q5;
            Q5=makeQuery(id+"F1.opExtrude","SWEPT_EDGE",EDGE,{"disambiguationData":[OSD([sQuery(id+"F0.wireOp",EDGE,"E27.rect.bottom"),sQuery(id+"F0.wireOp",EDGE,"E27.rect.right")])]});
            var Q6;
            Q6=makeQuery(id+"F1.opExtrude","SWEPT_EDGE",EDGE,{"disambiguationData":[OSD([sQuery(id+"F0.wireOp",EDGE,"E27.rect.top"),sQuery(id+"F0.wireOp",EDGE,"E27.rect.right")])]});
            var Q7;
            Q7=makeQuery(id+"F1.opExtrude","CAP_EDGE",EDGE,{"disambiguationData":[OSD([sQuery(id+"F0.wireOp",EDGE,"E27.rect.right")])],"isStart":false});
            var Q8;
            Q8=makeQuery(id+"F1.opExtrude","CAP_EDGE",EDGE,{"disambiguationData":[OSD([sQuery(id+"F0.wireOp",EDGE,"E27.rect.bottom")])],"isStart":false});
            var Q9;
            Q9=makeQuery(id+"F1.opExtrude","SWEPT_EDGE",EDGE,{"disambiguationData":[OSD([sQuery(id+"F0.wireOp",EDGE,"E27.rect.bottom"),sQuery(id+"F0.wireOp",EDGE,"E27.rect.left")])]});
            var Q10;
            Q10=makeQuery(id+"F1.opExtrude","CAP_EDGE",EDGE,{"disambiguationData":[OSD([sQuery(id+"F0.wireOp",EDGE,"E27.rect.left")])],"isStart":false});
            var Q11;
            {var subQ0=sQuery(id+"F0.wireOp",EDGE,"E27.rect.top");Q11=makeQuery(id+"F1.opExtrude","CAP_EDGE",EDGE,{"disambiguationData":[OSD([subQ0]),TDD([makeQuery(id+"F0.imprint","IMPRINT",EDGE,{"disambiguationData":[TD([[makeQuery(id+"F0.imprint","INTERSECT",VERTEX,{"derivedFrom":[subQ0,sQuery(id+"F0.wireOp",EDGE,"E27.rect.left")]}),-1.0]])],"derivedFrom":subQ0})])],"isStart":false});}
            var Q12;
            {var subQ0=sQuery(id+"F0.wireOp",EDGE,"E27.rect.top");Q12=makeQuery(id+"F1.opExtrude","CAP_EDGE",EDGE,{"disambiguationData":[OSD([subQ0]),TDD([makeQuery(id+"F0.imprint","IMPRINT",EDGE,{"disambiguationData":[TD([[makeQuery(id+"F0.imprint","INTERSECT",VERTEX,{"derivedFrom":[subQ0,sQuery(id+"F0.wireOp",EDGE,"E27.rect.right")]}),1.0]])],"derivedFrom":subQ0})])],"isStart":false});}
            var Q13;
            Q13=makeQuery(id+"F1.opExtrude","SWEPT_EDGE",EDGE,{"disambiguationData":[OSD([sQuery(id+"F0.wireOp",EDGE,"E27.rect.top"),sQuery(id+"F0.wireOp",EDGE,"E27.rect.left")])]});
            var Q14;
            Q14=makeQuery(id+"F1.opExtrude","SWEPT_EDGE",EDGE,{"disambiguationData":[OSD([sQuery(id+"F0.wireOp",EDGE,"E30.rect.bottom"),sQuery(id+"F0.wireOp",EDGE,"E30.rect.right")])]});
            var Q15;
            Q15=makeQuery(id+"F1.opExtrude","CAP_EDGE",EDGE,{"disambiguationData":[OSD([sQuery(id+"F0.wireOp",EDGE,"E30.rect.bottom")])],"isStart":false});
            var Q16;
            Q16=makeQuery(id+"F1.opExtrude","SWEPT_EDGE",EDGE,{"disambiguationData":[OSD([sQuery(id+"F0.wireOp",EDGE,"E30.rect.bottom"),sQuery(id+"F0.wireOp",EDGE,"E30.rect.left")])]});
            var Q17;
            Q17=makeQuery(id+"F1.opExtrude","CAP_EDGE",EDGE,{"disambiguationData":[OSD([sQuery(id+"F0.wireOp",EDGE,"E30.rect.bottom")])],"isStart":true});
            var Q18;
            Q18=makeQuery(id+"F1.opExtrude","CAP_EDGE",EDGE,{"disambiguationData":[OSD([sQuery(id+"F0.wireOp",EDGE,"E30.rect.right")])],"isStart":false});
            var Q19;
            Q19=makeQuery(id+"F1.opExtrude","CAP_EDGE",EDGE,{"disambiguationData":[OSD([sQuery(id+"F0.wireOp",EDGE,"E30.rect.left")])],"isStart":false});
            var Q20;
            Q20=makeQuery(id+"F1.opExtrude","CAP_EDGE",EDGE,{"disambiguationData":[OSD([sQuery(id+"F0.wireOp",EDGE,"E30.rect.right")])],"isStart":true});
            var Q21;
            Q21=makeQuery(id+"F1.opExtrude","CAP_EDGE",EDGE,{"disambiguationData":[OSD([sQuery(id+"F0.wireOp",EDGE,"E30.rect.left")])],"isStart":true});
            var Q22;
            {var subQ0=sQuery(id+"F0.wireOp",EDGE,"E30.rect.top");Q22=makeQuery(id+"F1.opExtrude","CAP_EDGE",EDGE,{"disambiguationData":[OSD([subQ0]),TDD([makeQuery(id+"F0.imprint","IMPRINT",EDGE,{"disambiguationData":[TD([[makeQuery(id+"F0.imprint","INTERSECT",VERTEX,{"derivedFrom":[subQ0,sQuery(id+"F0.wireOp",EDGE,"E30.rect.right")]}),1.0]])],"derivedFrom":subQ0})])],"isStart":false});}
            var Q23;
            Q23=makeQuery(id+"F1.opExtrude","SWEPT_EDGE",EDGE,{"disambiguationData":[OSD([sQuery(id+"F0.wireOp",EDGE,"E30.rect.top"),sQuery(id+"F0.wireOp",EDGE,"E30.rect.right")])]});
            var Q24;
            {var subQ0=sQuery(id+"F0.wireOp",EDGE,"E30.rect.top");Q24=makeQuery(id+"F1.opExtrude","CAP_EDGE",EDGE,{"disambiguationData":[OSD([subQ0]),TDD([makeQuery(id+"F0.imprint","IMPRINT",EDGE,{"disambiguationData":[TD([[makeQuery(id+"F0.imprint","INTERSECT",VERTEX,{"derivedFrom":[subQ0,sQuery(id+"F0.wireOp",EDGE,"E30.rect.left")]}),-1.0]])],"derivedFrom":subQ0})])],"isStart":false});}
            var Q25;
            Q25=makeQuery(id+"F1.opExtrude","SWEPT_EDGE",EDGE,{"disambiguationData":[OSD([sQuery(id+"F0.wireOp",EDGE,"E30.rect.top"),sQuery(id+"F0.wireOp",EDGE,"E30.rect.left")])]});
            var Q26;
            {var subQ0=sQuery(id+"F0.wireOp",EDGE,"E30.rect.top");Q26=makeQuery(id+"F1.opExtrude","CAP_EDGE",EDGE,{"disambiguationData":[OSD([subQ0]),TDD([makeQuery(id+"F0.imprint","IMPRINT",EDGE,{"disambiguationData":[TD([[makeQuery(id+"F0.imprint","INTERSECT",VERTEX,{"derivedFrom":[subQ0,sQuery(id+"F0.wireOp",EDGE,"E30.rect.left")]}),-1.0]])],"derivedFrom":subQ0})])],"isStart":true});}
            var Q27;
            {var subQ0=sQuery(id+"F0.wireOp",EDGE,"E30.rect.top");Q27=makeQuery(id+"F1.opExtrude","CAP_EDGE",EDGE,{"disambiguationData":[OSD([subQ0]),TDD([makeQuery(id+"F0.imprint","IMPRINT",EDGE,{"disambiguationData":[TD([[makeQuery(id+"F0.imprint","INTERSECT",VERTEX,{"derivedFrom":[subQ0,sQuery(id+"F0.wireOp",EDGE,"E30.rect.right")]}),1.0]])],"derivedFrom":subQ0})])],"isStart":true});}
            var Q28;
            Q28=makeQuery(id+"F1.opExtrude","CAP_EDGE",EDGE,{"disambiguationData":[OSD([sQuery(id+"F0.wireOp",EDGE,"E28.rect.bottom")])],"isStart":true});
            var Q29;
            Q29=makeQuery(id+"F1.opExtrude","CAP_EDGE",EDGE,{"disambiguationData":[OSD([sQuery(id+"F0.wireOp",EDGE,"E28.rect.right")])],"isStart":true});
            var Q30;
            Q30=makeQuery(id+"F1.opExtrude","CAP_EDGE",EDGE,{"disambiguationData":[OSD([sQuery(id+"F0.wireOp",EDGE,"E28.rect.left")])],"isStart":true});
            var Q31;
            Q31=makeQuery(id+"F1.opExtrude","SWEPT_EDGE",EDGE,{"disambiguationData":[OSD([sQuery(id+"F0.wireOp",EDGE,"E28.rect.bottom"),sQuery(id+"F0.wireOp",EDGE,"E28.rect.left")])]});
            var Q32;
            Q32=makeQuery(id+"F1.opExtrude","SWEPT_EDGE",EDGE,{"disambiguationData":[OSD([sQuery(id+"F0.wireOp",EDGE,"E28.rect.bottom"),sQuery(id+"F0.wireOp",EDGE,"E28.rect.right")])]});
            var Q33;
            Q33=makeQuery(id+"F1.opExtrude","CAP_EDGE",EDGE,{"disambiguationData":[OSD([sQuery(id+"F0.wireOp",EDGE,"E28.rect.bottom")])],"isStart":false});
            var Q34;
            Q34=makeQuery(id+"F1.opExtrude","CAP_EDGE",EDGE,{"disambiguationData":[OSD([sQuery(id+"F0.wireOp",EDGE,"E28.rect.left")])],"isStart":false});
            var Q35;
            Q35=makeQuery(id+"F1.opExtrude","CAP_EDGE",EDGE,{"disambiguationData":[OSD([sQuery(id+"F0.wireOp",EDGE,"E28.rect.right")])],"isStart":false});
            var Q36;
            Q36=makeQuery(id+"F1.opExtrude","SWEPT_EDGE",EDGE,{"disambiguationData":[OSD([sQuery(id+"F0.wireOp",EDGE,"E28.rect.top"),sQuery(id+"F0.wireOp",EDGE,"E28.rect.left")])]});
            var Q37;
            {var subQ0=sQuery(id+"F0.wireOp",EDGE,"E28.rect.top");Q37=makeQuery(id+"F1.opExtrude","CAP_EDGE",EDGE,{"disambiguationData":[OSD([subQ0]),TDD([makeQuery(id+"F0.imprint","IMPRINT",EDGE,{"disambiguationData":[TD([[makeQuery(id+"F0.imprint","INTERSECT",VERTEX,{"derivedFrom":[subQ0,sQuery(id+"F0.wireOp",EDGE,"E28.rect.left")]}),-1.0]])],"derivedFrom":subQ0})])],"isStart":false});}
            var Q38;
            {var subQ0=sQuery(id+"F0.wireOp",EDGE,"E28.rect.top");Q38=makeQuery(id+"F1.opExtrude","CAP_EDGE",EDGE,{"disambiguationData":[OSD([subQ0]),TDD([makeQuery(id+"F0.imprint","IMPRINT",EDGE,{"disambiguationData":[TD([[makeQuery(id+"F0.imprint","INTERSECT",VERTEX,{"derivedFrom":[subQ0,sQuery(id+"F0.wireOp",EDGE,"E28.rect.right")]}),1.0]])],"derivedFrom":subQ0})])],"isStart":false});}
            var Q39;
            Q39=makeQuery(id+"F1.opExtrude","SWEPT_EDGE",EDGE,{"disambiguationData":[OSD([sQuery(id+"F0.wireOp",EDGE,"E28.rect.top"),sQuery(id+"F0.wireOp",EDGE,"E28.rect.right")])]});
            var Q40;
            {var subQ0=sQuery(id+"F0.wireOp",EDGE,"E28.rect.top");Q40=makeQuery(id+"F1.opExtrude","CAP_EDGE",EDGE,{"disambiguationData":[OSD([subQ0]),TDD([makeQuery(id+"F0.imprint","IMPRINT",EDGE,{"disambiguationData":[TD([[makeQuery(id+"F0.imprint","INTERSECT",VERTEX,{"derivedFrom":[subQ0,sQuery(id+"F0.wireOp",EDGE,"E28.rect.left")]}),-1.0]])],"derivedFrom":subQ0})])],"isStart":true});}
            var Q41;
            {var subQ0=sQuery(id+"F0.wireOp",EDGE,"E28.rect.top");Q41=makeQuery(id+"F1.opExtrude","CAP_EDGE",EDGE,{"disambiguationData":[OSD([subQ0]),TDD([makeQuery(id+"F0.imprint","IMPRINT",EDGE,{"disambiguationData":[TD([[makeQuery(id+"F0.imprint","INTERSECT",VERTEX,{"derivedFrom":[subQ0,sQuery(id+"F0.wireOp",EDGE,"E28.rect.right")]}),1.0]])],"derivedFrom":subQ0})])],"isStart":true});}
            var Q42;
            Q42=makeQuery(id+"F1.opExtrude","CAP_EDGE",EDGE,{"disambiguationData":[OSD([sQuery(id+"F0.wireOp",EDGE,"E29.rect.top")])],"isStart":true});
            var Q43;
            Q43=makeQuery(id+"F1.opExtrude","CAP_EDGE",EDGE,{"disambiguationData":[OSD([sQuery(id+"F0.wireOp",EDGE,"E29.rect.left")])],"isStart":true});
            var Q44;
            {var subQ0=sQuery(id+"F0.wireOp",EDGE,"E29.rect.bottom");Q44=makeQuery(id+"F1.opExtrude","CAP_EDGE",EDGE,{"disambiguationData":[OSD([subQ0]),TDD([makeQuery(id+"F0.imprint","IMPRINT",EDGE,{"disambiguationData":[TD([[makeQuery(id+"F0.imprint","INTERSECT",VERTEX,{"derivedFrom":[subQ0,sQuery(id+"F0.wireOp",EDGE,"E29.rect.left")]}),-1.0]])],"derivedFrom":subQ0})])],"isStart":true});}
            var Q45;
            {var subQ0=sQuery(id+"F0.wireOp",EDGE,"E29.rect.bottom");Q45=makeQuery(id+"F1.opExtrude","CAP_EDGE",EDGE,{"disambiguationData":[OSD([subQ0]),TDD([makeQuery(id+"F0.imprint","IMPRINT",EDGE,{"disambiguationData":[TD([[makeQuery(id+"F0.imprint","INTERSECT",VERTEX,{"derivedFrom":[subQ0,sQuery(id+"F0.wireOp",EDGE,"E29.rect.right")]}),1.0]])],"derivedFrom":subQ0})])],"isStart":true});}
            var Q46;
            Q46=makeQuery(id+"F1.opExtrude","CAP_EDGE",EDGE,{"disambiguationData":[OSD([sQuery(id+"F0.wireOp",EDGE,"E29.rect.right")])],"isStart":true});
            var Q47;
            Q47=makeQuery(id+"F1.opExtrude","SWEPT_EDGE",EDGE,{"disambiguationData":[OSD([sQuery(id+"F0.wireOp",EDGE,"E29.rect.top"),sQuery(id+"F0.wireOp",EDGE,"E29.rect.left")])]});
            var Q48;
            Q48=makeQuery(id+"F1.opExtrude","SWEPT_EDGE",EDGE,{"disambiguationData":[OSD([sQuery(id+"F0.wireOp",EDGE,"E29.rect.top"),sQuery(id+"F0.wireOp",EDGE,"E29.rect.right")])]});
            var Q49;
            Q49=makeQuery(id+"F1.opExtrude","CAP_EDGE",EDGE,{"disambiguationData":[OSD([sQuery(id+"F0.wireOp",EDGE,"E29.rect.top")])],"isStart":false});
            var Q50;
            Q50=makeQuery(id+"F1.opExtrude","SWEPT_EDGE",EDGE,{"disambiguationData":[OSD([sQuery(id+"F0.wireOp",EDGE,"E29.rect.bottom"),sQuery(id+"F0.wireOp",EDGE,"E29.rect.left")])]});
            var Q51;
            Q51=makeQuery(id+"F1.opExtrude","SWEPT_EDGE",EDGE,{"disambiguationData":[OSD([sQuery(id+"F0.wireOp",EDGE,"E29.rect.bottom"),sQuery(id+"F0.wireOp",EDGE,"E29.rect.right")])]});
            var Q52;
            Q52=makeQuery(id+"F1.opExtrude","CAP_EDGE",EDGE,{"disambiguationData":[OSD([sQuery(id+"F0.wireOp",EDGE,"E29.rect.right")])],"isStart":false});
            var Q53;
            {var subQ0=sQuery(id+"F0.wireOp",EDGE,"E29.rect.bottom");Q53=makeQuery(id+"F1.opExtrude","CAP_EDGE",EDGE,{"disambiguationData":[OSD([subQ0]),TDD([makeQuery(id+"F0.imprint","IMPRINT",EDGE,{"disambiguationData":[TD([[makeQuery(id+"F0.imprint","INTERSECT",VERTEX,{"derivedFrom":[subQ0,sQuery(id+"F0.wireOp",EDGE,"E29.rect.right")]}),1.0]])],"derivedFrom":subQ0})])],"isStart":false});}
            var Q54;
            {var subQ0=sQuery(id+"F0.wireOp",EDGE,"E29.rect.bottom");Q54=makeQuery(id+"F1.opExtrude","CAP_EDGE",EDGE,{"disambiguationData":[OSD([subQ0]),TDD([makeQuery(id+"F0.imprint","IMPRINT",EDGE,{"disambiguationData":[TD([[makeQuery(id+"F0.imprint","INTERSECT",VERTEX,{"derivedFrom":[subQ0,sQuery(id+"F0.wireOp",EDGE,"E29.rect.left")]}),-1.0]])],"derivedFrom":subQ0})])],"isStart":false});}
            var Q55;
            Q55=makeQuery(id+"F1.opExtrude","CAP_EDGE",EDGE,{"disambiguationData":[OSD([sQuery(id+"F0.wireOp",EDGE,"E29.rect.left")])],"isStart":false});
            fillet(context, id + "F5", {"entities" : qUnion([Q0, Q1, Q2, Q3, Q4, Q5, Q6, Q7, Q8, Q9, Q10, Q11, Q12, Q13, Q14, Q15, Q16, Q17, Q18, Q19, Q20, Q21, Q22, Q23, Q24, Q25, Q26, Q27, Q28, Q29, Q30, Q31, Q32, Q33, Q34, Q35, Q36, Q37, Q38, Q39, Q40, Q41, Q42, Q43, Q44, Q45, Q46, Q47, Q48, Q49, Q50, Q51, Q52, Q53, Q54, Q55]), "radius" : 0.64 * mm, "tangentPropagation" : true, "allowEdgeOverflow" : false});
        }
        {
            var Q0;
            Q0=makeQuery(id+"F1.opExtrude","SWEPT_EDGE",EDGE,{"disambiguationData":[OSD([sQuery(id+"F0.wireOp",EDGE,"E26.left"),sQuery(id+"F0.wireOp",EDGE,"E28.rect.top")])]});
            var Q1;
            Q1=makeQuery(id+"F1.opExtrude","SWEPT_EDGE",EDGE,{"disambiguationData":[OSD([sQuery(id+"F0.wireOp",EDGE,"E26.right"),sQuery(id+"F0.wireOp",EDGE,"E28.rect.top")])]});
            var Q2;
            Q2=makeQuery(id+"F1.opExtrude","SWEPT_EDGE",EDGE,{"disambiguationData":[OSD([sQuery(id+"F0.wireOp",EDGE,"E23.left"),sQuery(id+"F0.wireOp",EDGE,"E27.rect.top")])]});
            var Q3;
            Q3=makeQuery(id+"F1.opExtrude","SWEPT_EDGE",EDGE,{"disambiguationData":[OSD([sQuery(id+"F0.wireOp",EDGE,"E23.right"),sQuery(id+"F0.wireOp",EDGE,"E27.rect.top")])]});
            var Q4;
            Q4=makeQuery(id+"F1.opExtrude","SWEPT_EDGE",EDGE,{"disambiguationData":[OSD([sQuery(id+"F0.wireOp",EDGE,"E25.left"),sQuery(id+"F0.wireOp",EDGE,"E29.rect.bottom")])]});
            var Q5;
            Q5=makeQuery(id+"F1.opExtrude","SWEPT_EDGE",EDGE,{"disambiguationData":[OSD([sQuery(id+"F0.wireOp",EDGE,"E24.right"),sQuery(id+"F0.wireOp",EDGE,"E30.rect.top")])]});
            var Q6;
            Q6=makeQuery(id+"F1.opExtrude","SWEPT_EDGE",EDGE,{"disambiguationData":[OSD([sQuery(id+"F0.wireOp",EDGE,"E24.left"),sQuery(id+"F0.wireOp",EDGE,"E30.rect.top")])]});
            var Q7;
            Q7=makeQuery(id+"F1.opExtrude","SWEPT_EDGE",EDGE,{"disambiguationData":[OSD([sQuery(id+"F0.wireOp",EDGE,"E25.right"),sQuery(id+"F0.wireOp",EDGE,"E29.rect.bottom")])]});
            var Q8;
            Q8=makeQuery(id+"F1.opExtrude","SWEPT_EDGE",EDGE,{"disambiguationData":[OSD([sQuery(id+"F0.wireOp",EDGE,"E17.rect.bottom"),sQuery(id+"F0.wireOp",EDGE,"E23.bottom"),sQuery(id+"F0.wireOp",EDGE,"E23.right")])]});
            var Q9;
            Q9=makeQuery(id+"F1.opExtrude","SWEPT_EDGE",EDGE,{"disambiguationData":[OSD([sQuery(id+"F0.wireOp",EDGE,"E17.rect.bottom"),sQuery(id+"F0.wireOp",EDGE,"E26.bottom"),sQuery(id+"F0.wireOp",EDGE,"E26.right")])]});
            var Q10;
            Q10=makeQuery(id+"F1.opExtrude","SWEPT_EDGE",EDGE,{"disambiguationData":[OSD([sQuery(id+"F0.wireOp",EDGE,"E17.rect.top"),sQuery(id+"F0.wireOp",EDGE,"E24.bottom"),sQuery(id+"F0.wireOp",EDGE,"E24.right")])]});
            var Q11;
            Q11=makeQuery(id+"F1.opExtrude","SWEPT_EDGE",EDGE,{"disambiguationData":[OSD([sQuery(id+"F0.wireOp",EDGE,"E17.rect.top"),sQuery(id+"F0.wireOp",EDGE,"E25.bottom"),sQuery(id+"F0.wireOp",EDGE,"E25.right")])]});
            fillet(context, id + "F6", {"entities" : qUnion([Q0, Q1, Q2, Q3, Q4, Q5, Q6, Q7, Q8, Q9, Q10, Q11]), "radius" : 0.5 * mm, "tangentPropagation" : true, "allowEdgeOverflow" : false});
        }
    });
